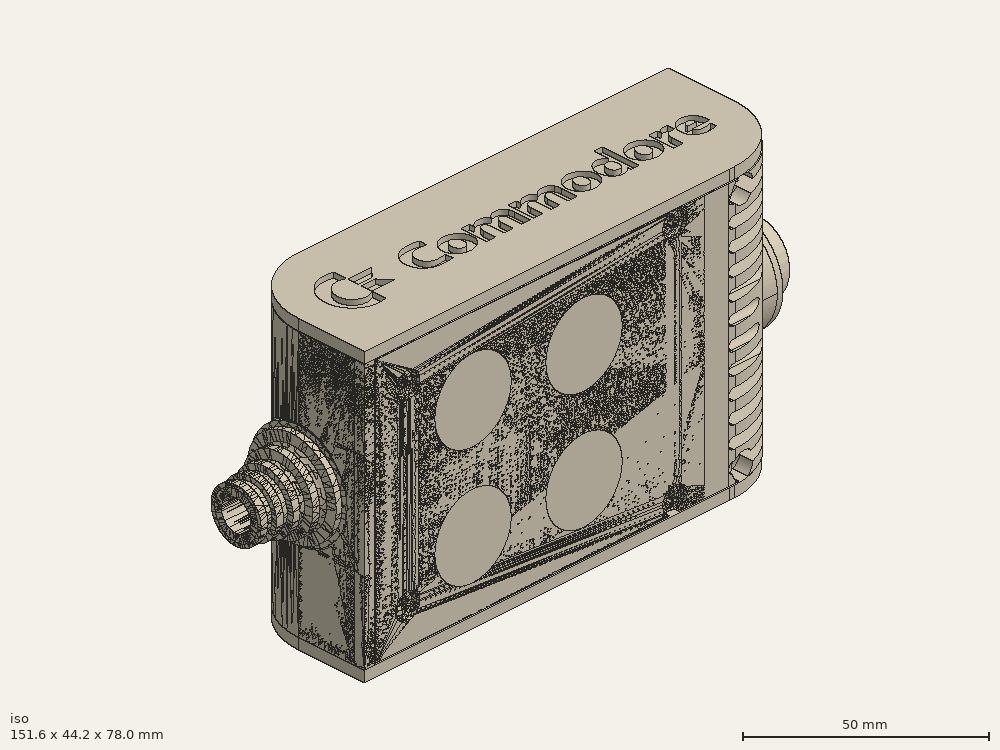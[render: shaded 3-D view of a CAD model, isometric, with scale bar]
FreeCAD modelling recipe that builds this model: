
FCSTD DOCUMENT  (FreeCAD 0.19R0.19.2)
Label: enclosure_215FCStd
License: All rights reserved
LicenseURL: http://en.wikipedia.org/wiki/All_rights_reserved
objects: Part::Revolution×152, Part::MultiFuse×146, Part::Feature×146, Sketcher::SketchObject×88, Part::Extrusion×73, Part::Cut×72, Part::Cylinder×70, Part::Fillet×58, Part::Box×36, App::MeasureDistance×4, Part::Chamfer×4, Part::FeaturePython×2, Image::ImagePlane×1, PartDesign::Body×1, Part::Mirroring×1
note: 849 computed .brp shape members not serialized (recipe doc carries the construction recipe); baked Part::Feature solids carry a one-line shape summary decoded from their .brp

FEATURE [Sketcher::SketchObject] Sketch  label="topSketch"
  FullyConstrained = true
  sketch-geometry (20):
    g0: LineSegment StartX=5.21097e-06 StartY=3 StartZ=0 EndX=5.21097e-06 EndY=19 EndZ=0
    g1: ArcOfCircle CenterX=19 CenterY=19 CenterZ=0 NormalX=0 NormalY=0 NormalZ=1 AngleXU=0 Radius=19 StartAngle=1.5708 EndAngle=3.14159
    g2: ArcOfCircle CenterX=19 CenterY=19 CenterZ=0 NormalX=0 NormalY=0 NormalZ=1 AngleXU=0 Radius=16 StartAngle=1.5708 EndAngle=3.14159
    g3: LineSegment StartX=114 StartY=35 StartZ=0 EndX=19 EndY=35 EndZ=0
    g4: LineSegment StartX=5.21097e-06 StartY=3 StartZ=0 EndX=5.21097e-06 EndY=0 EndZ=0
    g5: LineSegment StartX=3 StartY=0 StartZ=0 EndX=5.21097e-06 EndY=0 EndZ=0
    g6: LineSegment StartX=3 StartY=19 StartZ=0 EndX=3 EndY=0 EndZ=0
    g7: LineSegment StartX=19 StartY=38 StartZ=0 EndX=124 EndY=38 EndZ=0
    g8: Circle CenterX=119 CenterY=35 CenterZ=0 NormalX=0 NormalY=0 NormalZ=1 AngleXU=0 Radius=1
    g9: Circle CenterX=121 CenterY=35 CenterZ=0 NormalX=0 NormalY=0 NormalZ=1 AngleXU=0 Radius=1
    g10: Circle CenterX=121 CenterY=33 CenterZ=0 NormalX=0 NormalY=0 NormalZ=1 AngleXU=0 Radius=1
    g11: BSplineCurve PolesCount=3 KnotsCount=2 Degree=2 IsPeriodic=0
    g12: GeomPoint X=119 Y=35 Z=0
    g13: GeomPoint X=121 Y=33 Z=0
    g14: LineSegment StartX=119 StartY=35 StartZ=0 EndX=114 EndY=35 EndZ=0
    g15: ArcOfCircle CenterX=105 CenterY=19 CenterZ=0 NormalX=0 NormalY=0 NormalZ=1 AngleXU=0 Radius=19 StartAngle=5.7297 EndAngle=6.28319
    g16: ArcOfCircle CenterX=105 CenterY=19 CenterZ=0 NormalX=0 NormalY=0 NormalZ=1 AngleXU=0 Radius=16 StartAngle=5.60905 EndAngle=6.28319
    g17: LineSegment StartX=121 StartY=33 StartZ=0 EndX=121 EndY=19 EndZ=0
    g18: LineSegment StartX=124 StartY=38 StartZ=0 EndX=124 EndY=19 EndZ=0
    g19: LineSegment StartX=117.5 StartY=9.01251 StartZ=0 EndX=121.163 EndY=9.0125 EndZ=0
  constraints (46):
    c: Vertical(g0)
    c: Block(g0)
    c: Coincident(g1,g0)
    c: Block(g1)
    c: Coincident(g2,g1)
    c: Block(g2)
    c: Coincident(g3,g2)
    c: Horizontal(g3)
    c: Tangent(g3,g2)
    c: Coincident(g4,g0)
    c: Distance(g4) = 3
    c: Vertical(g4)
    c: Coincident(g5,g4)
    c: Horizontal(g5)
    c: Coincident(g6,g2)
    c: Coincident(g6,g5)
    c: Vertical(g6)
    c: Horizontal(g7)
    c: Distance(g7) = 105
    c: Coincident(g7,g1)
    c: Block(g3)
    c: Weight(g8) = 1
    c: Equal(g8,g9)
    c: Equal(g8,g10)
    c: InternalAlignment(g8,g11)
    c: InternalAlignment(g9,g11)
    c: InternalAlignment(g10,g11)
    c: InternalAlignment(g12,g11)
    c: InternalAlignment(g13,g11)
    c: Block(g11)
    c: Coincident(g14,g11)
    c: Coincident(g14,g3)
    c: Horizontal(g14)
    c: Block(g15)
    c: Coincident(g16,g15)
    c: Block(g16)
    c: Coincident(g17,g11)
    c: Coincident(g17,g16)
    c: Vertical(g17)
    c: Distance(g17) = 14
    c: Coincident(g18,g7)
    c: Coincident(g18,g15)
    c: Vertical(g18)
    c: Distance(g18) = 19
    c: Coincident(g19,g16)
    c: Coincident(g19,g15)
FEATURE [Sketcher::SketchObject] Sketch001  label="bottomSketch"
  FullyConstrained = true
  sketch-geometry (32):
    g0: LineSegment StartX=3.3 StartY=-6.03275e-07 StartZ=0 EndX=98 EndY=-6.03275e-07 EndZ=0
    g1: ArcOfCircle CenterX=98 CenterY=19 CenterZ=0 NormalX=0 NormalY=0 NormalZ=1 AngleXU=0 Radius=19 StartAngle=4.71239 EndAngle=5.71103
    g2: LineSegment StartX=6.3 StartY=8 StartZ=0 EndX=3.3 EndY=8 EndZ=0
    g3: LineSegment StartX=3.3 StartY=8 StartZ=0 EndX=3.3 EndY=-6.03275e-07 EndZ=0
    g4: ArcOfCircle CenterX=8.3 CenterY=5 CenterZ=0 NormalX=0 NormalY=0 NormalZ=1 AngleXU=0 Radius=2 StartAngle=3.14159 EndAngle=4.71239
    g5: LineSegment StartX=6.3 StartY=8 StartZ=0 EndX=6.3 EndY=5 EndZ=0
    g6: ArcOfCircle CenterX=98 CenterY=19 CenterZ=0 NormalX=0 NormalY=0 NormalZ=1 AngleXU=0 Radius=12.7 StartAngle=4.71239 EndAngle=6.28319
    g7: LineSegment StartX=94.7 StartY=3 StartZ=0 EndX=8.3 EndY=3 EndZ=0
    g8-g12: Circle x5 (B-spline internal-alignment scaffolding for g13; pole/knot coordinates omitted)
    g13: BSplineCurve PolesCount=5 KnotsCount=3 Degree=3 IsPeriodic=0
    g14: GeomPoint X=98 Y=6.3 Z=0
    g15: GeomPoint X=96.3938 Y=4.71946 Z=0
    g16: GeomPoint X=94.7 Y=3 Z=0
    g17-g23: Circle x7 (B-spline internal-alignment scaffolding for g24; pole/knot coordinates omitted)
    g24: BSplineCurve PolesCount=7 KnotsCount=5 Degree=3 IsPeriodic=0
    g25-g29: GeomPoint x5 (B-spline internal-alignment scaffolding for g24; pole/knot coordinates omitted)
    g30: ArcOfCircle CenterX=98 CenterY=19 CenterZ=0 NormalX=0 NormalY=0 NormalZ=1 AngleXU=0 Radius=15.7 StartAngle=5.81226 EndAngle=6.28319
    g31: LineSegment StartX=110.7 StartY=19 StartZ=0 EndX=113.7 EndY=19 EndZ=0
  constraints (41):
    c: Horizontal(g0)
    c: Coincident(g1,g0)
    c: Block(g1)
    c: Horizontal(g2)
    c: Distance(g2) = 3
    c: Coincident(g3,g2)
    c: Vertical(g3)
    c: Coincident(g3,g0)
    c: Block(g4)
    c: Block(g2)
    c: Coincident(g5,g2)
    c: Coincident(g5,g4)
    c: Vertical(g5)
    c: Coincident(g6,g1)
    c: Block(g6)
    c: Coincident(g7,g4)
    c: Horizontal(g7)
    c: Block(g0)
    c: Block(g7)
    c: Block(g3)
    c: Coincident(g13,g6)
    c: Weight(g8) = 1
    c: Equal(g8, g9-g12) x4
    c: Coincident(g13,g7)
    c: InternalAlignment(g8-g12 -> g13) x5
    c: InternalAlignment(g14,g13)
    c: InternalAlignment(g15,g13)
    c: InternalAlignment(g16,g13)
    c: Block(g13)
    c: Weight(g17) = 1
    c: Equal(g17, g18-g23) x6
    c: Coincident(g24,g1)
    c: InternalAlignment(g17-g23 -> g24) x7
    c: InternalAlignment(g25-g29 -> g24) x5
    c: Block(g24)
    c: Coincident(g30,g24)
    c: Coincident(g31,g6)
    c: Coincident(g31,g30)
    c: Horizontal(g31)
    c: Block(g31)
    c: Block(g30)
FEATURE [Part::Extrusion] Extrude  label="top"
  Base = -> Sketch
  Dir = (0,0,1)
  DirMode = 2
  FaceMakerClass = Part::FaceMakerBullseye
  LengthFwd = 72
  LengthRev = 0
  Solid = true
  Symmetric = false
FEATURE [Part::Extrusion] Extrude001  label="bottom"
  Base = -> Sketch001
  Dir = (0,0,1)
  DirMode = 2
  FaceMakerClass = Part::FaceMakerBullseye
  LengthFwd = 71.4
  LengthRev = 0
  Placement = pos=(0,0,0.3) rot=(0,0,1;0rad)
  Solid = true
  Symmetric = false
FEATURE [Sketcher::SketchObject] Sketch002  label="topSketch001"
  FullyConstrained = true
  sketch-geometry (8):
    g0: ArcOfCircle CenterX=19 CenterY=19.0975 CenterZ=0 NormalX=0 NormalY=0 NormalZ=1 AngleXU=0 Radius=18.9025 StartAngle=1.5708 EndAngle=3.14674
    g1: LineSegment StartX=0.0977805 StartY=19.0003 StartZ=0 EndX=0.0977805 EndY=0.000251602 EndZ=0
    g2: LineSegment StartX=19 StartY=38 StartZ=0 EndX=124 EndY=38 EndZ=0
    g3: LineSegment StartX=0.0977805 StartY=0.000251602 StartZ=0 EndX=105.098 EndY=0.000251602 EndZ=0
    g4: LineSegment StartX=124 StartY=38 StartZ=0 EndX=125.616 EndY=38 EndZ=0
    g5: LineSegment StartX=105.098 StartY=0.000251602 StartZ=0 EndX=106.713 EndY=0.000251602 EndZ=0
    g6: ArcOfCircle CenterX=106.616 CenterY=19 CenterZ=0 NormalX=0 NormalY=0 NormalZ=1 AngleXU=0 Radius=19 StartAngle=4.71754 EndAngle=6.28319
    g7: LineSegment StartX=125.616 StartY=38 StartZ=0 EndX=125.616 EndY=19 EndZ=0
  constraints (21):
    c: Block(g0)
    c: Coincident(g1,g0)
    c: Vertical(g1)
    c: Horizontal(g2)
    c: Distance(g2) = 105
    c: Coincident(g2,g0)
    c: Distance(g1) = 19
    c: Coincident(g3,g1)
    c: Horizontal(g3)
    c: Distance(g3) = 105
    c: Coincident(g4,g2)
    c: Horizontal(g4)
    c: Distance(g4) = 1.61553
    c: Horizontal(g5)
    c: Equal(g4,g5) = 1.61553
    c: Coincident(g5,g3)
    c: Block(g6)
    c: Coincident(g6,g5)
    c: Coincident(g7,g4)
    c: Coincident(g7,g6)
    c: Vertical(g7)
FEATURE [Part::Extrusion] Extrude002  label="sideA"
  Base = -> Sketch002
  Dir = (0,0,1)
  DirMode = 2
  FaceMakerClass = Part::FaceMakerBullseye
  LengthFwd = 3
  LengthRev = 0
  Placement = pos=(0,0,-3) rot=(0,0,1;0rad)
  Solid = true
  Symmetric = false
FEATURE [Sketcher::SketchObject] Sketch003  label="topSketch002"
  FullyConstrained = true
  sketch-geometry (6):
    g0: LineSegment StartX=19 StartY=38 StartZ=0 EndX=117 EndY=38 EndZ=0
    g1: ArcOfCircle CenterX=19 CenterY=19 CenterZ=0 NormalX=0 NormalY=0 NormalZ=1 AngleXU=0 Radius=19 StartAngle=1.5708 EndAngle=3.14159
    g2: LineSegment StartX=117 StartY=38 StartZ=0 EndX=117 EndY=19 EndZ=0
    g3: LineSegment StartX=98 StartY=1.0161e-12 StartZ=0 EndX=5.22862e-06 EndY=1.0161e-12 EndZ=0
    g4: LineSegment StartX=5.22862e-06 StartY=19 StartZ=0 EndX=5.22862e-06 EndY=1.0161e-12 EndZ=0
    g5: ArcOfCircle CenterX=98 CenterY=19 CenterZ=0 NormalX=0 NormalY=0 NormalZ=1 AngleXU=0 Radius=19 StartAngle=4.71239 EndAngle=6.28319
  constraints (16):
    c: Horizontal(g0)
    c: Distance(g0) = 98
    c: Coincident(g1,g0)
    c: Block(g1)
    c: Coincident(g2,g0)
    c: Vertical(g2)
    c: Distance(g2) = 19
    c: Horizontal(g3)
    c: Coincident(g4,g1)
    c: Vertical(g4)
    c: Coincident(g3,g4)
    c: Block(g3)
    c: Coincident(g5,g2)
    c: Coincident(g5,g3)
    c: Block(g0)
    c: Block(g5)
FEATURE [Sketcher::SketchObject] Sketch004
  FullyConstrained = true
  MapMode = 3
  Placement = pos=(0,0,0) rot=(1,0,0;1.5708rad)
  Support = -> [Extrude]
  sketch-geometry (8):
    g0: Circle CenterX=80.351 CenterY=-67.6202 CenterZ=0 NormalX=0 NormalY=0 NormalZ=1 AngleXU=0 Radius=2
    g1: Circle CenterX=80.351 CenterY=-67.6202 CenterZ=0 NormalX=0 NormalY=0 NormalZ=1 AngleXU=0 Radius=3
    g2: Circle CenterX=80.351 CenterY=-4.92017 CenterZ=0 NormalX=0 NormalY=0 NormalZ=1 AngleXU=0 Radius=2
    g3: Circle CenterX=80.351 CenterY=-4.92017 CenterZ=0 NormalX=0 NormalY=0 NormalZ=1 AngleXU=0 Radius=3
    g4: Circle CenterX=23.851 CenterY=-4.92017 CenterZ=0 NormalX=0 NormalY=0 NormalZ=1 AngleXU=0 Radius=2
    g5: Circle CenterX=23.851 CenterY=-4.92017 CenterZ=0 NormalX=0 NormalY=0 NormalZ=1 AngleXU=0 Radius=3
    g6: Circle CenterX=23.851 CenterY=-67.6202 CenterZ=0 NormalX=0 NormalY=0 NormalZ=1 AngleXU=0 Radius=2
    g7: Circle CenterX=23.851 CenterY=-67.6202 CenterZ=0 NormalX=0 NormalY=0 NormalZ=1 AngleXU=0 Radius=3
  constraints (8):
    c: Block(g3)
    c: Block(g2)
    c: Block(g1)
    c: Block(g0)
    c: Block(g6)
    c: Block(g7)
    c: Block(g4)
    c: Block(g5)
FEATURE [Part::Extrusion] Extrude004
  Base = -> Sketch004
  Dir = (0,-1,2e-16)
  DirMode = 2
  FaceMakerClass = Part::FaceMakerBullseye
  LengthFwd = 6
  LengthRev = 0
  Placement = pos=(0,9,0) rot=(0,0,1;0rad)
  Solid = true
  Symmetric = false
FEATURE [Sketcher::SketchObject] Sketch005
  FullyConstrained = true
  MapMode = 3
  Placement = pos=(0,0,0) rot=(1,0,0;1.5708rad)
  Support = -> [Extrude]
  sketch-geometry (8):
    g0: Circle CenterX=80.351 CenterY=-67.6202 CenterZ=0 NormalX=0 NormalY=0 NormalZ=1 AngleXU=0 Radius=3
    g1: Circle CenterX=80.351 CenterY=-4.92017 CenterZ=0 NormalX=0 NormalY=0 NormalZ=1 AngleXU=0 Radius=3
    g2: Circle CenterX=23.851 CenterY=-4.92017 CenterZ=0 NormalX=0 NormalY=0 NormalZ=1 AngleXU=0 Radius=3
    g3: Circle CenterX=23.851 CenterY=-67.6202 CenterZ=0 NormalX=0 NormalY=0 NormalZ=1 AngleXU=0 Radius=3
    g4: Circle CenterX=23.851 CenterY=-67.6202 CenterZ=0 NormalX=0 NormalY=0 NormalZ=1 AngleXU=0 Radius=5
    g5: Circle CenterX=80.351 CenterY=-67.6202 CenterZ=0 NormalX=0 NormalY=0 NormalZ=1 AngleXU=0 Radius=5
    g6: Circle CenterX=23.851 CenterY=-4.92017 CenterZ=0 NormalX=0 NormalY=0 NormalZ=1 AngleXU=0 Radius=5
    g7: Circle CenterX=80.351 CenterY=-4.92017 CenterZ=0 NormalX=0 NormalY=0 NormalZ=1 AngleXU=0 Radius=5
  constraints (8):
    c: Block(g1)
    c: Block(g0)
    c: Block(g3)
    c: Block(g2)
    c: Block(g5)
    c: Block(g4)
    c: Block(g6)
    c: Block(g7)
FEATURE [Part::Extrusion] Extrude005
  Base = -> Sketch005
  Dir = (0,-1,2e-16)
  DirMode = 2
  FaceMakerClass = Part::FaceMakerBullseye
  LengthFwd = 2
  LengthRev = 0
  Solid = true
  Symmetric = false
FEATURE [Sketcher::SketchObject] Sketch006
  FullyConstrained = true
  MapMode = 3
  Placement = pos=(0,0,0) rot=(1,0,0;1.5708rad)
  sketch-geometry (8):
    g0: Circle CenterX=80.351 CenterY=-67.6202 CenterZ=0 NormalX=0 NormalY=0 NormalZ=1 AngleXU=0 Radius=3
    g1: Circle CenterX=80.351 CenterY=-4.92017 CenterZ=0 NormalX=0 NormalY=0 NormalZ=1 AngleXU=0 Radius=3
    g2: Circle CenterX=23.851 CenterY=-4.92017 CenterZ=0 NormalX=0 NormalY=0 NormalZ=1 AngleXU=0 Radius=3
    g3: Circle CenterX=23.851 CenterY=-67.6202 CenterZ=0 NormalX=0 NormalY=0 NormalZ=1 AngleXU=0 Radius=3
    g4: Circle CenterX=23.851 CenterY=-67.6202 CenterZ=0 NormalX=0 NormalY=0 NormalZ=1 AngleXU=0 Radius=5
    g5: Circle CenterX=80.351 CenterY=-67.6202 CenterZ=0 NormalX=0 NormalY=0 NormalZ=1 AngleXU=0 Radius=5
    g6: Circle CenterX=23.851 CenterY=-4.92017 CenterZ=0 NormalX=0 NormalY=0 NormalZ=1 AngleXU=0 Radius=5
    g7: Circle CenterX=80.351 CenterY=-4.92017 CenterZ=0 NormalX=0 NormalY=0 NormalZ=1 AngleXU=0 Radius=5
  constraints (8):
    c: Block(g1)
    c: Block(g0)
    c: Block(g3)
    c: Block(g2)
    c: Block(g5)
    c: Block(g4)
    c: Block(g6)
    c: Block(g7)
FEATURE [Part::Extrusion] Extrude007
  Base = -> Sketch006
  Dir = (0,-1,2e-16)
  DirMode = 2
  FaceMakerClass = Part::FaceMakerBullseye
  LengthFwd = 2
  LengthRev = 0
  Solid = true
  Symmetric = false
FEATURE [Part::Fillet] Fillet
  Base = -> Extrude007
  Edges = 4 edges r=1.99: [Edge6,Edge12,Edge18,Edge24]
FEATURE [Part::Cut] Cut
  Base = -> Extrude005
  Placement = pos=(0,5,0) rot=(0,0,1;0rad)
  Tool = -> Fillet
FEATURE [Part::MultiFuse] Fusion  label="pCBScrews"
  Placement = pos=(-2.5,0,72.3) rot=(0,0,1;0rad)
  Shapes = -> [Extrude004,Cut]
FEATURE [App::MeasureDistance] Distance  label="Distance: 0.69 mm"
  Distance = 0.685967
  P1 = (24.0138,2.9647,0.3)
  P2 = (23.8901,3,-0.373787)
FEATURE [App::MeasureDistance] Distance001  label="Distance: 0.53 mm"
  Distance = 0.533607
  P1 = (80.2939,3,72.2334)
  P2 = (80.281,2.99661,71.7)
FEATURE [Part::Fillet] Fillet001
  Base = -> Extrude001
  Edges = 1 edges r=2.4: [Edge17]
FEATURE [Part::Fillet] Fillet002  label="bottom001"
  Base = -> Fillet001
  Edges = 1 edges r=2.4: [Edge36]
FEATURE [Part::Fillet] Fillet003  label="top001"
  Base = -> Extrude
  Edges = 1 edges r=2: [Edge1]
FEATURE [Sketcher::SketchObject] Sketch007
  FullyConstrained = true
  sketch-geometry (16):
    g0: LineSegment StartX=4 StartY=0 StartZ=0 EndX=4 EndY=2.4 EndZ=0
    g1: LineSegment StartX=4 StartY=2.4 StartZ=0 EndX=7 EndY=2.4 EndZ=0
    g2: LineSegment StartX=4 StartY=0 StartZ=0 EndX=5.7 EndY=0 EndZ=0
    g3: LineSegment StartX=5.7 StartY=0 StartZ=0 EndX=5.7 EndY=-5.6 EndZ=0
    g4-g8: Circle x5 (B-spline internal-alignment scaffolding for g9; pole/knot coordinates omitted)
    g9: BSplineCurve PolesCount=5 KnotsCount=3 Degree=3 IsPeriodic=0
    g10: GeomPoint X=7 Y=2.4 Z=0
    g11: GeomPoint X=10.4582 Y=-1.55472 Z=0
    g12: GeomPoint X=14 Y=-5.6 Z=0
    g13: LineSegment StartX=14 StartY=-5.6 StartZ=0 EndX=14 EndY=-14.1 EndZ=0
    g14: LineSegment StartX=14 StartY=-14.1 StartZ=0 EndX=6.5 EndY=-14.1 EndZ=0
    g15: LineSegment StartX=5.7 StartY=-5.6 StartZ=0 EndX=6.5 EndY=-14.1 EndZ=0
  constraints (28):
    c: Distance(g0) = 2.4
    c: Vertical(g0)
    c: Block(g0)
    c: Coincident(g1,g0)
    c: Horizontal(g1)
    c: Distance(g1) = 3
    c: Coincident(g2,g0)
    c: Horizontal(g2)
    c: Distance(g2) = 1.7
    c: Coincident(g3,g2)
    c: Vertical(g3)
    c: Distance(g3) = 5.6
    c: Coincident(g9,g1)
    c: Weight(g4) = 1
    c: Equal(g4, g5-g8) x4
    c: InternalAlignment(g4-g8 -> g9) x5
    c: InternalAlignment(g10,g9)
    c: InternalAlignment(g11,g9)
    c: InternalAlignment(g12,g9)
    c: Block(g9)
    c: Coincident(g13,g9)
    c: Vertical(g13)
    c: Distance(g13) = 8.5
    c: Coincident(g14,g13)
    c: Horizontal(g14)
    c: Distance(g14) = 7.5
    c: Coincident(g15,g3)
    c: Coincident(g15,g14)
FEATURE [Part::Feature] Face
  shape: bbox 10 x 16.5 x 2e-07 mm, 1 faces, 0 solids (baked)
FEATURE [Part::Revolution] Revolve  label="plugHousing"
  Angle = 360
  Axis = (0,1,0)
  Base = (0,0,0)
  FaceMakerClass = Part::FaceMakerBullseye
  Placement = pos=(0,0,36.15) rot=(0,0,1;0rad)
  Solid = false
  Source = -> Face
  Symmetric = false
FEATURE [Part::Feature] Face001
  shape: bbox 10 x 16.5 x 2e-07 mm, 1 faces, 0 solids (baked)
FEATURE [Part::Revolution] Revolve001  label="plugHousing001"
  Angle = 360
  Axis = (0,1,0)
  Base = (0,0,0)
  FaceMakerClass = Part::FaceMakerBullseye
  Placement = pos=(0,0,36.15) rot=(0,0,1;0rad)
  Solid = false
  Source = -> Face001
  Symmetric = false
FEATURE [Part::MultiFuse] Fusion001  label="plugHousing002"
  Placement = pos=(0,0,0) rot=(0,0,1;1.5708rad)
  Shapes = -> [Revolve001,Revolve]
FEATURE [Part::Feature] Face002
  shape: bbox 10 x 16.5 x 2e-07 mm, 1 faces, 0 solids (baked)
FEATURE [Part::Revolution] Revolve003  label="plugHousing005"
  Angle = 360
  Axis = (0,1,0)
  Base = (0,0,0)
  FaceMakerClass = Part::FaceMakerBullseye
  Placement = pos=(0,0,36.15) rot=(0,0,1;0rad)
  Solid = false
  Source = -> Face002
  Symmetric = false
FEATURE [Part::Feature] Face003
  shape: bbox 10 x 16.5 x 2e-07 mm, 1 faces, 0 solids (baked)
FEATURE [Part::Revolution] Revolve002  label="plugHousing003"
  Angle = 360
  Axis = (0,1,0)
  Base = (0,0,0)
  FaceMakerClass = Part::FaceMakerBullseye
  Placement = pos=(0,0,36.15) rot=(0,0,1;0rad)
  Solid = false
  Source = -> Face003
  Symmetric = false
FEATURE [Part::MultiFuse] Fusion002  label="plugHousing004"
  Placement = pos=(0,0,0) rot=(0,0,1;1.5708rad)
  Shapes = -> [Revolve002,Revolve003]
FEATURE [Part::MultiFuse] Fusion003  label="plugHousing006"
  Placement = pos=(0,19,0) rot=(0,0,1;3.14159rad)
  Shapes = -> [Fusion002,Fusion001]
FEATURE [Part::Feature] Face004
  shape: bbox 10 x 16.5 x 2e-07 mm, 1 faces, 0 solids (baked)
FEATURE [Part::Revolution] Revolve006  label="plugHousing010"
  Angle = 360
  Axis = (0,1,0)
  Base = (0,0,0)
  FaceMakerClass = Part::FaceMakerBullseye
  Placement = pos=(0,0,36.15) rot=(0,0,1;0rad)
  Solid = false
  Source = -> Face004
  Symmetric = false
FEATURE [Part::Feature] Face005
  shape: bbox 10 x 16.5 x 2e-07 mm, 1 faces, 0 solids (baked)
FEATURE [Part::Revolution] Revolve007  label="plugHousing011"
  Angle = 360
  Axis = (0,1,0)
  Base = (0,0,0)
  FaceMakerClass = Part::FaceMakerBullseye
  Placement = pos=(0,0,36.15) rot=(0,0,1;0rad)
  Solid = false
  Source = -> Face005
  Symmetric = false
FEATURE [Part::Feature] Face006
  shape: bbox 10 x 16.5 x 2e-07 mm, 1 faces, 0 solids (baked)
FEATURE [Part::Revolution] Revolve004  label="plugHousing007"
  Angle = 360
  Axis = (0,1,0)
  Base = (0,0,0)
  FaceMakerClass = Part::FaceMakerBullseye
  Placement = pos=(0,0,36.15) rot=(0,0,1;0rad)
  Solid = false
  Source = -> Face006
  Symmetric = false
FEATURE [Part::MultiFuse] Fusion004  label="plugHousing009"
  Placement = pos=(0,0,0) rot=(0,0,1;1.5708rad)
  Shapes = -> [Revolve004,Revolve007]
FEATURE [Part::Feature] Face007
  shape: bbox 10 x 16.5 x 2e-07 mm, 1 faces, 0 solids (baked)
FEATURE [Part::Revolution] Revolve005  label="plugHousing008"
  Angle = 360
  Axis = (0,1,0)
  Base = (0,0,0)
  FaceMakerClass = Part::FaceMakerBullseye
  Placement = pos=(0,0,36.15) rot=(0,0,1;0rad)
  Solid = false
  Source = -> Face007
  Symmetric = false
FEATURE [Part::MultiFuse] Fusion005  label="plugHousing012"
  Placement = pos=(0,0,0) rot=(0,0,1;1.5708rad)
  Shapes = -> [Revolve006,Revolve005]
FEATURE [Part::MultiFuse] Fusion006  label="plugHousing013"
  Placement = pos=(0,19,0) rot=(0,0,1;3.14159rad)
  Shapes = -> [Fusion005,Fusion004]
FEATURE [Part::MultiFuse] Fusion007  label="plugHousing014"
  Placement = pos=(122.621,0,-0.15) rot=(0,0,1;0rad)
  Shapes = -> [Fusion003,Fusion006]
FEATURE [Part::Cylinder] Cylinder002
  Angle = 360
  AttacherType = Attacher::AttachEngine3D
  Height = 20
  Placement = pos=(0,0,36.15) rot=(0,0,1;0rad)
  Radius = 4
FEATURE [Part::Cylinder] Cylinder003
  Angle = 360
  AttacherType = Attacher::AttachEngine3D
  Height = 10
  Placement = pos=(0,0,36.15) rot=(0,0,1;0rad)
  Radius = 4
FEATURE [Part::MultiFuse] Fusion009  label="removeToCreateHoleForPlugHousing"
  Placement = pos=(70,19,36.15) rot=(0,1,0;1.5708rad)
  Shapes = -> [Cylinder002,Cylinder003]
FEATURE [Part::Cylinder] Cylinder004
  Angle = 360
  AttacherType = Attacher::AttachEngine3D
  Height = 20
  Placement = pos=(0,0,36.15) rot=(0,0,1;0rad)
  Radius = 4
FEATURE [Part::Cylinder] Cylinder005
  Angle = 360
  AttacherType = Attacher::AttachEngine3D
  Height = 10
  Placement = pos=(0,0,36.15) rot=(0,0,1;0rad)
  Radius = 4
FEATURE [Part::MultiFuse] Fusion010  label="removeToCreateHoleForPlugHousing001"
  Placement = pos=(70,19,36.15) rot=(0,1,0;1.5708rad)
  Shapes = -> [Cylinder004,Cylinder005]
FEATURE [Part::Cut] Cut001
  Base = -> Fillet003
  Tool = -> Fusion010
FEATURE [Part::Cut] Cut002  label="Bottom"
  Base = -> Fillet002
  Tool = -> Fusion009
FEATURE [Part::Feature] Face008
  shape: bbox 10 x 16.5 x 2e-07 mm, 1 faces, 0 solids (baked)
FEATURE [Part::Revolution] Revolve011  label="plugHousing021"
  Angle = 360
  Axis = (0,1,0)
  Base = (0,0,0)
  FaceMakerClass = Part::FaceMakerBullseye
  Placement = pos=(0,0,36.15) rot=(0,0,1;0rad)
  Solid = false
  Source = -> Face008
  Symmetric = false
FEATURE [Part::Feature] Face009
  shape: bbox 10 x 16.5 x 2e-07 mm, 1 faces, 0 solids (baked)
FEATURE [Part::Revolution] Revolve012  label="plugHousing022"
  Angle = 360
  Axis = (0,1,0)
  Base = (0,0,0)
  FaceMakerClass = Part::FaceMakerBullseye
  Placement = pos=(0,0,36.15) rot=(0,0,1;0rad)
  Solid = false
  Source = -> Face009
  Symmetric = false
FEATURE [Part::Feature] Face010 .. Face013  x4 (patterned run collapsed; names and placements below)
  shape: bbox 10 x 16.5 x 2e-07 mm, 1 faces, 0 solids (baked)
FEATURE [Part::Revolution] Revolve015  label="plugHousing027"
  Angle = 360
  Axis = (0,1,0)
  Base = (0,0,0)
  FaceMakerClass = Part::FaceMakerBullseye
  Placement = pos=(0,0,36.15) rot=(0,0,1;0rad)
  Solid = false
  Source = -> Face013
  Symmetric = false
FEATURE [Part::Feature] Face014
  shape: bbox 10 x 16.5 x 2e-07 mm, 1 faces, 0 solids (baked)
FEATURE [Part::Feature] Face015
  shape: bbox 10 x 16.5 x 2e-07 mm, 1 faces, 0 solids (baked)
FEATURE [Part::Feature] Face016
  shape: bbox 10 x 16.5 x 2e-07 mm, 1 faces, 0 solids (baked)
FEATURE [Part::Revolution] Revolve019  label="plugHousing033"
  Angle = 360
  Axis = (0,1,0)
  Base = (0,0,0)
  FaceMakerClass = Part::FaceMakerBullseye
  Placement = pos=(0,0,36.15) rot=(0,0,1;0rad)
  Solid = false
  Source = -> Face016
  Symmetric = false
FEATURE [Part::Feature] Face017
  shape: bbox 10 x 16.5 x 2e-07 mm, 1 faces, 0 solids (baked)
FEATURE [Part::Revolution] Revolve020  label="plugHousing034"
  Angle = 360
  Axis = (0,1,0)
  Base = (0,0,0)
  FaceMakerClass = Part::FaceMakerBullseye
  Placement = pos=(0,0,36.15) rot=(0,0,1;0rad)
  Solid = false
  Source = -> Face017
  Symmetric = false
FEATURE [Part::Feature] Face018
  shape: bbox 10 x 16.5 x 2e-07 mm, 1 faces, 0 solids (baked)
FEATURE [Part::Revolution] Revolve016  label="plugHousing030"
  Angle = 360
  Axis = (0,1,0)
  Base = (0,0,0)
  FaceMakerClass = Part::FaceMakerBullseye
  Placement = pos=(0,0,36.15) rot=(0,0,1;0rad)
  Solid = false
  Source = -> Face018
  Symmetric = false
FEATURE [Part::MultiFuse] Fusion020  label="plugHousing038"
  Placement = pos=(0,0,0) rot=(0,0,1;1.5708rad)
  Shapes = -> [Revolve016,Revolve020]
FEATURE [Part::Feature] Face019
  shape: bbox 10 x 16.5 x 2e-07 mm, 1 faces, 0 solids (baked)
FEATURE [Part::Feature] Face020
  shape: bbox 10 x 16.5 x 2e-07 mm, 1 faces, 0 solids (baked)
FEATURE [Part::Revolution] Revolve017  label="plugHousing031"
  Angle = 360
  Axis = (0,1,0)
  Base = (0,0,0)
  FaceMakerClass = Part::FaceMakerBullseye
  Placement = pos=(0,0,36.15) rot=(0,0,1;0rad)
  Solid = false
  Source = -> Face020
  Symmetric = false
FEATURE [Part::MultiFuse] Fusion021  label="plugHousing039"
  Placement = pos=(0,0,0) rot=(0,0,1;1.5708rad)
  Shapes = -> [Revolve019,Revolve017]
FEATURE [Part::MultiFuse] Fusion023  label="plugHousing041"
  Placement = pos=(0,19,0) rot=(0,0,1;3.14159rad)
  Shapes = -> [Fusion021,Fusion020]
FEATURE [Part::Revolution] Revolve022  label="plugHousing043"
  Angle = 360
  Axis = (0,1,0)
  Base = (0,0,0)
  FaceMakerClass = Part::FaceMakerBullseye
  Placement = pos=(0,0,36.15) rot=(0,0,1;0rad)
  Solid = false
  Source = -> Face019
  Symmetric = false
FEATURE [Part::Feature] Face021
  shape: bbox 10 x 16.5 x 2e-07 mm, 1 faces, 0 solids (baked)
FEATURE [Part::Revolution] Revolve023  label="plugHousing044"
  Angle = 360
  Axis = (0,1,0)
  Base = (0,0,0)
  FaceMakerClass = Part::FaceMakerBullseye
  Placement = pos=(0,0,36.15) rot=(0,0,1;0rad)
  Solid = false
  Source = -> Face021
  Symmetric = false
FEATURE [Part::Feature] Face022
  shape: bbox 10 x 16.5 x 2e-07 mm, 1 faces, 0 solids (baked)
FEATURE [Part::Revolution] Revolve018  label="plugHousing032"
  Angle = 360
  Axis = (0,1,0)
  Base = (0,0,0)
  FaceMakerClass = Part::FaceMakerBullseye
  Placement = pos=(0,0,36.15) rot=(0,0,1;0rad)
  Solid = false
  Source = -> Face022
  Symmetric = false
FEATURE [Part::MultiFuse] Fusion022  label="plugHousing040"
  Placement = pos=(0,0,0) rot=(0,0,1;1.5708rad)
  Shapes = -> [Revolve018,Revolve023]
FEATURE [Part::Feature] Face023
  shape: bbox 10 x 16.5 x 2e-07 mm, 1 faces, 0 solids (baked)
FEATURE [Part::Revolution] Revolve021  label="plugHousing035"
  Angle = 360
  Axis = (0,1,0)
  Base = (0,0,0)
  FaceMakerClass = Part::FaceMakerBullseye
  Placement = pos=(0,0,36.15) rot=(0,0,1;0rad)
  Solid = false
  Source = -> Face023
  Symmetric = false
FEATURE [Part::MultiFuse] Fusion018  label="plugHousing036"
  Placement = pos=(0,0,0) rot=(0,0,1;1.5708rad)
  Shapes = -> [Revolve022,Revolve021]
FEATURE [Part::MultiFuse] Fusion019  label="plugHousing037"
  Placement = pos=(0,19,0) rot=(0,0,1;3.14159rad)
  Shapes = -> [Fusion018,Fusion022]
FEATURE [Part::MultiFuse] Fusion024  label="plugHousing042"
  Placement = pos=(122.621,0,-0.15) rot=(0,0,1;0rad)
  Shapes = -> [Fusion023,Fusion019]
FEATURE [Part::Cylinder] Cylinder006
  Angle = 360
  AttacherType = Attacher::AttachEngine3D
  Height = 20
  Placement = pos=(0,0,36.15) rot=(0,0,1;0rad)
  Radius = 14.3
FEATURE [Part::Cylinder] Cylinder007
  Angle = 360
  AttacherType = Attacher::AttachEngine3D
  Height = 10
  Placement = pos=(0,0,36.15) rot=(0,0,1;0rad)
  Radius = 4
FEATURE [Part::MultiFuse] Fusion026  label="removeToCreteHoleForPlugHousing"
  Placement = pos=(70,19,36) rot=(0,1,0;1.5708rad)
  Shapes = -> [Cylinder006,Cylinder007]
FEATURE [Part::Box] Box001  label="Cube001"
  AttacherType = Attacher::AttachEngine3D
  Height = 28
  Length = 3
  Placement = pos=(110.7,19,22) rot=(0,0,1;0rad)
  Width = 15.7
FEATURE [Part::Cut] Cut003  label="top002"
  Base = -> Cut001
  Tool = -> Fusion007
FEATURE [Part::Revolution] Revolve008  label="plugHousing015"
  Angle = 360
  Axis = (0,1,0)
  Base = (0,0,0)
  FaceMakerClass = Part::FaceMakerBullseye
  Placement = pos=(0,0,36.15) rot=(0,0,1;0rad)
  Solid = false
  Source = -> Face010
  Symmetric = false
FEATURE [Part::MultiFuse] Fusion013  label="plugHousing020"
  Placement = pos=(0,0,0) rot=(0,0,1;1.5708rad)
  Shapes = -> [Revolve008,Revolve012]
FEATURE [Part::Cut] Cut004  label="top003"
  Base = -> Cut003
  Placement = pos=(1,0,0) rot=(0,0,1;0rad)
  Tool = -> Fusion026
FEATURE [Part::Cylinder] Cylinder008
  Angle = 360
  AttacherType = Attacher::AttachEngine3D
  Height = 20
  Placement = pos=(0,0,36.15) rot=(0,0,1;0rad)
  Radius = 10.3
FEATURE [Part::Cylinder] Cylinder009
  Angle = 360
  AttacherType = Attacher::AttachEngine3D
  Height = 10
  Placement = pos=(0,0,36.15) rot=(0,0,1;0rad)
  Radius = 4
FEATURE [Part::MultiFuse] Fusion027  label="removeToCreteHoleForPlugHousing001"
  Placement = pos=(70,19,36) rot=(0,1,0;1.5708rad)
  Shapes = -> [Cylinder008,Cylinder009]
FEATURE [Part::Cut] Cut005  label="plugHousingTab"
  Base = -> Box001
  Tool = -> Fusion027
FEATURE [Part::MultiFuse] Fusion028  label="plugHousing045"
  Shapes = -> [Fusion024,Cut005]
FEATURE [Part::Box] Box002  label="Cube002"
  AttacherType = Attacher::AttachEngine3D
  Height = 28.8
  Length = 3
  Placement = pos=(107.3,28,21.6) rot=(0,0,1;0rad)
  Width = 7
FEATURE [Part::Box] Box003  label="Cube003"
  AttacherType = Attacher::AttachEngine3D
  Height = 3
  Length = 6.4
  Placement = pos=(107.3,28,18.6) rot=(0,0,1;0rad)
  Width = 7
FEATURE [Part::Box] Box004  label="Cube004"
  AttacherType = Attacher::AttachEngine3D
  Height = 3
  Length = 6.4
  Placement = pos=(107.3,28,50.4) rot=(0,0,1;0rad)
  Width = 7
FEATURE [Part::MultiFuse] Fusion029  label="plugHousingBracketHolder"
  Shapes = -> [Box004,Box002,Box003]
FEATURE [Part::Cylinder] Cylinder010
  Angle = 360
  AttacherType = Attacher::AttachEngine3D
  Height = 20
  Placement = pos=(0,0,36.15) rot=(0,0,1;0rad)
  Radius = 14.3
FEATURE [Part::Cylinder] Cylinder011
  Angle = 360
  AttacherType = Attacher::AttachEngine3D
  Height = 10
  Placement = pos=(0,0,36.15) rot=(0,0,1;0rad)
  Radius = 4
FEATURE [Part::MultiFuse] Fusion030  label="removeToCreteHoleForPlugHousing002"
  Placement = pos=(70,19,36) rot=(0,1,0;1.5708rad)
  Shapes = -> [Cylinder010,Cylinder011]
FEATURE [Part::Cut] Cut006  label="plugHousingBracketHolder001"
  Base = -> Fusion029
  Tool = -> Fusion030
FEATURE [Part::Cylinder] Cylinder012
  Angle = 360
  AttacherType = Attacher::AttachEngine3D
  Height = 20
  Placement = pos=(0,0,36.15) rot=(0,0,1;0rad)
  Radius = 7
FEATURE [Part::Cylinder] Cylinder013
  Angle = 360
  AttacherType = Attacher::AttachEngine3D
  Height = 10
  Placement = pos=(0,0,36.15) rot=(0,0,1;0rad)
  Radius = 4
FEATURE [Part::MultiFuse] Fusion032  label="removeToCreteHoleForPlugHousing003"
  Placement = pos=(70,19,36) rot=(0,1,0;1.5708rad)
  Shapes = -> [Cylinder012,Cylinder013]
FEATURE [Part::Cut] Cut007  label="bottom002"
  Base = -> Cut002
  Tool = -> Fusion032
FEATURE [Sketcher::SketchObject] Sketch008
  FullyConstrained = true
  sketch-geometry (54):
    g0: LineSegment StartX=-4.2 StartY=0 StartZ=0 EndX=-6.2 EndY=0 EndZ=0
    g1: LineSegment StartX=-14 StartY=-18 StartZ=0 EndX=-14 EndY=-26.5 EndZ=0
    g2: LineSegment StartX=-4.2 StartY=0 StartZ=0 EndX=-4.2 EndY=-13.4877 EndZ=0
    g3: Circle CenterX=-4.2 CenterY=-13.4877 CenterZ=0 NormalX=0 NormalY=0 NormalZ=1 AngleXU=0 Radius=1
    g4: Circle CenterX=-4.2 CenterY=-26.5 CenterZ=0 NormalX=0 NormalY=0 NormalZ=1 AngleXU=0 Radius=1
    g5: Circle CenterX=-8.2 CenterY=-26.5 CenterZ=0 NormalX=0 NormalY=0 NormalZ=1 AngleXU=0 Radius=1
    g6: BSplineCurve PolesCount=3 KnotsCount=2 Degree=2 IsPeriodic=0
    g7: GeomPoint X=-4.2 Y=-13.4877 Z=0
    g8: GeomPoint X=-8.2 Y=-26.5 Z=0
    g9: LineSegment StartX=-14 StartY=-26.5 StartZ=0 EndX=-8.2 EndY=-26.5 EndZ=0
    g10: LineSegment StartX=-10.15 StartY=-12 StartZ=0 EndX=-10.15 EndY=-14 EndZ=0
    g11: LineSegment StartX=-12.8401 StartY=-16 StartZ=0 EndX=-10.1571 EndY=-16 EndZ=0
    g12: LineSegment StartX=-10.15 StartY=-14 StartZ=0 EndX=-8.70761 EndY=-14 EndZ=0
    g13: LineSegment StartX=-12.8401 StartY=-16 StartZ=0 EndX=-12.8401 EndY=-17.6958 EndZ=0
    g14: LineSegment StartX=-10.15 StartY=-12 StartZ=0 EndX=-7.79258 EndY=-12 EndZ=0
    g15: Circle CenterX=-6.2215 CenterY=-2 CenterZ=0 NormalX=0 NormalY=0 NormalZ=1 AngleXU=0 Radius=1
    g16: Circle CenterX=-6.22762 CenterY=-2.58724 CenterZ=0 NormalX=0 NormalY=0 NormalZ=1 AngleXU=0 Radius=1
    g17: Circle CenterX=-6.32538 CenterY=-4 CenterZ=0 NormalX=0 NormalY=0 NormalZ=1 AngleXU=0 Radius=1
    g18: BSplineCurve PolesCount=3 KnotsCount=2 Degree=2 IsPeriodic=0
    g19: GeomPoint X=-6.2215 Y=-2 Z=0
    g20: GeomPoint X=-6.32538 Y=-4 Z=0
    g21: Circle CenterX=-6.48644 CenterY=-5.99526 CenterZ=0 NormalX=0 NormalY=0 NormalZ=1 AngleXU=0 Radius=1
    g22: Circle CenterX=-6.58486 CenterY=-6.99526 CenterZ=0 NormalX=0 NormalY=0 NormalZ=1 AngleXU=0 Radius=1
    g23: Circle CenterX=-6.77343 CenterY=-8 CenterZ=0 NormalX=0 NormalY=0 NormalZ=1 AngleXU=0 Radius=1
    g24: BSplineCurve PolesCount=3 KnotsCount=2 Degree=2 IsPeriodic=0
    g25: GeomPoint X=-6.48644 Y=-5.99526 Z=0
    g26: GeomPoint X=-6.77343 Y=-8 Z=0
    g27: Circle CenterX=-7.19003 CenterY=-10 CenterZ=0 NormalX=0 NormalY=0 NormalZ=1 AngleXU=0 Radius=1
    g28: Circle CenterX=-7.44407 CenterY=-11.0915 CenterZ=0 NormalX=0 NormalY=0 NormalZ=1 AngleXU=0 Radius=1
    g29: Circle CenterX=-7.79258 CenterY=-12 CenterZ=0 NormalX=0 NormalY=0 NormalZ=1 AngleXU=0 Radius=1
    g30: BSplineCurve PolesCount=3 KnotsCount=2 Degree=2 IsPeriodic=0
    g31: GeomPoint X=-7.19003 Y=-10 Z=0
    g32: GeomPoint X=-7.79258 Y=-12 Z=0
    g33: Circle CenterX=-8.70761 CenterY=-14 CenterZ=0 NormalX=0 NormalY=0 NormalZ=1 AngleXU=0 Radius=1
    g34: Circle CenterX=-9.33087 CenterY=-15.1837 CenterZ=0 NormalX=0 NormalY=0 NormalZ=1 AngleXU=0 Radius=1
    g35: Circle CenterX=-10.1571 CenterY=-16 CenterZ=0 NormalX=0 NormalY=0 NormalZ=1 AngleXU=0 Radius=1
    g36: BSplineCurve PolesCount=3 KnotsCount=2 Degree=2 IsPeriodic=0
    g37: GeomPoint X=-8.70761 Y=-14 Z=0
    g38: GeomPoint X=-10.1571 Y=-16 Z=0
    g39: Circle CenterX=-12.8401 CenterY=-17.6958 CenterZ=0 NormalX=0 NormalY=0 NormalZ=1 AngleXU=0 Radius=1
    g40: Circle CenterX=-13.3521 CenterY=-17.9027 CenterZ=0 NormalX=0 NormalY=0 NormalZ=1 AngleXU=0 Radius=1
    g41: Circle CenterX=-14 CenterY=-18 CenterZ=0 NormalX=0 NormalY=0 NormalZ=1 AngleXU=0 Radius=1
    g42: BSplineCurve PolesCount=3 KnotsCount=2 Degree=2 IsPeriodic=0
    g43: GeomPoint X=-12.8401 Y=-17.6958 Z=0
    g44: GeomPoint X=-14 Y=-18 Z=0
    g45: LineSegment StartX=-6.2 StartY=0 StartZ=0 EndX=-7.2 EndY=0 EndZ=0
    g46: LineSegment StartX=-7.2 StartY=0 StartZ=0 EndX=-7.2 EndY=-2 EndZ=0
    g47: LineSegment StartX=-7.2 StartY=-2 StartZ=0 EndX=-6.2215 EndY=-2 EndZ=0
    g48: LineSegment StartX=-6.32538 StartY=-4 StartZ=0 EndX=-7.65538 EndY=-4 EndZ=0
    g49: LineSegment StartX=-7.65538 StartY=-4 StartZ=0 EndX=-7.65538 EndY=-5.99526 EndZ=0
    g50: LineSegment StartX=-7.65538 StartY=-5.99526 StartZ=0 EndX=-6.48644 EndY=-5.99526 EndZ=0
    g51: LineSegment StartX=-6.77343 StartY=-8 StartZ=0 EndX=-8.43343 EndY=-8 EndZ=0
    g52: LineSegment StartX=-8.43343 StartY=-8 StartZ=0 EndX=-8.43343 EndY=-10 EndZ=0
    g53: LineSegment StartX=-8.43343 StartY=-10 StartZ=0 EndX=-7.19003 EndY=-10 EndZ=0
  constraints (112):
    c: Horizontal(g0)
    c: Distance(g0) = 2
    c: Block(g0)
    c: Vertical(g1)
    c: Coincident(g2,g0)
    c: Vertical(g2)
    c: Block(g2)
    c: Coincident(g6,g2)
    c: Weight(g3) = 1
    c: Equal(g3,g4)
    c: Equal(g3,g5)
    c: InternalAlignment(g3,g6)
    c: InternalAlignment(g4,g6)
    c: InternalAlignment(g5,g6)
    c: InternalAlignment(g7,g6)
    c: InternalAlignment(g8,g6)
    c: Block(g6)
    c: Coincident(g9,g1)
    c: Coincident(g9,g6)
    c: Horizontal(g9)
    c: Vertical(g10)
    c: Block(g10)
    c: Horizontal(g11)
    c: Block(g11)
    c: Coincident(g12,g10)
    c: Horizontal(g12)
    c: Block(g12)
    c: Coincident(g13,g11)
    c: Vertical(g13)
    c: Block(g13)
    c: Coincident(g14,g10)
    c: Horizontal(g14)
    c: Block(g14)
    c: Block(g9)
    c: Block(g1)
    c: Weight(g15) = 1
    c: Equal(g15,g16)
    c: Equal(g15,g17)
    c: InternalAlignment(g15,g18)
    c: InternalAlignment(g16,g18)
    c: InternalAlignment(g17,g18)
    c: InternalAlignment(g19,g18)
    c: InternalAlignment(g20,g18)
    c: Weight(g21) = 1
    c: Equal(g21,g22)
    c: Equal(g21,g23)
    c: InternalAlignment(g21,g24)
    c: InternalAlignment(g22,g24)
    c: InternalAlignment(g23,g24)
    c: InternalAlignment(g25,g24)
    c: InternalAlignment(g26,g24)
    c: Weight(g27) = 1
    c: Equal(g27,g28)
    c: Equal(g27,g29)
    c: Coincident(g30,g14)
    c: InternalAlignment(g27,g30)
    c: InternalAlignment(g28,g30)
    c: InternalAlignment(g29,g30)
    c: InternalAlignment(g31,g30)
    c: InternalAlignment(g32,g30)
    c: Coincident(g36,g12)
    c: Weight(g33) = 1
    c: Equal(g33,g34)
    c: Equal(g33,g35)
    c: Coincident(g36,g11)
    c: InternalAlignment(g33,g36)
    c: InternalAlignment(g34,g36)
    c: InternalAlignment(g35,g36)
    c: InternalAlignment(g37,g36)
    c: InternalAlignment(g38,g36)
    c: Coincident(g42,g13)
    c: Weight(g39) = 1
    c: Equal(g39,g40)
    c: Equal(g39,g41)
    c: Coincident(g42,g1)
    c: InternalAlignment(g39,g42)
    c: InternalAlignment(g40,g42)
    c: InternalAlignment(g41,g42)
    c: InternalAlignment(g43,g42)
    c: InternalAlignment(g44,g42)
    c: Block(g18)
    c: Block(g24)
    c: Block(g30)
    c: Block(g36)
    c: Block(g42)
    c: Horizontal(g45)
    c: Coincident(g45,g0)
    c: Vertical(g46)
    c: Coincident(g46,g45)
    c: Coincident(g47,g46)
    c: Coincident(g47,g18)
    c: Horizontal(g47)
    c: Block(g46)
    c: Coincident(g48,g18)
    c: Horizontal(g48)
    c: Distance(g48) = 1.33
    c: Vertical(g49)
    c: Coincident(g49,g48)
    c: Coincident(g50,g49)
    c: Coincident(g50,g24)
    c: Horizontal(g50)
    c: Tangent(g50,g22)
    c: Horizontal(g51)
    c: Coincident(g51,g24)
    c: Block(g51)
    c: Vertical(g52)
    c: Block(g52)
    c: Coincident(g52,g51)
    c: Coincident(g53,g52)
    c: Coincident(g53,g30)
    c: Horizontal(g53)
    c: Distance(g1) = 8.5
FEATURE [Part::Feature] Face024
  shape: bbox 9.8 x 26.5 x 2e-07 mm, 1 faces, 0 solids (baked)
FEATURE [Part::Revolution] Revolve024
  Angle = 360
  Axis = (0,1,0)
  Base = (0,0,0)
  FaceMakerClass = Part::FaceMakerBullseye
  Placement = pos=(0,0,0) rot=(0,0,1;1.5708rad)
  Solid = false
  Source = -> Face024
  Symmetric = false
FEATURE [Part::Feature] Face025
  shape: bbox 9.8 x 26.5 x 2e-07 mm, 1 faces, 0 solids (baked)
FEATURE [Part::Revolution] Revolve025
  Angle = 360
  Axis = (0,1,0)
  Base = (0,0,0)
  FaceMakerClass = Part::FaceMakerBullseye
  Placement = pos=(0,0,0) rot=(0,0,1;1.5708rad)
  Solid = false
  Source = -> Face025
  Symmetric = false
FEATURE [Part::MultiFuse] Fusion033
  Placement = pos=(-18,19,36) rot=(0,0,1;0rad)
  Shapes = -> [Revolve025,Revolve024]
FEATURE [Part::Cylinder] Cylinder014
  Angle = 360
  AttacherType = Attacher::AttachEngine3D
  Height = 20
  Placement = pos=(0,0,36.15) rot=(0,0,1;0rad)
  Radius = 14.3
FEATURE [Part::Cylinder] Cylinder015
  Angle = 360
  AttacherType = Attacher::AttachEngine3D
  Height = 10
  Placement = pos=(0,0,36.15) rot=(0,0,1;0rad)
  Radius = 4
FEATURE [Part::MultiFuse] Fusion034  label="removeToCreteHoleForPlugHousing004"
  Placement = pos=(-42,19,36) rot=(0,1,0;1.5708rad)
  Shapes = -> [Cylinder014,Cylinder015]
FEATURE [Part::Cut] Cut008  label="top004"
  Base = -> Cut004
  Placement = pos=(-1,0,0) rot=(0,0,1;0rad)
  Tool = -> Fusion034
FEATURE [Part::Box] Box005  label="Cube005"
  AttacherType = Attacher::AttachEngine3D
  Height = 28
  Length = 3
  Placement = pos=(110.7,19,22) rot=(0,0,1;0rad)
  Width = 15.7
FEATURE [Part::Cylinder] Cylinder016
  Angle = 360
  AttacherType = Attacher::AttachEngine3D
  Height = 10
  Placement = pos=(0,0,36.15) rot=(0,0,1;0rad)
  Radius = 4
FEATURE [Part::Cylinder] Cylinder017
  Angle = 360
  AttacherType = Attacher::AttachEngine3D
  Height = 20
  Placement = pos=(0,0,36.15) rot=(0,0,1;0rad)
  Radius = 10.3
FEATURE [Part::MultiFuse] Fusion035  label="removeToCreteHoleForPlugHousing005"
  Placement = pos=(70,19,36) rot=(0,1,0;1.5708rad)
  Shapes = -> [Cylinder017,Cylinder016]
FEATURE [Part::Cut] Cut009  label="plugHousingTab001"
  Base = -> Box005
  Placement = pos=(-107.4,-14,0) rot=(0,0,1;0rad)
  Tool = -> Fusion035
FEATURE [Part::Box] Box006  label="Cube006"
  AttacherType = Attacher::AttachEngine3D
  Height = 28
  Length = 3
  Placement = pos=(110.7,19,22) rot=(0,0,1;0rad)
  Width = 15.7
FEATURE [Part::Cylinder] Cylinder018
  Angle = 360
  AttacherType = Attacher::AttachEngine3D
  Height = 10
  Placement = pos=(0,0,36.15) rot=(0,0,1;0rad)
  Radius = 4
FEATURE [Part::Cylinder] Cylinder019
  Angle = 360
  AttacherType = Attacher::AttachEngine3D
  Height = 20
  Placement = pos=(0,0,36.15) rot=(0,0,1;0rad)
  Radius = 10.3
FEATURE [Part::MultiFuse] Fusion036  label="removeToCreteHoleForPlugHousing006"
  Placement = pos=(70,19,36) rot=(0,1,0;1.5708rad)
  Shapes = -> [Cylinder019,Cylinder018]
FEATURE [Part::Cut] Cut010  label="plugHousingTab002"
  Base = -> Box006
  Placement = pos=(-107.4,-14,0) rot=(0,0,1;0rad)
  Tool = -> Fusion036
FEATURE [Part::MultiFuse] Fusion037
  Placement = pos=(9.6,23,0) rot=(0,0,1;3.14159rad)
  Shapes = -> [Cut009,Cut010]
FEATURE [Part::Box] Box  label="Cube"
  AttacherType = Attacher::AttachEngine3D
  Height = 10
  Length = 3
  Placement = pos=(3.3,4,12) rot=(0,0,1;0rad)
  Width = 10
FEATURE [Part::Fillet] Fillet004
  Base = -> Fusion028
  Edges = 1 edges r=2: [Edge25]
FEATURE [Part::Fillet] Fillet005  label="plugHousing046"
  Base = -> Fillet004
  Edges = 1 edges r=2: [Edge8]
FEATURE [Part::Fillet] Fillet006
  Base = -> Box
  Edges = 1 edges r=2: [Edge11]
FEATURE [Part::Box] Box007  label="Cube007"
  AttacherType = Attacher::AttachEngine3D
  Height = 10
  Length = 3
  Placement = pos=(3.3,4,50) rot=(0,0,1;0rad)
  Width = 10
FEATURE [Part::Fillet] Fillet007
  Base = -> Box007
  Edges = 1 edges r=2: [Edge12]
FEATURE [Part::Box] Box008  label="Cube008"
  AttacherType = Attacher::AttachEngine3D
  Height = 28
  Length = 4
  Placement = pos=(5,0,22) rot=(0,0,1;0rad)
  Width = 10
FEATURE [Part::Fillet] Fillet008
  Base = -> Box008
  Edges = 1 edges r=1: [Edge7]
FEATURE [Part::Fillet] Fillet009
  Base = -> Fillet008
  Edges = 1 edges r=2: [Edge5]
FEATURE [Part::Fillet] Fillet010
  Base = -> Fillet009
  Edges = 1 edges r=2: [Edge2]
FEATURE [Sketcher::SketchObject] Sketch009  label="topSketch003"
  FullyConstrained = true
  sketch-geometry (4):
    g0: LineSegment StartX=16.8446 StartY=31.512 StartZ=0 EndX=16.3251 EndY=34.4666 EndZ=0
    g1: ArcOfCircle CenterX=19 CenterY=19.2524 CenterZ=0 NormalX=0 NormalY=0 NormalZ=1 AngleXU=0 Radius=15.4476 StartAngle=1.74483 EndAngle=2.72717
    g2: ArcOfCircle CenterX=19 CenterY=19.2524 CenterZ=0 NormalX=0 NormalY=0 NormalZ=1 AngleXU=0 Radius=12.4476 StartAngle=1.74483 EndAngle=2.73189
    g3: LineSegment StartX=4.86004 StartY=25.4725 StartZ=0 EndX=7.58253 EndY=24.2107 EndZ=0
  constraints (7):
    c: Block(g0)
    c: Coincident(g1,g0)
    c: Coincident(g2,g0)
    c: Coincident(g3,g1)
    c: Coincident(g3,g2)
    c: Block(g1)
    c: Block(g2)
FEATURE [Part::Extrusion] Extrude008
  Base = -> Sketch009
  Dir = (0,0,1)
  DirMode = 2
  FaceMakerClass = Part::FaceMakerBullseye
  LengthFwd = 10
  LengthRev = 0
  Placement = pos=(0,0,31) rot=(0,0,1;0rad)
  Solid = true
  Symmetric = false
FEATURE [Part::Cylinder] Cylinder020
  Angle = 360
  AttacherType = Attacher::AttachEngine3D
  Height = 20
  Placement = pos=(0,0,36.15) rot=(0,0,1;0rad)
  Radius = 8.2
FEATURE [Part::Cylinder] Cylinder021
  Angle = 360
  AttacherType = Attacher::AttachEngine3D
  Height = 10
  Placement = pos=(0,0,36.15) rot=(0,0,1;0rad)
  Radius = 4
FEATURE [Part::MultiFuse] Fusion038  label="removeToCreteHoleForPlugHousing007"
  Placement = pos=(-42,19,36) rot=(0,1,0;1.5708rad)
  Shapes = -> [Cylinder020,Cylinder021]
FEATURE [Part::Cut] Cut011
  Base = -> Extrude008
  Tool = -> Fusion038
FEATURE [Part::Fillet] Fillet011
  Base = -> Cut011
  Edges = 1 edges r=2: [Edge1]
FEATURE [Part::Fillet] Fillet012
  Base = -> Fillet011
  Edges = 1 edges r=2.5: [Edge1]
FEATURE [Part::Fillet] Fillet013
  Base = -> Fillet012
  Edges = 1 edges r=2.5: [Edge2]
FEATURE [Part::Box] Box010  label="Cube010"
  AttacherType = Attacher::AttachEngine3D
  Height = 16
  Length = 8
  Placement = pos=(12.7,31.52,28) rot=(0,0,1;0rad)
  Width = 4
FEATURE [Sketcher::SketchObject] Sketch010  label="topSketch004"
  FullyConstrained = true
  sketch-geometry (4):
    g0: LineSegment StartX=16.8446 StartY=31.512 StartZ=0 EndX=16.3251 EndY=34.4666 EndZ=0
    g1: ArcOfCircle CenterX=19 CenterY=19.2524 CenterZ=0 NormalX=0 NormalY=0 NormalZ=1 AngleXU=0 Radius=15.4476 StartAngle=1.74483 EndAngle=2.72717
    g2: ArcOfCircle CenterX=19 CenterY=19.2524 CenterZ=0 NormalX=0 NormalY=0 NormalZ=1 AngleXU=0 Radius=12.4476 StartAngle=1.74483 EndAngle=2.73189
    g3: LineSegment StartX=4.86004 StartY=25.4725 StartZ=0 EndX=7.58253 EndY=24.2107 EndZ=0
  constraints (7):
    c: Block(g0)
    c: Coincident(g1,g0)
    c: Coincident(g2,g0)
    c: Coincident(g3,g1)
    c: Coincident(g3,g2)
    c: Block(g1)
    c: Block(g2)
FEATURE [Part::Cylinder] Cylinder022
  Angle = 360
  AttacherType = Attacher::AttachEngine3D
  Height = 10
  Placement = pos=(0,0,36.15) rot=(0,0,1;0rad)
  Radius = 4
FEATURE [Sketcher::SketchObject] Sketch011  label="topSketch005"
  FullyConstrained = true
  sketch-geometry (4):
    g0: LineSegment StartX=16.8446 StartY=31.512 StartZ=0 EndX=16.3251 EndY=34.4666 EndZ=0
    g1: ArcOfCircle CenterX=19 CenterY=19.2524 CenterZ=0 NormalX=0 NormalY=0 NormalZ=1 AngleXU=0 Radius=15.4476 StartAngle=1.74483 EndAngle=2.72717
    g2: ArcOfCircle CenterX=19 CenterY=19.2524 CenterZ=0 NormalX=0 NormalY=0 NormalZ=1 AngleXU=0 Radius=12.4476 StartAngle=1.74483 EndAngle=2.73189
    g3: LineSegment StartX=4.86004 StartY=25.4725 StartZ=0 EndX=7.58253 EndY=24.2107 EndZ=0
  constraints (7):
    c: Block(g0)
    c: Coincident(g1,g0)
    c: Coincident(g2,g0)
    c: Coincident(g3,g1)
    c: Coincident(g3,g2)
    c: Block(g1)
    c: Block(g2)
FEATURE [Part::Extrusion] Extrude010
  Base = -> Sketch011
  Dir = (0,0,1)
  DirMode = 2
  FaceMakerClass = Part::FaceMakerBullseye
  LengthFwd = 10.6
  LengthRev = 0
  Placement = pos=(0,0,31) rot=(0,0,1;0rad)
  Solid = true
  Symmetric = false
FEATURE [Part::Cylinder] Cylinder023
  Angle = 360
  AttacherType = Attacher::AttachEngine3D
  Height = 20
  Placement = pos=(0,0,36.15) rot=(0,0,1;0rad)
  Radius = 8.2
FEATURE [Part::MultiFuse] Fusion039  label="removeToCreteHoleForPlugHousing008"
  Placement = pos=(-42,19,36) rot=(0,1,0;1.5708rad)
  Shapes = -> [Cylinder023,Cylinder022]
FEATURE [Part::Cut] Cut012
  Base = -> Extrude010
  Placement = pos=(0,0,-0.3) rot=(0,0,1;0rad)
  Tool = -> Fusion039
FEATURE [Part::Cut] Cut013
  Base = -> Box010
  Tool = -> Cut012
FEATURE [Part::Fillet] Fillet014
  Base = -> Cut013
  Edges = 1 edges r=0.7: [Edge13]
FEATURE [Part::Fillet] Fillet015
  Base = -> Fillet014
  Edges = 1 edges r=0.7: [Edge13]
FEATURE [Part::Fillet] Fillet016
  Base = -> Fillet015
  Edges = 1 edges r=0.7: [Edge16]
FEATURE [Part::Fillet] Fillet017
  Base = -> Fillet016
  Edges = 1 edges r=0.7: [Edge11]
FEATURE [Part::Fillet] Fillet018
  Base = -> Fillet017
  Edges = 1 edges r=0.7: [Edge10]
FEATURE [Part::Fillet] Fillet019
  Base = -> Fillet018
  Edges = 1 edges r=1.2: [Edge5]
FEATURE [Part::Fillet] Fillet020
  Base = -> Fillet019
  Edges = 1 edges r=1.2: [Edge12]
FEATURE [Part::Fillet] Fillet021
  Base = -> Fillet020
  Edges = 1 edges r=2: [Edge1]
  Placement = pos=(0.3,0,0) rot=(0,0,1;0rad)
FEATURE [Part::MultiFuse] Fusion040  label="top005"
  Shapes = -> [Cut008,Fillet021]
FEATURE [Part::MultiFuse] Fusion041  label="wireHolder"
  Shapes = -> [Fusion033,Fillet013]
FEATURE [Part::MultiFuse] Fusion042
  Shapes = -> [Fillet007,Fusion041]
FEATURE [Part::MultiFuse] Fusion043  label="wireHolder001"
  Shapes = -> [Fusion042,Fillet010]
FEATURE [Part::MultiFuse] Fusion044  label="wireHolder002"
  Shapes = -> [Fillet006,Fusion037,Fusion043]
FEATURE [Part::Feature] Face026
  shape: bbox 11 x 6 x 2e-07 mm, 1 faces, 0 solids (baked)
FEATURE [Part::Revolution] Revolve026
  Angle = 360
  Axis = (0,1,0)
  Base = (0,0,0)
  FaceMakerClass = Part::FaceMakerBullseye
  Placement = pos=(30.3,-1,19.7) rot=(0,0,1;0rad)
  Solid = false
  Source = -> Face026
  Symmetric = false
FEATURE [Sketcher::SketchObject] Sketch013  label="topSketch006"
  FullyConstrained = true
  sketch-geometry (13):
    g0: LineSegment StartX=117 StartY=19 StartZ=0 EndX=117 EndY=38 EndZ=0
    g1: ArcOfCircle CenterX=98 CenterY=19 CenterZ=0 NormalX=0 NormalY=0 NormalZ=1 AngleXU=0 Radius=19 StartAngle=5.7297 EndAngle=6.28319
    g2: LineSegment StartX=0 StartY=3 StartZ=0 EndX=0 EndY=19 EndZ=0
    g3: LineSegment StartX=19 StartY=38 StartZ=0 EndX=117 EndY=38 EndZ=0
    g4: ArcOfCircle CenterX=19 CenterY=19 CenterZ=0 NormalX=0 NormalY=0 NormalZ=1 AngleXU=0 Radius=19 StartAngle=1.5708 EndAngle=3.14159
    g5: ArcOfCircle CenterX=19 CenterY=19 CenterZ=0 NormalX=0 NormalY=0 NormalZ=1 AngleXU=0 Radius=16 StartAngle=1.5708 EndAngle=3.14159
    g6: ArcOfCircle CenterX=98 CenterY=19 CenterZ=0 NormalX=0 NormalY=0 NormalZ=1 AngleXU=0 Radius=16 StartAngle=5.60905 EndAngle=6.28319
    g7: LineSegment StartX=114 StartY=19 StartZ=0 EndX=114 EndY=35 EndZ=0
    g8: LineSegment StartX=110.5 StartY=9.01251 StartZ=0 EndX=114.163 EndY=9.01251 EndZ=0
    g9: LineSegment StartX=114 StartY=35 StartZ=0 EndX=19 EndY=35 EndZ=0
    g10: LineSegment StartX=0 StartY=3 StartZ=0 EndX=0 EndY=0 EndZ=0
    g11: LineSegment StartX=3 StartY=0 StartZ=0 EndX=0 EndY=0 EndZ=0
    g12: LineSegment StartX=3 StartY=19 StartZ=0 EndX=3 EndY=0 EndZ=0
  constraints (33):
    c: Vertical(g0)
    c: Distance(g0) = 19
    c: Block(g0)
    c: Coincident(g1,g0)
    c: Block(g1)
    c: Vertical(g2)
    c: Block(g2)
    c: Coincident(g3,g0)
    c: Horizontal(g3)
    c: Distance(g3) = 98
    c: Coincident(g4,g3)
    c: Coincident(g4,g2)
    c: Block(g4)
    c: Coincident(g5,g4)
    c: Coincident(g6,g1)
    c: Block(g6)
    c: Block(g5)
    c: Coincident(g7,g6)
    c: Vertical(g7)
    c: Coincident(g8,g6)
    c: Coincident(g8,g1)
    c: Coincident(g9,g7)
    c: Coincident(g9,g5)
    c: Horizontal(g9)
    c: Tangent(g9,g5)
    c: Coincident(g10,g2)
    c: Distance(g10) = 3
    c: Vertical(g10)
    c: Coincident(g11,g10)
    c: Horizontal(g11)
    c: Coincident(g12,g5)
    c: Coincident(g12,g11)
    c: Vertical(g12)
FEATURE [Part::Extrusion] Extrude011  label="top006"
  Base = -> Sketch013
  Dir = (0,0,1)
  DirMode = 2
  FaceMakerClass = Part::FaceMakerBullseye
  LengthFwd = 72
  LengthRev = 0
  Solid = true
  Symmetric = false
FEATURE [Sketcher::SketchObject] Sketch014
  FullyConstrained = true
  MapMode = 3
  Placement = pos=(0,0,0) rot=(1,0,0;1.5708rad)
  Support = -> [Extrude011]
  sketch-geometry (8):
    g0: Circle CenterX=80.351 CenterY=-67.6202 CenterZ=0 NormalX=0 NormalY=0 NormalZ=1 AngleXU=0 Radius=2
    g1: Circle CenterX=80.351 CenterY=-67.6202 CenterZ=0 NormalX=0 NormalY=0 NormalZ=1 AngleXU=0 Radius=3
    g2: Circle CenterX=80.351 CenterY=-4.92017 CenterZ=0 NormalX=0 NormalY=0 NormalZ=1 AngleXU=0 Radius=2
    g3: Circle CenterX=80.351 CenterY=-4.92017 CenterZ=0 NormalX=0 NormalY=0 NormalZ=1 AngleXU=0 Radius=3
    g4: Circle CenterX=23.851 CenterY=-4.92017 CenterZ=0 NormalX=0 NormalY=0 NormalZ=1 AngleXU=0 Radius=2
    g5: Circle CenterX=23.851 CenterY=-4.92017 CenterZ=0 NormalX=0 NormalY=0 NormalZ=1 AngleXU=0 Radius=3
    g6: Circle CenterX=23.851 CenterY=-67.6202 CenterZ=0 NormalX=0 NormalY=0 NormalZ=1 AngleXU=0 Radius=2
    g7: Circle CenterX=23.851 CenterY=-67.6202 CenterZ=0 NormalX=0 NormalY=0 NormalZ=1 AngleXU=0 Radius=3
  constraints (8):
    c: Block(g3)
    c: Block(g2)
    c: Block(g1)
    c: Block(g0)
    c: Block(g6)
    c: Block(g7)
    c: Block(g4)
    c: Block(g5)
FEATURE [Part::Feature] Face027
  shape: bbox 11 x 6 x 2e-07 mm, 1 faces, 0 solids (baked)
FEATURE [Part::Revolution] Revolve027
  Angle = 360
  Axis = (0,1,0)
  Base = (0,0,0)
  FaceMakerClass = Part::FaceMakerBullseye
  Placement = pos=(30.3,-1,51.7) rot=(0,0,1;0rad)
  Solid = false
  Source = -> Face027
  Symmetric = false
FEATURE [Part::Feature] Face028
  shape: bbox 11 x 6 x 2e-07 mm, 1 faces, 0 solids (baked)
FEATURE [Part::Revolution] Revolve028
  Angle = 360
  Axis = (0,1,0)
  Base = (0,0,0)
  FaceMakerClass = Part::FaceMakerBullseye
  Placement = pos=(62.3,-1,19.7) rot=(0,0,1;0rad)
  Solid = false
  Source = -> Face028
  Symmetric = false
FEATURE [Part::Feature] Face029
  shape: bbox 11 x 6 x 2e-07 mm, 1 faces, 0 solids (baked)
FEATURE [Part::Revolution] Revolve029
  Angle = 360
  Axis = (0,1,0)
  Base = (0,0,0)
  FaceMakerClass = Part::FaceMakerBullseye
  Placement = pos=(62.3,-1,51.7) rot=(0,0,1;0rad)
  Solid = false
  Source = -> Face029
  Symmetric = false
FEATURE [Part::Feature] Wire
  shape: bbox 11 x 5.2 x 2e-07 mm, 0 faces, 0 solids (baked)
FEATURE [Part::Revolution] Revolve030
  Angle = 360
  Axis = (0,1,0)
  Base = (0,0,0)
  FaceMakerClass = Part::FaceMakerBullseye
  Placement = pos=(30.3,38,19.7) rot=(0,0,1;0rad)
  Solid = true
  Source = -> Wire
  Symmetric = false
FEATURE [Part::Feature] Wire001
  shape: bbox 11 x 5.2 x 2e-07 mm, 0 faces, 0 solids (baked)
FEATURE [Part::Revolution] Revolve031
  Angle = 360
  Axis = (0,1,0)
  Base = (0,0,0)
  FaceMakerClass = Part::FaceMakerBullseye
  Placement = pos=(30.3,38,51.7) rot=(0,0,1;0rad)
  Solid = true
  Source = -> Wire001
  Symmetric = false
FEATURE [Part::Feature] Wire002
  shape: bbox 11 x 5.2 x 2e-07 mm, 0 faces, 0 solids (baked)
FEATURE [Part::Revolution] Revolve032
  Angle = 360
  Axis = (0,1,0)
  Base = (0,0,0)
  FaceMakerClass = Part::FaceMakerBullseye
  Placement = pos=(62.3,38,51.7) rot=(0,0,1;0rad)
  Solid = true
  Source = -> Wire002
  Symmetric = false
FEATURE [Part::Feature] Wire003
  shape: bbox 11 x 5.2 x 2e-07 mm, 0 faces, 0 solids (baked)
FEATURE [Part::Revolution] Revolve033
  Angle = 360
  Axis = (0,1,0)
  Base = (0,0,0)
  FaceMakerClass = Part::FaceMakerBullseye
  Placement = pos=(62.3,38,19.7) rot=(0,0,1;0rad)
  Solid = true
  Source = -> Wire003
  Symmetric = false
FEATURE [Part::MultiFuse] Fusion045  label="altRandScrewHousing"
  Shapes = -> [Revolve029,Revolve027,Revolve028,Revolve026]
FEATURE [Part::MultiFuse] Fusion046  label="fanScrewHousing"
  Shapes = -> [Revolve033,Revolve032,Revolve031,Revolve030]
FEATURE [Sketcher::SketchObject] Sketch015
  FullyConstrained = true
  sketch-geometry (17):
    g0: Circle CenterX=-3.5 CenterY=23.5 CenterZ=0 NormalX=0 NormalY=0 NormalZ=1 AngleXU=0 Radius=1
    g1: Circle CenterX=-1 CenterY=15.25 CenterZ=0 NormalX=0 NormalY=0 NormalZ=1 AngleXU=0 Radius=1
    g2: Circle CenterX=-3.5 CenterY=7 CenterZ=0 NormalX=0 NormalY=0 NormalZ=1 AngleXU=0 Radius=1
    g3: BSplineCurve PolesCount=3 KnotsCount=2 Degree=2 IsPeriodic=0
    g4: GeomPoint X=-3.5 Y=23.5 Z=0
    g5: GeomPoint X=-3.5 Y=7 Z=0
    g6: Circle CenterX=-4.8 CenterY=30.5 CenterZ=0 NormalX=0 NormalY=0 NormalZ=1 AngleXU=0 Radius=1
    g7: Circle CenterX=-3.5 CenterY=30.5 CenterZ=0 NormalX=0 NormalY=0 NormalZ=1 AngleXU=0 Radius=1
    g8: Circle CenterX=-3.5 CenterY=29.2 CenterZ=0 NormalX=0 NormalY=0 NormalZ=1 AngleXU=0 Radius=1
    g9: BSplineCurve PolesCount=3 KnotsCount=2 Degree=2 IsPeriodic=0
    g10: GeomPoint X=-4.8 Y=30.5 Z=0
    g11: GeomPoint X=-3.5 Y=29.2 Z=0
    g12: LineSegment StartX=-3.5 StartY=29.2 StartZ=0 EndX=-3.5 EndY=23.5 EndZ=0
    g13: LineSegment StartX=-4.8 StartY=30.5 StartZ=0 EndX=0 EndY=30.5 EndZ=0
    g14: LineSegment StartX=-3.5 StartY=0.3 StartZ=0 EndX=0 EndY=0.3 EndZ=0
    g15: LineSegment StartX=-3.5 StartY=0.3 StartZ=0 EndX=-3.5 EndY=7 EndZ=0
    g16: LineSegment StartX=0 StartY=0.3 StartZ=0 EndX=0 EndY=30.5 EndZ=0
  constraints (34):
    c: Weight(g0) = 1
    c: Equal(g0,g1)
    c: Equal(g0,g2)
    c: InternalAlignment(g0,g3)
    c: InternalAlignment(g1,g3)
    c: InternalAlignment(g2,g3)
    c: InternalAlignment(g4,g3)
    c: InternalAlignment(g5,g3)
    c: Block(g3)
    c: Weight(g6) = 1
    c: Equal(g6,g7)
    c: Equal(g6,g8)
    c: InternalAlignment(g6,g9)
    c: InternalAlignment(g7,g9)
    c: InternalAlignment(g8,g9)
    c: InternalAlignment(g10,g9)
    c: InternalAlignment(g11,g9)
    c: Block(g9)
    c: Coincident(g12,g9)
    c: Coincident(g12,g3)
    c: Vertical(g12)
    c: Coincident(g13,g9)
    c: Horizontal(g13)
    c: Distance(g13) = 4.8
    c: Horizontal(g14)
    c: Block(g14)
    c: Coincident(g15,g14)
    c: Coincident(g15,g3)
    c: Vertical(g15)
    c: Coincident(g16,g14)
    c: Coincident(g16,g13)
    c: Vertical(g16)
    c: Tangent(g16,g1)
    c: Distance(g14) = 3.5
FEATURE [Sketcher::SketchObject] Sketch016
  FullyConstrained = true
  sketch-geometry (16):
    g0: Circle CenterX=-3.5 CenterY=23.5 CenterZ=0 NormalX=0 NormalY=0 NormalZ=1 AngleXU=0 Radius=1
    g1: Circle CenterX=-1 CenterY=15.25 CenterZ=0 NormalX=0 NormalY=0 NormalZ=1 AngleXU=0 Radius=1
    g2: Circle CenterX=-3.5 CenterY=7 CenterZ=0 NormalX=0 NormalY=0 NormalZ=1 AngleXU=0 Radius=1
    g3: BSplineCurve PolesCount=3 KnotsCount=2 Degree=2 IsPeriodic=0
    g4: GeomPoint X=-3.5 Y=23.5 Z=0
    g5: GeomPoint X=-3.5 Y=7 Z=0
    g6: LineSegment StartX=-3.5 StartY=28.2 StartZ=0 EndX=-3.5 EndY=23.5 EndZ=0
    g7: LineSegment StartX=0 StartY=29.5 StartZ=0 EndX=0 EndY=30 EndZ=0
    g8: LineSegment StartX=-3.5 StartY=28.2 StartZ=0 EndX=-3.5 EndY=30 EndZ=0
    g9: LineSegment StartX=0 StartY=30 StartZ=0 EndX=0 EndY=30.5 EndZ=0
    g10: LineSegment StartX=0 StartY=30.5 StartZ=0 EndX=-3.5 EndY=30.5 EndZ=0
    g11: LineSegment StartX=-3.5 StartY=30.5 StartZ=0 EndX=-3.5 EndY=30 EndZ=0
    g12: LineSegment StartX=0 StartY=29.5 StartZ=0 EndX=0 EndY=5 EndZ=0
    g13: LineSegment StartX=-3.5 StartY=0.3 StartZ=0 EndX=-3.5 EndY=7 EndZ=0
    g14: LineSegment StartX=-3.5 StartY=0.3 StartZ=0 EndX=0 EndY=0.3 EndZ=0
    g15: LineSegment StartX=0 StartY=5 StartZ=0 EndX=0 EndY=0.3 EndZ=0
  constraints (39):
    c: Weight(g0) = 1
    c: Equal(g0,g1)
    c: Equal(g0,g2)
    c: InternalAlignment(g0,g3)
    c: InternalAlignment(g1,g3)
    c: InternalAlignment(g2,g3)
    c: InternalAlignment(g4,g3)
    c: InternalAlignment(g5,g3)
    c: Block(g3)
    c: Coincident(g6,g3)
    c: Vertical(g6)
    c: Vertical(g7)
    c: Distance(g7) = 0.5
    c: Coincident(g8,g6)
    c: Vertical(g8)
    c: Block(g6)
    c: Block(g7)
    c: Vertical(g9)
    c: Equal(g7,g9) = 0.5
    c: Block(g9)
    c: Coincident(g9,g7)
    c: Horizontal(g10)
    c: Coincident(g10,g9)
    c: Coincident(g11,g10)
    c: Coincident(g11,g8)
    c: Vertical(g11)
    c: Block(g11)
    c: Coincident(g12,g7)
    c: Vertical(g12)
    c: Coincident(g13,g3)
    c: Vertical(g13)
    c: Distance(g13) = 6.7
    c: Coincident(g14,g13)
    c: Horizontal(g14)
    c: Block(g14)
    c: Coincident(g15,g12)
    c: Coincident(g15,g14)
    c: Vertical(g15)
    c: Block(g15)
FEATURE [Sketcher::SketchObject] Sketch017
  FullyConstrained = true
  sketch-geometry (11):
    g0: LineSegment StartX=-3.5 StartY=1e-16 StartZ=0 EndX=-1.6 EndY=1e-16 EndZ=0
    g1: LineSegment StartX=-1.6 StartY=1e-16 StartZ=0 EndX=-1.6 EndY=1.5 EndZ=0
    g2: LineSegment StartX=-3.5 StartY=1.5 StartZ=0 EndX=-1.6 EndY=1.5 EndZ=0
    g3: LineSegment StartX=-3.5 StartY=1e-16 StartZ=0 EndX=-4.8 EndY=1e-16 EndZ=0
    g4: Circle CenterX=-3.5 CenterY=1.3 CenterZ=0 NormalX=0 NormalY=0 NormalZ=1 AngleXU=0 Radius=1
    g5: Circle CenterX=-3.5 CenterY=1e-16 CenterZ=0 NormalX=0 NormalY=0 NormalZ=1 AngleXU=0 Radius=1
    g6: Circle CenterX=-4.8 CenterY=1e-16 CenterZ=0 NormalX=0 NormalY=0 NormalZ=1 AngleXU=0 Radius=1
    g7: BSplineCurve PolesCount=3 KnotsCount=2 Degree=2 IsPeriodic=0
    g8: GeomPoint X=-3.5 Y=1.3 Z=0
    g9: GeomPoint X=-4.8 Y=1e-16 Z=0
    g10: LineSegment StartX=-3.5 StartY=1.3 StartZ=0 EndX=-3.5 EndY=1.5 EndZ=0
  constraints (24):
    c: Horizontal(g0)
    c: Distance(g0) = 1.9
    c: Block(g0)
    c: Coincident(g1,g0)
    c: Vertical(g1)
    c: Coincident(g2,g1)
    c: Horizontal(g2)
    c: Coincident(g3,g0)
    c: Horizontal(g3)
    c: Distance(g3) = 1.3
    c: Weight(g4) = 1
    c: Equal(g4,g5)
    c: Coincident(g5,g0)
    c: Equal(g4,g6)
    c: Coincident(g7,g3)
    c: InternalAlignment(g4,g7)
    c: InternalAlignment(g5,g7)
    c: InternalAlignment(g6,g7)
    c: InternalAlignment(g8,g7)
    c: InternalAlignment(g9,g7)
    c: Coincident(g10,g7)
    c: Coincident(g10,g2)
    c: Vertical(g10)
    c: Block(g10)
FEATURE [Part::Feature] Face035
  shape: bbox 3.2 x 1.5 x 2e-07 mm, 1 faces, 0 solids (baked)
FEATURE [Part::Revolution] Revolve039  label="backCaseScrewRetainer"
  Angle = 360
  Axis = (0,1,0)
  Base = (0,0,0)
  FaceMakerClass = Part::FaceMakerBullseye
  Placement = pos=(12.5,3,62) rot=(0,0,1;0rad)
  Solid = false
  Source = -> Face035
  Symmetric = false
FEATURE [Part::Feature] Face036
  shape: bbox 3.2 x 1.5 x 2e-07 mm, 1 faces, 0 solids (baked)
FEATURE [Part::Feature] Face039
  shape: bbox 4.8 x 30.2 x 2e-07 mm, 1 faces, 0 solids (baked)
FEATURE [Part::Revolution] Revolve043  label="frontCaseScrewPost002"
  Angle = 360
  Axis = (0,1,0)
  Base = (0,0,0)
  FaceMakerClass = Part::FaceMakerBullseye
  Placement = pos=(89.5,4.5,3.5) rot=(0,0,1;0rad)
  Solid = false
  Source = -> Face039
  Symmetric = false
FEATURE [Part::Feature] Face042
  shape: bbox 4.8 x 30.2 x 2e-07 mm, 1 faces, 0 solids (baked)
FEATURE [Part::Revolution] Revolve046  label="frontCaseScrewPost003"
  Angle = 360
  Axis = (0,1,0)
  Base = (0,0,0)
  FaceMakerClass = Part::FaceMakerBullseye
  Placement = pos=(89.5,4.5,68.5) rot=(0,0,1;0rad)
  Solid = false
  Source = -> Face042
  Symmetric = false
FEATURE [Part::Feature] Face043
  shape: bbox 3.2 x 1.5 x 2e-07 mm, 1 faces, 0 solids (baked)
FEATURE [Part::Revolution] Revolve047  label="frontCaseScrewRetainer002"
  Angle = 360
  Axis = (0,1,0)
  Base = (0,0,0)
  FaceMakerClass = Part::FaceMakerBullseye
  Placement = pos=(89.5,3,68.5) rot=(0,0,1;0rad)
  Solid = false
  Source = -> Face043
  Symmetric = false
FEATURE [Part::Feature] Face044
  shape: bbox 3.2 x 1.5 x 2e-07 mm, 1 faces, 0 solids (baked)
FEATURE [Part::Revolution] Revolve048  label="frontCaseScrewRetainer003"
  Angle = 360
  Axis = (0,1,0)
  Base = (0,0,0)
  FaceMakerClass = Part::FaceMakerBullseye
  Placement = pos=(89.5,3,3.5) rot=(0,0,1;0rad)
  Solid = false
  Source = -> Face044
  Symmetric = false
FEATURE [App::MeasureDistance] Distance002  label="Distance: 1.67 mm"
  Distance = 1.66921
  P1 = (99.2361,4.7524,71.7)
  P2 = (99.2347,6.42161,71.7)
FEATURE [Sketcher::SketchObject] Sketch018
  FullyConstrained = true
  sketch-geometry (7):
    g0: LineSegment StartX=0 StartY=0 StartZ=0 EndX=0 EndY=6 EndZ=0
    g1: Circle CenterX=0 CenterY=0 CenterZ=0 NormalX=0 NormalY=0 NormalZ=1 AngleXU=0 Radius=1
    g2: Circle CenterX=8 CenterY=6 CenterZ=0 NormalX=0 NormalY=0 NormalZ=1 AngleXU=0 Radius=1
    g3: BSplineCurve PolesCount=3 KnotsCount=2 Degree=2 IsPeriodic=0
    g4: GeomPoint X=0 Y=0 Z=0
    g5: GeomPoint X=8 Y=6 Z=0
    g6: LineSegment StartX=0 StartY=6 StartZ=0 EndX=8 EndY=6 EndZ=0
  constraints (14):
    c: Coincident(g0,g-1)
    c: Distance(g0) = 6
    c: Vertical(g0)
    c: Coincident(g3,g0)
    c: Weight(g1) = 1
    c: Equal(g1,g2)
    c: InternalAlignment(g1,g3)
    c: InternalAlignment(g2,g3)
    c: InternalAlignment(g4,g3)
    c: InternalAlignment(g5,g3)
    c: Block(g3)
    c: Coincident(g6,g0)
    c: Coincident(g6,g3)
    c: Horizontal(g6)
FEATURE [Part::Extrusion] Extrude012  label="caseScrewPillarBracket"
  Base = -> Sketch018
  Dir = (0,0,1)
  DirMode = 2
  FaceMakerClass = Part::FaceMakerBullseye
  LengthFwd = 2.4
  LengthRev = 0
  Placement = pos=(15.76,29,8.8) rot=(0,1,0;0rad)
  Solid = true
  Symmetric = false
FEATURE [Sketcher::SketchObject] Sketch019
  FullyConstrained = true
  sketch-geometry (7):
    g0: LineSegment StartX=0 StartY=0 StartZ=0 EndX=0 EndY=6 EndZ=0
    g1: Circle CenterX=0 CenterY=0 CenterZ=0 NormalX=0 NormalY=0 NormalZ=1 AngleXU=0 Radius=1
    g2: Circle CenterX=8 CenterY=6 CenterZ=0 NormalX=0 NormalY=0 NormalZ=1 AngleXU=0 Radius=1
    g3: BSplineCurve PolesCount=3 KnotsCount=2 Degree=2 IsPeriodic=0
    g4: GeomPoint X=0 Y=0 Z=0
    g5: GeomPoint X=8 Y=6 Z=0
    g6: LineSegment StartX=0 StartY=6 StartZ=0 EndX=8 EndY=6 EndZ=0
  constraints (14):
    c: Coincident(g0,g-1)
    c: Distance(g0) = 6
    c: Vertical(g0)
    c: Coincident(g3,g0)
    c: Weight(g1) = 1
    c: Equal(g1,g2)
    c: InternalAlignment(g1,g3)
    c: InternalAlignment(g2,g3)
    c: InternalAlignment(g4,g3)
    c: InternalAlignment(g5,g3)
    c: Block(g3)
    c: Coincident(g6,g0)
    c: Coincident(g6,g3)
    c: Horizontal(g6)
FEATURE [Part::Extrusion] Extrude013  label="caseScrewPillarBracket001"
  Base = -> Sketch019
  Dir = (0,0,1)
  DirMode = 2
  FaceMakerClass = Part::FaceMakerBullseye
  LengthFwd = 2.4
  LengthRev = 0
  Placement = pos=(15.76,29,60.8) rot=(0,0,1;0rad)
  Solid = true
  Symmetric = false
FEATURE [Sketcher::SketchObject] Sketch020
  FullyConstrained = true
  sketch-geometry (7):
    g0: LineSegment StartX=0 StartY=0 StartZ=0 EndX=0 EndY=6 EndZ=0
    g1: Circle CenterX=0 CenterY=0 CenterZ=0 NormalX=0 NormalY=0 NormalZ=1 AngleXU=0 Radius=1
    g2: Circle CenterX=8 CenterY=6 CenterZ=0 NormalX=0 NormalY=0 NormalZ=1 AngleXU=0 Radius=1
    g3: BSplineCurve PolesCount=3 KnotsCount=2 Degree=2 IsPeriodic=0
    g4: GeomPoint X=0 Y=0 Z=0
    g5: GeomPoint X=8 Y=6 Z=0
    g6: LineSegment StartX=0 StartY=6 StartZ=0 EndX=8 EndY=6 EndZ=0
  constraints (14):
    c: Coincident(g0,g-1)
    c: Distance(g0) = 6
    c: Vertical(g0)
    c: Coincident(g3,g0)
    c: Weight(g1) = 1
    c: Equal(g1,g2)
    c: InternalAlignment(g1,g3)
    c: InternalAlignment(g2,g3)
    c: InternalAlignment(g4,g3)
    c: InternalAlignment(g5,g3)
    c: Block(g3)
    c: Coincident(g6,g0)
    c: Coincident(g6,g3)
    c: Horizontal(g6)
FEATURE [Part::Extrusion] Extrude014  label="caseScrewPillarBracket002"
  Base = -> Sketch020
  Dir = (0,0,1)
  DirMode = 2
  FaceMakerClass = Part::FaceMakerBullseye
  LengthFwd = 2.4
  LengthRev = 0
  Placement = pos=(13.7,29,13.26) rot=(0,-1,0;1.5708rad)
  Solid = true
  Symmetric = false
FEATURE [Sketcher::SketchObject] Sketch021
  FullyConstrained = true
  sketch-geometry (7):
    g0: LineSegment StartX=0 StartY=0 StartZ=0 EndX=0 EndY=6 EndZ=0
    g1: Circle CenterX=0 CenterY=0 CenterZ=0 NormalX=0 NormalY=0 NormalZ=1 AngleXU=0 Radius=1
    g2: Circle CenterX=8 CenterY=6 CenterZ=0 NormalX=0 NormalY=0 NormalZ=1 AngleXU=0 Radius=1
    g3: BSplineCurve PolesCount=3 KnotsCount=2 Degree=2 IsPeriodic=0
    g4: GeomPoint X=0 Y=0 Z=0
    g5: GeomPoint X=8 Y=6 Z=0
    g6: LineSegment StartX=0 StartY=6 StartZ=0 EndX=8 EndY=6 EndZ=0
  constraints (14):
    c: Coincident(g0,g-1)
    c: Distance(g0) = 6
    c: Vertical(g0)
    c: Coincident(g3,g0)
    c: Weight(g1) = 1
    c: Equal(g1,g2)
    c: InternalAlignment(g1,g3)
    c: InternalAlignment(g2,g3)
    c: InternalAlignment(g4,g3)
    c: InternalAlignment(g5,g3)
    c: Block(g3)
    c: Coincident(g6,g0)
    c: Coincident(g6,g3)
    c: Horizontal(g6)
FEATURE [Part::Extrusion] Extrude015  label="caseScrewPillarBracket003"
  Base = -> Sketch021
  Dir = (0,0,1)
  DirMode = 2
  FaceMakerClass = Part::FaceMakerBullseye
  LengthFwd = 2.4
  LengthRev = 0
  Placement = pos=(11.3,29,58.74) rot=(0,1,0;1.5708rad)
  Solid = true
  Symmetric = false
FEATURE [Sketcher::SketchObject] Sketch022
  FullyConstrained = true
  sketch-geometry (7):
    g0: LineSegment StartX=0 StartY=0 StartZ=0 EndX=0 EndY=6 EndZ=0
    g1: Circle CenterX=0 CenterY=0 CenterZ=0 NormalX=0 NormalY=0 NormalZ=1 AngleXU=0 Radius=1
    g2: Circle CenterX=8 CenterY=6 CenterZ=0 NormalX=0 NormalY=0 NormalZ=1 AngleXU=0 Radius=1
    g3: BSplineCurve PolesCount=3 KnotsCount=2 Degree=2 IsPeriodic=0
    g4: GeomPoint X=0 Y=0 Z=0
    g5: GeomPoint X=8 Y=6 Z=0
    g6: LineSegment StartX=0 StartY=6 StartZ=0 EndX=8 EndY=6 EndZ=0
  constraints (14):
    c: Coincident(g0,g-1)
    c: Distance(g0) = 6
    c: Vertical(g0)
    c: Coincident(g3,g0)
    c: Weight(g1) = 1
    c: Equal(g1,g2)
    c: InternalAlignment(g1,g3)
    c: InternalAlignment(g2,g3)
    c: InternalAlignment(g4,g3)
    c: InternalAlignment(g5,g3)
    c: Block(g3)
    c: Coincident(g6,g0)
    c: Coincident(g6,g3)
    c: Horizontal(g6)
FEATURE [Part::Extrusion] Extrude016  label="caseScrewPillarBracket004"
  Base = -> Sketch022
  Dir = (0,0,1)
  DirMode = 2
  FaceMakerClass = Part::FaceMakerBullseye
  LengthFwd = 2.4
  LengthRev = 0
  Placement = pos=(88.3,29,65.23) rot=(0,1,0;1.5708rad)
  Solid = true
  Symmetric = false
FEATURE [Sketcher::SketchObject] Sketch023
  FullyConstrained = true
  sketch-geometry (7):
    g0: LineSegment StartX=0 StartY=0 StartZ=0 EndX=0 EndY=6 EndZ=0
    g1: Circle CenterX=0 CenterY=0 CenterZ=0 NormalX=0 NormalY=0 NormalZ=1 AngleXU=0 Radius=1
    g2: Circle CenterX=8 CenterY=6 CenterZ=0 NormalX=0 NormalY=0 NormalZ=1 AngleXU=0 Radius=1
    g3: BSplineCurve PolesCount=3 KnotsCount=2 Degree=2 IsPeriodic=0
    g4: GeomPoint X=0 Y=0 Z=0
    g5: GeomPoint X=8 Y=6 Z=0
    g6: LineSegment StartX=0 StartY=6 StartZ=0 EndX=8 EndY=6 EndZ=0
  constraints (14):
    c: Coincident(g0,g-1)
    c: Distance(g0) = 6
    c: Vertical(g0)
    c: Coincident(g3,g0)
    c: Weight(g1) = 1
    c: Equal(g1,g2)
    c: InternalAlignment(g1,g3)
    c: InternalAlignment(g2,g3)
    c: InternalAlignment(g4,g3)
    c: InternalAlignment(g5,g3)
    c: Block(g3)
    c: Coincident(g6,g0)
    c: Coincident(g6,g3)
    c: Horizontal(g6)
FEATURE [Part::Extrusion] Extrude017  label="caseScrewPillarBracket005"
  Base = -> Sketch023
  Dir = (0,0,1)
  DirMode = 2
  FaceMakerClass = Part::FaceMakerBullseye
  LengthFwd = 2.4
  LengthRev = 0
  Placement = pos=(90.7,29,6.77) rot=(0,-1,0;1.5708rad)
  Solid = true
  Symmetric = false
FEATURE [Sketcher::SketchObject] Sketch024
  FullyConstrained = true
  sketch-geometry (7):
    g0: LineSegment StartX=0 StartY=0 StartZ=0 EndX=0 EndY=6 EndZ=0
    g1: Circle CenterX=0 CenterY=0 CenterZ=0 NormalX=0 NormalY=0 NormalZ=1 AngleXU=0 Radius=1
    g2: Circle CenterX=8 CenterY=6 CenterZ=0 NormalX=0 NormalY=0 NormalZ=1 AngleXU=0 Radius=1
    g3: BSplineCurve PolesCount=3 KnotsCount=2 Degree=2 IsPeriodic=0
    g4: GeomPoint X=0 Y=0 Z=0
    g5: GeomPoint X=8 Y=6 Z=0
    g6: LineSegment StartX=0 StartY=6 StartZ=0 EndX=8 EndY=6 EndZ=0
  constraints (14):
    c: Coincident(g0,g-1)
    c: Distance(g0) = 6
    c: Vertical(g0)
    c: Coincident(g3,g0)
    c: Weight(g1) = 1
    c: Equal(g1,g2)
    c: InternalAlignment(g1,g3)
    c: InternalAlignment(g2,g3)
    c: InternalAlignment(g4,g3)
    c: InternalAlignment(g5,g3)
    c: Block(g3)
    c: Coincident(g6,g0)
    c: Coincident(g6,g3)
    c: Horizontal(g6)
FEATURE [Part::Extrusion] Extrude018  label="caseScrewPillarBracket006"
  Base = -> Sketch024
  Dir = (0,0,1)
  DirMode = 2
  FaceMakerClass = Part::FaceMakerBullseye
  LengthFwd = 2.4
  LengthRev = 0
  Placement = pos=(103.7,29,6.77) rot=(0,-1,0;1.5708rad)
  Solid = true
  Symmetric = false
FEATURE [Sketcher::SketchObject] Sketch025
  FullyConstrained = true
  sketch-geometry (7):
    g0: LineSegment StartX=0 StartY=0 StartZ=0 EndX=0 EndY=6 EndZ=0
    g1: Circle CenterX=0 CenterY=0 CenterZ=0 NormalX=0 NormalY=0 NormalZ=1 AngleXU=0 Radius=1
    g2: Circle CenterX=8 CenterY=6 CenterZ=0 NormalX=0 NormalY=0 NormalZ=1 AngleXU=0 Radius=1
    g3: BSplineCurve PolesCount=3 KnotsCount=2 Degree=2 IsPeriodic=0
    g4: GeomPoint X=0 Y=0 Z=0
    g5: GeomPoint X=8 Y=6 Z=0
    g6: LineSegment StartX=0 StartY=6 StartZ=0 EndX=8 EndY=6 EndZ=0
  constraints (14):
    c: Coincident(g0,g-1)
    c: Distance(g0) = 6
    c: Vertical(g0)
    c: Coincident(g3,g0)
    c: Weight(g1) = 1
    c: Equal(g1,g2)
    c: InternalAlignment(g1,g3)
    c: InternalAlignment(g2,g3)
    c: InternalAlignment(g4,g3)
    c: InternalAlignment(g5,g3)
    c: Block(g3)
    c: Coincident(g6,g0)
    c: Coincident(g6,g3)
    c: Horizontal(g6)
FEATURE [Part::Extrusion] Extrude019  label="caseScrewPillarBracket007"
  Base = -> Sketch025
  Dir = (0,0,1)
  DirMode = 2
  FaceMakerClass = Part::FaceMakerBullseye
  LengthFwd = 2.4
  LengthRev = 0
  Placement = pos=(101.3,29,65.23) rot=(0,1,0;1.5708rad)
  Solid = true
  Symmetric = false
FEATURE [Part::Box] Box011  label="frontCaseScrewPillarBracket"
  AttacherType = Attacher::AttachEngine3D
  Height = 2.4
  Length = 16
  Placement = pos=(87,28,2.3) rot=(0,0,1;0rad)
  Width = 7
FEATURE [Part::Box] Box012  label="frontCaseScrewPillarBracket001"
  AttacherType = Attacher::AttachEngine3D
  Height = 2.4
  Length = 16
  Placement = pos=(87,28,67.3) rot=(0,0,1;0rad)
  Width = 7
FEATURE [Sketcher::SketchObject] Sketch026
  FullyConstrained = true
  sketch-geometry (17):
    g0: Circle CenterX=-3.5 CenterY=23.5 CenterZ=0 NormalX=0 NormalY=0 NormalZ=1 AngleXU=0 Radius=1
    g1: Circle CenterX=-1 CenterY=15.25 CenterZ=0 NormalX=0 NormalY=0 NormalZ=1 AngleXU=0 Radius=1
    g2: Circle CenterX=-3.5 CenterY=7 CenterZ=0 NormalX=0 NormalY=0 NormalZ=1 AngleXU=0 Radius=1
    g3: BSplineCurve PolesCount=3 KnotsCount=2 Degree=2 IsPeriodic=0
    g4: GeomPoint X=-3.5 Y=23.5 Z=0
    g5: GeomPoint X=-3.5 Y=7 Z=0
    g6: Circle CenterX=-4.8 CenterY=30.5 CenterZ=0 NormalX=0 NormalY=0 NormalZ=1 AngleXU=0 Radius=1
    g7: Circle CenterX=-3.5 CenterY=30.5 CenterZ=0 NormalX=0 NormalY=0 NormalZ=1 AngleXU=0 Radius=1
    g8: Circle CenterX=-3.5 CenterY=29.2 CenterZ=0 NormalX=0 NormalY=0 NormalZ=1 AngleXU=0 Radius=1
    g9: BSplineCurve PolesCount=3 KnotsCount=2 Degree=2 IsPeriodic=0
    g10: GeomPoint X=-4.8 Y=30.5 Z=0
    g11: GeomPoint X=-3.5 Y=29.2 Z=0
    g12: LineSegment StartX=-3.5 StartY=29.2 StartZ=0 EndX=-3.5 EndY=23.5 EndZ=0
    g13: LineSegment StartX=-4.8 StartY=30.5 StartZ=0 EndX=0 EndY=30.5 EndZ=0
    g14: LineSegment StartX=-3.5 StartY=5 StartZ=0 EndX=-3.5 EndY=7 EndZ=0
    g15: LineSegment StartX=0 StartY=5 StartZ=0 EndX=0 EndY=30.5 EndZ=0
    g16: LineSegment StartX=-3.5 StartY=5 StartZ=0 EndX=0 EndY=5 EndZ=0
  constraints (33):
    c: Weight(g0) = 1
    c: Equal(g0,g1)
    c: Equal(g0,g2)
    c: InternalAlignment(g0,g3)
    c: InternalAlignment(g1,g3)
    c: InternalAlignment(g2,g3)
    c: InternalAlignment(g4,g3)
    c: InternalAlignment(g5,g3)
    c: Block(g3)
    c: Weight(g6) = 1
    c: Equal(g6,g7)
    c: Equal(g6,g8)
    c: InternalAlignment(g6,g9)
    c: InternalAlignment(g7,g9)
    c: InternalAlignment(g8,g9)
    c: InternalAlignment(g10,g9)
    c: InternalAlignment(g11,g9)
    c: Block(g9)
    c: Coincident(g12,g9)
    c: Coincident(g12,g3)
    c: Vertical(g12)
    c: Coincident(g13,g9)
    c: Horizontal(g13)
    c: Distance(g13) = 4.8
    c: Coincident(g14,g3)
    c: Vertical(g14)
    c: Coincident(g15,g13)
    c: Vertical(g15)
    c: Tangent(g15,g1)
    c: Distance(g14) = 2
    c: Coincident(g16,g14)
    c: Horizontal(g16)
    c: Coincident(g15,g16)
FEATURE [Part::Feature] Face050
  shape: bbox 4.8 x 25.5 x 2e-07 mm, 1 faces, 0 solids (baked)
FEATURE [Part::Revolution] Revolve054  label="moreFrontCaseScrewPost001"
  Angle = 360
  Axis = (0,1,0)
  Base = (0,0,0)
  FaceMakerClass = Part::FaceMakerBullseye
  Placement = pos=(102.5,4.5,3.5) rot=(0,0,1;0rad)
  Solid = false
  Source = -> Face050
  Symmetric = false
FEATURE [Part::Feature] Face051
  shape: bbox 4.8 x 25.5 x 2e-07 mm, 1 faces, 0 solids (baked)
FEATURE [Part::Revolution] Revolve055  label="moreFrontCaseScrewPost002"
  Angle = 360
  Axis = (0,1,0)
  Base = (0,0,0)
  FaceMakerClass = Part::FaceMakerBullseye
  Placement = pos=(102.5,4.5,68.5) rot=(0,0,1;0rad)
  Solid = false
  Source = -> Face051
  Symmetric = false
FEATURE [Sketcher::SketchObject] Sketch027
  FullyConstrained = true
  sketch-geometry (10):
    g0: LineSegment StartX=-1.6 StartY=4.7 StartZ=0 EndX=-1.6 EndY=1.7 EndZ=0
    g1: LineSegment StartX=-3.5 StartY=4.7 StartZ=0 EndX=-1.6 EndY=4.7 EndZ=0
    g2: LineSegment StartX=-1.6 StartY=1.7 StartZ=0 EndX=-1.6 EndY=1.5 EndZ=0
    g3: LineSegment StartX=-1.6 StartY=1.5 StartZ=0 EndX=-5.2 EndY=1.5 EndZ=0
    g4: Circle CenterX=-3.5 CenterY=4.7 CenterZ=0 NormalX=0 NormalY=0 NormalZ=1 AngleXU=0 Radius=1
    g5: Circle CenterX=-3.59627 CenterY=2.99743 CenterZ=0 NormalX=0 NormalY=0 NormalZ=1 AngleXU=0 Radius=1
    g6: Circle CenterX=-5.2 CenterY=1.5 CenterZ=0 NormalX=0 NormalY=0 NormalZ=1 AngleXU=0 Radius=1
    g7: BSplineCurve PolesCount=3 KnotsCount=2 Degree=2 IsPeriodic=0
    g8: GeomPoint X=-3.5 Y=4.7 Z=0
    g9: GeomPoint X=-5.2 Y=1.5 Z=0
  constraints (23):
    c: Vertical(g0)
    c: Distance(g0) = 3
    c: Coincident(g1,g0)
    c: Horizontal(g1)
    c: Block(g0)
    c: Block(g1)
    c: Coincident(g2,g0)
    c: Vertical(g2)
    c: Distance(g2) = 0.2
    c: Coincident(g3,g2)
    c: Horizontal(g3)
    c: Block(g3)
    c: Coincident(g7,g1)
    c: Weight(g4) = 1
    c: Equal(g4,g5)
    c: Equal(g4,g6)
    c: Coincident(g7,g3)
    c: InternalAlignment(g4,g7)
    c: InternalAlignment(g5,g7)
    c: InternalAlignment(g6,g7)
    c: InternalAlignment(g8,g7)
    c: InternalAlignment(g9,g7)
    c: Block(g7)
FEATURE [Sketcher::SketchObject] Sketch028
  FullyConstrained = true
  sketch-geometry (18):
    g0: LineSegment StartX=0 StartY=3e-16 StartZ=0 EndX=0 EndY=1.7 EndZ=0
    g1: LineSegment StartX=-3.5 StartY=0 StartZ=0 EndX=-3.5 EndY=0.9 EndZ=0
    g2: Circle CenterX=-2.7 CenterY=1.7 CenterZ=0 NormalX=0 NormalY=0 NormalZ=1 AngleXU=0 Radius=1
    g3: Circle CenterX=-3.5 CenterY=1.7 CenterZ=0 NormalX=0 NormalY=0 NormalZ=1 AngleXU=0 Radius=1
    g4: Circle CenterX=-3.5 CenterY=0.9 CenterZ=0 NormalX=0 NormalY=0 NormalZ=1 AngleXU=0 Radius=1
    g5: BSplineCurve PolesCount=3 KnotsCount=2 Degree=2 IsPeriodic=0
    g6: GeomPoint X=-2.7 Y=1.7 Z=0
    g7: GeomPoint X=-3.5 Y=0.9 Z=0
    g8: LineSegment StartX=-3.5 StartY=0 StartZ=0 EndX=-3.5 EndY=-7 EndZ=0
    g9: LineSegment StartX=0 StartY=3e-16 StartZ=0 EndX=0 EndY=-7 EndZ=0
    g10: LineSegment StartX=-3.5 StartY=-7 StartZ=0 EndX=0 EndY=-7 EndZ=0
    g11: LineSegment StartX=-2.7 StartY=1.7 StartZ=0 EndX=-1.6 EndY=1.7 EndZ=0
    g12: LineSegment StartX=0 StartY=1.7 StartZ=0 EndX=0 EndY=4.5 EndZ=0
    g13: LineSegment StartX=0 StartY=4.5 StartZ=0 EndX=0 EndY=10.8 EndZ=0
    g14: LineSegment StartX=0 StartY=10.8 StartZ=0 EndX=-2 EndY=10.8 EndZ=0
    g15: LineSegment StartX=-1.6 StartY=4.7 StartZ=0 EndX=-1.6 EndY=1.7 EndZ=0
    g16: LineSegment StartX=-1.6 StartY=4.7 StartZ=0 EndX=-2 EndY=4.7 EndZ=0
    g17: LineSegment StartX=-2 StartY=4.7 StartZ=0 EndX=-2 EndY=10.8 EndZ=0
  constraints (44):
    c: Vertical(g0)
    c: Vertical(g1)
    c: Distance(g1) = 0.9
    c: Block(g0)
    c: Distance(g0) = 1.7
    c: Weight(g2) = 1
    c: Equal(g2,g3)
    c: Equal(g2,g4)
    c: Coincident(g5,g1)
    c: InternalAlignment(g2,g5)
    c: InternalAlignment(g3,g5)
    c: InternalAlignment(g4,g5)
    c: InternalAlignment(g6,g5)
    c: InternalAlignment(g7,g5)
    c: Block(g5)
    c: Coincident(g8,g1)
    c: Vertical(g8)
    c: Distance(g8) = 7
    c: Vertical(g9)
    c: Equal(g8,g9) = 7
    c: Coincident(g9,g0)
    c: Coincident(g10,g8)
    c: Coincident(g10,g9)
    c: Horizontal(g10)
    c: Coincident(g11,g5)
    c: Horizontal(g11)
    c: Coincident(g12,g0)
    c: Vertical(g12)
    c: Distance(g12) = 2.8
    c: Coincident(g13,g12)
    c: Vertical(g13)
    c: Distance(g13) = 6.3
    c: Coincident(g14,g13)
    c: Horizontal(g14)
    c: Distance(g14) = 2
    c: Vertical(g15)
    c: Distance(g15) = 3
    c: Block(g11)
    c: Coincident(g15,g11)
    c: Coincident(g16,g15)
    c: Horizontal(g16)
    c: Coincident(g17,g16)
    c: Coincident(g17,g14)
    c: Vertical(g17)
FEATURE [Part::Revolution] Revolve040  label="backCaseScrewRetainer001"
  Angle = 360
  Axis = (0,1,0)
  Base = (0,0,0)
  FaceMakerClass = Part::FaceMakerBullseye
  Placement = pos=(12.5,3,10) rot=(0,0,1;0rad)
  Solid = false
  Source = -> Face036
  Symmetric = false
FEATURE [Part::Feature] Face055
  shape: bbox 3.5 x 30.2 x 2e-07 mm, 1 faces, 0 solids (baked)
FEATURE [Part::Revolution] Revolve059  label="backCaseScrewPost"
  Angle = 360
  Axis = (0,1,0)
  Base = (0,0,0)
  FaceMakerClass = Part::FaceMakerBullseye
  Placement = pos=(12.5,4.5,10) rot=(0,0,1;0rad)
  Solid = false
  Source = -> Face055
  Symmetric = false
FEATURE [Part::Feature] Face056
  shape: bbox 3.5 x 30.2 x 2e-07 mm, 1 faces, 0 solids (baked)
FEATURE [Part::Revolution] Revolve060  label="backCaseScrewPost001"
  Angle = 360
  Axis = (0,1,0)
  Base = (0,0,0)
  FaceMakerClass = Part::FaceMakerBullseye
  Placement = pos=(12.5,4.5,62) rot=(0,0,1;0rad)
  Solid = false
  Source = -> Face056
  Symmetric = false
FEATURE [Part::Feature] Face057
  shape: bbox 3.5 x 17.8 x 2e-07 mm, 1 faces, 0 solids (baked)
FEATURE [Part::Revolution] Revolve061  label="removeToCreateScrewAndThreadedInsertHole"
  Angle = 360
  Axis = (0,1,0)
  Base = (0,0,0)
  FaceMakerClass = Part::FaceMakerBullseye
  Placement = pos=(12.5,0,10) rot=(0,0,1;0rad)
  Solid = false
  Source = -> Face057
  Symmetric = false
FEATURE [Part::Feature] Face058
  shape: bbox 3.5 x 17.8 x 2e-07 mm, 1 faces, 0 solids (baked)
FEATURE [Part::Revolution] Revolve062  label="removeToCreateScrewAndThreadedInsertHole001"
  Angle = 360
  Axis = (0,1,0)
  Base = (0,0,0)
  FaceMakerClass = Part::FaceMakerBullseye
  Placement = pos=(12.5,0,62) rot=(0,0,1;0rad)
  Solid = false
  Source = -> Face058
  Symmetric = false
FEATURE [Part::Feature] Face059
  shape: bbox 3.5 x 17.8 x 2e-07 mm, 1 faces, 0 solids (baked)
FEATURE [Part::Revolution] Revolve063  label="removeToCreateScrewAndThreadedInsertHole002"
  Angle = 360
  Axis = (0,1,0)
  Base = (0,0,0)
  FaceMakerClass = Part::FaceMakerBullseye
  Placement = pos=(89.5,0,68.5) rot=(0,0,1;0rad)
  Solid = false
  Source = -> Face059
  Symmetric = false
FEATURE [Part::Feature] Face060
  shape: bbox 3.5 x 17.8 x 2e-07 mm, 1 faces, 0 solids (baked)
FEATURE [Part::Revolution] Revolve064  label="removeToCreateScrewAndThreadedInsertHole003"
  Angle = 360
  Axis = (0,1,0)
  Base = (0,0,0)
  FaceMakerClass = Part::FaceMakerBullseye
  Placement = pos=(89.5,0,3.5) rot=(0,0,1;0rad)
  Solid = false
  Source = -> Face060
  Symmetric = false
FEATURE [Part::Feature] Face061
  shape: bbox 3.5 x 17.8 x 2e-07 mm, 1 faces, 0 solids (baked)
FEATURE [Part::Revolution] Revolve065  label="removeToCreateScrewAndThreadedInsertHole004"
  Angle = 360
  Axis = (0,1,0)
  Base = (0,0,0)
  FaceMakerClass = Part::FaceMakerBullseye
  Placement = pos=(102.5,4.7,3.5) rot=(0,0,1;0rad)
  Solid = false
  Source = -> Face061
  Symmetric = false
FEATURE [Part::Feature] Face062
  shape: bbox 3.5 x 17.8 x 2e-07 mm, 1 faces, 0 solids (baked)
FEATURE [Part::Revolution] Revolve066  label="removeToCreateScrewAndThreadedInsertHole005"
  Angle = 360
  Axis = (0,1,0)
  Base = (0,0,0)
  FaceMakerClass = Part::FaceMakerBullseye
  Placement = pos=(102.5,4.7,68.5) rot=(0,0,1;0rad)
  Solid = false
  Source = -> Face062
  Symmetric = false
FEATURE [Part::MultiFuse] Fusion047  label="makeHoles"
  Shapes = -> [Revolve066,Revolve065,Revolve064,Revolve063,Revolve062,Revolve061]
FEATURE [Part::Feature] Face063
  shape: bbox 3.6 x 3.2 x 2e-07 mm, 1 faces, 0 solids (baked)
FEATURE [Part::Revolution] Revolve067  label="moreFrontCaseScrewRetainer002"
  Angle = 360
  Axis = (0,1,0)
  Base = (0,0,0)
  FaceMakerClass = Part::FaceMakerBullseye
  Placement = pos=(102.5,4.5,68.5) rot=(0,0,1;0rad)
  Solid = false
  Source = -> Face063
  Symmetric = false
FEATURE [Part::Feature] Face064
  shape: bbox 3.6 x 3.2 x 2e-07 mm, 1 faces, 0 solids (baked)
FEATURE [Part::Revolution] Revolve068  label="moreFrontCaseScrewRetainer003"
  Angle = 360
  Axis = (0,1,0)
  Base = (0,0,0)
  FaceMakerClass = Part::FaceMakerBullseye
  Placement = pos=(102.5,4.5,3.5) rot=(0,0,1;0rad)
  Solid = false
  Source = -> Face064
  Symmetric = false
FEATURE [Part::Feature] Face065
  shape: bbox 3.5 x 17.8 x 2e-07 mm, 1 faces, 0 solids (baked)
FEATURE [Part::Revolution] Revolve069  label="removeToCreateScrewAndThreadedInsertHole006"
  Angle = 360
  Axis = (0,1,0)
  Base = (0,0,0)
  FaceMakerClass = Part::FaceMakerBullseye
  Placement = pos=(12.5,0,10) rot=(0,0,1;0rad)
  Solid = false
  Source = -> Face065
  Symmetric = false
FEATURE [Part::Feature] Face066
  shape: bbox 3.5 x 17.8 x 2e-07 mm, 1 faces, 0 solids (baked)
FEATURE [Part::Revolution] Revolve070  label="removeToCreateScrewAndThreadedInsertHole007"
  Angle = 360
  Axis = (0,1,0)
  Base = (0,0,0)
  FaceMakerClass = Part::FaceMakerBullseye
  Placement = pos=(12.5,0,62) rot=(0,0,1;0rad)
  Solid = false
  Source = -> Face066
  Symmetric = false
FEATURE [Part::Feature] Face067
  shape: bbox 3.5 x 17.8 x 2e-07 mm, 1 faces, 0 solids (baked)
FEATURE [Part::Revolution] Revolve071  label="removeToCreateScrewAndThreadedInsertHole008"
  Angle = 360
  Axis = (0,1,0)
  Base = (0,0,0)
  FaceMakerClass = Part::FaceMakerBullseye
  Placement = pos=(89.5,0,68.5) rot=(0,0,1;0rad)
  Solid = false
  Source = -> Face067
  Symmetric = false
FEATURE [Part::Feature] Face068
  shape: bbox 3.5 x 17.8 x 2e-07 mm, 1 faces, 0 solids (baked)
FEATURE [Part::Revolution] Revolve072  label="removeToCreateScrewAndThreadedInsertHole009"
  Angle = 360
  Axis = (0,1,0)
  Base = (0,0,0)
  FaceMakerClass = Part::FaceMakerBullseye
  Placement = pos=(89.5,0,3.5) rot=(0,0,1;0rad)
  Solid = false
  Source = -> Face068
  Symmetric = false
FEATURE [Part::Feature] Face069
  shape: bbox 3.5 x 17.8 x 2e-07 mm, 1 faces, 0 solids (baked)
FEATURE [Part::Feature] Face070
  shape: bbox 3.5 x 17.8 x 2e-07 mm, 1 faces, 0 solids (baked)
FEATURE [Part::Revolution] Revolve073  label="removeToCreateScrewAndThreadedInsertHole010"
  Angle = 360
  Axis = (0,1,0)
  Base = (0,0,0)
  FaceMakerClass = Part::FaceMakerBullseye
  Placement = pos=(102.5,4.7,3.5) rot=(0,0,1;0rad)
  Solid = false
  Source = -> Face069
  Symmetric = false
FEATURE [Part::Revolution] Revolve074  label="removeToCreateScrewAndThreadedInsertHole011"
  Angle = 360
  Axis = (0,1,0)
  Base = (0,0,0)
  FaceMakerClass = Part::FaceMakerBullseye
  Placement = pos=(102.5,4.7,68.5) rot=(0,0,1;0rad)
  Solid = false
  Source = -> Face070
  Symmetric = false
FEATURE [Part::MultiFuse] Fusion048  label="makeHoles001"
  Shapes = -> [Revolve074,Revolve073,Revolve072,Revolve071,Revolve070,Revolve069]
FEATURE [Part::MultiFuse] Fusion049  label="caseScrewRetainers"
  Shapes = -> [Revolve067,Revolve068,Revolve048,Revolve047,Revolve039,Revolve040]
FEATURE [Part::Cut] Cut015  label="caseScrewRetainers001"
  Base = -> Fusion049
  Tool = -> Fusion048
FEATURE [Part::MultiFuse] Fusion050  label="casePillars"
  Shapes = -> [Revolve055,Revolve054,Revolve043,Revolve046,Revolve059,Revolve060]
FEATURE [Part::Feature] Face071 .. Face076  x6 (patterned run collapsed; names and placements below)
  shape: bbox 3.5 x 17.8 x 2e-07 mm, 1 faces, 0 solids (baked)
FEATURE [Part::Revolution] Revolve075  label="removeToCreateScrewAndThreadedInsertHole012"
  Angle = 360
  Axis = (0,1,0)
  Base = (0,0,0)
  FaceMakerClass = Part::FaceMakerBullseye
  Placement = pos=(12.5,0,10) rot=(0,0,1;0rad)
  Solid = false
  Source = -> Face071
  Symmetric = false
FEATURE [Part::Revolution] Revolve076  label="removeToCreateScrewAndThreadedInsertHole013"
  Angle = 360
  Axis = (0,1,0)
  Base = (0,0,0)
  FaceMakerClass = Part::FaceMakerBullseye
  Placement = pos=(12.5,0,62) rot=(0,0,1;0rad)
  Solid = false
  Source = -> Face072
  Symmetric = false
FEATURE [Part::Revolution] Revolve077  label="removeToCreateScrewAndThreadedInsertHole014"
  Angle = 360
  Axis = (0,1,0)
  Base = (0,0,0)
  FaceMakerClass = Part::FaceMakerBullseye
  Placement = pos=(89.5,0,68.5) rot=(0,0,1;0rad)
  Solid = false
  Source = -> Face073
  Symmetric = false
FEATURE [Part::Revolution] Revolve078  label="removeToCreateScrewAndThreadedInsertHole015"
  Angle = 360
  Axis = (0,1,0)
  Base = (0,0,0)
  FaceMakerClass = Part::FaceMakerBullseye
  Placement = pos=(89.5,0,3.5) rot=(0,0,1;0rad)
  Solid = false
  Source = -> Face074
  Symmetric = false
FEATURE [Part::Revolution] Revolve079  label="removeToCreateScrewAndThreadedInsertHole016"
  Angle = 360
  Axis = (0,1,0)
  Base = (0,0,0)
  FaceMakerClass = Part::FaceMakerBullseye
  Placement = pos=(102.5,4.7,3.5) rot=(0,0,1;0rad)
  Solid = false
  Source = -> Face075
  Symmetric = false
FEATURE [Part::Revolution] Revolve080  label="removeToCreateScrewAndThreadedInsertHole017"
  Angle = 360
  Axis = (0,1,0)
  Base = (0,0,0)
  FaceMakerClass = Part::FaceMakerBullseye
  Placement = pos=(102.5,4.7,68.5) rot=(0,0,1;0rad)
  Solid = false
  Source = -> Face076
  Symmetric = false
FEATURE [Part::MultiFuse] Fusion051  label="makeHoles002"
  Shapes = -> [Revolve080,Revolve079,Revolve078,Revolve077,Revolve076,Revolve075]
FEATURE [Part::Cut] Cut016  label="caesPillars"
  Base = -> Fusion050
  Tool = -> Fusion051
FEATURE [Part::Revolution] Revolve009  label="plugHousing016"
  Angle = 360
  Axis = (0,1,0)
  Base = (0,0,0)
  FaceMakerClass = Part::FaceMakerBullseye
  Placement = pos=(0,0,36.15) rot=(0,0,1;0rad)
  Solid = false
  Source = -> Face012
  Symmetric = false
FEATURE [Part::MultiFuse] Fusion014  label="plugHousing023"
  Placement = pos=(0,0,0) rot=(0,0,1;1.5708rad)
  Shapes = -> [Revolve011,Revolve009]
FEATURE [Part::Revolution] Revolve010  label="plugHousing017"
  Angle = 360
  Axis = (0,1,0)
  Base = (0,0,0)
  FaceMakerClass = Part::FaceMakerBullseye
  Placement = pos=(0,0,36.15) rot=(0,0,1;0rad)
  Solid = false
  Source = -> Face014
  Symmetric = false
FEATURE [Part::MultiFuse] Fusion015  label="plugHousing024"
  Placement = pos=(0,0,0) rot=(0,0,1;1.5708rad)
  Shapes = -> [Revolve010,Revolve015]
FEATURE [Part::Revolution] Revolve014  label="plugHousing026"
  Angle = 360
  Axis = (0,1,0)
  Base = (0,0,0)
  FaceMakerClass = Part::FaceMakerBullseye
  Placement = pos=(0,0,36.15) rot=(0,0,1;0rad)
  Solid = false
  Source = -> Face011
  Symmetric = false
FEATURE [Part::Revolution] Revolve013  label="plugHousing025"
  Angle = 360
  Axis = (0,1,0)
  Base = (0,0,0)
  FaceMakerClass = Part::FaceMakerBullseye
  Placement = pos=(0,0,36.15) rot=(0,0,1;0rad)
  Solid = false
  Source = -> Face015
  Symmetric = false
FEATURE [Part::MultiFuse] Fusion016  label="plugHousing028"
  Placement = pos=(0,19,0) rot=(0,0,1;3.14159rad)
  Shapes = -> [Fusion014,Fusion013]
FEATURE [Part::MultiFuse] Fusion011  label="plugHousing018"
  Placement = pos=(0,0,0) rot=(0,0,1;1.5708rad)
  Shapes = -> [Revolve014,Revolve013]
FEATURE [Part::MultiFuse] Fusion012  label="plugHousing019"
  Placement = pos=(0,19,0) rot=(0,0,1;3.14159rad)
  Shapes = -> [Fusion011,Fusion015]
FEATURE [Part::MultiFuse] Fusion017  label="plugHousing029"
  Placement = pos=(122.621,0,-0.15) rot=(0,0,1;0rad)
  Shapes = -> [Fusion016,Fusion012]
FEATURE [Part::MultiFuse] Fusion052  label="casePillarRetainers"
  Shapes = -> [Extrude012,Extrude013,Extrude014,Extrude015,Extrude016,Extrude017,Extrude018,Extrude019,Box011,Box012]
FEATURE [Part::Feature] Face077
  shape: bbox 3.5 x 17.8 x 2e-07 mm, 1 faces, 0 solids (baked)
FEATURE [Part::Revolution] Revolve081  label="removeToCreateScrewAndThreadedInsertHole018"
  Angle = 360
  Axis = (0,1,0)
  Base = (0,0,0)
  FaceMakerClass = Part::FaceMakerBullseye
  Placement = pos=(62.3,30.3,19.7) rot=(0,0,1;0rad)
  Solid = false
  Source = -> Face077
  Symmetric = false
FEATURE [Part::Feature] Face078
  shape: bbox 3.5 x 17.8 x 2e-07 mm, 1 faces, 0 solids (baked)
FEATURE [Part::Revolution] Revolve082  label="removeToCreateScrewAndThreadedInsertHole019"
  Angle = 360
  Axis = (0,1,0)
  Base = (0,0,0)
  FaceMakerClass = Part::FaceMakerBullseye
  Placement = pos=(62.3,30.3,51.7) rot=(0,0,1;0rad)
  Solid = false
  Source = -> Face078
  Symmetric = false
FEATURE [Part::Feature] Face079
  shape: bbox 3.5 x 17.8 x 2e-07 mm, 1 faces, 0 solids (baked)
FEATURE [Part::Revolution] Revolve083  label="removeToCreateScrewAndThreadedInsertHole020"
  Angle = 360
  Axis = (0,1,0)
  Base = (0,0,0)
  FaceMakerClass = Part::FaceMakerBullseye
  Placement = pos=(30.3,30.3,19.7) rot=(0,0,1;0rad)
  Solid = false
  Source = -> Face079
  Symmetric = false
FEATURE [Part::Feature] Face080
  shape: bbox 3.5 x 17.8 x 2e-07 mm, 1 faces, 0 solids (baked)
FEATURE [Part::Revolution] Revolve084  label="removeToCreateScrewAndThreadedInsertHole021"
  Angle = 360
  Axis = (0,1,0)
  Base = (0,0,0)
  FaceMakerClass = Part::FaceMakerBullseye
  Placement = pos=(30.3,30.3,51.7) rot=(0,0,1;0rad)
  Solid = false
  Source = -> Face080
  Symmetric = false
FEATURE [Part::MultiFuse] Fusion053  label="createThreadedInsertHolesForFan"
  Shapes = -> [Revolve081,Revolve082,Revolve083,Revolve084]
FEATURE [Part::Cut] Cut017  label="fanScrewHousing001"
  Base = -> Fusion046
  Tool = -> Fusion053
FEATURE [Part::Feature] Face081
  shape: bbox 3.5 x 17.8 x 2e-07 mm, 1 faces, 0 solids (baked)
FEATURE [Part::Revolution] Revolve085  label="removeToCreateScrewAndThreadedInsertHole022"
  Angle = 360
  Axis = (0,1,0)
  Base = (0,0,0)
  FaceMakerClass = Part::FaceMakerBullseye
  Placement = pos=(62.3,30.3,19.7) rot=(0,0,1;0rad)
  Solid = false
  Source = -> Face081
  Symmetric = false
FEATURE [Part::Feature] Face082
  shape: bbox 3.5 x 17.8 x 2e-07 mm, 1 faces, 0 solids (baked)
FEATURE [Part::Revolution] Revolve086  label="removeToCreateScrewAndThreadedInsertHole023"
  Angle = 360
  Axis = (0,1,0)
  Base = (0,0,0)
  FaceMakerClass = Part::FaceMakerBullseye
  Placement = pos=(62.3,30.3,51.7) rot=(0,0,1;0rad)
  Solid = false
  Source = -> Face082
  Symmetric = false
FEATURE [Part::Feature] Face083
  shape: bbox 3.5 x 17.8 x 2e-07 mm, 1 faces, 0 solids (baked)
FEATURE [Part::Revolution] Revolve087  label="removeToCreateScrewAndThreadedInsertHole024"
  Angle = 360
  Axis = (0,1,0)
  Base = (0,0,0)
  FaceMakerClass = Part::FaceMakerBullseye
  Placement = pos=(30.3,30.3,19.7) rot=(0,0,1;0rad)
  Solid = false
  Source = -> Face083
  Symmetric = false
FEATURE [Part::Feature] Face084
  shape: bbox 3.5 x 17.8 x 2e-07 mm, 1 faces, 0 solids (baked)
FEATURE [Part::Revolution] Revolve088  label="removeToCreateScrewAndThreadedInsertHole025"
  Angle = 360
  Axis = (0,1,0)
  Base = (0,0,0)
  FaceMakerClass = Part::FaceMakerBullseye
  Placement = pos=(30.3,30.3,51.7) rot=(0,0,1;0rad)
  Solid = false
  Source = -> Face084
  Symmetric = false
FEATURE [Part::MultiFuse] Fusion054  label="createThreadedInsertHolesForFan001"
  Shapes = -> [Revolve085,Revolve086,Revolve087,Revolve088]
FEATURE [Part::Cut] Cut018  label="top007"
  Base = -> Fusion040
  Tool = -> Fusion054
FEATURE [Sketcher::SketchObject] Sketch029
  FullyConstrained = false
  Placement = pos=(0,0,0) rot=(1,0,0;1.5708rad)
  sketch-geometry (24):
    g0: ArcOfCircle CenterX=-4 CenterY=-10.5 CenterZ=0 NormalX=0 NormalY=0 NormalZ=1 AngleXU=0 Radius=1.5 StartAngle=6e-16 EndAngle=3.14159
    g1: ArcOfCircle CenterX=-34.2 CenterY=-10.5 CenterZ=0 NormalX=0 NormalY=0 NormalZ=1 AngleXU=0 Radius=1.5 StartAngle=0 EndAngle=3.14159
    g2: ArcOfCircle CenterX=-34.2 CenterY=-27.7 CenterZ=0 NormalX=0 NormalY=0 NormalZ=1 AngleXU=0 Radius=1.5 StartAngle=3.14159 EndAngle=6.28319
    g3: ArcOfCircle CenterX=-4 CenterY=-27.7 CenterZ=0 NormalX=0 NormalY=0 NormalZ=1 AngleXU=0 Radius=1.5 StartAngle=3.1416 EndAngle=6.28319
    g4: ArcOfCircle CenterX=-10 CenterY=-4.3 CenterZ=0 NormalX=0 NormalY=0 NormalZ=1 AngleXU=0 Radius=1.5 StartAngle=2e-16 EndAngle=3.14159
    g5: ArcOfCircle CenterX=-16.1 CenterY=-1.8 CenterZ=0 NormalX=0 NormalY=0 NormalZ=1 AngleXU=0 Radius=1.5 StartAngle=5e-16 EndAngle=3.14159
    g6: ArcOfCircle CenterX=-22.1 CenterY=-1.8 CenterZ=0 NormalX=0 NormalY=0 NormalZ=1 AngleXU=0 Radius=1.5 StartAngle=5e-16 EndAngle=3.14159
    g7: ArcOfCircle CenterX=-28.2 CenterY=-4.3 CenterZ=0 NormalX=0 NormalY=0 NormalZ=1 AngleXU=0 Radius=1.5 StartAngle=2e-16 EndAngle=3.14159
    g8: ArcOfCircle CenterX=-10 CenterY=-33.9 CenterZ=0 NormalX=0 NormalY=0 NormalZ=1 AngleXU=0 Radius=1.5 StartAngle=3.14159 EndAngle=6.28319
    g9: ArcOfCircle CenterX=-16.1 CenterY=-36.4 CenterZ=0 NormalX=0 NormalY=0 NormalZ=1 AngleXU=0 Radius=1.5 StartAngle=3.14159 EndAngle=6.28319
    g10: ArcOfCircle CenterX=-22.1 CenterY=-36.4 CenterZ=0 NormalX=0 NormalY=0 NormalZ=1 AngleXU=0 Radius=1.5 StartAngle=3.14159 EndAngle=6.28319
    g11: ArcOfCircle CenterX=-28.2 CenterY=-33.9 CenterZ=0 NormalX=0 NormalY=0 NormalZ=1 AngleXU=0 Radius=1.5 StartAngle=3.14159 EndAngle=6.28319
    g12: LineSegment StartX=-35.7 StartY=-10.5 StartZ=0 EndX=-35.7 EndY=-27.7 EndZ=0
    g13: LineSegment StartX=-32.7 StartY=-10.5 StartZ=0 EndX=-32.7 EndY=-27.7 EndZ=0
    g14: LineSegment StartX=-29.7 StartY=-33.9 StartZ=0 EndX=-29.7 EndY=-4.3 EndZ=0
    g15: LineSegment StartX=-26.7 StartY=-33.9 StartZ=0 EndX=-26.7 EndY=-4.3 EndZ=0
    g16: LineSegment StartX=-2.5 StartY=-10.5 StartZ=0 EndX=-2.5 EndY=-27.7 EndZ=0
    g17: LineSegment StartX=-8.5 StartY=-4.3 StartZ=0 EndX=-8.5 EndY=-33.9 EndZ=0
    g18: LineSegment StartX=-5.5 StartY=-10.5 StartZ=0 EndX=-5.5 EndY=-27.7 EndZ=0
    g19: LineSegment StartX=-11.5 StartY=-4.3 StartZ=0 EndX=-11.5 EndY=-33.9 EndZ=0
    g20: LineSegment StartX=-14.6 StartY=-1.8 StartZ=0 EndX=-14.6 EndY=-36.4 EndZ=0
    g21: LineSegment StartX=-17.6 StartY=-1.8 StartZ=0 EndX=-17.6 EndY=-36.4 EndZ=0
    g22: LineSegment StartX=-20.6 StartY=-36.4 StartZ=0 EndX=-20.6 EndY=-1.8 EndZ=0
    g23: LineSegment StartX=-23.6 StartY=-1.8 StartZ=0 EndX=-23.6 EndY=-36.4 EndZ=0
  constraints (48):
    c: Block(g0)
    c: Block(g1)
    c: Block(g2)
    c: Block(g3)
    c: Block(g4)
    c: Block(g5)
    c: Block(g6)
    c: Block(g7)
    c: Block(g8)
    c: Block(g9)
    c: Block(g10)
    c: Block(g11)
    c: Coincident(g12,g1)
    c: Coincident(g12,g2)
    c: Vertical(g12)
    c: Coincident(g13,g1)
    c: Coincident(g13,g2)
    c: Vertical(g13)
    c: Coincident(g14,g11)
    c: Coincident(g14,g7)
    c: Vertical(g14)
    c: Coincident(g15,g11)
    c: Coincident(g15,g7)
    c: Vertical(g15)
    c: Coincident(g16,g0)
    c: Coincident(g16,g3)
    c: Vertical(g16)
    c: Coincident(g17,g4)
    c: Coincident(g17,g8)
    c: Vertical(g17)
    c: Coincident(g18,g0)
    c: Coincident(g18,g3)
    c: Vertical(g18)
    c: Coincident(g19,g4)
    c: Coincident(g19,g8)
    c: Vertical(g19)
    c: Coincident(g20,g5)
    c: Coincident(g20,g9)
    c: Vertical(g20)
    c: Coincident(g21,g5)
    c: Coincident(g21,g9)
    c: Vertical(g21)
    c: Coincident(g22,g10)
    c: Coincident(g22,g6)
    c: Vertical(g22)
    c: Coincident(g23,g6)
    c: Coincident(g23,g10)
    c: Vertical(g23)
FEATURE [Part::Extrusion] Extrude020  label="removeToCreateFanGrillHoles"
  Base = -> Sketch029
  Dir = (0,-1,6e-16)
  DirMode = 2
  FaceMakerClass = Part::FaceMakerBullseye
  LengthFwd = 10
  LengthRev = 0
  Placement = pos=(65.4,44,54.82) rot=(0,0,1;0rad)
  Solid = true
  Symmetric = false
FEATURE [Part::MultiFuse] Fusion055  label="top008"
  Shapes = -> [Cut017,Cut018]
FEATURE [Part::Cut] Cut019  label="top009"
  Base = -> Fusion055
  Tool = -> Extrude020
FEATURE [App::MeasureDistance] Distance003  label="Distance: 71.95 mm"
  Distance = 71.9513
  P1 = (117,38,72)
  P2 = (117,38,0.0487319)
FEATURE [Sketcher::SketchObject] Sketch030
  FullyConstrained = true
  Placement = pos=(117,19,0) rot=(0.57735,0.57735,0.57735;2.0944rad)
  sketch-geometry (48):
    g0: LineSegment StartX=-49.19 StartY=69.25 StartZ=0 EndX=-49.19 EndY=66.25 EndZ=0
    g1: LineSegment StartX=-49.19 StartY=63.5 StartZ=0 EndX=-49.19 EndY=60.5 EndZ=0
    g2: LineSegment StartX=-49.19 StartY=57.75 StartZ=0 EndX=-49.19 EndY=54.75 EndZ=0
    g3: LineSegment StartX=-49.19 StartY=52 StartZ=0 EndX=-49.19 EndY=49 EndZ=0
    g4: LineSegment StartX=-49.19 StartY=46.25 StartZ=0 EndX=-49.19 EndY=43.25 EndZ=0
    g5: LineSegment StartX=-49.19 StartY=40.5 StartZ=0 EndX=-49.19 EndY=37.5 EndZ=0
    g6: LineSegment StartX=-49.19 StartY=34.5 StartZ=0 EndX=-49.19 EndY=31.5 EndZ=0
    g7: LineSegment StartX=-49.19 StartY=28.75 StartZ=0 EndX=-49.19 EndY=25.75 EndZ=0
    g8: LineSegment StartX=-49.19 StartY=23 StartZ=0 EndX=-49.19 EndY=20 EndZ=0
    g9: LineSegment StartX=-49.19 StartY=17.25 StartZ=0 EndX=-49.19 EndY=14.25 EndZ=0
    g10: LineSegment StartX=-49.19 StartY=11.5 StartZ=0 EndX=-49.19 EndY=8.5 EndZ=0
    g11: LineSegment StartX=-49.19 StartY=5.75 StartZ=0 EndX=-49.19 EndY=2.75 EndZ=0
    g12: ArcOfCircle CenterX=-1.5 CenterY=67.75 CenterZ=0 NormalX=0 NormalY=0 NormalZ=1 AngleXU=0 Radius=1.5 StartAngle=4.71239 EndAngle=7.85398
    g13: ArcOfCircle CenterX=-1.5 CenterY=62 CenterZ=0 NormalX=0 NormalY=0 NormalZ=1 AngleXU=0 Radius=1.5 StartAngle=4.71239 EndAngle=7.85398
    g14: ArcOfCircle CenterX=-1.5 CenterY=56.25 CenterZ=0 NormalX=0 NormalY=0 NormalZ=1 AngleXU=0 Radius=1.5 StartAngle=4.71239 EndAngle=7.85398
    g15: ArcOfCircle CenterX=-11.49 CenterY=50.5 CenterZ=0 NormalX=0 NormalY=0 NormalZ=1 AngleXU=0 Radius=1.5 StartAngle=4.71239 EndAngle=7.85398
    g16: ArcOfCircle CenterX=-16.28 CenterY=44.75 CenterZ=0 NormalX=0 NormalY=0 NormalZ=1 AngleXU=0 Radius=1.5 StartAngle=4.71239 EndAngle=7.85398
    g17: ArcOfCircle CenterX=-18.2337 CenterY=39 CenterZ=0 NormalX=0 NormalY=0 NormalZ=1 AngleXU=0 Radius=1.5 StartAngle=4.71485 EndAngle=7.85398
    g18: ArcOfCircle CenterX=-16.2837 CenterY=27.25 CenterZ=0 NormalX=0 NormalY=0 NormalZ=1 AngleXU=0 Radius=1.5 StartAngle=4.71485 EndAngle=7.85398
    g19: ArcOfCircle CenterX=-18.2337 CenterY=33 CenterZ=0 NormalX=0 NormalY=0 NormalZ=1 AngleXU=0 Radius=1.5 StartAngle=4.71485 EndAngle=7.85398
    g20: ArcOfCircle CenterX=-11.49 CenterY=21.5 CenterZ=0 NormalX=0 NormalY=0 NormalZ=1 AngleXU=0 Radius=1.5 StartAngle=4.71239 EndAngle=7.85398
    g21: ArcOfCircle CenterX=-1.5 CenterY=4.25 CenterZ=0 NormalX=0 NormalY=0 NormalZ=1 AngleXU=0 Radius=1.5 StartAngle=4.71239 EndAngle=7.85398
    g22: ArcOfCircle CenterX=-1.5 CenterY=10 CenterZ=0 NormalX=0 NormalY=0 NormalZ=1 AngleXU=0 Radius=1.5 StartAngle=4.71239 EndAngle=7.85398
    g23: ArcOfCircle CenterX=-1.5 CenterY=15.75 CenterZ=0 NormalX=0 NormalY=0 NormalZ=1 AngleXU=0 Radius=1.5 StartAngle=4.71239 EndAngle=7.85398
    g24: LineSegment StartX=-49.19 StartY=69.25 StartZ=0 EndX=-1.5 EndY=69.25 EndZ=0
    g25: LineSegment StartX=-49.19 StartY=66.25 StartZ=0 EndX=-1.5 EndY=66.25 EndZ=0
    g26: LineSegment StartX=-49.19 StartY=63.5 StartZ=0 EndX=-1.5 EndY=63.5 EndZ=0
    g27: LineSegment StartX=-49.19 StartY=60.5 StartZ=0 EndX=-1.5 EndY=60.5 EndZ=0
    g28: LineSegment StartX=-49.19 StartY=57.75 StartZ=0 EndX=-1.5 EndY=57.75 EndZ=0
    g29: LineSegment StartX=-49.19 StartY=54.75 StartZ=0 EndX=-1.5 EndY=54.75 EndZ=0
    g30: LineSegment StartX=-49.19 StartY=52 StartZ=0 EndX=-11.49 EndY=52 EndZ=0
    g31: LineSegment StartX=-49.19 StartY=49 StartZ=0 EndX=-11.49 EndY=49 EndZ=0
    g32: LineSegment StartX=-49.19 StartY=46.25 StartZ=0 EndX=-16.28 EndY=46.25 EndZ=0
    g33: LineSegment StartX=-49.19 StartY=43.25 StartZ=0 EndX=-16.28 EndY=43.25 EndZ=0
    g34: LineSegment StartX=-49.19 StartY=40.5 StartZ=0 EndX=-18.2337 EndY=40.5 EndZ=0
    g35: LineSegment StartX=-49.19 StartY=37.5 StartZ=0 EndX=-18.23 EndY=37.5 EndZ=0
    g36: LineSegment StartX=-49.19 StartY=34.5 StartZ=0 EndX=-18.2337 EndY=34.5 EndZ=0
    g37: LineSegment StartX=-49.19 StartY=31.5 StartZ=0 EndX=-18.23 EndY=31.5 EndZ=0
    g38: LineSegment StartX=-49.19 StartY=28.75 StartZ=0 EndX=-16.2837 EndY=28.75 EndZ=0
    g39: LineSegment StartX=-49.19 StartY=25.75 StartZ=0 EndX=-16.28 EndY=25.75 EndZ=0
    g40: LineSegment StartX=-49.19 StartY=23 StartZ=0 EndX=-11.49 EndY=23 EndZ=0
    g41: LineSegment StartX=-49.19 StartY=20 StartZ=0 EndX=-11.49 EndY=20 EndZ=0
    g42: LineSegment StartX=-49.19 StartY=17.25 StartZ=0 EndX=-1.5 EndY=17.25 EndZ=0
    g43: LineSegment StartX=-49.19 StartY=14.25 StartZ=0 EndX=-1.5 EndY=14.25 EndZ=0
    g44: LineSegment StartX=-49.19 StartY=11.5 StartZ=0 EndX=-1.5 EndY=11.5 EndZ=0
    g45: LineSegment StartX=-49.19 StartY=8.5 StartZ=0 EndX=-1.5 EndY=8.5 EndZ=0
    g46: LineSegment StartX=-49.19 StartY=5.75 StartZ=0 EndX=-1.5 EndY=5.75 EndZ=0
    g47: LineSegment StartX=-49.19 StartY=2.75 StartZ=0 EndX=-1.5 EndY=2.75 EndZ=0
  constraints (120):
    c: Vertical(g0)
    c: Distance(g0) = 3
    c: Block(g0)
    c: Vertical(g1)
    c: Distance(g1) = 3
    c: Vertical(g2)
    c: Equal(g0,g2) = 3
    c: Block(g2)
    c: Vertical(g3)
    c: Equal(g1,g3) = 3
    c: Vertical(g4)
    c: Equal(g0,g4) = 3
    c: Block(g4)
    c: Vertical(g5)
    c: Equal(g1,g5) = 3
    c: Vertical(g6)
    c: Equal(g0,g6) = 3
    c: Block(g6)
    c: Vertical(g7)
    c: Equal(g1,g7) = 3
    c: Vertical(g8)
    c: Equal(g0,g8) = 3
    c: Block(g8)
    c: Vertical(g9)
    c: Equal(g1,g9) = 3
    c: Vertical(g10)
    c: Equal(g0,g10) = 3
    c: Block(g10)
    c: Vertical(g11)
    c: Equal(g1,g11) = 3
    c: Block(g12)
    c: Block(g13)
    c: Block(g14)
    c: Block(g15)
    c: Block(g16)
    c: Block(g17)
    c: Block(g18)
    c: Block(g19)
    c: Block(g20)
    c: Block(g21)
    c: Block(g22)
    c: Block(g23)
    c: Block(g11)
    c: Block(g9)
    c: Block(g7)
    c: Block(g5)
    c: Block(g3)
    c: Block(g1)
    c: Coincident(g24,g0)
    c: Coincident(g24,g12)
    c: Horizontal(g24)
    c: Coincident(g25,g0)
    c: Coincident(g25,g12)
    c: Horizontal(g25)
    c: Coincident(g26,g1)
    c: Coincident(g26,g13)
    c: Horizontal(g26)
    c: Coincident(g27,g1)
    c: Coincident(g27,g13)
    c: Horizontal(g27)
    c: Coincident(g28,g2)
    c: Coincident(g28,g14)
    c: Horizontal(g28)
    c: Coincident(g29,g2)
    c: Coincident(g29,g14)
    c: Horizontal(g29)
    c: Coincident(g30,g3)
    c: Coincident(g30,g15)
    c: Horizontal(g30)
    c: Coincident(g31,g3)
    c: Coincident(g31,g15)
    c: Horizontal(g31)
    c: Coincident(g32,g4)
    c: Coincident(g32,g16)
    c: Horizontal(g32)
    c: Coincident(g33,g4)
    c: Coincident(g33,g16)
    c: Horizontal(g33)
    c: Coincident(g34,g5)
    c: Coincident(g34,g17)
    c: Horizontal(g34)
    c: Coincident(g35,g5)
    c: Coincident(g35,g17)
    c: Horizontal(g35)
    c: Coincident(g36,g6)
    c: Coincident(g36,g19)
    c: Horizontal(g36)
    c: Coincident(g37,g6)
    c: Coincident(g37,g19)
    c: Horizontal(g37)
    c: Coincident(g38,g7)
    c: Coincident(g38,g18)
    c: Horizontal(g38)
    c: Coincident(g39,g7)
    c: Coincident(g39,g18)
    c: Horizontal(g39)
    c: Coincident(g40,g8)
    c: Coincident(g40,g20)
    c: Horizontal(g40)
    c: Coincident(g41,g8)
    c: Coincident(g41,g20)
    c: Horizontal(g41)
    c: Coincident(g42,g9)
    c: Coincident(g42,g23)
    c: Horizontal(g42)
    c: Coincident(g43,g9)
    c: Coincident(g43,g23)
    c: Horizontal(g43)
    c: Coincident(g44,g10)
    c: Coincident(g44,g22)
    c: Horizontal(g44)
    c: Coincident(g45,g10)
    c: Coincident(g45,g22)
    c: Horizontal(g45)
    c: Coincident(g46,g11)
    c: Coincident(g46,g21)
    c: Horizontal(g46)
    c: Coincident(g47,g11)
    c: Coincident(g47,g21)
    c: Horizontal(g47)
FEATURE [Sketcher::SketchObject] Sketch031
  FullyConstrained = true
  Placement = pos=(117,19,0) rot=(0.57735,0.57735,0.57735;2.0944rad)
  sketch-geometry (24):
    g0: ArcOfCircle CenterX=-49.19 CenterY=67.75 CenterZ=0 NormalX=0 NormalY=0 NormalZ=1 AngleXU=0 Radius=1.5 StartAngle=1.5708 EndAngle=4.71239
    g1: ArcOfCircle CenterX=-49.19 CenterY=62 CenterZ=0 NormalX=0 NormalY=0 NormalZ=1 AngleXU=0 Radius=1.5 StartAngle=1.5708 EndAngle=4.71239
    g2: ArcOfCircle CenterX=-49.19 CenterY=56.25 CenterZ=0 NormalX=0 NormalY=0 NormalZ=1 AngleXU=0 Radius=1.5 StartAngle=1.5708 EndAngle=4.71239
    g3: ArcOfCircle CenterX=-49.19 CenterY=50.5 CenterZ=0 NormalX=0 NormalY=0 NormalZ=1 AngleXU=0 Radius=1.5 StartAngle=1.5708 EndAngle=4.71239
    g4: ArcOfCircle CenterX=-49.19 CenterY=44.75 CenterZ=0 NormalX=0 NormalY=0 NormalZ=1 AngleXU=0 Radius=1.5 StartAngle=1.5708 EndAngle=4.71239
    g5: ArcOfCircle CenterX=-49.19 CenterY=39 CenterZ=0 NormalX=0 NormalY=0 NormalZ=1 AngleXU=0 Radius=1.5 StartAngle=1.5708 EndAngle=4.71239
    g6: ArcOfCircle CenterX=-49.19 CenterY=33 CenterZ=0 NormalX=0 NormalY=0 NormalZ=1 AngleXU=0 Radius=1.5 StartAngle=1.5708 EndAngle=4.71239
    g7: ArcOfCircle CenterX=-49.19 CenterY=27.25 CenterZ=0 NormalX=0 NormalY=0 NormalZ=1 AngleXU=0 Radius=1.5 StartAngle=1.5708 EndAngle=4.71239
    g8: ArcOfCircle CenterX=-49.19 CenterY=21.5 CenterZ=0 NormalX=0 NormalY=0 NormalZ=1 AngleXU=0 Radius=1.5 StartAngle=1.5708 EndAngle=4.71239
    g9: ArcOfCircle CenterX=-49.19 CenterY=15.75 CenterZ=0 NormalX=0 NormalY=0 NormalZ=1 AngleXU=0 Radius=1.5 StartAngle=1.5708 EndAngle=4.71239
    g10: ArcOfCircle CenterX=-49.19 CenterY=10 CenterZ=0 NormalX=0 NormalY=0 NormalZ=1 AngleXU=0 Radius=1.5 StartAngle=1.5708 EndAngle=4.71239
    g11: ArcOfCircle CenterX=-49.19 CenterY=4.25 CenterZ=0 NormalX=0 NormalY=0 NormalZ=1 AngleXU=0 Radius=1.5 StartAngle=1.5708 EndAngle=4.71239
    g12: LineSegment StartX=-49.19 StartY=69.25 StartZ=0 EndX=-49.19 EndY=66.25 EndZ=0
    g13: LineSegment StartX=-49.19 StartY=63.5 StartZ=0 EndX=-49.19 EndY=60.5 EndZ=0
    g14: LineSegment StartX=-49.19 StartY=57.75 StartZ=0 EndX=-49.19 EndY=54.75 EndZ=0
    g15: LineSegment StartX=-49.19 StartY=52 StartZ=0 EndX=-49.19 EndY=49 EndZ=0
    g16: LineSegment StartX=-49.19 StartY=46.25 StartZ=0 EndX=-49.19 EndY=43.25 EndZ=0
    g17: LineSegment StartX=-49.19 StartY=40.5 StartZ=0 EndX=-49.19 EndY=37.5 EndZ=0
    g18: LineSegment StartX=-49.19 StartY=34.5 StartZ=0 EndX=-49.19 EndY=31.5 EndZ=0
    g19: LineSegment StartX=-49.19 StartY=28.75 StartZ=0 EndX=-49.19 EndY=25.75 EndZ=0
    g20: LineSegment StartX=-49.19 StartY=23 StartZ=0 EndX=-49.19 EndY=20 EndZ=0
    g21: LineSegment StartX=-49.19 StartY=17.25 StartZ=0 EndX=-49.19 EndY=14.25 EndZ=0
    g22: LineSegment StartX=-49.19 StartY=11.5 StartZ=0 EndX=-49.19 EndY=8.5 EndZ=0
    g23: LineSegment StartX=-49.19 StartY=5.75 StartZ=0 EndX=-49.19 EndY=2.75 EndZ=0
  constraints (48):
    c: Block(g0)
    c: Block(g1)
    c: Block(g2)
    c: Block(g3)
    c: Block(g4)
    c: Block(g5)
    c: Block(g6)
    c: Block(g7)
    c: Block(g8)
    c: Block(g9)
    c: Block(g10)
    c: Block(g11)
    c: Coincident(g12,g0)
    c: Coincident(g12,g0)
    c: Vertical(g12)
    c: Vertical(g13)
    c: Coincident(g13,g1)
    c: Vertical(g14)
    c: Coincident(g14,g2)
    c: Vertical(g15)
    c: Coincident(g15,g3)
    c: Vertical(g16)
    c: Coincident(g16,g4)
    c: Vertical(g17)
    c: Coincident(g17,g5)
    c: Vertical(g18)
    c: Coincident(g18,g6)
    c: Vertical(g19)
    c: Coincident(g19,g7)
    c: Vertical(g20)
    c: Coincident(g20,g8)
    c: Vertical(g21)
    c: Coincident(g21,g9)
    c: Vertical(g22)
    c: Coincident(g22,g10)
    c: Vertical(g23)
    c: Coincident(g23,g11)
    c: Block(g23)
    c: Block(g22)
    c: Block(g21)
    c: Block(g20)
    c: Block(g13)
    c: Block(g14)
    c: Block(g15)
    c: Block(g16)
    c: Block(g17)
    c: Block(g18)
    c: Block(g19)
FEATURE [Part::Extrusion] Extrude022
  Base = -> Sketch030
  Dir = (1,-2e-16,2e-16)
  DirMode = 2
  FaceMakerClass = Part::FaceMakerBullseye
  LengthFwd = 19
  LengthRev = 0
  Placement = pos=(-19,0,0) rot=(0,0,1;0rad)
  Solid = true
  Symmetric = false
FEATURE [Part::Fillet] Fillet022
  Base = -> Extrude022
  Edges = 24 edges r=1.49: [Edge6,Edge11,Edge18,Edge23,Edge30,Edge35,Edge42,Edge47,Edge54,Edge59,Edge66,Edge71,Edge78,Edge83,Edge90,Edge95,Edge102,Edge107,Edge114,Edge119,Edge126,Edge131,Edge138,Edge143]
FEATURE [Part::Cut] Cut020  label="top010"
  Base = -> Cut019
  Tool = -> Fillet022
FEATURE [Sketcher::SketchObject] Sketch032
  FullyConstrained = true
  Placement = pos=(117,19,0) rot=(0.57735,0.57735,0.57735;2.0944rad)
  sketch-geometry (48):
    g0: LineSegment StartX=-49.19 StartY=69.25 StartZ=0 EndX=-49.19 EndY=66.25 EndZ=0
    g1: LineSegment StartX=-49.19 StartY=63.5 StartZ=0 EndX=-49.19 EndY=60.5 EndZ=0
    g2: LineSegment StartX=-49.19 StartY=57.75 StartZ=0 EndX=-49.19 EndY=54.75 EndZ=0
    g3: LineSegment StartX=-49.19 StartY=52 StartZ=0 EndX=-49.19 EndY=49 EndZ=0
    g4: LineSegment StartX=-49.19 StartY=46.25 StartZ=0 EndX=-49.19 EndY=43.25 EndZ=0
    g5: LineSegment StartX=-49.19 StartY=40.5 StartZ=0 EndX=-49.19 EndY=37.5 EndZ=0
    g6: LineSegment StartX=-49.19 StartY=34.5 StartZ=0 EndX=-49.19 EndY=31.5 EndZ=0
    g7: LineSegment StartX=-49.19 StartY=28.75 StartZ=0 EndX=-49.19 EndY=25.75 EndZ=0
    g8: LineSegment StartX=-49.19 StartY=23 StartZ=0 EndX=-49.19 EndY=20 EndZ=0
    g9: LineSegment StartX=-49.19 StartY=17.25 StartZ=0 EndX=-49.19 EndY=14.25 EndZ=0
    g10: LineSegment StartX=-49.19 StartY=11.5 StartZ=0 EndX=-49.19 EndY=8.5 EndZ=0
    g11: LineSegment StartX=-49.19 StartY=5.75 StartZ=0 EndX=-49.19 EndY=2.75 EndZ=0
    g12: ArcOfCircle CenterX=-1.5 CenterY=67.75 CenterZ=0 NormalX=0 NormalY=0 NormalZ=1 AngleXU=0 Radius=1.5 StartAngle=4.71239 EndAngle=7.85398
    g13: ArcOfCircle CenterX=-1.5 CenterY=62 CenterZ=0 NormalX=0 NormalY=0 NormalZ=1 AngleXU=0 Radius=1.5 StartAngle=4.71239 EndAngle=7.85398
    g14: ArcOfCircle CenterX=-1.5 CenterY=56.25 CenterZ=0 NormalX=0 NormalY=0 NormalZ=1 AngleXU=0 Radius=1.5 StartAngle=4.71239 EndAngle=7.85398
    g15: ArcOfCircle CenterX=-11.49 CenterY=50.5 CenterZ=0 NormalX=0 NormalY=0 NormalZ=1 AngleXU=0 Radius=1.5 StartAngle=4.71239 EndAngle=7.85398
    g16: ArcOfCircle CenterX=-16.28 CenterY=44.75 CenterZ=0 NormalX=0 NormalY=0 NormalZ=1 AngleXU=0 Radius=1.5 StartAngle=4.71239 EndAngle=7.85398
    g17: ArcOfCircle CenterX=-18.2337 CenterY=39 CenterZ=0 NormalX=0 NormalY=0 NormalZ=1 AngleXU=0 Radius=1.5 StartAngle=4.71485 EndAngle=7.85398
    g18: ArcOfCircle CenterX=-16.2837 CenterY=27.25 CenterZ=0 NormalX=0 NormalY=0 NormalZ=1 AngleXU=0 Radius=1.5 StartAngle=4.71485 EndAngle=7.85398
    g19: ArcOfCircle CenterX=-18.2337 CenterY=33 CenterZ=0 NormalX=0 NormalY=0 NormalZ=1 AngleXU=0 Radius=1.5 StartAngle=4.71485 EndAngle=7.85398
    g20: ArcOfCircle CenterX=-11.49 CenterY=21.5 CenterZ=0 NormalX=0 NormalY=0 NormalZ=1 AngleXU=0 Radius=1.5 StartAngle=4.71239 EndAngle=7.85398
    g21: ArcOfCircle CenterX=-1.5 CenterY=4.25 CenterZ=0 NormalX=0 NormalY=0 NormalZ=1 AngleXU=0 Radius=1.5 StartAngle=4.71239 EndAngle=7.85398
    g22: ArcOfCircle CenterX=-1.5 CenterY=10 CenterZ=0 NormalX=0 NormalY=0 NormalZ=1 AngleXU=0 Radius=1.5 StartAngle=4.71239 EndAngle=7.85398
    g23: ArcOfCircle CenterX=-1.5 CenterY=15.75 CenterZ=0 NormalX=0 NormalY=0 NormalZ=1 AngleXU=0 Radius=1.5 StartAngle=4.71239 EndAngle=7.85398
    g24: LineSegment StartX=-49.19 StartY=69.25 StartZ=0 EndX=-1.5 EndY=69.25 EndZ=0
    g25: LineSegment StartX=-49.19 StartY=66.25 StartZ=0 EndX=-1.5 EndY=66.25 EndZ=0
    g26: LineSegment StartX=-49.19 StartY=63.5 StartZ=0 EndX=-1.5 EndY=63.5 EndZ=0
    g27: LineSegment StartX=-49.19 StartY=60.5 StartZ=0 EndX=-1.5 EndY=60.5 EndZ=0
    g28: LineSegment StartX=-49.19 StartY=57.75 StartZ=0 EndX=-1.5 EndY=57.75 EndZ=0
    g29: LineSegment StartX=-49.19 StartY=54.75 StartZ=0 EndX=-1.5 EndY=54.75 EndZ=0
    g30: LineSegment StartX=-49.19 StartY=52 StartZ=0 EndX=-11.49 EndY=52 EndZ=0
    g31: LineSegment StartX=-49.19 StartY=49 StartZ=0 EndX=-11.49 EndY=49 EndZ=0
    g32: LineSegment StartX=-49.19 StartY=46.25 StartZ=0 EndX=-16.28 EndY=46.25 EndZ=0
    g33: LineSegment StartX=-49.19 StartY=43.25 StartZ=0 EndX=-16.28 EndY=43.25 EndZ=0
    g34: LineSegment StartX=-49.19 StartY=40.5 StartZ=0 EndX=-18.2337 EndY=40.5 EndZ=0
    g35: LineSegment StartX=-49.19 StartY=37.5 StartZ=0 EndX=-18.23 EndY=37.5 EndZ=0
    g36: LineSegment StartX=-49.19 StartY=34.5 StartZ=0 EndX=-18.2337 EndY=34.5 EndZ=0
    g37: LineSegment StartX=-49.19 StartY=31.5 StartZ=0 EndX=-18.23 EndY=31.5 EndZ=0
    g38: LineSegment StartX=-49.19 StartY=28.75 StartZ=0 EndX=-16.2837 EndY=28.75 EndZ=0
    g39: LineSegment StartX=-49.19 StartY=25.75 StartZ=0 EndX=-16.28 EndY=25.75 EndZ=0
    g40: LineSegment StartX=-49.19 StartY=23 StartZ=0 EndX=-11.49 EndY=23 EndZ=0
    g41: LineSegment StartX=-49.19 StartY=20 StartZ=0 EndX=-11.49 EndY=20 EndZ=0
    g42: LineSegment StartX=-49.19 StartY=17.25 StartZ=0 EndX=-1.5 EndY=17.25 EndZ=0
    g43: LineSegment StartX=-49.19 StartY=14.25 StartZ=0 EndX=-1.5 EndY=14.25 EndZ=0
    g44: LineSegment StartX=-49.19 StartY=11.5 StartZ=0 EndX=-1.5 EndY=11.5 EndZ=0
    g45: LineSegment StartX=-49.19 StartY=8.5 StartZ=0 EndX=-1.5 EndY=8.5 EndZ=0
    g46: LineSegment StartX=-49.19 StartY=5.75 StartZ=0 EndX=-1.5 EndY=5.75 EndZ=0
    g47: LineSegment StartX=-49.19 StartY=2.75 StartZ=0 EndX=-1.5 EndY=2.75 EndZ=0
  constraints (120):
    c: Vertical(g0)
    c: Distance(g0) = 3
    c: Block(g0)
    c: Vertical(g1)
    c: Distance(g1) = 3
    c: Vertical(g2)
    c: Equal(g0,g2) = 3
    c: Block(g2)
    c: Vertical(g3)
    c: Equal(g1,g3) = 3
    c: Vertical(g4)
    c: Equal(g0,g4) = 3
    c: Block(g4)
    c: Vertical(g5)
    c: Equal(g1,g5) = 3
    c: Vertical(g6)
    c: Equal(g0,g6) = 3
    c: Block(g6)
    c: Vertical(g7)
    c: Equal(g1,g7) = 3
    c: Vertical(g8)
    c: Equal(g0,g8) = 3
    c: Block(g8)
    c: Vertical(g9)
    c: Equal(g1,g9) = 3
    c: Vertical(g10)
    c: Equal(g0,g10) = 3
    c: Block(g10)
    c: Vertical(g11)
    c: Equal(g1,g11) = 3
    c: Block(g12)
    c: Block(g13)
    c: Block(g14)
    c: Block(g15)
    c: Block(g16)
    c: Block(g17)
    c: Block(g18)
    c: Block(g19)
    c: Block(g20)
    c: Block(g21)
    c: Block(g22)
    c: Block(g23)
    c: Block(g11)
    c: Block(g9)
    c: Block(g7)
    c: Block(g5)
    c: Block(g3)
    c: Block(g1)
    c: Coincident(g24,g0)
    c: Coincident(g24,g12)
    c: Horizontal(g24)
    c: Coincident(g25,g0)
    c: Coincident(g25,g12)
    c: Horizontal(g25)
    c: Coincident(g26,g1)
    c: Coincident(g26,g13)
    c: Horizontal(g26)
    c: Coincident(g27,g1)
    c: Coincident(g27,g13)
    c: Horizontal(g27)
    c: Coincident(g28,g2)
    c: Coincident(g28,g14)
    c: Horizontal(g28)
    c: Coincident(g29,g2)
    c: Coincident(g29,g14)
    c: Horizontal(g29)
    c: Coincident(g30,g3)
    c: Coincident(g30,g15)
    c: Horizontal(g30)
    c: Coincident(g31,g3)
    c: Coincident(g31,g15)
    c: Horizontal(g31)
    c: Coincident(g32,g4)
    c: Coincident(g32,g16)
    c: Horizontal(g32)
    c: Coincident(g33,g4)
    c: Coincident(g33,g16)
    c: Horizontal(g33)
    c: Coincident(g34,g5)
    c: Coincident(g34,g17)
    c: Horizontal(g34)
    c: Coincident(g35,g5)
    c: Coincident(g35,g17)
    c: Horizontal(g35)
    c: Coincident(g36,g6)
    c: Coincident(g36,g19)
    c: Horizontal(g36)
    c: Coincident(g37,g6)
    c: Coincident(g37,g19)
    c: Horizontal(g37)
    c: Coincident(g38,g7)
    c: Coincident(g38,g18)
    c: Horizontal(g38)
    c: Coincident(g39,g7)
    c: Coincident(g39,g18)
    c: Horizontal(g39)
    c: Coincident(g40,g8)
    c: Coincident(g40,g20)
    c: Horizontal(g40)
    c: Coincident(g41,g8)
    c: Coincident(g41,g20)
    c: Horizontal(g41)
    c: Coincident(g42,g9)
    c: Coincident(g42,g23)
    c: Horizontal(g42)
    c: Coincident(g43,g9)
    c: Coincident(g43,g23)
    c: Horizontal(g43)
    c: Coincident(g44,g10)
    c: Coincident(g44,g22)
    c: Horizontal(g44)
    c: Coincident(g45,g10)
    c: Coincident(g45,g22)
    c: Horizontal(g45)
    c: Coincident(g46,g11)
    c: Coincident(g46,g21)
    c: Horizontal(g46)
    c: Coincident(g47,g11)
    c: Coincident(g47,g21)
    c: Horizontal(g47)
FEATURE [Part::Extrusion] Extrude023
  Base = -> Sketch032
  Dir = (1,-2e-16,2e-16)
  DirMode = 2
  FaceMakerClass = Part::FaceMakerBullseye
  LengthFwd = 19
  LengthRev = 0
  Placement = pos=(-19,0,0) rot=(0,0,1;0rad)
  Solid = true
  Symmetric = false
FEATURE [Part::Fillet] Fillet023
  Base = -> Extrude023
  Edges = <same value as first occurrence — deduplicated (x6 in doc)>
  Placement = pos=(0,0.05,0) rot=(0,0,1;0rad)
FEATURE [Part::Cut] Cut014  label="bottom003"
  Base = -> Cut007
  Tool = -> Fusion047
FEATURE [Part::Cut] Cut021  label="bottom004"
  Base = -> Cut014
  Tool = -> Fillet023
FEATURE [Sketcher::SketchObject] Sketch033
  FullyConstrained = true
  Placement = pos=(117,19,0) rot=(0.57735,0.57735,0.57735;2.0944rad)
  sketch-geometry (8):
    g0: LineSegment StartX=-49.19 StartY=69.25 StartZ=0 EndX=-49.19 EndY=66.25 EndZ=0
    g1: LineSegment StartX=-49.19 StartY=5.75 StartZ=0 EndX=-49.19 EndY=2.75 EndZ=0
    g2: ArcOfCircle CenterX=-1.5 CenterY=67.75 CenterZ=0 NormalX=0 NormalY=0 NormalZ=1 AngleXU=0 Radius=1.5 StartAngle=4.71239 EndAngle=7.85398
    g3: ArcOfCircle CenterX=-1.5 CenterY=4.25 CenterZ=0 NormalX=0 NormalY=0 NormalZ=1 AngleXU=0 Radius=1.5 StartAngle=4.71239 EndAngle=7.85398
    g4: LineSegment StartX=-49.19 StartY=69.25 StartZ=0 EndX=-1.5 EndY=69.25 EndZ=0
    g5: LineSegment StartX=-49.19 StartY=66.25 StartZ=0 EndX=-1.5 EndY=66.25 EndZ=0
    g6: LineSegment StartX=-49.19 StartY=5.75 StartZ=0 EndX=-1.5 EndY=5.75 EndZ=0
    g7: LineSegment StartX=-49.19 StartY=2.75 StartZ=0 EndX=-1.5 EndY=2.75 EndZ=0
  constraints (19):
    c: Vertical(g0)
    c: Distance(g0) = 3
    c: Block(g0)
    c: Vertical(g1)
    c: Block(g2)
    c: Block(g3)
    c: Block(g1)
    c: Coincident(g4,g0)
    c: Coincident(g4,g2)
    c: Horizontal(g4)
    c: Coincident(g5,g0)
    c: Coincident(g5,g2)
    c: Horizontal(g5)
    c: Coincident(g6,g1)
    c: Coincident(g6,g3)
    c: Horizontal(g6)
    c: Coincident(g7,g1)
    c: Coincident(g7,g3)
    c: Horizontal(g7)
FEATURE [Sketcher::SketchObject] Sketch034
  FullyConstrained = true
  Placement = pos=(117,19,0) rot=(0.57735,0.57735,0.57735;2.0944rad)
  sketch-geometry (8):
    g0: LineSegment StartX=-49.19 StartY=63.5 StartZ=0 EndX=-49.19 EndY=60.5 EndZ=0
    g1: LineSegment StartX=-49.19 StartY=11.5 StartZ=0 EndX=-49.19 EndY=8.5 EndZ=0
    g2: ArcOfCircle CenterX=-1.5 CenterY=62 CenterZ=0 NormalX=0 NormalY=0 NormalZ=1 AngleXU=0 Radius=1.5 StartAngle=4.71239 EndAngle=7.85398
    g3: ArcOfCircle CenterX=-1.5 CenterY=10 CenterZ=0 NormalX=0 NormalY=0 NormalZ=1 AngleXU=0 Radius=1.5 StartAngle=4.71239 EndAngle=7.85398
    g4: LineSegment StartX=-49.19 StartY=63.5 StartZ=0 EndX=-1.5 EndY=63.5 EndZ=0
    g5: LineSegment StartX=-49.19 StartY=60.5 StartZ=0 EndX=-1.5 EndY=60.5 EndZ=0
    g6: LineSegment StartX=-49.19 StartY=11.5 StartZ=0 EndX=-1.5 EndY=11.5 EndZ=0
    g7: LineSegment StartX=-49.19 StartY=8.5 StartZ=0 EndX=-1.5 EndY=8.5 EndZ=0
  constraints (19):
    c: Vertical(g0)
    c: Distance(g0) = 3
    c: Vertical(g1)
    c: Block(g1)
    c: Block(g2)
    c: Block(g3)
    c: Block(g0)
    c: Coincident(g4,g0)
    c: Coincident(g4,g2)
    c: Horizontal(g4)
    c: Coincident(g5,g0)
    c: Coincident(g5,g2)
    c: Horizontal(g5)
    c: Coincident(g6,g1)
    c: Coincident(g6,g3)
    c: Horizontal(g6)
    c: Coincident(g7,g1)
    c: Coincident(g7,g3)
    c: Horizontal(g7)
FEATURE [Part::Extrusion] Extrude024
  Base = -> Sketch033
  Dir = (1,0,0)
  DirMode = 2
  FaceMakerClass = Part::FaceMakerBullseye
  LengthFwd = 10
  LengthRev = 0
  Solid = true
  Symmetric = false
FEATURE [Part::Extrusion] Extrude025
  Base = -> Sketch034
  Dir = (1,0,0)
  DirMode = 2
  FaceMakerClass = Part::FaceMakerBullseye
  LengthFwd = 10
  LengthRev = 0
  Solid = true
  Symmetric = false
FEATURE [Part::Fillet] Fillet024  label="removeFromtMoreFrontCaseScrewRetainers"
  Base = -> Extrude024
  Edges = 4 edges r=1.49: [Edge6,Edge11,Edge18,Edge23]
  Placement = pos=(-11,0,0) rot=(0,0,1;0rad)
FEATURE [Part::Fillet] Fillet025  label="removeFromtMoreFrontCaseScrewRetainers001"
  Base = -> Extrude025
  Edges = 4 edges r=1.49: [Edge6,Edge11,Edge18,Edge23]
  Placement = pos=(-19,0,0) rot=(0,0,1;0rad)
FEATURE [Part::Cut] Cut022
  Base = -> Cut015
  Tool = -> Fillet025
FEATURE [Part::Cut] Cut023  label="screwRetainers"
  Base = -> Cut022
  Tool = -> Fillet024
FEATURE [Part::MultiFuse] Fusion056  label="bottom005"
  Shapes = -> [Fusion044,Cut021]
FEATURE [Part::MultiFuse] Fusion057  label="casePillars001"
  Shapes = -> [Cut016,Fusion052]
FEATURE [Part::MultiFuse] Fusion058  label="bottom006"
  Shapes = -> [Fusion056,Cut023]
FEATURE [Part::MultiFuse] Fusion059  label="bottom007"
  Shapes = -> [Fusion058,Fillet005]
FEATURE [Part::MultiFuse] Fusion060  label="bottom008"
  Shapes = -> [Fusion059,Fusion]
FEATURE [Part::MultiFuse] Fusion061  label="top011"
  Shapes = -> [Cut006,Cut020]
FEATURE [Part::MultiFuse] Fusion062  label="top012"
  Shapes = -> [Fusion057,Fusion061]
FEATURE [Sketcher::SketchObject] Sketch035  label="topSketch007"
  FullyConstrained = true
  sketch-geometry (6):
    g0: LineSegment StartX=19 StartY=38 StartZ=0 EndX=117 EndY=38 EndZ=0
    g1: ArcOfCircle CenterX=19 CenterY=19 CenterZ=0 NormalX=0 NormalY=0 NormalZ=1 AngleXU=0 Radius=19 StartAngle=1.5708 EndAngle=3.14159
    g2: LineSegment StartX=117 StartY=38 StartZ=0 EndX=117 EndY=19 EndZ=0
    g3: LineSegment StartX=98 StartY=1.0161e-12 StartZ=0 EndX=5.22862e-06 EndY=1.0161e-12 EndZ=0
    g4: LineSegment StartX=5.22862e-06 StartY=19 StartZ=0 EndX=5.22862e-06 EndY=1.0161e-12 EndZ=0
    g5: ArcOfCircle CenterX=98 CenterY=19 CenterZ=0 NormalX=0 NormalY=0 NormalZ=1 AngleXU=0 Radius=19 StartAngle=4.71239 EndAngle=6.28319
  constraints (16):
    c: Horizontal(g0)
    c: Distance(g0) = 98
    c: Coincident(g1,g0)
    c: Block(g1)
    c: Coincident(g2,g0)
    c: Vertical(g2)
    c: Distance(g2) = 19
    c: Horizontal(g3)
    c: Coincident(g4,g1)
    c: Vertical(g4)
    c: Coincident(g3,g4)
    c: Block(g3)
    c: Coincident(g5,g2)
    c: Coincident(g5,g3)
    c: Block(g0)
    c: Block(g5)
FEATURE [Part::Extrusion] Extrude026  label="sideA001"
  Base = -> Sketch035
  Dir = (0,0,1)
  DirMode = 2
  FaceMakerClass = Part::FaceMakerBullseye
  LengthFwd = 3
  LengthRev = 0
  Placement = pos=(0,0,-2.7) rot=(0,0,1;0rad)
  Solid = true
  Symmetric = false
FEATURE [Sketcher::SketchObject] Sketch036  label="topSketch008"
  FullyConstrained = true
  sketch-geometry (6):
    g0: LineSegment StartX=19 StartY=38 StartZ=0 EndX=117 EndY=38 EndZ=0
    g1: ArcOfCircle CenterX=19 CenterY=19 CenterZ=0 NormalX=0 NormalY=0 NormalZ=1 AngleXU=0 Radius=19 StartAngle=1.5708 EndAngle=3.14159
    g2: LineSegment StartX=117 StartY=38 StartZ=0 EndX=117 EndY=19 EndZ=0
    g3: LineSegment StartX=98 StartY=1.0161e-12 StartZ=0 EndX=5.22862e-06 EndY=1.0161e-12 EndZ=0
    g4: LineSegment StartX=5.22862e-06 StartY=19 StartZ=0 EndX=5.22862e-06 EndY=1.0161e-12 EndZ=0
    g5: ArcOfCircle CenterX=98 CenterY=19 CenterZ=0 NormalX=0 NormalY=0 NormalZ=1 AngleXU=0 Radius=19 StartAngle=4.71239 EndAngle=6.28319
  constraints (16):
    c: Horizontal(g0)
    c: Distance(g0) = 98
    c: Coincident(g1,g0)
    c: Block(g1)
    c: Coincident(g2,g0)
    c: Vertical(g2)
    c: Distance(g2) = 19
    c: Horizontal(g3)
    c: Coincident(g4,g1)
    c: Vertical(g4)
    c: Coincident(g3,g4)
    c: Block(g3)
    c: Coincident(g5,g2)
    c: Coincident(g5,g3)
    c: Block(g0)
    c: Block(g5)
FEATURE [Part::Extrusion] Extrude027  label="sideB001"
  Base = -> Sketch036
  Dir = (0,0,1)
  DirMode = 2
  FaceMakerClass = Part::FaceMakerBullseye
  LengthFwd = 3
  LengthRev = 0
  Placement = pos=(0,0,71.7) rot=(0,0,1;0rad)
  Solid = true
  Symmetric = false
FEATURE [Part::MultiFuse] Fusion064  label="removeFromBottom"
  Shapes = -> [Extrude026,Extrude027]
FEATURE [Part::Cut] Cut024  label="bottom009"
  Base = -> Fusion060
  Tool = -> Fusion064
FEATURE [Sketcher::SketchObject] Sketch037  label="topSketch009"
  FullyConstrained = true
  sketch-geometry (8):
    g0: ArcOfCircle CenterX=19 CenterY=19.1201 CenterZ=0 NormalX=0 NormalY=0 NormalZ=1 AngleXU=0 Radius=18.8799 StartAngle=1.5708 EndAngle=3.14793
    g1: LineSegment StartX=0.120501 StartY=19.0004 StartZ=0 EndX=0.120501 EndY=0.000382114 EndZ=0
    g2: LineSegment StartX=19 StartY=38 StartZ=0 EndX=124 EndY=38 EndZ=0
    g3: LineSegment StartX=0.120501 StartY=0.000382114 StartZ=0 EndX=105.121 EndY=0.000382114 EndZ=0
    g4: LineSegment StartX=124 StartY=38 StartZ=0 EndX=125.616 EndY=38 EndZ=0
    g5: LineSegment StartX=105.121 StartY=0.000382114 StartZ=0 EndX=106.736 EndY=0.000382114 EndZ=0
    g6: ArcOfCircle CenterX=106.616 CenterY=19 CenterZ=0 NormalX=0 NormalY=0 NormalZ=1 AngleXU=0 Radius=19 StartAngle=4.71873 EndAngle=6.28319
    g7: LineSegment StartX=125.616 StartY=38 StartZ=0 EndX=125.616 EndY=19 EndZ=0
  constraints (21):
    c: Block(g0)
    c: Coincident(g1,g0)
    c: Vertical(g1)
    c: Horizontal(g2)
    c: Distance(g2) = 105
    c: Coincident(g2,g0)
    c: Distance(g1) = 19
    c: Coincident(g3,g1)
    c: Horizontal(g3)
    c: Distance(g3) = 105
    c: Coincident(g4,g2)
    c: Horizontal(g4)
    c: Distance(g4) = 1.61553
    c: Horizontal(g5)
    c: Equal(g4,g5) = 1.61553
    c: Coincident(g5,g3)
    c: Block(g6)
    c: Coincident(g6,g5)
    c: Coincident(g7,g4)
    c: Coincident(g7,g6)
    c: Vertical(g7)
FEATURE [Part::Extrusion] Extrude028  label="sideB"
  Base = -> Sketch037
  Dir = (0,0,1)
  DirMode = 2
  FaceMakerClass = Part::FaceMakerBullseye
  LengthFwd = 3
  LengthRev = 0
  Placement = pos=(0,0,72) rot=(0,0,1;0rad)
  Solid = true
  Symmetric = false
FEATURE [Sketcher::SketchObject] Sketch038  label="topSketch010"
  FullyConstrained = true
  sketch-geometry (22):
    g0: LineSegment StartX=5.21097e-06 StartY=3 StartZ=0 EndX=5.21097e-06 EndY=19 EndZ=0
    g1: ArcOfCircle CenterX=19 CenterY=19 CenterZ=0 NormalX=0 NormalY=0 NormalZ=1 AngleXU=0 Radius=19 StartAngle=1.5708 EndAngle=3.14159
    g2: ArcOfCircle CenterX=19 CenterY=19 CenterZ=0 NormalX=0 NormalY=0 NormalZ=1 AngleXU=0 Radius=16 StartAngle=1.5708 EndAngle=3.14159
    g3: LineSegment StartX=114 StartY=35 StartZ=0 EndX=19 EndY=35 EndZ=0
    g4: LineSegment StartX=5.21097e-06 StartY=3 StartZ=0 EndX=5.21097e-06 EndY=0 EndZ=0
    g5: LineSegment StartX=3 StartY=0 StartZ=0 EndX=5.21097e-06 EndY=0 EndZ=0
    g6: LineSegment StartX=3 StartY=19 StartZ=0 EndX=3 EndY=0 EndZ=0
    g7: LineSegment StartX=19 StartY=38 StartZ=0 EndX=124 EndY=38 EndZ=0
    g8: Circle CenterX=119 CenterY=35 CenterZ=0 NormalX=0 NormalY=0 NormalZ=1 AngleXU=0 Radius=1
    g9: Circle CenterX=121 CenterY=35 CenterZ=0 NormalX=0 NormalY=0 NormalZ=1 AngleXU=0 Radius=1
    g10: Circle CenterX=121 CenterY=33 CenterZ=0 NormalX=0 NormalY=0 NormalZ=1 AngleXU=0 Radius=1
    g11: BSplineCurve PolesCount=3 KnotsCount=2 Degree=2 IsPeriodic=0
    g12: GeomPoint X=119 Y=35 Z=0
    g13: GeomPoint X=121 Y=33 Z=0
    g14: LineSegment StartX=119 StartY=35 StartZ=0 EndX=114 EndY=35 EndZ=0
    g15: ArcOfCircle CenterX=105 CenterY=19 CenterZ=0 NormalX=0 NormalY=0 NormalZ=1 AngleXU=0 Radius=16 StartAngle=5.60905 EndAngle=6.28319
    g16: LineSegment StartX=121 StartY=33 StartZ=0 EndX=121 EndY=19 EndZ=0
    g17: LineSegment StartX=117.5 StartY=9.01251 StartZ=0 EndX=121.163 EndY=9.0125 EndZ=0
    g18: ArcOfCircle CenterX=105 CenterY=19 CenterZ=0 NormalX=0 NormalY=0 NormalZ=1 AngleXU=0 Radius=20.6155 StartAngle=5.7297 EndAngle=6.28319
    g19: LineSegment StartX=121.163 StartY=9.0125 StartZ=0 EndX=122.538 EndY=8.16329 EndZ=0
    g20: LineSegment StartX=124 StartY=38 StartZ=0 EndX=125.616 EndY=38 EndZ=0
    g21: LineSegment StartX=125.616 StartY=19 StartZ=0 EndX=125.616 EndY=38 EndZ=0
  constraints (49):
    c: Vertical(g0)
    c: Block(g0)
    c: Coincident(g1,g0)
    c: Block(g1)
    c: Coincident(g2,g1)
    c: Block(g2)
    c: Coincident(g3,g2)
    c: Horizontal(g3)
    c: Tangent(g3,g2)
    c: Coincident(g4,g0)
    c: Distance(g4) = 3
    c: Vertical(g4)
    c: Coincident(g5,g4)
    c: Horizontal(g5)
    c: Coincident(g6,g2)
    c: Coincident(g6,g5)
    c: Vertical(g6)
    c: Horizontal(g7)
    c: Distance(g7) = 105
    c: Coincident(g7,g1)
    c: Block(g3)
    c: Weight(g8) = 1
    c: Equal(g8,g9)
    c: Equal(g8,g10)
    c: InternalAlignment(g8,g11)
    c: InternalAlignment(g9,g11)
    c: InternalAlignment(g10,g11)
    c: InternalAlignment(g12,g11)
    c: InternalAlignment(g13,g11)
    c: Block(g11)
    c: Coincident(g14,g11)
    c: Coincident(g14,g3)
    c: Horizontal(g14)
    c: Block(g15)
    c: Coincident(g16,g11)
    c: Coincident(g16,g15)
    c: Vertical(g16)
    c: Distance(g16) = 14
    c: Coincident(g17,g15)
    c: Block(g18)
    c: Coincident(g19,g18)
    c: Coincident(g20,g7)
    c: Horizontal(g20)
    c: Vertical(g21)
    c: Coincident(g20,g21)
    c: Block(g20)
    c: Block(g21)
    c: Block(g19)
    c: Block(g17)
FEATURE [Part::Extrusion] Extrude029
  Base = -> Sketch038
  Dir = (0,0,1)
  DirMode = 2
  FaceMakerClass = Part::FaceMakerBullseye
  LengthFwd = 72
  LengthRev = 0
  Solid = true
  Symmetric = false
FEATURE [Part::Feature] Face085
  shape: bbox 4.8 x 25.5 x 2e-07 mm, 1 faces, 0 solids (baked)
FEATURE [Part::Revolution] Revolve089  label="moreFrontCaseScrewPost003"
  Angle = 360
  Axis = (0,1,0)
  Base = (0,0,0)
  FaceMakerClass = Part::FaceMakerBullseye
  Placement = pos=(109.5,4.5,3.5) rot=(0,0,1;0rad)
  Solid = false
  Source = -> Face085
  Symmetric = false
FEATURE [Part::Feature] Face086
  shape: bbox 4.8 x 25.5 x 2e-07 mm, 1 faces, 0 solids (baked)
FEATURE [Part::Revolution] Revolve090  label="moreFrontCaseScrewPost004"
  Angle = 360
  Axis = (0,1,0)
  Base = (0,0,0)
  FaceMakerClass = Part::FaceMakerBullseye
  Placement = pos=(109.5,4.5,68.5) rot=(0,0,1;0rad)
  Solid = false
  Source = -> Face086
  Symmetric = false
FEATURE [Part::Fillet] Fillet026  label="top013"
  Base = -> Extrude029
  Edges = 1 edges r=2: [Edge35]
FEATURE [Sketcher::SketchObject] Sketch039
  FullyConstrained = true
  sketch-geometry (7):
    g0: LineSegment StartX=0 StartY=0 StartZ=0 EndX=0 EndY=6 EndZ=0
    g1: Circle CenterX=0 CenterY=0 CenterZ=0 NormalX=0 NormalY=0 NormalZ=1 AngleXU=0 Radius=1
    g2: Circle CenterX=8 CenterY=6 CenterZ=0 NormalX=0 NormalY=0 NormalZ=1 AngleXU=0 Radius=1
    g3: BSplineCurve PolesCount=3 KnotsCount=2 Degree=2 IsPeriodic=0
    g4: GeomPoint X=0 Y=0 Z=0
    g5: GeomPoint X=8 Y=6 Z=0
    g6: LineSegment StartX=0 StartY=6 StartZ=0 EndX=8 EndY=6 EndZ=0
  constraints (14):
    c: Coincident(g0,g-1)
    c: Distance(g0) = 6
    c: Vertical(g0)
    c: Coincident(g3,g0)
    c: Weight(g1) = 1
    c: Equal(g1,g2)
    c: InternalAlignment(g1,g3)
    c: InternalAlignment(g2,g3)
    c: InternalAlignment(g4,g3)
    c: InternalAlignment(g5,g3)
    c: Block(g3)
    c: Coincident(g6,g0)
    c: Coincident(g6,g3)
    c: Horizontal(g6)
FEATURE [Sketcher::SketchObject] Sketch040
  FullyConstrained = true
  sketch-geometry (7):
    g0: LineSegment StartX=0 StartY=0 StartZ=0 EndX=0 EndY=6 EndZ=0
    g1: Circle CenterX=0 CenterY=0 CenterZ=0 NormalX=0 NormalY=0 NormalZ=1 AngleXU=0 Radius=1
    g2: Circle CenterX=8 CenterY=6 CenterZ=0 NormalX=0 NormalY=0 NormalZ=1 AngleXU=0 Radius=1
    g3: BSplineCurve PolesCount=3 KnotsCount=2 Degree=2 IsPeriodic=0
    g4: GeomPoint X=0 Y=0 Z=0
    g5: GeomPoint X=8 Y=6 Z=0
    g6: LineSegment StartX=0 StartY=6 StartZ=0 EndX=8 EndY=6 EndZ=0
  constraints (14):
    c: Coincident(g0,g-1)
    c: Distance(g0) = 6
    c: Vertical(g0)
    c: Coincident(g3,g0)
    c: Weight(g1) = 1
    c: Equal(g1,g2)
    c: InternalAlignment(g1,g3)
    c: InternalAlignment(g2,g3)
    c: InternalAlignment(g4,g3)
    c: InternalAlignment(g5,g3)
    c: Block(g3)
    c: Coincident(g6,g0)
    c: Coincident(g6,g3)
    c: Horizontal(g6)
FEATURE [Sketcher::SketchObject] Sketch041
  FullyConstrained = true
  sketch-geometry (7):
    g0: LineSegment StartX=0 StartY=0 StartZ=0 EndX=0 EndY=6 EndZ=0
    g1: Circle CenterX=0 CenterY=0 CenterZ=0 NormalX=0 NormalY=0 NormalZ=1 AngleXU=0 Radius=1
    g2: Circle CenterX=8 CenterY=6 CenterZ=0 NormalX=0 NormalY=0 NormalZ=1 AngleXU=0 Radius=1
    g3: BSplineCurve PolesCount=3 KnotsCount=2 Degree=2 IsPeriodic=0
    g4: GeomPoint X=0 Y=0 Z=0
    g5: GeomPoint X=8 Y=6 Z=0
    g6: LineSegment StartX=0 StartY=6 StartZ=0 EndX=8 EndY=6 EndZ=0
  constraints (14):
    c: Coincident(g0,g-1)
    c: Distance(g0) = 6
    c: Vertical(g0)
    c: Coincident(g3,g0)
    c: Weight(g1) = 1
    c: Equal(g1,g2)
    c: InternalAlignment(g1,g3)
    c: InternalAlignment(g2,g3)
    c: InternalAlignment(g4,g3)
    c: InternalAlignment(g5,g3)
    c: Block(g3)
    c: Coincident(g6,g0)
    c: Coincident(g6,g3)
    c: Horizontal(g6)
FEATURE [Sketcher::SketchObject] Sketch042
  FullyConstrained = true
  sketch-geometry (7):
    g0: LineSegment StartX=0 StartY=0 StartZ=0 EndX=0 EndY=6 EndZ=0
    g1: Circle CenterX=0 CenterY=0 CenterZ=0 NormalX=0 NormalY=0 NormalZ=1 AngleXU=0 Radius=1
    g2: Circle CenterX=8 CenterY=6 CenterZ=0 NormalX=0 NormalY=0 NormalZ=1 AngleXU=0 Radius=1
    g3: BSplineCurve PolesCount=3 KnotsCount=2 Degree=2 IsPeriodic=0
    g4: GeomPoint X=0 Y=0 Z=0
    g5: GeomPoint X=8 Y=6 Z=0
    g6: LineSegment StartX=0 StartY=6 StartZ=0 EndX=8 EndY=6 EndZ=0
  constraints (14):
    c: Coincident(g0,g-1)
    c: Distance(g0) = 6
    c: Vertical(g0)
    c: Coincident(g3,g0)
    c: Weight(g1) = 1
    c: Equal(g1,g2)
    c: InternalAlignment(g1,g3)
    c: InternalAlignment(g2,g3)
    c: InternalAlignment(g4,g3)
    c: InternalAlignment(g5,g3)
    c: Block(g3)
    c: Coincident(g6,g0)
    c: Coincident(g6,g3)
    c: Horizontal(g6)
FEATURE [Part::Extrusion] Extrude030  label="caseScrewPillarBracket008"
  Base = -> Sketch039
  Dir = (0,0,1)
  DirMode = 2
  FaceMakerClass = Part::FaceMakerBullseye
  LengthFwd = 2.4
  LengthRev = 0
  Placement = pos=(15.76,29,8.8) rot=(0,1,0;0rad)
  Solid = true
  Symmetric = false
FEATURE [Part::Extrusion] Extrude031  label="caseScrewPillarBracket009"
  Base = -> Sketch040
  Dir = (0,0,1)
  DirMode = 2
  FaceMakerClass = Part::FaceMakerBullseye
  LengthFwd = 2.4
  LengthRev = 0
  Placement = pos=(15.76,29,60.8) rot=(0,0,1;0rad)
  Solid = true
  Symmetric = false
FEATURE [Part::Extrusion] Extrude032  label="caseScrewPillarBracket010"
  Base = -> Sketch041
  Dir = (0,0,1)
  DirMode = 2
  FaceMakerClass = Part::FaceMakerBullseye
  LengthFwd = 2.4
  LengthRev = 0
  Placement = pos=(13.7,29,13.26) rot=(0,-1,0;1.5708rad)
  Solid = true
  Symmetric = false
FEATURE [Part::Extrusion] Extrude033  label="caseScrewPillarBracket011"
  Base = -> Sketch042
  Dir = (0,0,1)
  DirMode = 2
  FaceMakerClass = Part::FaceMakerBullseye
  LengthFwd = 2.4
  LengthRev = 0
  Placement = pos=(11.3,29,58.74) rot=(0,1,0;1.5708rad)
  Solid = true
  Symmetric = false
FEATURE [Sketcher::SketchObject] Sketch043
  FullyConstrained = true
  sketch-geometry (7):
    g0: LineSegment StartX=0 StartY=0 StartZ=0 EndX=0 EndY=6 EndZ=0
    g1: Circle CenterX=0 CenterY=0 CenterZ=0 NormalX=0 NormalY=0 NormalZ=1 AngleXU=0 Radius=1
    g2: Circle CenterX=8 CenterY=6 CenterZ=0 NormalX=0 NormalY=0 NormalZ=1 AngleXU=0 Radius=1
    g3: BSplineCurve PolesCount=3 KnotsCount=2 Degree=2 IsPeriodic=0
    g4: GeomPoint X=0 Y=0 Z=0
    g5: GeomPoint X=8 Y=6 Z=0
    g6: LineSegment StartX=0 StartY=6 StartZ=0 EndX=8 EndY=6 EndZ=0
  constraints (14):
    c: Coincident(g0,g-1)
    c: Distance(g0) = 6
    c: Vertical(g0)
    c: Coincident(g3,g0)
    c: Weight(g1) = 1
    c: Equal(g1,g2)
    c: InternalAlignment(g1,g3)
    c: InternalAlignment(g2,g3)
    c: InternalAlignment(g4,g3)
    c: InternalAlignment(g5,g3)
    c: Block(g3)
    c: Coincident(g6,g0)
    c: Coincident(g6,g3)
    c: Horizontal(g6)
FEATURE [Part::Extrusion] Extrude034  label="caseScrewPillarBracket012"
  Base = -> Sketch043
  Dir = (0,0,1)
  DirMode = 2
  FaceMakerClass = Part::FaceMakerBullseye
  LengthFwd = 2.4
  LengthRev = 0
  Placement = pos=(88.3,29,65.23) rot=(0,1,0;1.5708rad)
  Solid = true
  Symmetric = false
FEATURE [Sketcher::SketchObject] Sketch044
  FullyConstrained = true
  sketch-geometry (7):
    g0: LineSegment StartX=0 StartY=0 StartZ=0 EndX=0 EndY=6 EndZ=0
    g1: Circle CenterX=0 CenterY=0 CenterZ=0 NormalX=0 NormalY=0 NormalZ=1 AngleXU=0 Radius=1
    g2: Circle CenterX=8 CenterY=6 CenterZ=0 NormalX=0 NormalY=0 NormalZ=1 AngleXU=0 Radius=1
    g3: BSplineCurve PolesCount=3 KnotsCount=2 Degree=2 IsPeriodic=0
    g4: GeomPoint X=0 Y=0 Z=0
    g5: GeomPoint X=8 Y=6 Z=0
    g6: LineSegment StartX=0 StartY=6 StartZ=0 EndX=8 EndY=6 EndZ=0
  constraints (14):
    c: Coincident(g0,g-1)
    c: Distance(g0) = 6
    c: Vertical(g0)
    c: Coincident(g3,g0)
    c: Weight(g1) = 1
    c: Equal(g1,g2)
    c: InternalAlignment(g1,g3)
    c: InternalAlignment(g2,g3)
    c: InternalAlignment(g4,g3)
    c: InternalAlignment(g5,g3)
    c: Block(g3)
    c: Coincident(g6,g0)
    c: Coincident(g6,g3)
    c: Horizontal(g6)
FEATURE [Part::Extrusion] Extrude035  label="caseScrewPillarBracket013"
  Base = -> Sketch044
  Dir = (0,0,1)
  DirMode = 2
  FaceMakerClass = Part::FaceMakerBullseye
  LengthFwd = 2.4
  LengthRev = 0
  Placement = pos=(90.7,29,6.77) rot=(0,-1,0;1.5708rad)
  Solid = true
  Symmetric = false
FEATURE [Sketcher::SketchObject] Sketch045
  FullyConstrained = true
  sketch-geometry (7):
    g0: LineSegment StartX=0 StartY=0 StartZ=0 EndX=0 EndY=6 EndZ=0
    g1: Circle CenterX=0 CenterY=0 CenterZ=0 NormalX=0 NormalY=0 NormalZ=1 AngleXU=0 Radius=1
    g2: Circle CenterX=8 CenterY=6 CenterZ=0 NormalX=0 NormalY=0 NormalZ=1 AngleXU=0 Radius=1
    g3: BSplineCurve PolesCount=3 KnotsCount=2 Degree=2 IsPeriodic=0
    g4: GeomPoint X=0 Y=0 Z=0
    g5: GeomPoint X=8 Y=6 Z=0
    g6: LineSegment StartX=0 StartY=6 StartZ=0 EndX=8 EndY=6 EndZ=0
  constraints (14):
    c: Coincident(g0,g-1)
    c: Distance(g0) = 6
    c: Vertical(g0)
    c: Coincident(g3,g0)
    c: Weight(g1) = 1
    c: Equal(g1,g2)
    c: InternalAlignment(g1,g3)
    c: InternalAlignment(g2,g3)
    c: InternalAlignment(g4,g3)
    c: InternalAlignment(g5,g3)
    c: Block(g3)
    c: Coincident(g6,g0)
    c: Coincident(g6,g3)
    c: Horizontal(g6)
FEATURE [Sketcher::SketchObject] Sketch046
  FullyConstrained = true
  sketch-geometry (7):
    g0: LineSegment StartX=0 StartY=0 StartZ=0 EndX=0 EndY=6 EndZ=0
    g1: Circle CenterX=0 CenterY=0 CenterZ=0 NormalX=0 NormalY=0 NormalZ=1 AngleXU=0 Radius=1
    g2: Circle CenterX=8 CenterY=6 CenterZ=0 NormalX=0 NormalY=0 NormalZ=1 AngleXU=0 Radius=1
    g3: BSplineCurve PolesCount=3 KnotsCount=2 Degree=2 IsPeriodic=0
    g4: GeomPoint X=0 Y=0 Z=0
    g5: GeomPoint X=8 Y=6 Z=0
    g6: LineSegment StartX=0 StartY=6 StartZ=0 EndX=8 EndY=6 EndZ=0
  constraints (14):
    c: Coincident(g0,g-1)
    c: Distance(g0) = 6
    c: Vertical(g0)
    c: Coincident(g3,g0)
    c: Weight(g1) = 1
    c: Equal(g1,g2)
    c: InternalAlignment(g1,g3)
    c: InternalAlignment(g2,g3)
    c: InternalAlignment(g4,g3)
    c: InternalAlignment(g5,g3)
    c: Block(g3)
    c: Coincident(g6,g0)
    c: Coincident(g6,g3)
    c: Horizontal(g6)
FEATURE [Part::Extrusion] Extrude036  label="caseScrewPillarBracket014"
  Base = -> Sketch045
  Dir = (0,0,1)
  DirMode = 2
  FaceMakerClass = Part::FaceMakerBullseye
  LengthFwd = 2.4
  LengthRev = 0
  Placement = pos=(110.7,29,6.77) rot=(0,-1,0;1.5708rad)
  Solid = true
  Symmetric = false
FEATURE [Part::Extrusion] Extrude037  label="caseScrewPillarBracket015"
  Base = -> Sketch046
  Dir = (0,0,1)
  DirMode = 2
  FaceMakerClass = Part::FaceMakerBullseye
  LengthFwd = 2.4
  LengthRev = 0
  Placement = pos=(108.3,29,65.23) rot=(0,1,0;1.5708rad)
  Solid = true
  Symmetric = false
FEATURE [Part::Box] Box013  label="frontCaseScrewPillarBracket002"
  AttacherType = Attacher::AttachEngine3D
  Height = 2.4
  Length = 22
  Placement = pos=(87,28,2.3) rot=(0,0,1;0rad)
  Width = 7
FEATURE [Part::Box] Box014  label="frontCaseScrewPillarBracket003"
  AttacherType = Attacher::AttachEngine3D
  Height = 2.4
  Length = 22
  Placement = pos=(87,28,67.3) rot=(0,0,1;0rad)
  Width = 7
FEATURE [Part::Feature] Face087
  shape: bbox 4.8 x 30.2 x 2e-07 mm, 1 faces, 0 solids (baked)
FEATURE [Part::Revolution] Revolve091  label="frontCaseScrewPost004"
  Angle = 360
  Axis = (0,1,0)
  Base = (0,0,0)
  FaceMakerClass = Part::FaceMakerBullseye
  Placement = pos=(89.5,4.5,3.5) rot=(0,0,1;0rad)
  Solid = false
  Source = -> Face087
  Symmetric = false
FEATURE [Part::Feature] Face088
  shape: bbox 4.8 x 30.2 x 2e-07 mm, 1 faces, 0 solids (baked)
FEATURE [Part::Revolution] Revolve092  label="frontCaseScrewPost005"
  Angle = 360
  Axis = (0,1,0)
  Base = (0,0,0)
  FaceMakerClass = Part::FaceMakerBullseye
  Placement = pos=(89.5,4.5,68.5) rot=(0,0,1;0rad)
  Solid = false
  Source = -> Face088
  Symmetric = false
FEATURE [Part::Feature] Face089
  shape: bbox 3.5 x 30.2 x 2e-07 mm, 1 faces, 0 solids (baked)
FEATURE [Part::Revolution] Revolve093  label="backCaseScrewPost002"
  Angle = 360
  Axis = (0,1,0)
  Base = (0,0,0)
  FaceMakerClass = Part::FaceMakerBullseye
  Placement = pos=(12.5,4.5,10) rot=(0,0,1;0rad)
  Solid = false
  Source = -> Face089
  Symmetric = false
FEATURE [Part::Feature] Face090
  shape: bbox 3.5 x 30.2 x 2e-07 mm, 1 faces, 0 solids (baked)
FEATURE [Part::Revolution] Revolve094  label="backCaseScrewPost003"
  Angle = 360
  Axis = (0,1,0)
  Base = (0,0,0)
  FaceMakerClass = Part::FaceMakerBullseye
  Placement = pos=(12.5,4.5,62) rot=(0,0,1;0rad)
  Solid = false
  Source = -> Face090
  Symmetric = false
FEATURE [Part::Box] Box015  label="Cube011"
  AttacherType = Attacher::AttachEngine3D
  Height = 28.8
  Length = 3
  Placement = pos=(107.3,28,21.6) rot=(0,0,1;0rad)
  Width = 7
FEATURE [Part::Box] Box016  label="Cube012"
  AttacherType = Attacher::AttachEngine3D
  Height = 3
  Length = 7.4
  Placement = pos=(107.3,28,18.6) rot=(0,0,1;0rad)
  Width = 7
FEATURE [Part::Box] Box017  label="Cube013"
  AttacherType = Attacher::AttachEngine3D
  Height = 3
  Length = 7.4
  Placement = pos=(107.3,28,50.4) rot=(0,0,1;0rad)
  Width = 7
FEATURE [Part::Cylinder] Cylinder024
  Angle = 360
  AttacherType = Attacher::AttachEngine3D
  Height = 20
  Placement = pos=(0,0,36.15) rot=(0,0,1;0rad)
  Radius = 14.3
FEATURE [Part::Cylinder] Cylinder025
  Angle = 360
  AttacherType = Attacher::AttachEngine3D
  Height = 10
  Placement = pos=(0,0,36.15) rot=(0,0,1;0rad)
  Radius = 4
FEATURE [Part::MultiFuse] Fusion066  label="removeToCreteHoleForPlugHousing009"
  Placement = pos=(70,19,36) rot=(0,1,0;1.5708rad)
  Shapes = -> [Cylinder024,Cylinder025]
FEATURE [Part::MultiFuse] Fusion065  label="plugHousingBracketHolder002"
  Shapes = -> [Box017,Box015,Box016]
FEATURE [Part::Cut] Cut025  label="plugHousingBracketHolder003"
  Base = -> Fusion065
  Placement = pos=(7,0,0) rot=(0,0,1;0rad)
  Tool = -> Fusion066
FEATURE [Sketcher::SketchObject] Sketch047
  FullyConstrained = false
  Placement = pos=(0,0,0) rot=(1,0,0;1.5708rad)
  sketch-geometry (24):
    g0: ArcOfCircle CenterX=-4 CenterY=-10.5 CenterZ=0 NormalX=0 NormalY=0 NormalZ=1 AngleXU=0 Radius=1.5 StartAngle=6e-16 EndAngle=3.14159
    g1: ArcOfCircle CenterX=-34.2 CenterY=-10.5 CenterZ=0 NormalX=0 NormalY=0 NormalZ=1 AngleXU=0 Radius=1.5 StartAngle=0 EndAngle=3.14159
    g2: ArcOfCircle CenterX=-34.2 CenterY=-27.7 CenterZ=0 NormalX=0 NormalY=0 NormalZ=1 AngleXU=0 Radius=1.5 StartAngle=3.14159 EndAngle=6.28319
    g3: ArcOfCircle CenterX=-4 CenterY=-27.7 CenterZ=0 NormalX=0 NormalY=0 NormalZ=1 AngleXU=0 Radius=1.5 StartAngle=3.1416 EndAngle=6.28319
    g4: ArcOfCircle CenterX=-10 CenterY=-4.3 CenterZ=0 NormalX=0 NormalY=0 NormalZ=1 AngleXU=0 Radius=1.5 StartAngle=2e-16 EndAngle=3.14159
    g5: ArcOfCircle CenterX=-16.1 CenterY=-1.8 CenterZ=0 NormalX=0 NormalY=0 NormalZ=1 AngleXU=0 Radius=1.5 StartAngle=5e-16 EndAngle=3.14159
    g6: ArcOfCircle CenterX=-22.1 CenterY=-1.8 CenterZ=0 NormalX=0 NormalY=0 NormalZ=1 AngleXU=0 Radius=1.5 StartAngle=5e-16 EndAngle=3.14159
    g7: ArcOfCircle CenterX=-28.2 CenterY=-4.3 CenterZ=0 NormalX=0 NormalY=0 NormalZ=1 AngleXU=0 Radius=1.5 StartAngle=2e-16 EndAngle=3.14159
    g8: ArcOfCircle CenterX=-10 CenterY=-33.9 CenterZ=0 NormalX=0 NormalY=0 NormalZ=1 AngleXU=0 Radius=1.5 StartAngle=3.14159 EndAngle=6.28319
    g9: ArcOfCircle CenterX=-16.1 CenterY=-36.4 CenterZ=0 NormalX=0 NormalY=0 NormalZ=1 AngleXU=0 Radius=1.5 StartAngle=3.14159 EndAngle=6.28319
    g10: ArcOfCircle CenterX=-22.1 CenterY=-36.4 CenterZ=0 NormalX=0 NormalY=0 NormalZ=1 AngleXU=0 Radius=1.5 StartAngle=3.14159 EndAngle=6.28319
    g11: ArcOfCircle CenterX=-28.2 CenterY=-33.9 CenterZ=0 NormalX=0 NormalY=0 NormalZ=1 AngleXU=0 Radius=1.5 StartAngle=3.14159 EndAngle=6.28319
    g12: LineSegment StartX=-35.7 StartY=-10.5 StartZ=0 EndX=-35.7 EndY=-27.7 EndZ=0
    g13: LineSegment StartX=-32.7 StartY=-10.5 StartZ=0 EndX=-32.7 EndY=-27.7 EndZ=0
    g14: LineSegment StartX=-29.7 StartY=-33.9 StartZ=0 EndX=-29.7 EndY=-4.3 EndZ=0
    g15: LineSegment StartX=-26.7 StartY=-33.9 StartZ=0 EndX=-26.7 EndY=-4.3 EndZ=0
    g16: LineSegment StartX=-2.5 StartY=-10.5 StartZ=0 EndX=-2.5 EndY=-27.7 EndZ=0
    g17: LineSegment StartX=-8.5 StartY=-4.3 StartZ=0 EndX=-8.5 EndY=-33.9 EndZ=0
    g18: LineSegment StartX=-5.5 StartY=-10.5 StartZ=0 EndX=-5.5 EndY=-27.7 EndZ=0
    g19: LineSegment StartX=-11.5 StartY=-4.3 StartZ=0 EndX=-11.5 EndY=-33.9 EndZ=0
    g20: LineSegment StartX=-14.6 StartY=-1.8 StartZ=0 EndX=-14.6 EndY=-36.4 EndZ=0
    g21: LineSegment StartX=-17.6 StartY=-1.8 StartZ=0 EndX=-17.6 EndY=-36.4 EndZ=0
    g22: LineSegment StartX=-20.6 StartY=-36.4 StartZ=0 EndX=-20.6 EndY=-1.8 EndZ=0
    g23: LineSegment StartX=-23.6 StartY=-1.8 StartZ=0 EndX=-23.6 EndY=-36.4 EndZ=0
  constraints (48):
    c: Block(g0)
    c: Block(g1)
    c: Block(g2)
    c: Block(g3)
    c: Block(g4)
    c: Block(g5)
    c: Block(g6)
    c: Block(g7)
    c: Block(g8)
    c: Block(g9)
    c: Block(g10)
    c: Block(g11)
    c: Coincident(g12,g1)
    c: Coincident(g12,g2)
    c: Vertical(g12)
    c: Coincident(g13,g1)
    c: Coincident(g13,g2)
    c: Vertical(g13)
    c: Coincident(g14,g11)
    c: Coincident(g14,g7)
    c: Vertical(g14)
    c: Coincident(g15,g11)
    c: Coincident(g15,g7)
    c: Vertical(g15)
    c: Coincident(g16,g0)
    c: Coincident(g16,g3)
    c: Vertical(g16)
    c: Coincident(g17,g4)
    c: Coincident(g17,g8)
    c: Vertical(g17)
    c: Coincident(g18,g0)
    c: Coincident(g18,g3)
    c: Vertical(g18)
    c: Coincident(g19,g4)
    c: Coincident(g19,g8)
    c: Vertical(g19)
    c: Coincident(g20,g5)
    c: Coincident(g20,g9)
    c: Vertical(g20)
    c: Coincident(g21,g5)
    c: Coincident(g21,g9)
    c: Vertical(g21)
    c: Coincident(g22,g10)
    c: Coincident(g22,g6)
    c: Vertical(g22)
    c: Coincident(g23,g6)
    c: Coincident(g23,g10)
    c: Vertical(g23)
FEATURE [Part::Extrusion] Extrude038  label="removeToCreateFanGrillHoles001"
  Base = -> Sketch047
  Dir = (0,-1,6e-16)
  DirMode = 2
  FaceMakerClass = Part::FaceMakerBullseye
  LengthFwd = 10
  LengthRev = 0
  Placement = pos=(65.4,44,54.82) rot=(0,0,1;0rad)
  Solid = true
  Symmetric = false
FEATURE [Part::Feature] Wire004
  shape: bbox 11 x 5.2 x 2e-07 mm, 0 faces, 0 solids (baked)
FEATURE [Part::Revolution] Revolve095
  Angle = 360
  Axis = (0,1,0)
  Base = (0,0,0)
  FaceMakerClass = Part::FaceMakerBullseye
  Placement = pos=(30.3,38,19.7) rot=(0,0,1;0rad)
  Solid = true
  Source = -> Wire004
  Symmetric = false
FEATURE [Part::Feature] Wire005
  shape: bbox 11 x 5.2 x 2e-07 mm, 0 faces, 0 solids (baked)
FEATURE [Part::Revolution] Revolve096
  Angle = 360
  Axis = (0,1,0)
  Base = (0,0,0)
  FaceMakerClass = Part::FaceMakerBullseye
  Placement = pos=(30.3,38,51.7) rot=(0,0,1;0rad)
  Solid = true
  Source = -> Wire005
  Symmetric = false
FEATURE [Part::Feature] Wire006
  shape: bbox 11 x 5.2 x 2e-07 mm, 0 faces, 0 solids (baked)
FEATURE [Part::Revolution] Revolve097
  Angle = 360
  Axis = (0,1,0)
  Base = (0,0,0)
  FaceMakerClass = Part::FaceMakerBullseye
  Placement = pos=(62.3,38,51.7) rot=(0,0,1;0rad)
  Solid = true
  Source = -> Wire006
  Symmetric = false
FEATURE [Part::Feature] Wire007
  shape: bbox 11 x 5.2 x 2e-07 mm, 0 faces, 0 solids (baked)
FEATURE [Part::Revolution] Revolve098
  Angle = 360
  Axis = (0,1,0)
  Base = (0,0,0)
  FaceMakerClass = Part::FaceMakerBullseye
  Placement = pos=(62.3,38,19.7) rot=(0,0,1;0rad)
  Solid = true
  Source = -> Wire007
  Symmetric = false
FEATURE [Part::MultiFuse] Fusion067  label="fanScrewHousing002"
  Shapes = -> [Revolve098,Revolve097,Revolve096,Revolve095]
FEATURE [Part::Feature] Face091 .. Face094  x4 (patterned run collapsed; names and placements below)
  shape: bbox 3.5 x 17.8 x 2e-07 mm, 1 faces, 0 solids (baked)
FEATURE [Part::Revolution] Revolve099  label="removeToCreateScrewAndThreadedInsertHole026"
  Angle = 360
  Axis = (0,1,0)
  Base = (0,0,0)
  FaceMakerClass = Part::FaceMakerBullseye
  Placement = pos=(62.3,30.3,19.7) rot=(0,0,1;0rad)
  Solid = false
  Source = -> Face091
  Symmetric = false
FEATURE [Part::Revolution] Revolve100  label="removeToCreateScrewAndThreadedInsertHole027"
  Angle = 360
  Axis = (0,1,0)
  Base = (0,0,0)
  FaceMakerClass = Part::FaceMakerBullseye
  Placement = pos=(62.3,30.3,51.7) rot=(0,0,1;0rad)
  Solid = false
  Source = -> Face092
  Symmetric = false
FEATURE [Part::Revolution] Revolve101  label="removeToCreateScrewAndThreadedInsertHole028"
  Angle = 360
  Axis = (0,1,0)
  Base = (0,0,0)
  FaceMakerClass = Part::FaceMakerBullseye
  Placement = pos=(30.3,30.3,19.7) rot=(0,0,1;0rad)
  Solid = false
  Source = -> Face093
  Symmetric = false
FEATURE [Part::Revolution] Revolve102  label="removeToCreateScrewAndThreadedInsertHole029"
  Angle = 360
  Axis = (0,1,0)
  Base = (0,0,0)
  FaceMakerClass = Part::FaceMakerBullseye
  Placement = pos=(30.3,30.3,51.7) rot=(0,0,1;0rad)
  Solid = false
  Source = -> Face094
  Symmetric = false
FEATURE [Part::MultiFuse] Fusion068  label="createThreadedInsertHolesForFan002"
  Shapes = -> [Revolve099,Revolve100,Revolve101,Revolve102]
FEATURE [Part::Cut] Cut026  label="fanScrewHousing003"
  Base = -> Fusion067
  Tool = -> Fusion068
FEATURE [Sketcher::SketchObject] Sketch048
  FullyConstrained = false
  Placement = pos=(0,0,0) rot=(1,0,0;1.5708rad)
  sketch-geometry (24):
    g0: ArcOfCircle CenterX=-4 CenterY=-10.5 CenterZ=0 NormalX=0 NormalY=0 NormalZ=1 AngleXU=0 Radius=1.5 StartAngle=6e-16 EndAngle=3.14159
    g1: ArcOfCircle CenterX=-34.2 CenterY=-10.5 CenterZ=0 NormalX=0 NormalY=0 NormalZ=1 AngleXU=0 Radius=1.5 StartAngle=0 EndAngle=3.14159
    g2: ArcOfCircle CenterX=-34.2 CenterY=-27.7 CenterZ=0 NormalX=0 NormalY=0 NormalZ=1 AngleXU=0 Radius=1.5 StartAngle=3.14159 EndAngle=6.28319
    g3: ArcOfCircle CenterX=-4 CenterY=-27.7 CenterZ=0 NormalX=0 NormalY=0 NormalZ=1 AngleXU=0 Radius=1.5 StartAngle=3.1416 EndAngle=6.28319
    g4: ArcOfCircle CenterX=-10 CenterY=-4.3 CenterZ=0 NormalX=0 NormalY=0 NormalZ=1 AngleXU=0 Radius=1.5 StartAngle=2e-16 EndAngle=3.14159
    g5: ArcOfCircle CenterX=-16.1 CenterY=-1.8 CenterZ=0 NormalX=0 NormalY=0 NormalZ=1 AngleXU=0 Radius=1.5 StartAngle=5e-16 EndAngle=3.14159
    g6: ArcOfCircle CenterX=-22.1 CenterY=-1.8 CenterZ=0 NormalX=0 NormalY=0 NormalZ=1 AngleXU=0 Radius=1.5 StartAngle=5e-16 EndAngle=3.14159
    g7: ArcOfCircle CenterX=-28.2 CenterY=-4.3 CenterZ=0 NormalX=0 NormalY=0 NormalZ=1 AngleXU=0 Radius=1.5 StartAngle=2e-16 EndAngle=3.14159
    g8: ArcOfCircle CenterX=-10 CenterY=-33.9 CenterZ=0 NormalX=0 NormalY=0 NormalZ=1 AngleXU=0 Radius=1.5 StartAngle=3.14159 EndAngle=6.28319
    g9: ArcOfCircle CenterX=-16.1 CenterY=-36.4 CenterZ=0 NormalX=0 NormalY=0 NormalZ=1 AngleXU=0 Radius=1.5 StartAngle=3.14159 EndAngle=6.28319
    g10: ArcOfCircle CenterX=-22.1 CenterY=-36.4 CenterZ=0 NormalX=0 NormalY=0 NormalZ=1 AngleXU=0 Radius=1.5 StartAngle=3.14159 EndAngle=6.28319
    g11: ArcOfCircle CenterX=-28.2 CenterY=-33.9 CenterZ=0 NormalX=0 NormalY=0 NormalZ=1 AngleXU=0 Radius=1.5 StartAngle=3.14159 EndAngle=6.28319
    g12: LineSegment StartX=-35.7 StartY=-10.5 StartZ=0 EndX=-35.7 EndY=-27.7 EndZ=0
    g13: LineSegment StartX=-32.7 StartY=-10.5 StartZ=0 EndX=-32.7 EndY=-27.7 EndZ=0
    g14: LineSegment StartX=-29.7 StartY=-33.9 StartZ=0 EndX=-29.7 EndY=-4.3 EndZ=0
    g15: LineSegment StartX=-26.7 StartY=-33.9 StartZ=0 EndX=-26.7 EndY=-4.3 EndZ=0
    g16: LineSegment StartX=-2.5 StartY=-10.5 StartZ=0 EndX=-2.5 EndY=-27.7 EndZ=0
    g17: LineSegment StartX=-8.5 StartY=-4.3 StartZ=0 EndX=-8.5 EndY=-33.9 EndZ=0
    g18: LineSegment StartX=-5.5 StartY=-10.5 StartZ=0 EndX=-5.5 EndY=-27.7 EndZ=0
    g19: LineSegment StartX=-11.5 StartY=-4.3 StartZ=0 EndX=-11.5 EndY=-33.9 EndZ=0
    g20: LineSegment StartX=-14.6 StartY=-1.8 StartZ=0 EndX=-14.6 EndY=-36.4 EndZ=0
    g21: LineSegment StartX=-17.6 StartY=-1.8 StartZ=0 EndX=-17.6 EndY=-36.4 EndZ=0
    g22: LineSegment StartX=-20.6 StartY=-36.4 StartZ=0 EndX=-20.6 EndY=-1.8 EndZ=0
    g23: LineSegment StartX=-23.6 StartY=-1.8 StartZ=0 EndX=-23.6 EndY=-36.4 EndZ=0
  constraints (48):
    c: Block(g0)
    c: Block(g1)
    c: Block(g2)
    c: Block(g3)
    c: Block(g4)
    c: Block(g5)
    c: Block(g6)
    c: Block(g7)
    c: Block(g8)
    c: Block(g9)
    c: Block(g10)
    c: Block(g11)
    c: Coincident(g12,g1)
    c: Coincident(g12,g2)
    c: Vertical(g12)
    c: Coincident(g13,g1)
    c: Coincident(g13,g2)
    c: Vertical(g13)
    c: Coincident(g14,g11)
    c: Coincident(g14,g7)
    c: Vertical(g14)
    c: Coincident(g15,g11)
    c: Coincident(g15,g7)
    c: Vertical(g15)
    c: Coincident(g16,g0)
    c: Coincident(g16,g3)
    c: Vertical(g16)
    c: Coincident(g17,g4)
    c: Coincident(g17,g8)
    c: Vertical(g17)
    c: Coincident(g18,g0)
    c: Coincident(g18,g3)
    c: Vertical(g18)
    c: Coincident(g19,g4)
    c: Coincident(g19,g8)
    c: Vertical(g19)
    c: Coincident(g20,g5)
    c: Coincident(g20,g9)
    c: Vertical(g20)
    c: Coincident(g21,g5)
    c: Coincident(g21,g9)
    c: Vertical(g21)
    c: Coincident(g22,g10)
    c: Coincident(g22,g6)
    c: Vertical(g22)
    c: Coincident(g23,g6)
    c: Coincident(g23,g10)
    c: Vertical(g23)
FEATURE [Part::Extrusion] Extrude039  label="removeToCreateFanGrillHoles002"
  Base = -> Sketch048
  Dir = (0,-1,6e-16)
  DirMode = 2
  FaceMakerClass = Part::FaceMakerBullseye
  LengthFwd = 10
  LengthRev = 0
  Placement = pos=(65.4,44,54.82) rot=(0,0,1;0rad)
  Solid = true
  Symmetric = false
FEATURE [Part::Cut] Cut027  label="fanScrewHousing004"
  Base = -> Cut026
  Tool = -> Extrude038
FEATURE [Part::Cut] Cut028  label="top014"
  Base = -> Fillet026
  Tool = -> Extrude039
FEATURE [Part::Feature] Face095 .. Face098  x4 (patterned run collapsed; names and placements below)
  shape: bbox 3.5 x 17.8 x 2e-07 mm, 1 faces, 0 solids (baked)
FEATURE [Part::Revolution] Revolve103  label="removeToCreateScrewAndThreadedInsertHole030"
  Angle = 360
  Axis = (0,1,0)
  Base = (0,0,0)
  FaceMakerClass = Part::FaceMakerBullseye
  Placement = pos=(62.3,30.3,19.7) rot=(0,0,1;0rad)
  Solid = false
  Source = -> Face095
  Symmetric = false
FEATURE [Part::Revolution] Revolve104  label="removeToCreateScrewAndThreadedInsertHole031"
  Angle = 360
  Axis = (0,1,0)
  Base = (0,0,0)
  FaceMakerClass = Part::FaceMakerBullseye
  Placement = pos=(62.3,30.3,51.7) rot=(0,0,1;0rad)
  Solid = false
  Source = -> Face096
  Symmetric = false
FEATURE [Part::Revolution] Revolve105  label="removeToCreateScrewAndThreadedInsertHole032"
  Angle = 360
  Axis = (0,1,0)
  Base = (0,0,0)
  FaceMakerClass = Part::FaceMakerBullseye
  Placement = pos=(30.3,30.3,19.7) rot=(0,0,1;0rad)
  Solid = false
  Source = -> Face097
  Symmetric = false
FEATURE [Part::Revolution] Revolve106  label="removeToCreateScrewAndThreadedInsertHole033"
  Angle = 360
  Axis = (0,1,0)
  Base = (0,0,0)
  FaceMakerClass = Part::FaceMakerBullseye
  Placement = pos=(30.3,30.3,51.7) rot=(0,0,1;0rad)
  Solid = false
  Source = -> Face098
  Symmetric = false
FEATURE [Part::MultiFuse] Fusion069  label="createThreadedInsertHolesForFan003"
  Shapes = -> [Revolve103,Revolve104,Revolve105,Revolve106]
FEATURE [Part::Cut] Cut029  label="top015"
  Base = -> Cut028
  Tool = -> Fusion054
FEATURE [Part::Cut] Cut030  label="fanScrewHousing005"
  Base = -> Cut027
  Tool = -> Fusion069
FEATURE [Part::Cylinder] Cylinder026  label="removeToCreteHoleForPlugHousing010"
  Angle = 360
  AttacherType = Attacher::AttachEngine3D
  Height = 20
  Placement = pos=(-2,19,36) rot=(0,1,0;1.5708rad)
  Radius = 14.3
FEATURE [Part::Box] Box018  label="removeToCreteHoleForPlugHousing011"
  AttacherType = Attacher::AttachEngine3D
  Height = 28.6
  Length = 10
  Placement = pos=(-2,0,21.7) rot=(0,0,1;0rad)
  Width = 19
FEATURE [Part::Box] Box019  label="wireHolderBottomCaseBit"
  AttacherType = Attacher::AttachEngine3D
  Height = 28
  Length = 3
  Placement = pos=(0,0,22) rot=(0,0,1;0rad)
  Width = 21
FEATURE [Part::Cylinder] Cylinder027  label="removeToCreteHoleForPlugHousing012"
  Angle = 360
  AttacherType = Attacher::AttachEngine3D
  Height = 20
  Placement = pos=(-2,19,36) rot=(0,1,0;1.5708rad)
  Radius = 14.3
FEATURE [Part::Cut] Cut031  label="wireHolderBottomCaseBit001"
  Base = -> Box019
  Tool = -> Cylinder027
FEATURE [Part::MultiFuse] Fusion070  label="removeToCreteHoleForPlugHousing013"
  Shapes = -> [Box018,Cylinder026]
FEATURE [Part::Cut] Cut032  label="top016"
  Base = -> Cut029
  Tool = -> Fusion070
FEATURE [Part::Cylinder] Cylinder028
  Angle = 360
  AttacherType = Attacher::AttachEngine3D
  Height = 20
  Placement = pos=(0,0,36.15) rot=(0,0,1;0rad)
  Radius = 14.3
FEATURE [Part::Cylinder] Cylinder029
  Angle = 360
  AttacherType = Attacher::AttachEngine3D
  Height = 10
  Placement = pos=(0,0,36.15) rot=(0,0,1;0rad)
  Radius = 4
FEATURE [Part::MultiFuse] Fusion071  label="removeToCreteHoleForPlugHousing014"
  Placement = pos=(70,19,36) rot=(0,1,0;1.5708rad)
  Shapes = -> [Cylinder028,Cylinder029]
FEATURE [Sketcher::SketchObject] Sketch049  label="topSketch011"
  FullyConstrained = true
  sketch-geometry (4):
    g0: ArcOfCircle CenterX=105 CenterY=19 CenterZ=0 NormalX=0 NormalY=0 NormalZ=1 AngleXU=0 Radius=20.6155 StartAngle=5.54125 EndAngle=6.28319
    g1: ArcOfCircle CenterX=105 CenterY=19 CenterZ=0 NormalX=0 NormalY=0 NormalZ=1 AngleXU=0 Radius=13 StartAngle=5.54125 EndAngle=6.28319
    g2: LineSegment StartX=118 StartY=19 StartZ=0 EndX=125.616 EndY=19 EndZ=0
    g3: LineSegment StartX=114.583 StartY=10.2157 StartZ=0 EndX=120.197 EndY=5.06982 EndZ=0
  constraints (7):
    c: Block(g0)
    c: Block(g1)
    c: Coincident(g2,g1)
    c: Coincident(g2,g0)
    c: Horizontal(g2)
    c: Coincident(g3,g1)
    c: Coincident(g3,g0)
FEATURE [Part::Box] Box020  label="removeToCreteHoleForPlugHousing015"
  AttacherType = Attacher::AttachEngine3D
  Height = 28.6
  Length = 20
  Placement = pos=(106.15,0,21.7) rot=(0,0,1;0rad)
  Width = 19
FEATURE [Part::MultiFuse] Fusion072  label="removeToCreteHoleForPlugHousing016"
  Shapes = -> [Box020,Fusion071]
FEATURE [Part::Cut] Cut033  label="removeToCreteHoleForPlugHousing017"
  Base = -> Cut032
  Tool = -> Fusion072
FEATURE [Part::Cylinder] Cylinder030
  Angle = 360
  AttacherType = Attacher::AttachEngine3D
  Height = 20
  Placement = pos=(0,0,36.15) rot=(0,0,1;0rad)
  Radius = 14.3
FEATURE [Part::Cylinder] Cylinder031
  Angle = 360
  AttacherType = Attacher::AttachEngine3D
  Height = 10
  Placement = pos=(0,0,36.15) rot=(0,0,1;0rad)
  Radius = 4
FEATURE [Part::Box] Box021  label="removeToCreteHoleForPlugHousing019"
  AttacherType = Attacher::AttachEngine3D
  Height = 28.6
  Length = 20
  Placement = pos=(106.15,0,21.7) rot=(0,0,1;0rad)
  Width = 19
FEATURE [Part::MultiFuse] Fusion074  label="removeToCreteHoleForPlugHousing020"
  Placement = pos=(70,19,36) rot=(0,1,0;1.5708rad)
  Shapes = -> [Cylinder030,Cylinder031]
FEATURE [Part::MultiFuse] Fusion073  label="removeToCreteHoleForPlugHousing018"
  Placement = pos=(0,0,28.3) rot=(0,0,1;0rad)
  Shapes = -> [Box021,Fusion074]
FEATURE [Part::Cylinder] Cylinder032
  Angle = 360
  AttacherType = Attacher::AttachEngine3D
  Height = 20
  Placement = pos=(0,0,36.15) rot=(0,0,1;0rad)
  Radius = 14.3
FEATURE [Part::Cylinder] Cylinder033
  Angle = 360
  AttacherType = Attacher::AttachEngine3D
  Height = 10
  Placement = pos=(0,0,36.15) rot=(0,0,1;0rad)
  Radius = 4
FEATURE [Part::Box] Box022  label="removeToCreteHoleForPlugHousing021"
  AttacherType = Attacher::AttachEngine3D
  Height = 28.6
  Length = 20
  Placement = pos=(106.15,0,21.7) rot=(0,0,1;0rad)
  Width = 19
FEATURE [Part::MultiFuse] Fusion076  label="removeToCreteHoleForPlugHousing023"
  Placement = pos=(70,19,36) rot=(0,1,0;1.5708rad)
  Shapes = -> [Cylinder032,Cylinder033]
FEATURE [Part::MultiFuse] Fusion075  label="removeToCreteHoleForPlugHousing022"
  Placement = pos=(0,0,-28.3) rot=(0,0,1;0rad)
  Shapes = -> [Box022,Fusion076]
FEATURE [Part::MultiFuse] Fusion077  label="removeToCreatePlugHousingBottomBit"
  Shapes = -> [Fusion075,Fusion073]
FEATURE [Part::Cylinder] Cylinder034
  Angle = 360
  AttacherType = Attacher::AttachEngine3D
  Height = 20
  Placement = pos=(0,0,36.15) rot=(0,0,1;0rad)
  Radius = 14
FEATURE [Part::Cylinder] Cylinder035
  Angle = 360
  AttacherType = Attacher::AttachEngine3D
  Height = 10
  Placement = pos=(0,0,36.15) rot=(0,0,1;0rad)
  Radius = 4
FEATURE [Part::MultiFuse] Fusion078  label="removeToCreteHoleForPlugHousing024"
  Placement = pos=(70,19,36) rot=(0,1,0;1.5708rad)
  Shapes = -> [Cylinder034,Cylinder035]
FEATURE [Part::MultiFuse] Fusion079  label="removeToCreatePlugHousingBottomBit001"
  Shapes = -> [Fusion078,Fusion077]
FEATURE [Part::Extrusion] Extrude040  label="bottomPlugHousingBit"
  Base = -> Sketch049
  Dir = (0,0,1)
  DirMode = 2
  FaceMakerClass = Part::FaceMakerBullseye
  LengthFwd = 72
  LengthRev = 0
  Solid = true
  Symmetric = false
FEATURE [Part::Cut] Cut034  label="bottomPlugHousingBit001"
  Base = -> Extrude040
  Placement = pos=(-0.09,0,0) rot=(0,0,1;0rad)
  Tool = -> Fusion079
FEATURE [Part::Box] Box023  label="Cube014"
  AttacherType = Attacher::AttachEngine3D
  Height = 16
  Length = 8
  Placement = pos=(12.7,31.52,28) rot=(0,0,1;0rad)
  Width = 4
FEATURE [Part::Cylinder] Cylinder036
  Angle = 360
  AttacherType = Attacher::AttachEngine3D
  Height = 10
  Placement = pos=(0,0,36.15) rot=(0,0,1;0rad)
  Radius = 4
FEATURE [Part::Cylinder] Cylinder037
  Angle = 360
  AttacherType = Attacher::AttachEngine3D
  Height = 20
  Placement = pos=(0,0,36.15) rot=(0,0,1;0rad)
  Radius = 8.2
FEATURE [Part::MultiFuse] Fusion080  label="removeToCreteHoleForPlugHousing025"
  Placement = pos=(-42,19,36) rot=(0,1,0;1.5708rad)
  Shapes = -> [Cylinder037,Cylinder036]
FEATURE [Sketcher::SketchObject] Sketch050  label="topSketch012"
  FullyConstrained = true
  sketch-geometry (4):
    g0: LineSegment StartX=16.8446 StartY=31.512 StartZ=0 EndX=16.3251 EndY=34.4666 EndZ=0
    g1: ArcOfCircle CenterX=19 CenterY=19.2524 CenterZ=0 NormalX=0 NormalY=0 NormalZ=1 AngleXU=0 Radius=15.4476 StartAngle=1.74483 EndAngle=2.72717
    g2: ArcOfCircle CenterX=19 CenterY=19.2524 CenterZ=0 NormalX=0 NormalY=0 NormalZ=1 AngleXU=0 Radius=12.4476 StartAngle=1.74483 EndAngle=2.73189
    g3: LineSegment StartX=4.86004 StartY=25.4725 StartZ=0 EndX=7.58253 EndY=24.2107 EndZ=0
  constraints (7):
    c: Block(g0)
    c: Coincident(g1,g0)
    c: Coincident(g2,g0)
    c: Coincident(g3,g1)
    c: Coincident(g3,g2)
    c: Block(g1)
    c: Block(g2)
FEATURE [Part::Extrusion] Extrude041
  Base = -> Sketch050
  Dir = (0,0,1)
  DirMode = 2
  FaceMakerClass = Part::FaceMakerBullseye
  LengthFwd = 10.6
  LengthRev = 0
  Placement = pos=(0,0,31) rot=(0,0,1;0rad)
  Solid = true
  Symmetric = false
FEATURE [Part::Cut] Cut035
  Base = -> Extrude041
  Placement = pos=(0,0,-0.3) rot=(0,0,1;0rad)
  Tool = -> Fusion080
FEATURE [Part::Cut] Cut036
  Base = -> Box023
  Tool = -> Cut035
FEATURE [Part::Fillet] Fillet027
  Base = -> Cut036
  Edges = 1 edges r=0.7: [Edge13]
FEATURE [Part::Fillet] Fillet028
  Base = -> Fillet027
  Edges = 1 edges r=0.7: [Edge13]
FEATURE [Part::Fillet] Fillet029
  Base = -> Fillet028
  Edges = 1 edges r=0.7: [Edge16]
FEATURE [Part::Fillet] Fillet030
  Base = -> Fillet029
  Edges = 1 edges r=0.7: [Edge11]
FEATURE [Part::Fillet] Fillet031
  Base = -> Fillet030
  Edges = 1 edges r=0.7: [Edge10]
FEATURE [Part::Fillet] Fillet032
  Base = -> Fillet031
  Edges = 1 edges r=1.2: [Edge5]
FEATURE [Part::Fillet] Fillet033
  Base = -> Fillet032
  Edges = 1 edges r=1.2: [Edge12]
FEATURE [Part::Fillet] Fillet034  label="wireHousingRetainer"
  Base = -> Fillet033
  Edges = 1 edges r=2: [Edge1]
  Placement = pos=(0.3,0,0) rot=(0,0,1;0rad)
FEATURE [Part::Feature] Face099
  shape: bbox 3.5 x 17.8 x 2e-07 mm, 1 faces, 0 solids (baked)
FEATURE [Part::Revolution] Revolve107  label="removeToCreateScrewAndThreadedInsertHole034"
  Angle = 360
  Axis = (0,1,0)
  Base = (0,0,0)
  FaceMakerClass = Part::FaceMakerBullseye
  Placement = pos=(12.5,0,10) rot=(0,0,1;0rad)
  Solid = false
  Source = -> Face099
  Symmetric = false
FEATURE [Part::Feature] Face100
  shape: bbox 3.5 x 17.8 x 2e-07 mm, 1 faces, 0 solids (baked)
FEATURE [Part::Revolution] Revolve108  label="removeToCreateScrewAndThreadedInsertHole035"
  Angle = 360
  Axis = (0,1,0)
  Base = (0,0,0)
  FaceMakerClass = Part::FaceMakerBullseye
  Placement = pos=(12.5,0,62) rot=(0,0,1;0rad)
  Solid = false
  Source = -> Face100
  Symmetric = false
FEATURE [Part::Feature] Face101
  shape: bbox 3.5 x 17.8 x 2e-07 mm, 1 faces, 0 solids (baked)
FEATURE [Part::Revolution] Revolve109  label="removeToCreateScrewAndThreadedInsertHole036"
  Angle = 360
  Axis = (0,1,0)
  Base = (0,0,0)
  FaceMakerClass = Part::FaceMakerBullseye
  Placement = pos=(89.5,0,68.5) rot=(0,0,1;0rad)
  Solid = false
  Source = -> Face101
  Symmetric = false
FEATURE [Part::Feature] Face102
  shape: bbox 3.5 x 17.8 x 2e-07 mm, 1 faces, 0 solids (baked)
FEATURE [Part::Revolution] Revolve110  label="removeToCreateScrewAndThreadedInsertHole037"
  Angle = 360
  Axis = (0,1,0)
  Base = (0,0,0)
  FaceMakerClass = Part::FaceMakerBullseye
  Placement = pos=(89.5,0,3.5) rot=(0,0,1;0rad)
  Solid = false
  Source = -> Face102
  Symmetric = false
FEATURE [Part::Feature] Face103
  shape: bbox 3.5 x 17.8 x 2e-07 mm, 1 faces, 0 solids (baked)
FEATURE [Part::Revolution] Revolve111  label="removeToCreateScrewAndThreadedInsertHole038"
  Angle = 360
  Axis = (0,1,0)
  Base = (0,0,0)
  FaceMakerClass = Part::FaceMakerBullseye
  Placement = pos=(109.5,4.7,3.5) rot=(0,0,1;0rad)
  Solid = false
  Source = -> Face103
  Symmetric = false
FEATURE [Part::Feature] Face104
  shape: bbox 3.5 x 17.8 x 2e-07 mm, 1 faces, 0 solids (baked)
FEATURE [Part::Revolution] Revolve112  label="removeToCreateScrewAndThreadedInsertHole039"
  Angle = 360
  Axis = (0,1,0)
  Base = (0,0,0)
  FaceMakerClass = Part::FaceMakerBullseye
  Placement = pos=(109.5,4.7,68.5) rot=(0,0,1;0rad)
  Solid = false
  Source = -> Face104
  Symmetric = false
FEATURE [Part::MultiFuse] Fusion081  label="removeToCreateScrewAndThreadedInsertHole040"
  Shapes = -> [Revolve107,Revolve108,Revolve109,Revolve110,Revolve111,Revolve112]
FEATURE [Part::MultiFuse] Fusion082  label="casePillars002"
  Shapes = -> [Revolve094,Revolve092,Revolve090,Revolve089,Revolve091,Revolve093]
FEATURE [Part::Cut] Cut037  label="casePillars003"
  Base = -> Fusion082
  Tool = -> Fusion081
FEATURE [Sketcher::SketchObject] Sketch051
  FullyConstrained = true
  Placement = pos=(117,19,0) rot=(0.57735,0.57735,0.57735;2.0944rad)
  sketch-geometry (48):
    g0: LineSegment StartX=-49.19 StartY=69.25 StartZ=0 EndX=-49.19 EndY=66.25 EndZ=0
    g1: LineSegment StartX=-49.19 StartY=63.5 StartZ=0 EndX=-49.19 EndY=60.5 EndZ=0
    g2: LineSegment StartX=-49.19 StartY=57.75 StartZ=0 EndX=-49.19 EndY=54.75 EndZ=0
    g3: LineSegment StartX=-49.19 StartY=52 StartZ=0 EndX=-49.19 EndY=49 EndZ=0
    g4: LineSegment StartX=-49.19 StartY=46.25 StartZ=0 EndX=-49.19 EndY=43.25 EndZ=0
    g5: LineSegment StartX=-49.19 StartY=40.5 StartZ=0 EndX=-49.19 EndY=37.5 EndZ=0
    g6: LineSegment StartX=-49.19 StartY=34.5 StartZ=0 EndX=-49.19 EndY=31.5 EndZ=0
    g7: LineSegment StartX=-49.19 StartY=28.75 StartZ=0 EndX=-49.19 EndY=25.75 EndZ=0
    g8: LineSegment StartX=-49.19 StartY=23 StartZ=0 EndX=-49.19 EndY=20 EndZ=0
    g9: LineSegment StartX=-49.19 StartY=17.25 StartZ=0 EndX=-49.19 EndY=14.25 EndZ=0
    g10: LineSegment StartX=-49.19 StartY=11.5 StartZ=0 EndX=-49.19 EndY=8.5 EndZ=0
    g11: LineSegment StartX=-49.19 StartY=5.75 StartZ=0 EndX=-49.19 EndY=2.75 EndZ=0
    g12: ArcOfCircle CenterX=-1.5 CenterY=67.75 CenterZ=0 NormalX=0 NormalY=0 NormalZ=1 AngleXU=0 Radius=1.5 StartAngle=4.71239 EndAngle=7.85398
    g13: ArcOfCircle CenterX=-1.5 CenterY=62 CenterZ=0 NormalX=0 NormalY=0 NormalZ=1 AngleXU=0 Radius=1.5 StartAngle=4.71239 EndAngle=7.85398
    g14: ArcOfCircle CenterX=-1.5 CenterY=56.25 CenterZ=0 NormalX=0 NormalY=0 NormalZ=1 AngleXU=0 Radius=1.5 StartAngle=4.71239 EndAngle=7.85398
    g15: ArcOfCircle CenterX=-11.49 CenterY=50.5 CenterZ=0 NormalX=0 NormalY=0 NormalZ=1 AngleXU=0 Radius=1.5 StartAngle=4.71239 EndAngle=7.85398
    g16: ArcOfCircle CenterX=-16.28 CenterY=44.75 CenterZ=0 NormalX=0 NormalY=0 NormalZ=1 AngleXU=0 Radius=1.5 StartAngle=4.71239 EndAngle=7.85398
    g17: ArcOfCircle CenterX=-18.2337 CenterY=39 CenterZ=0 NormalX=0 NormalY=0 NormalZ=1 AngleXU=0 Radius=1.5 StartAngle=4.71485 EndAngle=7.85398
    g18: ArcOfCircle CenterX=-16.2837 CenterY=27.25 CenterZ=0 NormalX=0 NormalY=0 NormalZ=1 AngleXU=0 Radius=1.5 StartAngle=4.71485 EndAngle=7.85398
    g19: ArcOfCircle CenterX=-18.2337 CenterY=33 CenterZ=0 NormalX=0 NormalY=0 NormalZ=1 AngleXU=0 Radius=1.5 StartAngle=4.71485 EndAngle=7.85398
    g20: ArcOfCircle CenterX=-11.49 CenterY=21.5 CenterZ=0 NormalX=0 NormalY=0 NormalZ=1 AngleXU=0 Radius=1.5 StartAngle=4.71239 EndAngle=7.85398
    g21: ArcOfCircle CenterX=-1.5 CenterY=4.25 CenterZ=0 NormalX=0 NormalY=0 NormalZ=1 AngleXU=0 Radius=1.5 StartAngle=4.71239 EndAngle=7.85398
    g22: ArcOfCircle CenterX=-1.5 CenterY=10 CenterZ=0 NormalX=0 NormalY=0 NormalZ=1 AngleXU=0 Radius=1.5 StartAngle=4.71239 EndAngle=7.85398
    g23: ArcOfCircle CenterX=-1.5 CenterY=15.75 CenterZ=0 NormalX=0 NormalY=0 NormalZ=1 AngleXU=0 Radius=1.5 StartAngle=4.71239 EndAngle=7.85398
    g24: LineSegment StartX=-49.19 StartY=69.25 StartZ=0 EndX=-1.5 EndY=69.25 EndZ=0
    g25: LineSegment StartX=-49.19 StartY=66.25 StartZ=0 EndX=-1.5 EndY=66.25 EndZ=0
    g26: LineSegment StartX=-49.19 StartY=63.5 StartZ=0 EndX=-1.5 EndY=63.5 EndZ=0
    g27: LineSegment StartX=-49.19 StartY=60.5 StartZ=0 EndX=-1.5 EndY=60.5 EndZ=0
    g28: LineSegment StartX=-49.19 StartY=57.75 StartZ=0 EndX=-1.5 EndY=57.75 EndZ=0
    g29: LineSegment StartX=-49.19 StartY=54.75 StartZ=0 EndX=-1.5 EndY=54.75 EndZ=0
    g30: LineSegment StartX=-49.19 StartY=52 StartZ=0 EndX=-11.49 EndY=52 EndZ=0
    g31: LineSegment StartX=-49.19 StartY=49 StartZ=0 EndX=-11.49 EndY=49 EndZ=0
    g32: LineSegment StartX=-49.19 StartY=46.25 StartZ=0 EndX=-16.28 EndY=46.25 EndZ=0
    g33: LineSegment StartX=-49.19 StartY=43.25 StartZ=0 EndX=-16.28 EndY=43.25 EndZ=0
    g34: LineSegment StartX=-49.19 StartY=40.5 StartZ=0 EndX=-18.2337 EndY=40.5 EndZ=0
    g35: LineSegment StartX=-49.19 StartY=37.5 StartZ=0 EndX=-18.23 EndY=37.5 EndZ=0
    g36: LineSegment StartX=-49.19 StartY=34.5 StartZ=0 EndX=-18.2337 EndY=34.5 EndZ=0
    g37: LineSegment StartX=-49.19 StartY=31.5 StartZ=0 EndX=-18.23 EndY=31.5 EndZ=0
    g38: LineSegment StartX=-49.19 StartY=28.75 StartZ=0 EndX=-16.2837 EndY=28.75 EndZ=0
    g39: LineSegment StartX=-49.19 StartY=25.75 StartZ=0 EndX=-16.28 EndY=25.75 EndZ=0
    g40: LineSegment StartX=-49.19 StartY=23 StartZ=0 EndX=-11.49 EndY=23 EndZ=0
    g41: LineSegment StartX=-49.19 StartY=20 StartZ=0 EndX=-11.49 EndY=20 EndZ=0
    g42: LineSegment StartX=-49.19 StartY=17.25 StartZ=0 EndX=-1.5 EndY=17.25 EndZ=0
    g43: LineSegment StartX=-49.19 StartY=14.25 StartZ=0 EndX=-1.5 EndY=14.25 EndZ=0
    g44: LineSegment StartX=-49.19 StartY=11.5 StartZ=0 EndX=-1.5 EndY=11.5 EndZ=0
    g45: LineSegment StartX=-49.19 StartY=8.5 StartZ=0 EndX=-1.5 EndY=8.5 EndZ=0
    g46: LineSegment StartX=-49.19 StartY=5.75 StartZ=0 EndX=-1.5 EndY=5.75 EndZ=0
    g47: LineSegment StartX=-49.19 StartY=2.75 StartZ=0 EndX=-1.5 EndY=2.75 EndZ=0
  constraints (120):
    c: Vertical(g0)
    c: Distance(g0) = 3
    c: Block(g0)
    c: Vertical(g1)
    c: Distance(g1) = 3
    c: Vertical(g2)
    c: Equal(g0,g2) = 3
    c: Block(g2)
    c: Vertical(g3)
    c: Equal(g1,g3) = 3
    c: Vertical(g4)
    c: Equal(g0,g4) = 3
    c: Block(g4)
    c: Vertical(g5)
    c: Equal(g1,g5) = 3
    c: Vertical(g6)
    c: Equal(g0,g6) = 3
    c: Block(g6)
    c: Vertical(g7)
    c: Equal(g1,g7) = 3
    c: Vertical(g8)
    c: Equal(g0,g8) = 3
    c: Block(g8)
    c: Vertical(g9)
    c: Equal(g1,g9) = 3
    c: Vertical(g10)
    c: Equal(g0,g10) = 3
    c: Block(g10)
    c: Vertical(g11)
    c: Equal(g1,g11) = 3
    c: Block(g12)
    c: Block(g13)
    c: Block(g14)
    c: Block(g15)
    c: Block(g16)
    c: Block(g17)
    c: Block(g18)
    c: Block(g19)
    c: Block(g20)
    c: Block(g21)
    c: Block(g22)
    c: Block(g23)
    c: Block(g11)
    c: Block(g9)
    c: Block(g7)
    c: Block(g5)
    c: Block(g3)
    c: Block(g1)
    c: Coincident(g24,g0)
    c: Coincident(g24,g12)
    c: Horizontal(g24)
    c: Coincident(g25,g0)
    c: Coincident(g25,g12)
    c: Horizontal(g25)
    c: Coincident(g26,g1)
    c: Coincident(g26,g13)
    c: Horizontal(g26)
    c: Coincident(g27,g1)
    c: Coincident(g27,g13)
    c: Horizontal(g27)
    c: Coincident(g28,g2)
    c: Coincident(g28,g14)
    c: Horizontal(g28)
    c: Coincident(g29,g2)
    c: Coincident(g29,g14)
    c: Horizontal(g29)
    c: Coincident(g30,g3)
    c: Coincident(g30,g15)
    c: Horizontal(g30)
    c: Coincident(g31,g3)
    c: Coincident(g31,g15)
    c: Horizontal(g31)
    c: Coincident(g32,g4)
    c: Coincident(g32,g16)
    c: Horizontal(g32)
    c: Coincident(g33,g4)
    c: Coincident(g33,g16)
    c: Horizontal(g33)
    c: Coincident(g34,g5)
    c: Coincident(g34,g17)
    c: Horizontal(g34)
    c: Coincident(g35,g5)
    c: Coincident(g35,g17)
    c: Horizontal(g35)
    c: Coincident(g36,g6)
    c: Coincident(g36,g19)
    c: Horizontal(g36)
    c: Coincident(g37,g6)
    c: Coincident(g37,g19)
    c: Horizontal(g37)
    c: Coincident(g38,g7)
    c: Coincident(g38,g18)
    c: Horizontal(g38)
    c: Coincident(g39,g7)
    c: Coincident(g39,g18)
    c: Horizontal(g39)
    c: Coincident(g40,g8)
    c: Coincident(g40,g20)
    c: Horizontal(g40)
    c: Coincident(g41,g8)
    c: Coincident(g41,g20)
    c: Horizontal(g41)
    c: Coincident(g42,g9)
    c: Coincident(g42,g23)
    c: Horizontal(g42)
    c: Coincident(g43,g9)
    c: Coincident(g43,g23)
    c: Horizontal(g43)
    c: Coincident(g44,g10)
    c: Coincident(g44,g22)
    c: Horizontal(g44)
    c: Coincident(g45,g10)
    c: Coincident(g45,g22)
    c: Horizontal(g45)
    c: Coincident(g46,g11)
    c: Coincident(g46,g21)
    c: Horizontal(g46)
    c: Coincident(g47,g11)
    c: Coincident(g47,g21)
    c: Horizontal(g47)
FEATURE [Part::Extrusion] Extrude042
  Base = -> Sketch051
  Dir = (1,-2e-16,2e-16)
  DirMode = 2
  FaceMakerClass = Part::FaceMakerBullseye
  LengthFwd = 19
  LengthRev = 0
  Placement = pos=(-19,0,0) rot=(0,0,1;0rad)
  Solid = true
  Symmetric = false
FEATURE [Part::Fillet] Fillet035  label="removeToCreateVentalationHoles"
  Base = -> Extrude042
  Edges = <same value as first occurrence — deduplicated (x6 in doc)>
  Placement = pos=(7,0,0) rot=(0,0,1;0rad)
FEATURE [Part::Cut] Cut038  label="top017"
  Base = -> Cut033
  Tool = -> Fillet035
FEATURE [Sketcher::SketchObject] Sketch052  label="bottomSketch001"
  FullyConstrained = true
  sketch-geometry (45):
    g0: LineSegment StartX=6.29999 StartY=8 StartZ=0 EndX=3.29999 EndY=8 EndZ=0
    g1: LineSegment StartX=3.29999 StartY=8 StartZ=0 EndX=3.29999 EndY=-6.03275e-07 EndZ=0
    g2: ArcOfCircle CenterX=8.29999 CenterY=5 CenterZ=0 NormalX=0 NormalY=0 NormalZ=1 AngleXU=0 Radius=2 StartAngle=3.14159 EndAngle=4.71239
    g3: LineSegment StartX=6.29999 StartY=8 StartZ=0 EndX=6.29999 EndY=5 EndZ=0
    g4: ArcOfCircle CenterX=105 CenterY=19 CenterZ=0 NormalX=0 NormalY=0 NormalZ=1 AngleXU=0 Radius=12.7 StartAngle=4.71239 EndAngle=5.94289
    g5-g11: Circle x7 (B-spline internal-alignment scaffolding for g12; pole/knot coordinates omitted)
    g12: BSplineCurve PolesCount=7 KnotsCount=5 Degree=3 IsPeriodic=0
    g13-g17: GeomPoint x5 (B-spline internal-alignment scaffolding for g12; pole/knot coordinates omitted)
    g18: ArcOfCircle CenterX=105 CenterY=19 CenterZ=0 NormalX=0 NormalY=0 NormalZ=1 AngleXU=0 Radius=15.7 StartAngle=5.81226 EndAngle=6.28319
    g19: BSplineCurve PolesCount=5 KnotsCount=3 Degree=3 IsPeriodic=0
    g20: LineSegment StartX=8.29999 StartY=3 StartZ=0 EndX=101.7 EndY=3 EndZ=0
    g21: LineSegment StartX=3.29999 StartY=-6.03275e-07 StartZ=0 EndX=105 EndY=-6.03275e-07 EndZ=0
    g22: LineSegment StartX=120.974 StartY=8.71251 StartZ=0 EndX=122.332 EndY=7.83778 EndZ=0
    g23: LineSegment StartX=105 StartY=-6.03274e-07 StartZ=0 EndX=113 EndY=-6.03274e-07 EndZ=0
    g24: ArcOfCircle CenterX=105 CenterY=19 CenterZ=0 NormalX=0 NormalY=0 NormalZ=1 AngleXU=0 Radius=20.6155 StartAngle=5.11091 EndAngle=5.71103
    g25: ArcOfCircle CenterX=117.7 CenterY=19 CenterZ=0 NormalX=0 NormalY=0 NormalZ=1 AngleXU=0 Radius=3 StartAngle=1.2e-15 EndAngle=2.10468
    g26: Circle CenterX=116.345 CenterY=16.3232 CenterZ=0 NormalX=0 NormalY=0 NormalZ=1 AngleXU=0 Radius=1
    g27: Circle CenterX=117.24 CenterY=15.7584 CenterZ=0 NormalX=0 NormalY=0 NormalZ=1 AngleXU=0 Radius=1
    g28: Circle CenterX=116.972 CenterY=14.7612 CenterZ=0 NormalX=0 NormalY=0 NormalZ=1 AngleXU=0 Radius=1
    g29: BSplineCurve PolesCount=3 KnotsCount=2 Degree=2 IsPeriodic=0
    g30: GeomPoint X=116.345 Y=16.3232 Z=0
    g31: GeomPoint X=116.972 Y=14.7612 Z=0
    g32: Circle CenterX=115.828 CenterY=17.157 CenterZ=0 NormalX=0 NormalY=0 NormalZ=1 AngleXU=0 Radius=1
    g33: Circle CenterX=115.841 CenterY=16.639 CenterZ=0 NormalX=0 NormalY=0 NormalZ=1 AngleXU=0 Radius=1
    g34: Circle CenterX=116.345 CenterY=16.3232 CenterZ=0 NormalX=0 NormalY=0 NormalZ=1 AngleXU=0 Radius=1
    g35: BSplineCurve PolesCount=3 KnotsCount=2 Degree=2 IsPeriodic=0
    g36: GeomPoint X=115.828 Y=17.157 Z=0
    g37: GeomPoint X=116.345 Y=16.3232 Z=0
    g38: LineSegment StartX=115.828 StartY=17.157 StartZ=0 EndX=115.828 EndY=20.8307 EndZ=0
    g39: Circle CenterX=115.828 CenterY=20.8307 CenterZ=0 NormalX=0 NormalY=0 NormalZ=1 AngleXU=0 Radius=1
    g40: Circle CenterX=115.831 CenterY=21.3396 CenterZ=0 NormalX=0 NormalY=0 NormalZ=1 AngleXU=0 Radius=1
    g41: Circle CenterX=116.173 CenterY=21.5825 CenterZ=0 NormalX=0 NormalY=0 NormalZ=1 AngleXU=0 Radius=1
    g42: BSplineCurve PolesCount=3 KnotsCount=2 Degree=2 IsPeriodic=0
    g43: GeomPoint X=115.828 Y=20.8307 Z=0
    g44: GeomPoint X=116.173 Y=21.5825 Z=0
  constraints (70):
    c: Horizontal(g0)
    c: Distance(g0) = 3
    c: Coincident(g1,g0)
    c: Vertical(g1)
    c: Block(g2)
    c: Block(g0)
    c: Coincident(g3,g0)
    c: Coincident(g3,g2)
    c: Vertical(g3)
    c: Block(g1)
    c: Block(g4)
    c: Coincident(g19,g4)
    c: Block(g19)
    c: Equal(g5, g6-g11) x6
    c: InternalAlignment(g5-g11 -> g12) x7
    c: InternalAlignment(g13-g17 -> g12) x5
    c: Block(g12)
    c: Coincident(g18,g12)
    c: Block(g18)
    c: Coincident(g20,g2)
    c: Coincident(g20,g19)
    c: Horizontal(g20)
    c: Distance(g20) = 93.4
    c: Coincident(g21,g1)
    c: Horizontal(g21)
    c: Distance(g21) = 101.7
    c: Horizontal(g23)
    c: Distance(g23) = 8
    c: Coincident(g24,g23)
    c: Block(g23)
    c: Coincident(g22,g24)
    c: Block(g24)
    c: Block(g22)
    c: Distance(g22) = 1.61553
    c: Coincident(g25,g18)
    c: Block(g25)
    c: Weight(g26) = 1
    c: Equal(g26,g27)
    c: Equal(g26,g28)
    c: Coincident(g29,g4)
    c: InternalAlignment(g26,g29)
    c: InternalAlignment(g27,g29)
    c: InternalAlignment(g28,g29)
    c: InternalAlignment(g30,g29)
    c: InternalAlignment(g31,g29)
    c: Block(g29)
    c: Weight(g32) = 1
    c: Equal(g32,g33)
    c: Equal(g32,g34)
    c: Coincident(g35,g29)
    c: InternalAlignment(g32,g35)
    c: InternalAlignment(g33,g35)
    c: InternalAlignment(g34,g35)
    c: InternalAlignment(g36,g35)
    c: InternalAlignment(g37,g35)
    c: Block(g35)
    c: Coincident(g38,g35)
    c: Vertical(g38)
    c: Block(g38)
    c: Coincident(g42,g38)
    c: Weight(g39) = 1
    c: Equal(g39,g40)
    c: Equal(g39,g41)
    c: Coincident(g42,g25)
    c: InternalAlignment(g39,g42)
    c: InternalAlignment(g40,g42)
    c: InternalAlignment(g41,g42)
    c: InternalAlignment(g43,g42)
    c: InternalAlignment(g44,g42)
    c: Block(g42)
FEATURE [Part::Extrusion] Extrude043  label="bottom010"
  Base = -> Sketch052
  Dir = (0,0,1)
  DirMode = 2
  FaceMakerClass = Part::FaceMakerBullseye
  LengthFwd = 71.4
  LengthRev = 0
  Placement = pos=(0,0,0.3) rot=(0,0,1;0rad)
  Solid = true
  Symmetric = false
FEATURE [Sketcher::SketchObject] Sketch053  label="topSketch013"
  FullyConstrained = true
  sketch-geometry (22):
    g0: LineSegment StartX=5.21097e-06 StartY=3 StartZ=0 EndX=5.21097e-06 EndY=19 EndZ=0
    g1: ArcOfCircle CenterX=19 CenterY=19 CenterZ=0 NormalX=0 NormalY=0 NormalZ=1 AngleXU=0 Radius=19 StartAngle=1.5708 EndAngle=3.14159
    g2: ArcOfCircle CenterX=19 CenterY=19 CenterZ=0 NormalX=0 NormalY=0 NormalZ=1 AngleXU=0 Radius=16 StartAngle=1.5708 EndAngle=3.14159
    g3: LineSegment StartX=114 StartY=35 StartZ=0 EndX=19 EndY=35 EndZ=0
    g4: LineSegment StartX=5.21097e-06 StartY=3 StartZ=0 EndX=5.21097e-06 EndY=0 EndZ=0
    g5: LineSegment StartX=3 StartY=0 StartZ=0 EndX=5.21097e-06 EndY=0 EndZ=0
    g6: LineSegment StartX=3 StartY=19 StartZ=0 EndX=3 EndY=0 EndZ=0
    g7: LineSegment StartX=19 StartY=38 StartZ=0 EndX=124 EndY=38 EndZ=0
    g8: Circle CenterX=119 CenterY=35 CenterZ=0 NormalX=0 NormalY=0 NormalZ=1 AngleXU=0 Radius=1
    g9: Circle CenterX=121 CenterY=35 CenterZ=0 NormalX=0 NormalY=0 NormalZ=1 AngleXU=0 Radius=1
    g10: Circle CenterX=121 CenterY=33 CenterZ=0 NormalX=0 NormalY=0 NormalZ=1 AngleXU=0 Radius=1
    g11: BSplineCurve PolesCount=3 KnotsCount=2 Degree=2 IsPeriodic=0
    g12: GeomPoint X=119 Y=35 Z=0
    g13: GeomPoint X=121 Y=33 Z=0
    g14: LineSegment StartX=119 StartY=35 StartZ=0 EndX=114 EndY=35 EndZ=0
    g15: ArcOfCircle CenterX=105 CenterY=19 CenterZ=0 NormalX=0 NormalY=0 NormalZ=1 AngleXU=0 Radius=16 StartAngle=5.60905 EndAngle=6.28319
    g16: LineSegment StartX=121 StartY=33 StartZ=0 EndX=121 EndY=19 EndZ=0
    g17: LineSegment StartX=117.5 StartY=9.01251 StartZ=0 EndX=121.163 EndY=9.0125 EndZ=0
    g18: ArcOfCircle CenterX=105 CenterY=19 CenterZ=0 NormalX=0 NormalY=0 NormalZ=1 AngleXU=0 Radius=20.6155 StartAngle=5.7297 EndAngle=6.28319
    g19: LineSegment StartX=121.163 StartY=9.0125 StartZ=0 EndX=122.538 EndY=8.16329 EndZ=0
    g20: LineSegment StartX=124 StartY=38 StartZ=0 EndX=125.616 EndY=38 EndZ=0
    g21: LineSegment StartX=125.616 StartY=19 StartZ=0 EndX=125.616 EndY=38 EndZ=0
  constraints (50):
    c: Vertical(g0)
    c: Block(g0)
    c: Coincident(g1,g0)
    c: Block(g1)
    c: Coincident(g2,g1)
    c: Block(g2)
    c: Coincident(g3,g2)
    c: Horizontal(g3)
    c: Tangent(g3,g2)
    c: Coincident(g4,g0)
    c: Distance(g4) = 3
    c: Vertical(g4)
    c: Coincident(g5,g4)
    c: Horizontal(g5)
    c: Coincident(g6,g2)
    c: Coincident(g6,g5)
    c: Vertical(g6)
    c: Horizontal(g7)
    c: Distance(g7) = 105
    c: Coincident(g7,g1)
    c: Block(g3)
    c: Weight(g8) = 1
    c: Equal(g8,g9)
    c: Equal(g8,g10)
    c: InternalAlignment(g8,g11)
    c: InternalAlignment(g9,g11)
    c: InternalAlignment(g10,g11)
    c: InternalAlignment(g12,g11)
    c: InternalAlignment(g13,g11)
    c: Block(g11)
    c: Coincident(g14,g11)
    c: Coincident(g14,g3)
    c: Horizontal(g14)
    c: Block(g15)
    c: Coincident(g16,g11)
    c: Coincident(g16,g15)
    c: Vertical(g16)
    c: Distance(g16) = 14
    c: Coincident(g17,g15)
    c: Block(g18)
    c: Coincident(g19,g18)
    c: Coincident(g20,g7)
    c: Horizontal(g20)
    c: Vertical(g21)
    c: Coincident(g20,g21)
    c: Block(g20)
    c: Block(g21)
    c: Block(g19)
    c: Block(g17)
    c: Distance(g20) = 1.61553
FEATURE [Part::Extrusion] Extrude044
  Base = -> Sketch053
  Dir = (0,0,1)
  DirMode = 2
  FaceMakerClass = Part::FaceMakerBullseye
  LengthFwd = 72
  LengthRev = 0
  Solid = true
  Symmetric = false
FEATURE [Part::Fillet] Fillet036  label="top018"
  Base = -> Extrude044
  Edges = 1 edges r=2: [Edge41]
FEATURE [Sketcher::SketchObject] Sketch054
  FullyConstrained = false
  Placement = pos=(0,0,0) rot=(1,0,0;1.5708rad)
  sketch-geometry (24):
    g0: ArcOfCircle CenterX=-4 CenterY=-10.5 CenterZ=0 NormalX=0 NormalY=0 NormalZ=1 AngleXU=0 Radius=1.5 StartAngle=6e-16 EndAngle=3.14159
    g1: ArcOfCircle CenterX=-34.2 CenterY=-10.5 CenterZ=0 NormalX=0 NormalY=0 NormalZ=1 AngleXU=0 Radius=1.5 StartAngle=0 EndAngle=3.14159
    g2: ArcOfCircle CenterX=-34.2 CenterY=-27.7 CenterZ=0 NormalX=0 NormalY=0 NormalZ=1 AngleXU=0 Radius=1.5 StartAngle=3.14159 EndAngle=6.28319
    g3: ArcOfCircle CenterX=-4 CenterY=-27.7 CenterZ=0 NormalX=0 NormalY=0 NormalZ=1 AngleXU=0 Radius=1.5 StartAngle=3.1416 EndAngle=6.28319
    g4: ArcOfCircle CenterX=-10 CenterY=-4.3 CenterZ=0 NormalX=0 NormalY=0 NormalZ=1 AngleXU=0 Radius=1.5 StartAngle=2e-16 EndAngle=3.14159
    g5: ArcOfCircle CenterX=-16.1 CenterY=-1.8 CenterZ=0 NormalX=0 NormalY=0 NormalZ=1 AngleXU=0 Radius=1.5 StartAngle=5e-16 EndAngle=3.14159
    g6: ArcOfCircle CenterX=-22.1 CenterY=-1.8 CenterZ=0 NormalX=0 NormalY=0 NormalZ=1 AngleXU=0 Radius=1.5 StartAngle=5e-16 EndAngle=3.14159
    g7: ArcOfCircle CenterX=-28.2 CenterY=-4.3 CenterZ=0 NormalX=0 NormalY=0 NormalZ=1 AngleXU=0 Radius=1.5 StartAngle=2e-16 EndAngle=3.14159
    g8: ArcOfCircle CenterX=-10 CenterY=-33.9 CenterZ=0 NormalX=0 NormalY=0 NormalZ=1 AngleXU=0 Radius=1.5 StartAngle=3.14159 EndAngle=6.28319
    g9: ArcOfCircle CenterX=-16.1 CenterY=-36.4 CenterZ=0 NormalX=0 NormalY=0 NormalZ=1 AngleXU=0 Radius=1.5 StartAngle=3.14159 EndAngle=6.28319
    g10: ArcOfCircle CenterX=-22.1 CenterY=-36.4 CenterZ=0 NormalX=0 NormalY=0 NormalZ=1 AngleXU=0 Radius=1.5 StartAngle=3.14159 EndAngle=6.28319
    g11: ArcOfCircle CenterX=-28.2 CenterY=-33.9 CenterZ=0 NormalX=0 NormalY=0 NormalZ=1 AngleXU=0 Radius=1.5 StartAngle=3.14159 EndAngle=6.28319
    g12: LineSegment StartX=-35.7 StartY=-10.5 StartZ=0 EndX=-35.7 EndY=-27.7 EndZ=0
    g13: LineSegment StartX=-32.7 StartY=-10.5 StartZ=0 EndX=-32.7 EndY=-27.7 EndZ=0
    g14: LineSegment StartX=-29.7 StartY=-33.9 StartZ=0 EndX=-29.7 EndY=-4.3 EndZ=0
    g15: LineSegment StartX=-26.7 StartY=-33.9 StartZ=0 EndX=-26.7 EndY=-4.3 EndZ=0
    g16: LineSegment StartX=-2.5 StartY=-10.5 StartZ=0 EndX=-2.5 EndY=-27.7 EndZ=0
    g17: LineSegment StartX=-8.5 StartY=-4.3 StartZ=0 EndX=-8.5 EndY=-33.9 EndZ=0
    g18: LineSegment StartX=-5.5 StartY=-10.5 StartZ=0 EndX=-5.5 EndY=-27.7 EndZ=0
    g19: LineSegment StartX=-11.5 StartY=-4.3 StartZ=0 EndX=-11.5 EndY=-33.9 EndZ=0
    g20: LineSegment StartX=-14.6 StartY=-1.8 StartZ=0 EndX=-14.6 EndY=-36.4 EndZ=0
    g21: LineSegment StartX=-17.6 StartY=-1.8 StartZ=0 EndX=-17.6 EndY=-36.4 EndZ=0
    g22: LineSegment StartX=-20.6 StartY=-36.4 StartZ=0 EndX=-20.6 EndY=-1.8 EndZ=0
    g23: LineSegment StartX=-23.6 StartY=-1.8 StartZ=0 EndX=-23.6 EndY=-36.4 EndZ=0
  constraints (48):
    c: Block(g0)
    c: Block(g1)
    c: Block(g2)
    c: Block(g3)
    c: Block(g4)
    c: Block(g5)
    c: Block(g6)
    c: Block(g7)
    c: Block(g8)
    c: Block(g9)
    c: Block(g10)
    c: Block(g11)
    c: Coincident(g12,g1)
    c: Coincident(g12,g2)
    c: Vertical(g12)
    c: Coincident(g13,g1)
    c: Coincident(g13,g2)
    c: Vertical(g13)
    c: Coincident(g14,g11)
    c: Coincident(g14,g7)
    c: Vertical(g14)
    c: Coincident(g15,g11)
    c: Coincident(g15,g7)
    c: Vertical(g15)
    c: Coincident(g16,g0)
    c: Coincident(g16,g3)
    c: Vertical(g16)
    c: Coincident(g17,g4)
    c: Coincident(g17,g8)
    c: Vertical(g17)
    c: Coincident(g18,g0)
    c: Coincident(g18,g3)
    c: Vertical(g18)
    c: Coincident(g19,g4)
    c: Coincident(g19,g8)
    c: Vertical(g19)
    c: Coincident(g20,g5)
    c: Coincident(g20,g9)
    c: Vertical(g20)
    c: Coincident(g21,g5)
    c: Coincident(g21,g9)
    c: Vertical(g21)
    c: Coincident(g22,g10)
    c: Coincident(g22,g6)
    c: Vertical(g22)
    c: Coincident(g23,g6)
    c: Coincident(g23,g10)
    c: Vertical(g23)
FEATURE [Part::Extrusion] Extrude045  label="removeToCreateFanGrillHoles003"
  Base = -> Sketch054
  Dir = (0,-1,6e-16)
  DirMode = 2
  FaceMakerClass = Part::FaceMakerBullseye
  LengthFwd = 10
  LengthRev = 0
  Placement = pos=(65.4,44,54.82) rot=(0,0,1;0rad)
  Solid = true
  Symmetric = false
FEATURE [Part::Feature] Face105 .. Face108  x4 (patterned run collapsed; names and placements below)
  shape: bbox 3.5 x 17.8 x 2e-07 mm, 1 faces, 0 solids (baked)
FEATURE [Part::Revolution] Revolve113  label="removeToCreateScrewAndThreadedInsertHole041"
  Angle = 360
  Axis = (0,1,0)
  Base = (0,0,0)
  FaceMakerClass = Part::FaceMakerBullseye
  Placement = pos=(62.3,30.3,19.7) rot=(0,0,1;0rad)
  Solid = false
  Source = -> Face105
  Symmetric = false
FEATURE [Part::Revolution] Revolve114  label="removeToCreateScrewAndThreadedInsertHole042"
  Angle = 360
  Axis = (0,1,0)
  Base = (0,0,0)
  FaceMakerClass = Part::FaceMakerBullseye
  Placement = pos=(62.3,30.3,51.7) rot=(0,0,1;0rad)
  Solid = false
  Source = -> Face106
  Symmetric = false
FEATURE [Part::Revolution] Revolve115  label="removeToCreateScrewAndThreadedInsertHole043"
  Angle = 360
  Axis = (0,1,0)
  Base = (0,0,0)
  FaceMakerClass = Part::FaceMakerBullseye
  Placement = pos=(30.3,30.3,19.7) rot=(0,0,1;0rad)
  Solid = false
  Source = -> Face107
  Symmetric = false
FEATURE [Part::Revolution] Revolve116  label="removeToCreateScrewAndThreadedInsertHole044"
  Angle = 360
  Axis = (0,1,0)
  Base = (0,0,0)
  FaceMakerClass = Part::FaceMakerBullseye
  Placement = pos=(30.3,30.3,51.7) rot=(0,0,1;0rad)
  Solid = false
  Source = -> Face108
  Symmetric = false
FEATURE [Part::MultiFuse] Fusion083  label="createThreadedInsertHolesForFan004"
  Shapes = -> [Revolve113,Revolve114,Revolve115,Revolve116]
FEATURE [Part::Box] Box024  label="removeToCreteHoleForPlugHousing026"
  AttacherType = Attacher::AttachEngine3D
  Height = 28.6
  Length = 10
  Placement = pos=(-2,0,21.7) rot=(0,0,1;0rad)
  Width = 19
FEATURE [Part::Cylinder] Cylinder038  label="removeToCreteHoleForPlugHousing027"
  Angle = 360
  AttacherType = Attacher::AttachEngine3D
  Height = 20
  Placement = pos=(-2,19,36) rot=(0,1,0;1.5708rad)
  Radius = 14.3
FEATURE [Part::MultiFuse] Fusion084  label="removeToCreteHoleForPlugHousing028"
  Shapes = -> [Box024,Cylinder038]
FEATURE [Part::Cylinder] Cylinder039
  Angle = 360
  AttacherType = Attacher::AttachEngine3D
  Height = 20
  Placement = pos=(0,0,36.15) rot=(0,0,1;0rad)
  Radius = 14.3
FEATURE [Part::Cylinder] Cylinder040
  Angle = 360
  AttacherType = Attacher::AttachEngine3D
  Height = 10
  Placement = pos=(0,0,36.15) rot=(0,0,1;0rad)
  Radius = 4
FEATURE [Part::Box] Box025  label="removeToCreteHoleForPlugHousing030"
  AttacherType = Attacher::AttachEngine3D
  Height = 28.6
  Length = 20
  Placement = pos=(106.15,0,21.7) rot=(0,0,1;0rad)
  Width = 19
FEATURE [Part::MultiFuse] Fusion086  label="removeToCreteHoleForPlugHousing031"
  Placement = pos=(70,19,36) rot=(0,1,0;1.5708rad)
  Shapes = -> [Cylinder039,Cylinder040]
FEATURE [Part::MultiFuse] Fusion085  label="removeToCreteHoleForPlugHousing029"
  Shapes = -> [Box025,Fusion086]
FEATURE [Sketcher::SketchObject] Sketch055
  FullyConstrained = true
  Placement = pos=(117,19,0) rot=(0.57735,0.57735,0.57735;2.0944rad)
  sketch-geometry (48):
    g0: LineSegment StartX=-49.19 StartY=69.25 StartZ=0 EndX=-49.19 EndY=66.25 EndZ=0
    g1: LineSegment StartX=-49.19 StartY=63.5 StartZ=0 EndX=-49.19 EndY=60.5 EndZ=0
    g2: LineSegment StartX=-49.19 StartY=57.75 StartZ=0 EndX=-49.19 EndY=54.75 EndZ=0
    g3: LineSegment StartX=-49.19 StartY=52 StartZ=0 EndX=-49.19 EndY=49 EndZ=0
    g4: LineSegment StartX=-49.19 StartY=46.25 StartZ=0 EndX=-49.19 EndY=43.25 EndZ=0
    g5: LineSegment StartX=-49.19 StartY=40.5 StartZ=0 EndX=-49.19 EndY=37.5 EndZ=0
    g6: LineSegment StartX=-49.19 StartY=34.5 StartZ=0 EndX=-49.19 EndY=31.5 EndZ=0
    g7: LineSegment StartX=-49.19 StartY=28.75 StartZ=0 EndX=-49.19 EndY=25.75 EndZ=0
    g8: LineSegment StartX=-49.19 StartY=23 StartZ=0 EndX=-49.19 EndY=20 EndZ=0
    g9: LineSegment StartX=-49.19 StartY=17.25 StartZ=0 EndX=-49.19 EndY=14.25 EndZ=0
    g10: LineSegment StartX=-49.19 StartY=11.5 StartZ=0 EndX=-49.19 EndY=8.5 EndZ=0
    g11: LineSegment StartX=-49.19 StartY=5.75 StartZ=0 EndX=-49.19 EndY=2.75 EndZ=0
    g12: ArcOfCircle CenterX=-1.5 CenterY=67.75 CenterZ=0 NormalX=0 NormalY=0 NormalZ=1 AngleXU=0 Radius=1.5 StartAngle=4.71239 EndAngle=7.85398
    g13: ArcOfCircle CenterX=-1.5 CenterY=62 CenterZ=0 NormalX=0 NormalY=0 NormalZ=1 AngleXU=0 Radius=1.5 StartAngle=4.71239 EndAngle=7.85398
    g14: ArcOfCircle CenterX=-1.5 CenterY=56.25 CenterZ=0 NormalX=0 NormalY=0 NormalZ=1 AngleXU=0 Radius=1.5 StartAngle=4.71239 EndAngle=7.85398
    g15: ArcOfCircle CenterX=-11.49 CenterY=50.5 CenterZ=0 NormalX=0 NormalY=0 NormalZ=1 AngleXU=0 Radius=1.5 StartAngle=4.71239 EndAngle=7.85398
    g16: ArcOfCircle CenterX=-16.28 CenterY=44.75 CenterZ=0 NormalX=0 NormalY=0 NormalZ=1 AngleXU=0 Radius=1.5 StartAngle=4.71239 EndAngle=7.85398
    g17: ArcOfCircle CenterX=-18.2337 CenterY=39 CenterZ=0 NormalX=0 NormalY=0 NormalZ=1 AngleXU=0 Radius=1.5 StartAngle=4.71485 EndAngle=7.85398
    g18: ArcOfCircle CenterX=-16.2837 CenterY=27.25 CenterZ=0 NormalX=0 NormalY=0 NormalZ=1 AngleXU=0 Radius=1.5 StartAngle=4.71485 EndAngle=7.85398
    g19: ArcOfCircle CenterX=-18.2337 CenterY=33 CenterZ=0 NormalX=0 NormalY=0 NormalZ=1 AngleXU=0 Radius=1.5 StartAngle=4.71485 EndAngle=7.85398
    g20: ArcOfCircle CenterX=-11.49 CenterY=21.5 CenterZ=0 NormalX=0 NormalY=0 NormalZ=1 AngleXU=0 Radius=1.5 StartAngle=4.71239 EndAngle=7.85398
    g21: ArcOfCircle CenterX=-1.5 CenterY=4.25 CenterZ=0 NormalX=0 NormalY=0 NormalZ=1 AngleXU=0 Radius=1.5 StartAngle=4.71239 EndAngle=7.85398
    g22: ArcOfCircle CenterX=-1.5 CenterY=10 CenterZ=0 NormalX=0 NormalY=0 NormalZ=1 AngleXU=0 Radius=1.5 StartAngle=4.71239 EndAngle=7.85398
    g23: ArcOfCircle CenterX=-1.5 CenterY=15.75 CenterZ=0 NormalX=0 NormalY=0 NormalZ=1 AngleXU=0 Radius=1.5 StartAngle=4.71239 EndAngle=7.85398
    g24: LineSegment StartX=-49.19 StartY=69.25 StartZ=0 EndX=-1.5 EndY=69.25 EndZ=0
    g25: LineSegment StartX=-49.19 StartY=66.25 StartZ=0 EndX=-1.5 EndY=66.25 EndZ=0
    g26: LineSegment StartX=-49.19 StartY=63.5 StartZ=0 EndX=-1.5 EndY=63.5 EndZ=0
    g27: LineSegment StartX=-49.19 StartY=60.5 StartZ=0 EndX=-1.5 EndY=60.5 EndZ=0
    g28: LineSegment StartX=-49.19 StartY=57.75 StartZ=0 EndX=-1.5 EndY=57.75 EndZ=0
    g29: LineSegment StartX=-49.19 StartY=54.75 StartZ=0 EndX=-1.5 EndY=54.75 EndZ=0
    g30: LineSegment StartX=-49.19 StartY=52 StartZ=0 EndX=-11.49 EndY=52 EndZ=0
    g31: LineSegment StartX=-49.19 StartY=49 StartZ=0 EndX=-11.49 EndY=49 EndZ=0
    g32: LineSegment StartX=-49.19 StartY=46.25 StartZ=0 EndX=-16.28 EndY=46.25 EndZ=0
    g33: LineSegment StartX=-49.19 StartY=43.25 StartZ=0 EndX=-16.28 EndY=43.25 EndZ=0
    g34: LineSegment StartX=-49.19 StartY=40.5 StartZ=0 EndX=-18.2337 EndY=40.5 EndZ=0
    g35: LineSegment StartX=-49.19 StartY=37.5 StartZ=0 EndX=-18.23 EndY=37.5 EndZ=0
    g36: LineSegment StartX=-49.19 StartY=34.5 StartZ=0 EndX=-18.2337 EndY=34.5 EndZ=0
    g37: LineSegment StartX=-49.19 StartY=31.5 StartZ=0 EndX=-18.23 EndY=31.5 EndZ=0
    g38: LineSegment StartX=-49.19 StartY=28.75 StartZ=0 EndX=-16.2837 EndY=28.75 EndZ=0
    g39: LineSegment StartX=-49.19 StartY=25.75 StartZ=0 EndX=-16.28 EndY=25.75 EndZ=0
    g40: LineSegment StartX=-49.19 StartY=23 StartZ=0 EndX=-11.49 EndY=23 EndZ=0
    g41: LineSegment StartX=-49.19 StartY=20 StartZ=0 EndX=-11.49 EndY=20 EndZ=0
    g42: LineSegment StartX=-49.19 StartY=17.25 StartZ=0 EndX=-1.5 EndY=17.25 EndZ=0
    g43: LineSegment StartX=-49.19 StartY=14.25 StartZ=0 EndX=-1.5 EndY=14.25 EndZ=0
    g44: LineSegment StartX=-49.19 StartY=11.5 StartZ=0 EndX=-1.5 EndY=11.5 EndZ=0
    g45: LineSegment StartX=-49.19 StartY=8.5 StartZ=0 EndX=-1.5 EndY=8.5 EndZ=0
    g46: LineSegment StartX=-49.19 StartY=5.75 StartZ=0 EndX=-1.5 EndY=5.75 EndZ=0
    g47: LineSegment StartX=-49.19 StartY=2.75 StartZ=0 EndX=-1.5 EndY=2.75 EndZ=0
  constraints (120):
    c: Vertical(g0)
    c: Distance(g0) = 3
    c: Block(g0)
    c: Vertical(g1)
    c: Distance(g1) = 3
    c: Vertical(g2)
    c: Equal(g0,g2) = 3
    c: Block(g2)
    c: Vertical(g3)
    c: Equal(g1,g3) = 3
    c: Vertical(g4)
    c: Equal(g0,g4) = 3
    c: Block(g4)
    c: Vertical(g5)
    c: Equal(g1,g5) = 3
    c: Vertical(g6)
    c: Equal(g0,g6) = 3
    c: Block(g6)
    c: Vertical(g7)
    c: Equal(g1,g7) = 3
    c: Vertical(g8)
    c: Equal(g0,g8) = 3
    c: Block(g8)
    c: Vertical(g9)
    c: Equal(g1,g9) = 3
    c: Vertical(g10)
    c: Equal(g0,g10) = 3
    c: Block(g10)
    c: Vertical(g11)
    c: Equal(g1,g11) = 3
    c: Block(g12)
    c: Block(g13)
    c: Block(g14)
    c: Block(g15)
    c: Block(g16)
    c: Block(g17)
    c: Block(g18)
    c: Block(g19)
    c: Block(g20)
    c: Block(g21)
    c: Block(g22)
    c: Block(g23)
    c: Block(g11)
    c: Block(g9)
    c: Block(g7)
    c: Block(g5)
    c: Block(g3)
    c: Block(g1)
    c: Coincident(g24,g0)
    c: Coincident(g24,g12)
    c: Horizontal(g24)
    c: Coincident(g25,g0)
    c: Coincident(g25,g12)
    c: Horizontal(g25)
    c: Coincident(g26,g1)
    c: Coincident(g26,g13)
    c: Horizontal(g26)
    c: Coincident(g27,g1)
    c: Coincident(g27,g13)
    c: Horizontal(g27)
    c: Coincident(g28,g2)
    c: Coincident(g28,g14)
    c: Horizontal(g28)
    c: Coincident(g29,g2)
    c: Coincident(g29,g14)
    c: Horizontal(g29)
    c: Coincident(g30,g3)
    c: Coincident(g30,g15)
    c: Horizontal(g30)
    c: Coincident(g31,g3)
    c: Coincident(g31,g15)
    c: Horizontal(g31)
    c: Coincident(g32,g4)
    c: Coincident(g32,g16)
    c: Horizontal(g32)
    c: Coincident(g33,g4)
    c: Coincident(g33,g16)
    c: Horizontal(g33)
    c: Coincident(g34,g5)
    c: Coincident(g34,g17)
    c: Horizontal(g34)
    c: Coincident(g35,g5)
    c: Coincident(g35,g17)
    c: Horizontal(g35)
    c: Coincident(g36,g6)
    c: Coincident(g36,g19)
    c: Horizontal(g36)
    c: Coincident(g37,g6)
    c: Coincident(g37,g19)
    c: Horizontal(g37)
    c: Coincident(g38,g7)
    c: Coincident(g38,g18)
    c: Horizontal(g38)
    c: Coincident(g39,g7)
    c: Coincident(g39,g18)
    c: Horizontal(g39)
    c: Coincident(g40,g8)
    c: Coincident(g40,g20)
    c: Horizontal(g40)
    c: Coincident(g41,g8)
    c: Coincident(g41,g20)
    c: Horizontal(g41)
    c: Coincident(g42,g9)
    c: Coincident(g42,g23)
    c: Horizontal(g42)
    c: Coincident(g43,g9)
    c: Coincident(g43,g23)
    c: Horizontal(g43)
    c: Coincident(g44,g10)
    c: Coincident(g44,g22)
    c: Horizontal(g44)
    c: Coincident(g45,g10)
    c: Coincident(g45,g22)
    c: Horizontal(g45)
    c: Coincident(g46,g11)
    c: Coincident(g46,g21)
    c: Horizontal(g46)
    c: Coincident(g47,g11)
    c: Coincident(g47,g21)
    c: Horizontal(g47)
FEATURE [Part::Extrusion] Extrude046
  Base = -> Sketch055
  Dir = (1,0,0)
  DirMode = 2
  FaceMakerClass = Part::FaceMakerBullseye
  LengthFwd = 23
  LengthRev = 0
  Placement = pos=(-19,0,0) rot=(0,0,1;0rad)
  Solid = true
  Symmetric = false
FEATURE [Part::Fillet] Fillet038  label="removeToCreateVentalationHoles001"
  Base = -> Extrude046
  Edges = <same value as first occurrence — deduplicated (x6 in doc)>
  Placement = pos=(7,0,0) rot=(0,0,1;0rad)
FEATURE [Sketcher::SketchObject] Sketch056  label="topSketch014"
  FullyConstrained = true
  sketch-geometry (22):
    g0: LineSegment StartX=5.21097e-06 StartY=3 StartZ=0 EndX=5.21097e-06 EndY=19 EndZ=0
    g1: ArcOfCircle CenterX=19 CenterY=19 CenterZ=0 NormalX=0 NormalY=0 NormalZ=1 AngleXU=0 Radius=19 StartAngle=1.5708 EndAngle=3.14159
    g2: ArcOfCircle CenterX=19 CenterY=19 CenterZ=0 NormalX=0 NormalY=0 NormalZ=1 AngleXU=0 Radius=16 StartAngle=1.5708 EndAngle=3.14159
    g3: LineSegment StartX=114 StartY=35 StartZ=0 EndX=19 EndY=35 EndZ=0
    g4: LineSegment StartX=5.21097e-06 StartY=3 StartZ=0 EndX=5.21097e-06 EndY=0 EndZ=0
    g5: LineSegment StartX=3 StartY=0 StartZ=0 EndX=5.21097e-06 EndY=0 EndZ=0
    g6: LineSegment StartX=3 StartY=19 StartZ=0 EndX=3 EndY=0 EndZ=0
    g7: LineSegment StartX=19 StartY=38 StartZ=0 EndX=124 EndY=38 EndZ=0
    g8: Circle CenterX=119 CenterY=35 CenterZ=0 NormalX=0 NormalY=0 NormalZ=1 AngleXU=0 Radius=1
    g9: Circle CenterX=121 CenterY=35 CenterZ=0 NormalX=0 NormalY=0 NormalZ=1 AngleXU=0 Radius=1
    g10: Circle CenterX=121 CenterY=33 CenterZ=0 NormalX=0 NormalY=0 NormalZ=1 AngleXU=0 Radius=1
    g11: BSplineCurve PolesCount=3 KnotsCount=2 Degree=2 IsPeriodic=0
    g12: GeomPoint X=119 Y=35 Z=0
    g13: GeomPoint X=121 Y=33 Z=0
    g14: LineSegment StartX=119 StartY=35 StartZ=0 EndX=114 EndY=35 EndZ=0
    g15: ArcOfCircle CenterX=105 CenterY=19 CenterZ=0 NormalX=0 NormalY=0 NormalZ=1 AngleXU=0 Radius=16 StartAngle=5.60905 EndAngle=6.28319
    g16: LineSegment StartX=121 StartY=33 StartZ=0 EndX=121 EndY=19 EndZ=0
    g17: LineSegment StartX=117.5 StartY=9.01251 StartZ=0 EndX=121.163 EndY=9.0125 EndZ=0
    g18: ArcOfCircle CenterX=105 CenterY=19 CenterZ=0 NormalX=0 NormalY=0 NormalZ=1 AngleXU=0 Radius=20.6155 StartAngle=5.7297 EndAngle=6.28319
    g19: LineSegment StartX=121.163 StartY=9.0125 StartZ=0 EndX=122.538 EndY=8.16329 EndZ=0
    g20: LineSegment StartX=124 StartY=38 StartZ=0 EndX=125.616 EndY=38 EndZ=0
    g21: LineSegment StartX=125.616 StartY=19 StartZ=0 EndX=125.616 EndY=38 EndZ=0
  constraints (49):
    c: Vertical(g0)
    c: Block(g0)
    c: Coincident(g1,g0)
    c: Block(g1)
    c: Coincident(g2,g1)
    c: Block(g2)
    c: Coincident(g3,g2)
    c: Horizontal(g3)
    c: Tangent(g3,g2)
    c: Coincident(g4,g0)
    c: Distance(g4) = 3
    c: Vertical(g4)
    c: Coincident(g5,g4)
    c: Horizontal(g5)
    c: Coincident(g6,g2)
    c: Coincident(g6,g5)
    c: Vertical(g6)
    c: Horizontal(g7)
    c: Distance(g7) = 105
    c: Coincident(g7,g1)
    c: Block(g3)
    c: Weight(g8) = 1
    c: Equal(g8,g9)
    c: Equal(g8,g10)
    c: InternalAlignment(g8,g11)
    c: InternalAlignment(g9,g11)
    c: InternalAlignment(g10,g11)
    c: InternalAlignment(g12,g11)
    c: InternalAlignment(g13,g11)
    c: Block(g11)
    c: Coincident(g14,g11)
    c: Coincident(g14,g3)
    c: Horizontal(g14)
    c: Block(g15)
    c: Coincident(g16,g11)
    c: Coincident(g16,g15)
    c: Vertical(g16)
    c: Distance(g16) = 14
    c: Coincident(g17,g15)
    c: Block(g18)
    c: Coincident(g19,g18)
    c: Coincident(g20,g7)
    c: Horizontal(g20)
    c: Vertical(g21)
    c: Coincident(g20,g21)
    c: Block(g20)
    c: Block(g21)
    c: Block(g19)
    c: Block(g17)
FEATURE [Part::Box] Box026  label="removeToCreteHoleForPlugHousing032"
  AttacherType = Attacher::AttachEngine3D
  Height = 28.6
  Length = 10
  Placement = pos=(-2,0,21.7) rot=(0,0,1;0rad)
  Width = 19
FEATURE [Part::Feature] Face109 .. Face112  x4 (patterned run collapsed; names and placements below)
  shape: bbox 3.5 x 17.8 x 2e-07 mm, 1 faces, 0 solids (baked)
FEATURE [Part::Revolution] Revolve117  label="removeToCreateScrewAndThreadedInsertHole045"
  Angle = 360
  Axis = (0,1,0)
  Base = (0,0,0)
  FaceMakerClass = Part::FaceMakerBullseye
  Placement = pos=(62.3,30.3,19.7) rot=(0,0,1;0rad)
  Solid = false
  Source = -> Face109
  Symmetric = false
FEATURE [Part::Revolution] Revolve118  label="removeToCreateScrewAndThreadedInsertHole046"
  Angle = 360
  Axis = (0,1,0)
  Base = (0,0,0)
  FaceMakerClass = Part::FaceMakerBullseye
  Placement = pos=(62.3,30.3,51.7) rot=(0,0,1;0rad)
  Solid = false
  Source = -> Face110
  Symmetric = false
FEATURE [Part::Revolution] Revolve119  label="removeToCreateScrewAndThreadedInsertHole047"
  Angle = 360
  Axis = (0,1,0)
  Base = (0,0,0)
  FaceMakerClass = Part::FaceMakerBullseye
  Placement = pos=(30.3,30.3,19.7) rot=(0,0,1;0rad)
  Solid = false
  Source = -> Face111
  Symmetric = false
FEATURE [Part::Revolution] Revolve120  label="removeToCreateScrewAndThreadedInsertHole048"
  Angle = 360
  Axis = (0,1,0)
  Base = (0,0,0)
  FaceMakerClass = Part::FaceMakerBullseye
  Placement = pos=(30.3,30.3,51.7) rot=(0,0,1;0rad)
  Solid = false
  Source = -> Face112
  Symmetric = false
FEATURE [Part::MultiFuse] Fusion087  label="createThreadedInsertHolesForFan005"
  Shapes = -> [Revolve117,Revolve118,Revolve119,Revolve120]
FEATURE [Part::Extrusion] Extrude047
  Base = -> Sketch056
  Dir = (0,0,1)
  DirMode = 2
  FaceMakerClass = Part::FaceMakerBullseye
  LengthFwd = 72
  LengthRev = 0
  Solid = true
  Symmetric = false
FEATURE [Part::Fillet] Fillet039  label="top019"
  Base = -> Extrude047
  Edges = 1 edges r=2: [Edge35]
FEATURE [Sketcher::SketchObject] Sketch057
  FullyConstrained = false
  Placement = pos=(0,0,0) rot=(1,0,0;1.5708rad)
  sketch-geometry (24):
    g0: ArcOfCircle CenterX=-4 CenterY=-10.5 CenterZ=0 NormalX=0 NormalY=0 NormalZ=1 AngleXU=0 Radius=1.5 StartAngle=6e-16 EndAngle=3.14159
    g1: ArcOfCircle CenterX=-34.2 CenterY=-10.5 CenterZ=0 NormalX=0 NormalY=0 NormalZ=1 AngleXU=0 Radius=1.5 StartAngle=0 EndAngle=3.14159
    g2: ArcOfCircle CenterX=-34.2 CenterY=-27.7 CenterZ=0 NormalX=0 NormalY=0 NormalZ=1 AngleXU=0 Radius=1.5 StartAngle=3.14159 EndAngle=6.28319
    g3: ArcOfCircle CenterX=-4 CenterY=-27.7 CenterZ=0 NormalX=0 NormalY=0 NormalZ=1 AngleXU=0 Radius=1.5 StartAngle=3.1416 EndAngle=6.28319
    g4: ArcOfCircle CenterX=-10 CenterY=-4.3 CenterZ=0 NormalX=0 NormalY=0 NormalZ=1 AngleXU=0 Radius=1.5 StartAngle=2e-16 EndAngle=3.14159
    g5: ArcOfCircle CenterX=-16.1 CenterY=-1.8 CenterZ=0 NormalX=0 NormalY=0 NormalZ=1 AngleXU=0 Radius=1.5 StartAngle=5e-16 EndAngle=3.14159
    g6: ArcOfCircle CenterX=-22.1 CenterY=-1.8 CenterZ=0 NormalX=0 NormalY=0 NormalZ=1 AngleXU=0 Radius=1.5 StartAngle=5e-16 EndAngle=3.14159
    g7: ArcOfCircle CenterX=-28.2 CenterY=-4.3 CenterZ=0 NormalX=0 NormalY=0 NormalZ=1 AngleXU=0 Radius=1.5 StartAngle=2e-16 EndAngle=3.14159
    g8: ArcOfCircle CenterX=-10 CenterY=-33.9 CenterZ=0 NormalX=0 NormalY=0 NormalZ=1 AngleXU=0 Radius=1.5 StartAngle=3.14159 EndAngle=6.28319
    g9: ArcOfCircle CenterX=-16.1 CenterY=-36.4 CenterZ=0 NormalX=0 NormalY=0 NormalZ=1 AngleXU=0 Radius=1.5 StartAngle=3.14159 EndAngle=6.28319
    g10: ArcOfCircle CenterX=-22.1 CenterY=-36.4 CenterZ=0 NormalX=0 NormalY=0 NormalZ=1 AngleXU=0 Radius=1.5 StartAngle=3.14159 EndAngle=6.28319
    g11: ArcOfCircle CenterX=-28.2 CenterY=-33.9 CenterZ=0 NormalX=0 NormalY=0 NormalZ=1 AngleXU=0 Radius=1.5 StartAngle=3.14159 EndAngle=6.28319
    g12: LineSegment StartX=-35.7 StartY=-10.5 StartZ=0 EndX=-35.7 EndY=-27.7 EndZ=0
    g13: LineSegment StartX=-32.7 StartY=-10.5 StartZ=0 EndX=-32.7 EndY=-27.7 EndZ=0
    g14: LineSegment StartX=-29.7 StartY=-33.9 StartZ=0 EndX=-29.7 EndY=-4.3 EndZ=0
    g15: LineSegment StartX=-26.7 StartY=-33.9 StartZ=0 EndX=-26.7 EndY=-4.3 EndZ=0
    g16: LineSegment StartX=-2.5 StartY=-10.5 StartZ=0 EndX=-2.5 EndY=-27.7 EndZ=0
    g17: LineSegment StartX=-8.5 StartY=-4.3 StartZ=0 EndX=-8.5 EndY=-33.9 EndZ=0
    g18: LineSegment StartX=-5.5 StartY=-10.5 StartZ=0 EndX=-5.5 EndY=-27.7 EndZ=0
    g19: LineSegment StartX=-11.5 StartY=-4.3 StartZ=0 EndX=-11.5 EndY=-33.9 EndZ=0
    g20: LineSegment StartX=-14.6 StartY=-1.8 StartZ=0 EndX=-14.6 EndY=-36.4 EndZ=0
    g21: LineSegment StartX=-17.6 StartY=-1.8 StartZ=0 EndX=-17.6 EndY=-36.4 EndZ=0
    g22: LineSegment StartX=-20.6 StartY=-36.4 StartZ=0 EndX=-20.6 EndY=-1.8 EndZ=0
    g23: LineSegment StartX=-23.6 StartY=-1.8 StartZ=0 EndX=-23.6 EndY=-36.4 EndZ=0
  constraints (48):
    c: Block(g0)
    c: Block(g1)
    c: Block(g2)
    c: Block(g3)
    c: Block(g4)
    c: Block(g5)
    c: Block(g6)
    c: Block(g7)
    c: Block(g8)
    c: Block(g9)
    c: Block(g10)
    c: Block(g11)
    c: Coincident(g12,g1)
    c: Coincident(g12,g2)
    c: Vertical(g12)
    c: Coincident(g13,g1)
    c: Coincident(g13,g2)
    c: Vertical(g13)
    c: Coincident(g14,g11)
    c: Coincident(g14,g7)
    c: Vertical(g14)
    c: Coincident(g15,g11)
    c: Coincident(g15,g7)
    c: Vertical(g15)
    c: Coincident(g16,g0)
    c: Coincident(g16,g3)
    c: Vertical(g16)
    c: Coincident(g17,g4)
    c: Coincident(g17,g8)
    c: Vertical(g17)
    c: Coincident(g18,g0)
    c: Coincident(g18,g3)
    c: Vertical(g18)
    c: Coincident(g19,g4)
    c: Coincident(g19,g8)
    c: Vertical(g19)
    c: Coincident(g20,g5)
    c: Coincident(g20,g9)
    c: Vertical(g20)
    c: Coincident(g21,g5)
    c: Coincident(g21,g9)
    c: Vertical(g21)
    c: Coincident(g22,g10)
    c: Coincident(g22,g6)
    c: Vertical(g22)
    c: Coincident(g23,g6)
    c: Coincident(g23,g10)
    c: Vertical(g23)
FEATURE [Part::Extrusion] Extrude048  label="removeToCreateFanGrillHoles004"
  Base = -> Sketch057
  Dir = (0,-1,6e-16)
  DirMode = 2
  FaceMakerClass = Part::FaceMakerBullseye
  LengthFwd = 10
  LengthRev = 0
  Placement = pos=(65.4,44,54.82) rot=(0,0,1;0rad)
  Solid = true
  Symmetric = false
FEATURE [Part::Cut] Cut040  label="top021"
  Base = -> Fillet039
  Tool = -> Extrude048
FEATURE [Part::Cylinder] Cylinder041  label="removeToCreteHoleForPlugHousing034"
  Angle = 360
  AttacherType = Attacher::AttachEngine3D
  Height = 20
  Placement = pos=(-2,19,36) rot=(0,1,0;1.5708rad)
  Radius = 14.3
FEATURE [Part::MultiFuse] Fusion089  label="removeToCreteHoleForPlugHousing035"
  Shapes = -> [Box026,Cylinder041]
FEATURE [Part::Cylinder] Cylinder042
  Angle = 360
  AttacherType = Attacher::AttachEngine3D
  Height = 20
  Placement = pos=(0,0,36.15) rot=(0,0,1;0rad)
  Radius = 14.3
FEATURE [Part::Cylinder] Cylinder043
  Angle = 360
  AttacherType = Attacher::AttachEngine3D
  Height = 10
  Placement = pos=(0,0,36.15) rot=(0,0,1;0rad)
  Radius = 4
FEATURE [Part::Box] Box027  label="removeToCreteHoleForPlugHousing036"
  AttacherType = Attacher::AttachEngine3D
  Height = 28.6
  Length = 20
  Placement = pos=(106.15,0,21.7) rot=(0,0,1;0rad)
  Width = 19
FEATURE [Part::Cut] Cut041  label="top022"
  Base = -> Cut040
  Tool = -> Fusion087
FEATURE [Part::Cut] Cut039  label="top020"
  Base = -> Cut041
  Tool = -> Fusion089
FEATURE [Part::MultiFuse] Fusion090  label="removeToCreteHoleForPlugHousing037"
  Placement = pos=(70,19,36) rot=(0,1,0;1.5708rad)
  Shapes = -> [Cylinder042,Cylinder043]
FEATURE [Part::MultiFuse] Fusion088  label="removeToCreteHoleForPlugHousing033"
  Shapes = -> [Box027,Fusion090]
FEATURE [Part::Cut] Cut042  label="removeToCreteHoleForPlugHousing038"
  Base = -> Cut039
  Tool = -> Fusion088
FEATURE [Part::MultiFuse] Fusion091  label="removeFromTop"
  Shapes = -> [Fillet038,Fusion085,Fusion084,Fusion083,Extrude045]
FEATURE [Part::Cut] Cut043  label="REAL TOP ====="
  Base = -> Fillet036
  Tool = -> Fusion091
FEATURE [Part::MultiFuse] Fusion092  label="caseScrewPillarBracket016"
  Shapes = -> [Extrude030,Extrude031,Extrude032,Extrude033,Extrude034,Extrude035,Extrude036,Extrude037,Box013,Box014]
FEATURE [Sketcher::SketchObject] Sketch058  label="topSketch015"
  FullyConstrained = true
  sketch-geometry (20):
    g0: LineSegment StartX=5.21097e-06 StartY=3 StartZ=0 EndX=5.21097e-06 EndY=19 EndZ=0
    g1: ArcOfCircle CenterX=19 CenterY=19 CenterZ=0 NormalX=0 NormalY=0 NormalZ=1 AngleXU=0 Radius=19 StartAngle=1.5708 EndAngle=3.14159
    g2: ArcOfCircle CenterX=19 CenterY=19 CenterZ=0 NormalX=0 NormalY=0 NormalZ=1 AngleXU=0 Radius=16 StartAngle=1.5708 EndAngle=3.14159
    g3: LineSegment StartX=114 StartY=35 StartZ=0 EndX=19 EndY=35 EndZ=0
    g4: LineSegment StartX=5.21097e-06 StartY=3 StartZ=0 EndX=5.21097e-06 EndY=0 EndZ=0
    g5: LineSegment StartX=3 StartY=0 StartZ=0 EndX=5.21097e-06 EndY=0 EndZ=0
    g6: LineSegment StartX=3 StartY=19 StartZ=0 EndX=3 EndY=0 EndZ=0
    g7: LineSegment StartX=19 StartY=38 StartZ=0 EndX=124 EndY=38 EndZ=0
    g8: Circle CenterX=119 CenterY=35 CenterZ=0 NormalX=0 NormalY=0 NormalZ=1 AngleXU=0 Radius=1
    g9: Circle CenterX=121 CenterY=35 CenterZ=0 NormalX=0 NormalY=0 NormalZ=1 AngleXU=0 Radius=1
    g10: Circle CenterX=121 CenterY=33 CenterZ=0 NormalX=0 NormalY=0 NormalZ=1 AngleXU=0 Radius=1
    g11: BSplineCurve PolesCount=3 KnotsCount=2 Degree=2 IsPeriodic=0
    g12: GeomPoint X=119 Y=35 Z=0
    g13: GeomPoint X=121 Y=33 Z=0
    g14: LineSegment StartX=119 StartY=35 StartZ=0 EndX=114 EndY=35 EndZ=0
    g15: ArcOfCircle CenterX=105 CenterY=19 CenterZ=0 NormalX=0 NormalY=0 NormalZ=1 AngleXU=0 Radius=19 StartAngle=5.7297 EndAngle=6.28319
    g16: ArcOfCircle CenterX=105 CenterY=19 CenterZ=0 NormalX=0 NormalY=0 NormalZ=1 AngleXU=0 Radius=16 StartAngle=5.60905 EndAngle=6.28319
    g17: LineSegment StartX=121 StartY=33 StartZ=0 EndX=121 EndY=19 EndZ=0
    g18: LineSegment StartX=124 StartY=38 StartZ=0 EndX=124 EndY=19 EndZ=0
    g19: LineSegment StartX=117.5 StartY=9.01251 StartZ=0 EndX=121.163 EndY=9.0125 EndZ=0
  constraints (46):
    c: Vertical(g0)
    c: Block(g0)
    c: Coincident(g1,g0)
    c: Block(g1)
    c: Coincident(g2,g1)
    c: Block(g2)
    c: Coincident(g3,g2)
    c: Horizontal(g3)
    c: Tangent(g3,g2)
    c: Coincident(g4,g0)
    c: Distance(g4) = 3
    c: Vertical(g4)
    c: Coincident(g5,g4)
    c: Horizontal(g5)
    c: Coincident(g6,g2)
    c: Coincident(g6,g5)
    c: Vertical(g6)
    c: Horizontal(g7)
    c: Distance(g7) = 105
    c: Coincident(g7,g1)
    c: Block(g3)
    c: Weight(g8) = 1
    c: Equal(g8,g9)
    c: Equal(g8,g10)
    c: InternalAlignment(g8,g11)
    c: InternalAlignment(g9,g11)
    c: InternalAlignment(g10,g11)
    c: InternalAlignment(g12,g11)
    c: InternalAlignment(g13,g11)
    c: Block(g11)
    c: Coincident(g14,g11)
    c: Coincident(g14,g3)
    c: Horizontal(g14)
    c: Block(g15)
    c: Coincident(g16,g15)
    c: Block(g16)
    c: Coincident(g17,g11)
    c: Coincident(g17,g16)
    c: Vertical(g17)
    c: Distance(g17) = 14
    c: Coincident(g18,g7)
    c: Coincident(g18,g15)
    c: Vertical(g18)
    c: Distance(g18) = 19
    c: Coincident(g19,g16)
    c: Coincident(g19,g15)
FEATURE [Part::Extrusion] Extrude049  label="top023"
  Base = -> Sketch058
  Dir = (0,0,1)
  DirMode = 2
  FaceMakerClass = Part::FaceMakerBullseye
  LengthFwd = 72
  LengthRev = 0
  Solid = true
  Symmetric = false
FEATURE [Sketcher::SketchObject] Sketch059
  FullyConstrained = true
  MapMode = 3
  Placement = pos=(0,0,0) rot=(1,0,0;1.5708rad)
  Support = -> [Extrude049]
  sketch-geometry (8):
    g0: Circle CenterX=80.351 CenterY=-67.6202 CenterZ=0 NormalX=0 NormalY=0 NormalZ=1 AngleXU=0 Radius=2
    g1: Circle CenterX=80.351 CenterY=-67.6202 CenterZ=0 NormalX=0 NormalY=0 NormalZ=1 AngleXU=0 Radius=3
    g2: Circle CenterX=80.351 CenterY=-4.92017 CenterZ=0 NormalX=0 NormalY=0 NormalZ=1 AngleXU=0 Radius=2
    g3: Circle CenterX=80.351 CenterY=-4.92017 CenterZ=0 NormalX=0 NormalY=0 NormalZ=1 AngleXU=0 Radius=3
    g4: Circle CenterX=23.851 CenterY=-4.92017 CenterZ=0 NormalX=0 NormalY=0 NormalZ=1 AngleXU=0 Radius=2
    g5: Circle CenterX=23.851 CenterY=-4.92017 CenterZ=0 NormalX=0 NormalY=0 NormalZ=1 AngleXU=0 Radius=3
    g6: Circle CenterX=23.851 CenterY=-67.6202 CenterZ=0 NormalX=0 NormalY=0 NormalZ=1 AngleXU=0 Radius=2
    g7: Circle CenterX=23.851 CenterY=-67.6202 CenterZ=0 NormalX=0 NormalY=0 NormalZ=1 AngleXU=0 Radius=3
  constraints (8):
    c: Block(g3)
    c: Block(g2)
    c: Block(g1)
    c: Block(g0)
    c: Block(g6)
    c: Block(g7)
    c: Block(g4)
    c: Block(g5)
FEATURE [Sketcher::SketchObject] Sketch060
  FullyConstrained = true
  MapMode = 3
  Placement = pos=(0,0,0) rot=(1,0,0;1.5708rad)
  Support = -> [Extrude049]
  sketch-geometry (8):
    g0: Circle CenterX=80.351 CenterY=-67.6202 CenterZ=0 NormalX=0 NormalY=0 NormalZ=1 AngleXU=0 Radius=3
    g1: Circle CenterX=80.351 CenterY=-4.92017 CenterZ=0 NormalX=0 NormalY=0 NormalZ=1 AngleXU=0 Radius=3
    g2: Circle CenterX=23.851 CenterY=-4.92017 CenterZ=0 NormalX=0 NormalY=0 NormalZ=1 AngleXU=0 Radius=3
    g3: Circle CenterX=23.851 CenterY=-67.6202 CenterZ=0 NormalX=0 NormalY=0 NormalZ=1 AngleXU=0 Radius=3
    g4: Circle CenterX=23.851 CenterY=-67.6202 CenterZ=0 NormalX=0 NormalY=0 NormalZ=1 AngleXU=0 Radius=5
    g5: Circle CenterX=80.351 CenterY=-67.6202 CenterZ=0 NormalX=0 NormalY=0 NormalZ=1 AngleXU=0 Radius=5
    g6: Circle CenterX=23.851 CenterY=-4.92017 CenterZ=0 NormalX=0 NormalY=0 NormalZ=1 AngleXU=0 Radius=5
    g7: Circle CenterX=80.351 CenterY=-4.92017 CenterZ=0 NormalX=0 NormalY=0 NormalZ=1 AngleXU=0 Radius=5
  constraints (8):
    c: Block(g1)
    c: Block(g0)
    c: Block(g3)
    c: Block(g2)
    c: Block(g5)
    c: Block(g4)
    c: Block(g6)
    c: Block(g7)
FEATURE [Sketcher::SketchObject] Sketch061
  FullyConstrained = true
  MapMode = 3
  Placement = pos=(0,0,0) rot=(1,0,0;1.5708rad)
  sketch-geometry (8):
    g0: Circle CenterX=80.351 CenterY=-67.6202 CenterZ=0 NormalX=0 NormalY=0 NormalZ=1 AngleXU=0 Radius=3
    g1: Circle CenterX=80.351 CenterY=-4.92017 CenterZ=0 NormalX=0 NormalY=0 NormalZ=1 AngleXU=0 Radius=3
    g2: Circle CenterX=23.851 CenterY=-4.92017 CenterZ=0 NormalX=0 NormalY=0 NormalZ=1 AngleXU=0 Radius=3
    g3: Circle CenterX=23.851 CenterY=-67.6202 CenterZ=0 NormalX=0 NormalY=0 NormalZ=1 AngleXU=0 Radius=3
    g4: Circle CenterX=23.851 CenterY=-67.6202 CenterZ=0 NormalX=0 NormalY=0 NormalZ=1 AngleXU=0 Radius=5
    g5: Circle CenterX=80.351 CenterY=-67.6202 CenterZ=0 NormalX=0 NormalY=0 NormalZ=1 AngleXU=0 Radius=5
    g6: Circle CenterX=23.851 CenterY=-4.92017 CenterZ=0 NormalX=0 NormalY=0 NormalZ=1 AngleXU=0 Radius=5
    g7: Circle CenterX=80.351 CenterY=-4.92017 CenterZ=0 NormalX=0 NormalY=0 NormalZ=1 AngleXU=0 Radius=5
  constraints (8):
    c: Block(g1)
    c: Block(g0)
    c: Block(g3)
    c: Block(g2)
    c: Block(g5)
    c: Block(g4)
    c: Block(g6)
    c: Block(g7)
FEATURE [Sketcher::SketchObject] Sketch062  label="topSketch016"
  FullyConstrained = true
  sketch-geometry (20):
    g0: LineSegment StartX=5.21097e-06 StartY=3 StartZ=0 EndX=5.21097e-06 EndY=19 EndZ=0
    g1: ArcOfCircle CenterX=19 CenterY=19 CenterZ=0 NormalX=0 NormalY=0 NormalZ=1 AngleXU=0 Radius=19 StartAngle=1.5708 EndAngle=3.14159
    g2: ArcOfCircle CenterX=19 CenterY=19 CenterZ=0 NormalX=0 NormalY=0 NormalZ=1 AngleXU=0 Radius=16 StartAngle=1.5708 EndAngle=3.14159
    g3: LineSegment StartX=114 StartY=35 StartZ=0 EndX=19 EndY=35 EndZ=0
    g4: LineSegment StartX=5.21097e-06 StartY=3 StartZ=0 EndX=5.21097e-06 EndY=0 EndZ=0
    g5: LineSegment StartX=3 StartY=0 StartZ=0 EndX=5.21097e-06 EndY=0 EndZ=0
    g6: LineSegment StartX=3 StartY=19 StartZ=0 EndX=3 EndY=0 EndZ=0
    g7: LineSegment StartX=19 StartY=38 StartZ=0 EndX=124 EndY=38 EndZ=0
    g8: Circle CenterX=119 CenterY=35 CenterZ=0 NormalX=0 NormalY=0 NormalZ=1 AngleXU=0 Radius=1
    g9: Circle CenterX=121 CenterY=35 CenterZ=0 NormalX=0 NormalY=0 NormalZ=1 AngleXU=0 Radius=1
    g10: Circle CenterX=121 CenterY=33 CenterZ=0 NormalX=0 NormalY=0 NormalZ=1 AngleXU=0 Radius=1
    g11: BSplineCurve PolesCount=3 KnotsCount=2 Degree=2 IsPeriodic=0
    g12: GeomPoint X=119 Y=35 Z=0
    g13: GeomPoint X=121 Y=33 Z=0
    g14: LineSegment StartX=119 StartY=35 StartZ=0 EndX=114 EndY=35 EndZ=0
    g15: ArcOfCircle CenterX=105 CenterY=19 CenterZ=0 NormalX=0 NormalY=0 NormalZ=1 AngleXU=0 Radius=19 StartAngle=5.7297 EndAngle=6.28319
    g16: ArcOfCircle CenterX=105 CenterY=19 CenterZ=0 NormalX=0 NormalY=0 NormalZ=1 AngleXU=0 Radius=16 StartAngle=5.60905 EndAngle=6.28319
    g17: LineSegment StartX=121 StartY=33 StartZ=0 EndX=121 EndY=19 EndZ=0
    g18: LineSegment StartX=124 StartY=38 StartZ=0 EndX=124 EndY=19 EndZ=0
    g19: LineSegment StartX=117.5 StartY=9.01251 StartZ=0 EndX=121.163 EndY=9.0125 EndZ=0
  constraints (46):
    c: Vertical(g0)
    c: Block(g0)
    c: Coincident(g1,g0)
    c: Block(g1)
    c: Coincident(g2,g1)
    c: Block(g2)
    c: Coincident(g3,g2)
    c: Horizontal(g3)
    c: Tangent(g3,g2)
    c: Coincident(g4,g0)
    c: Distance(g4) = 3
    c: Vertical(g4)
    c: Coincident(g5,g4)
    c: Horizontal(g5)
    c: Coincident(g6,g2)
    c: Coincident(g6,g5)
    c: Vertical(g6)
    c: Horizontal(g7)
    c: Distance(g7) = 105
    c: Coincident(g7,g1)
    c: Block(g3)
    c: Weight(g8) = 1
    c: Equal(g8,g9)
    c: Equal(g8,g10)
    c: InternalAlignment(g8,g11)
    c: InternalAlignment(g9,g11)
    c: InternalAlignment(g10,g11)
    c: InternalAlignment(g12,g11)
    c: InternalAlignment(g13,g11)
    c: Block(g11)
    c: Coincident(g14,g11)
    c: Coincident(g14,g3)
    c: Horizontal(g14)
    c: Block(g15)
    c: Coincident(g16,g15)
    c: Block(g16)
    c: Coincident(g17,g11)
    c: Coincident(g17,g16)
    c: Vertical(g17)
    c: Distance(g17) = 14
    c: Coincident(g18,g7)
    c: Coincident(g18,g15)
    c: Vertical(g18)
    c: Distance(g18) = 19
    c: Coincident(g19,g16)
    c: Coincident(g19,g15)
FEATURE [Part::Extrusion] Extrude053  label="top024"
  Base = -> Sketch062
  Dir = (0,0,1)
  DirMode = 2
  FaceMakerClass = Part::FaceMakerBullseye
  LengthFwd = 72
  LengthRev = 0
  Solid = true
  Symmetric = false
FEATURE [Sketcher::SketchObject] Sketch063
  FullyConstrained = true
  MapMode = 3
  Placement = pos=(0,0,0) rot=(1,0,0;1.5708rad)
  Support = -> [Extrude053]
  sketch-geometry (8):
    g0: Circle CenterX=80.351 CenterY=-67.6202 CenterZ=0 NormalX=0 NormalY=0 NormalZ=1 AngleXU=0 Radius=2
    g1: Circle CenterX=80.351 CenterY=-67.6202 CenterZ=0 NormalX=0 NormalY=0 NormalZ=1 AngleXU=0 Radius=3
    g2: Circle CenterX=80.351 CenterY=-4.92017 CenterZ=0 NormalX=0 NormalY=0 NormalZ=1 AngleXU=0 Radius=2
    g3: Circle CenterX=80.351 CenterY=-4.92017 CenterZ=0 NormalX=0 NormalY=0 NormalZ=1 AngleXU=0 Radius=3
    g4: Circle CenterX=23.851 CenterY=-4.92017 CenterZ=0 NormalX=0 NormalY=0 NormalZ=1 AngleXU=0 Radius=2
    g5: Circle CenterX=23.851 CenterY=-4.92017 CenterZ=0 NormalX=0 NormalY=0 NormalZ=1 AngleXU=0 Radius=3
    g6: Circle CenterX=23.851 CenterY=-67.6202 CenterZ=0 NormalX=0 NormalY=0 NormalZ=1 AngleXU=0 Radius=2
    g7: Circle CenterX=23.851 CenterY=-67.6202 CenterZ=0 NormalX=0 NormalY=0 NormalZ=1 AngleXU=0 Radius=3
  constraints (8):
    c: Block(g3)
    c: Block(g2)
    c: Block(g1)
    c: Block(g0)
    c: Block(g6)
    c: Block(g7)
    c: Block(g4)
    c: Block(g5)
FEATURE [Part::Extrusion] Extrude054
  Base = -> Sketch063
  Dir = (0,-1,2e-16)
  DirMode = 2
  FaceMakerClass = Part::FaceMakerBullseye
  LengthFwd = 6
  LengthRev = 0
  Placement = pos=(0,9,0) rot=(0,0,1;0rad)
  Solid = true
  Symmetric = false
FEATURE [Sketcher::SketchObject] Sketch064  label="topSketch017"
  FullyConstrained = true
  sketch-geometry (20):
    g0: LineSegment StartX=5.21097e-06 StartY=3 StartZ=0 EndX=5.21097e-06 EndY=19 EndZ=0
    g1: ArcOfCircle CenterX=19 CenterY=19 CenterZ=0 NormalX=0 NormalY=0 NormalZ=1 AngleXU=0 Radius=19 StartAngle=1.5708 EndAngle=3.14159
    g2: ArcOfCircle CenterX=19 CenterY=19 CenterZ=0 NormalX=0 NormalY=0 NormalZ=1 AngleXU=0 Radius=16 StartAngle=1.5708 EndAngle=3.14159
    g3: LineSegment StartX=114 StartY=35 StartZ=0 EndX=19 EndY=35 EndZ=0
    g4: LineSegment StartX=5.21097e-06 StartY=3 StartZ=0 EndX=5.21097e-06 EndY=0 EndZ=0
    g5: LineSegment StartX=3 StartY=0 StartZ=0 EndX=5.21097e-06 EndY=0 EndZ=0
    g6: LineSegment StartX=3 StartY=19 StartZ=0 EndX=3 EndY=0 EndZ=0
    g7: LineSegment StartX=19 StartY=38 StartZ=0 EndX=124 EndY=38 EndZ=0
    g8: Circle CenterX=119 CenterY=35 CenterZ=0 NormalX=0 NormalY=0 NormalZ=1 AngleXU=0 Radius=1
    g9: Circle CenterX=121 CenterY=35 CenterZ=0 NormalX=0 NormalY=0 NormalZ=1 AngleXU=0 Radius=1
    g10: Circle CenterX=121 CenterY=33 CenterZ=0 NormalX=0 NormalY=0 NormalZ=1 AngleXU=0 Radius=1
    g11: BSplineCurve PolesCount=3 KnotsCount=2 Degree=2 IsPeriodic=0
    g12: GeomPoint X=119 Y=35 Z=0
    g13: GeomPoint X=121 Y=33 Z=0
    g14: LineSegment StartX=119 StartY=35 StartZ=0 EndX=114 EndY=35 EndZ=0
    g15: ArcOfCircle CenterX=105 CenterY=19 CenterZ=0 NormalX=0 NormalY=0 NormalZ=1 AngleXU=0 Radius=19 StartAngle=5.7297 EndAngle=6.28319
    g16: ArcOfCircle CenterX=105 CenterY=19 CenterZ=0 NormalX=0 NormalY=0 NormalZ=1 AngleXU=0 Radius=16 StartAngle=5.60905 EndAngle=6.28319
    g17: LineSegment StartX=121 StartY=33 StartZ=0 EndX=121 EndY=19 EndZ=0
    g18: LineSegment StartX=124 StartY=38 StartZ=0 EndX=124 EndY=19 EndZ=0
    g19: LineSegment StartX=117.5 StartY=9.01251 StartZ=0 EndX=121.163 EndY=9.0125 EndZ=0
  constraints (46):
    c: Vertical(g0)
    c: Block(g0)
    c: Coincident(g1,g0)
    c: Block(g1)
    c: Coincident(g2,g1)
    c: Block(g2)
    c: Coincident(g3,g2)
    c: Horizontal(g3)
    c: Tangent(g3,g2)
    c: Coincident(g4,g0)
    c: Distance(g4) = 3
    c: Vertical(g4)
    c: Coincident(g5,g4)
    c: Horizontal(g5)
    c: Coincident(g6,g2)
    c: Coincident(g6,g5)
    c: Vertical(g6)
    c: Horizontal(g7)
    c: Distance(g7) = 105
    c: Coincident(g7,g1)
    c: Block(g3)
    c: Weight(g8) = 1
    c: Equal(g8,g9)
    c: Equal(g8,g10)
    c: InternalAlignment(g8,g11)
    c: InternalAlignment(g9,g11)
    c: InternalAlignment(g10,g11)
    c: InternalAlignment(g12,g11)
    c: InternalAlignment(g13,g11)
    c: Block(g11)
    c: Coincident(g14,g11)
    c: Coincident(g14,g3)
    c: Horizontal(g14)
    c: Block(g15)
    c: Coincident(g16,g15)
    c: Block(g16)
    c: Coincident(g17,g11)
    c: Coincident(g17,g16)
    c: Vertical(g17)
    c: Distance(g17) = 14
    c: Coincident(g18,g7)
    c: Coincident(g18,g15)
    c: Vertical(g18)
    c: Distance(g18) = 19
    c: Coincident(g19,g16)
    c: Coincident(g19,g15)
FEATURE [Sketcher::SketchObject] Sketch065
  FullyConstrained = true
  MapMode = 3
  Placement = pos=(0,0,0) rot=(1,0,0;1.5708rad)
  sketch-geometry (8):
    g0: Circle CenterX=80.351 CenterY=-67.6202 CenterZ=0 NormalX=0 NormalY=0 NormalZ=1 AngleXU=0 Radius=3
    g1: Circle CenterX=80.351 CenterY=-4.92017 CenterZ=0 NormalX=0 NormalY=0 NormalZ=1 AngleXU=0 Radius=3
    g2: Circle CenterX=23.851 CenterY=-4.92017 CenterZ=0 NormalX=0 NormalY=0 NormalZ=1 AngleXU=0 Radius=3
    g3: Circle CenterX=23.851 CenterY=-67.6202 CenterZ=0 NormalX=0 NormalY=0 NormalZ=1 AngleXU=0 Radius=3
    g4: Circle CenterX=23.851 CenterY=-67.6202 CenterZ=0 NormalX=0 NormalY=0 NormalZ=1 AngleXU=0 Radius=5
    g5: Circle CenterX=80.351 CenterY=-67.6202 CenterZ=0 NormalX=0 NormalY=0 NormalZ=1 AngleXU=0 Radius=5
    g6: Circle CenterX=23.851 CenterY=-4.92017 CenterZ=0 NormalX=0 NormalY=0 NormalZ=1 AngleXU=0 Radius=5
    g7: Circle CenterX=80.351 CenterY=-4.92017 CenterZ=0 NormalX=0 NormalY=0 NormalZ=1 AngleXU=0 Radius=5
  constraints (8):
    c: Block(g1)
    c: Block(g0)
    c: Block(g3)
    c: Block(g2)
    c: Block(g5)
    c: Block(g4)
    c: Block(g6)
    c: Block(g7)
FEATURE [Part::Extrusion] Extrude056
  Base = -> Sketch065
  Dir = (0,-1,2e-16)
  DirMode = 2
  FaceMakerClass = Part::FaceMakerBullseye
  LengthFwd = 2
  LengthRev = 0
  Solid = true
  Symmetric = false
FEATURE [Part::Extrusion] Extrude057  label="top025"
  Base = -> Sketch064
  Dir = (0,0,1)
  DirMode = 2
  FaceMakerClass = Part::FaceMakerBullseye
  LengthFwd = 72
  LengthRev = 0
  Solid = true
  Symmetric = false
FEATURE [Sketcher::SketchObject] Sketch066
  FullyConstrained = true
  MapMode = 3
  Placement = pos=(0,0,0) rot=(1,0,0;1.5708rad)
  Support = -> [Extrude057]
  sketch-geometry (8):
    g0: Circle CenterX=80.351 CenterY=-67.6202 CenterZ=0 NormalX=0 NormalY=0 NormalZ=1 AngleXU=0 Radius=3
    g1: Circle CenterX=80.351 CenterY=-4.92017 CenterZ=0 NormalX=0 NormalY=0 NormalZ=1 AngleXU=0 Radius=3
    g2: Circle CenterX=23.851 CenterY=-4.92017 CenterZ=0 NormalX=0 NormalY=0 NormalZ=1 AngleXU=0 Radius=3
    g3: Circle CenterX=23.851 CenterY=-67.6202 CenterZ=0 NormalX=0 NormalY=0 NormalZ=1 AngleXU=0 Radius=3
    g4: Circle CenterX=23.851 CenterY=-67.6202 CenterZ=0 NormalX=0 NormalY=0 NormalZ=1 AngleXU=0 Radius=5
    g5: Circle CenterX=80.351 CenterY=-67.6202 CenterZ=0 NormalX=0 NormalY=0 NormalZ=1 AngleXU=0 Radius=5
    g6: Circle CenterX=23.851 CenterY=-4.92017 CenterZ=0 NormalX=0 NormalY=0 NormalZ=1 AngleXU=0 Radius=5
    g7: Circle CenterX=80.351 CenterY=-4.92017 CenterZ=0 NormalX=0 NormalY=0 NormalZ=1 AngleXU=0 Radius=5
  constraints (8):
    c: Block(g1)
    c: Block(g0)
    c: Block(g3)
    c: Block(g2)
    c: Block(g5)
    c: Block(g4)
    c: Block(g6)
    c: Block(g7)
FEATURE [Part::Extrusion] Extrude055
  Base = -> Sketch066
  Dir = (0,-1,2e-16)
  DirMode = 2
  FaceMakerClass = Part::FaceMakerBullseye
  LengthFwd = 2
  LengthRev = 0
  Solid = true
  Symmetric = false
FEATURE [Part::Fillet] Fillet041
  Base = -> Extrude056
  Edges = 4 edges r=1.99: [Edge6,Edge12,Edge18,Edge24]
FEATURE [Part::Cut] Cut045
  Base = -> Extrude055
  Placement = pos=(0,6,0) rot=(0,0,1;0rad)
  Tool = -> Fillet041
FEATURE [Part::MultiFuse] Fusion095  label="pcbScrewPillars"
  Placement = pos=(-3.2,-1,72.3) rot=(0,0,1;0rad)
  Shapes = -> [Cut045,Extrude054]
FEATURE [Part::Feature] Face113
  shape: bbox 3.2 x 1.5 x 2e-07 mm, 1 faces, 0 solids (baked)
FEATURE [Part::Revolution] Revolve121  label="backCaseScrewRetainer002"
  Angle = 360
  Axis = (0,1,0)
  Base = (0,0,0)
  FaceMakerClass = Part::FaceMakerBullseye
  Placement = pos=(12.5,3,62) rot=(0,0,1;0rad)
  Solid = false
  Source = -> Face113
  Symmetric = false
FEATURE [Part::Feature] Face114
  shape: bbox 3.2 x 1.5 x 2e-07 mm, 1 faces, 0 solids (baked)
FEATURE [Part::Feature] Face115
  shape: bbox 3.2 x 1.5 x 2e-07 mm, 1 faces, 0 solids (baked)
FEATURE [Part::Feature] Face116
  shape: bbox 3.2 x 1.5 x 2e-07 mm, 1 faces, 0 solids (baked)
FEATURE [Part::Revolution] Revolve122  label="frontCaseScrewRetainer004"
  Angle = 360
  Axis = (0,1,0)
  Base = (0,0,0)
  FaceMakerClass = Part::FaceMakerBullseye
  Placement = pos=(89.5,3,68.5) rot=(0,0,1;0rad)
  Solid = false
  Source = -> Face115
  Symmetric = false
FEATURE [Part::Revolution] Revolve123  label="frontCaseScrewRetainer005"
  Angle = 360
  Axis = (0,1,0)
  Base = (0,0,0)
  FaceMakerClass = Part::FaceMakerBullseye
  Placement = pos=(89.5,3,3.5) rot=(0,0,1;0rad)
  Solid = false
  Source = -> Face116
  Symmetric = false
FEATURE [Part::Revolution] Revolve124  label="backCaseScrewRetainer003"
  Angle = 360
  Axis = (0,1,0)
  Base = (0,0,0)
  FaceMakerClass = Part::FaceMakerBullseye
  Placement = pos=(12.5,3,10) rot=(0,0,1;0rad)
  Solid = false
  Source = -> Face114
  Symmetric = false
FEATURE [Part::Feature] Face117
  shape: bbox 3.6 x 3.2 x 2e-07 mm, 1 faces, 0 solids (baked)
FEATURE [Part::Revolution] Revolve125  label="moreFrontCaseScrewRetainer004"
  Angle = 360
  Axis = (0,1,0)
  Base = (0,0,0)
  FaceMakerClass = Part::FaceMakerBullseye
  Placement = pos=(109.5,4.5,68.5) rot=(0,0,1;0rad)
  Solid = false
  Source = -> Face117
  Symmetric = false
FEATURE [Part::Feature] Face118
  shape: bbox 3.6 x 3.2 x 2e-07 mm, 1 faces, 0 solids (baked)
FEATURE [Part::Revolution] Revolve126  label="moreFrontCaseScrewRetainer005"
  Angle = 360
  Axis = (0,1,0)
  Base = (0,0,0)
  FaceMakerClass = Part::FaceMakerBullseye
  Placement = pos=(109.5,4.5,3.5) rot=(0,0,1;0rad)
  Solid = false
  Source = -> Face118
  Symmetric = false
FEATURE [Part::MultiFuse] Fusion096  label="screwRetainers001"
  Shapes = -> [Revolve126,Revolve125,Revolve124,Revolve123,Revolve122,Revolve121]
FEATURE [Part::Feature] Face119
  shape: bbox 10 x 16.5 x 2e-07 mm, 1 faces, 0 solids (baked)
FEATURE [Part::Revolution] Revolve130  label="plugHousing050"
  Angle = 360
  Axis = (0,1,0)
  Base = (0,0,0)
  FaceMakerClass = Part::FaceMakerBullseye
  Placement = pos=(0,0,36.15) rot=(0,0,1;0rad)
  Solid = false
  Source = -> Face119
  Symmetric = false
FEATURE [Part::Feature] Face120
  shape: bbox 10 x 16.5 x 2e-07 mm, 1 faces, 0 solids (baked)
FEATURE [Part::Feature] Face121
  shape: bbox 10 x 16.5 x 2e-07 mm, 1 faces, 0 solids (baked)
FEATURE [Part::Revolution] Revolve127  label="plugHousing047"
  Angle = 360
  Axis = (0,1,0)
  Base = (0,0,0)
  FaceMakerClass = Part::FaceMakerBullseye
  Placement = pos=(0,0,36.15) rot=(0,0,1;0rad)
  Solid = false
  Source = -> Face121
  Symmetric = false
FEATURE [Part::Feature] Face122
  shape: bbox 10 x 16.5 x 2e-07 mm, 1 faces, 0 solids (baked)
FEATURE [Part::Feature] Face123
  shape: bbox 10 x 16.5 x 2e-07 mm, 1 faces, 0 solids (baked)
FEATURE [Part::Revolution] Revolve128  label="plugHousing048"
  Angle = 360
  Axis = (0,1,0)
  Base = (0,0,0)
  FaceMakerClass = Part::FaceMakerBullseye
  Placement = pos=(0,0,36.15) rot=(0,0,1;0rad)
  Solid = false
  Source = -> Face123
  Symmetric = false
FEATURE [Part::MultiFuse] Fusion100  label="plugHousing054"
  Placement = pos=(0,0,0) rot=(0,0,1;1.5708rad)
  Shapes = -> [Revolve130,Revolve128]
FEATURE [Part::Feature] Face124
  shape: bbox 10 x 16.5 x 2e-07 mm, 1 faces, 0 solids (baked)
FEATURE [Part::Feature] Face125
  shape: bbox 10 x 16.5 x 2e-07 mm, 1 faces, 0 solids (baked)
FEATURE [Part::Revolution] Revolve129  label="plugHousing049"
  Angle = 360
  Axis = (0,1,0)
  Base = (0,0,0)
  FaceMakerClass = Part::FaceMakerBullseye
  Placement = pos=(0,0,36.15) rot=(0,0,1;0rad)
  Solid = false
  Source = -> Face125
  Symmetric = false
FEATURE [Part::Feature] Face126
  shape: bbox 10 x 16.5 x 2e-07 mm, 1 faces, 0 solids (baked)
FEATURE [Part::Revolution] Revolve131  label="plugHousing058"
  Angle = 360
  Axis = (0,1,0)
  Base = (0,0,0)
  FaceMakerClass = Part::FaceMakerBullseye
  Placement = pos=(0,0,36.15) rot=(0,0,1;0rad)
  Solid = false
  Source = -> Face120
  Symmetric = false
FEATURE [Part::MultiFuse] Fusion099  label="plugHousing053"
  Placement = pos=(0,0,0) rot=(0,0,1;1.5708rad)
  Shapes = -> [Revolve127,Revolve131]
FEATURE [Part::MultiFuse] Fusion102  label="plugHousing056"
  Placement = pos=(0,19,0) rot=(0,0,1;3.14159rad)
  Shapes = -> [Fusion100,Fusion099]
FEATURE [Part::Revolution] Revolve132  label="plugHousing059"
  Angle = 360
  Axis = (0,1,0)
  Base = (0,0,0)
  FaceMakerClass = Part::FaceMakerBullseye
  Placement = pos=(0,0,36.15) rot=(0,0,1;0rad)
  Solid = false
  Source = -> Face126
  Symmetric = false
FEATURE [Part::Revolution] Revolve133  label="plugHousing060"
  Angle = 360
  Axis = (0,1,0)
  Base = (0,0,0)
  FaceMakerClass = Part::FaceMakerBullseye
  Placement = pos=(0,0,36.15) rot=(0,0,1;0rad)
  Solid = false
  Source = -> Face122
  Symmetric = false
FEATURE [Part::MultiFuse] Fusion097  label="plugHousing051"
  Placement = pos=(0,0,0) rot=(0,0,1;1.5708rad)
  Shapes = -> [Revolve133,Revolve132]
FEATURE [Part::Revolution] Revolve134  label="plugHousing061"
  Angle = 360
  Axis = (0,1,0)
  Base = (0,0,0)
  FaceMakerClass = Part::FaceMakerBullseye
  Placement = pos=(0,0,36.15) rot=(0,0,1;0rad)
  Solid = false
  Source = -> Face124
  Symmetric = false
FEATURE [Part::MultiFuse] Fusion101  label="plugHousing055"
  Placement = pos=(0,0,0) rot=(0,0,1;1.5708rad)
  Shapes = -> [Revolve129,Revolve134]
FEATURE [Part::MultiFuse] Fusion098  label="plugHousing052"
  Placement = pos=(0,19,0) rot=(0,0,1;3.14159rad)
  Shapes = -> [Fusion097,Fusion101]
FEATURE [Part::MultiFuse] Fusion103  label="plugHousing057"
  Placement = pos=(122.621,0,-0.15) rot=(0,0,1;0rad)
  Shapes = -> [Fusion102,Fusion098]
FEATURE [Part::Box] Box028  label="Cube015"
  AttacherType = Attacher::AttachEngine3D
  Height = 28
  Length = 3
  Placement = pos=(110.7,19,22) rot=(0,0,1;0rad)
  Width = 15.7
FEATURE [Part::Cylinder] Cylinder044
  Angle = 360
  AttacherType = Attacher::AttachEngine3D
  Height = 20
  Placement = pos=(0,0,36.15) rot=(0,0,1;0rad)
  Radius = 10.3
FEATURE [Part::Cylinder] Cylinder045
  Angle = 360
  AttacherType = Attacher::AttachEngine3D
  Height = 10
  Placement = pos=(0,0,36.15) rot=(0,0,1;0rad)
  Radius = 4
FEATURE [Part::MultiFuse] Fusion104  label="removeToCreteHoleForPlugHousing040"
  Placement = pos=(70,19,36) rot=(0,1,0;1.5708rad)
  Shapes = -> [Cylinder044,Cylinder045]
FEATURE [Part::Cut] Cut046  label="plugHousingTab003"
  Base = -> Box028
  Tool = -> Fusion104
FEATURE [Part::MultiFuse] Fusion105  label="plugHousing062"
  Shapes = -> [Fusion103,Cut046]
FEATURE [Part::Fillet] Fillet042
  Base = -> Fusion105
  Edges = 1 edges r=2: [Edge25]
FEATURE [Part::Fillet] Fillet043  label="plugHousing063"
  Base = -> Fillet042
  Edges = 1 edges r=2: [Edge8]
  Placement = pos=(7,0,0) rot=(0,0,1;0rad)
FEATURE [Part::Feature] Face127
  shape: bbox 10 x 16.5 x 2e-07 mm, 1 faces, 0 solids (baked)
FEATURE [Part::Feature] Face128
  shape: bbox 10 x 16.5 x 2e-07 mm, 1 faces, 0 solids (baked)
FEATURE [Part::Revolution] Revolve137  label="plugHousing070"
  Angle = 360
  Axis = (0,1,0)
  Base = (0,0,0)
  FaceMakerClass = Part::FaceMakerBullseye
  Placement = pos=(0,0,36.15) rot=(0,0,1;0rad)
  Solid = false
  Source = -> Face127
  Symmetric = false
FEATURE [Part::Revolution] Revolve140  label="plugHousing073"
  Angle = 360
  Axis = (0,1,0)
  Base = (0,0,0)
  FaceMakerClass = Part::FaceMakerBullseye
  Placement = pos=(0,0,36.15) rot=(0,0,1;0rad)
  Solid = false
  Source = -> Face128
  Symmetric = false
FEATURE [Part::Feature] Face129
  shape: bbox 10 x 16.5 x 2e-07 mm, 1 faces, 0 solids (baked)
FEATURE [Part::Revolution] Revolve138  label="plugHousing071"
  Angle = 360
  Axis = (0,1,0)
  Base = (0,0,0)
  FaceMakerClass = Part::FaceMakerBullseye
  Placement = pos=(0,0,36.15) rot=(0,0,1;0rad)
  Solid = false
  Source = -> Face129
  Symmetric = false
FEATURE [Part::Feature] Face130
  shape: bbox 10 x 16.5 x 2e-07 mm, 1 faces, 0 solids (baked)
FEATURE [Part::Revolution] Revolve139  label="plugHousing072"
  Angle = 360
  Axis = (0,1,0)
  Base = (0,0,0)
  FaceMakerClass = Part::FaceMakerBullseye
  Placement = pos=(0,0,36.15) rot=(0,0,1;0rad)
  Solid = false
  Source = -> Face130
  Symmetric = false
FEATURE [Part::Feature] Face131
  shape: bbox 10 x 16.5 x 2e-07 mm, 1 faces, 0 solids (baked)
FEATURE [Part::Revolution] Revolve135  label="plugHousing068"
  Angle = 360
  Axis = (0,1,0)
  Base = (0,0,0)
  FaceMakerClass = Part::FaceMakerBullseye
  Placement = pos=(0,0,36.15) rot=(0,0,1;0rad)
  Solid = false
  Source = -> Face131
  Symmetric = false
FEATURE [Part::MultiFuse] Fusion112  label="plugHousing078"
  Placement = pos=(0,0,0) rot=(0,0,1;1.5708rad)
  Shapes = -> [Revolve135,Revolve139]
FEATURE [Part::Feature] Face132
  shape: bbox 10 x 16.5 x 2e-07 mm, 1 faces, 0 solids (baked)
FEATURE [Part::Revolution] Revolve141  label="plugHousing074"
  Angle = 360
  Axis = (0,1,0)
  Base = (0,0,0)
  FaceMakerClass = Part::FaceMakerBullseye
  Placement = pos=(0,0,36.15) rot=(0,0,1;0rad)
  Solid = false
  Source = -> Face132
  Symmetric = false
FEATURE [Part::MultiFuse] Fusion110  label="plugHousing076"
  Placement = pos=(0,0,0) rot=(0,0,1;1.5708rad)
  Shapes = -> [Revolve141,Revolve140]
FEATURE [Part::Feature] Face133
  shape: bbox 10 x 16.5 x 2e-07 mm, 1 faces, 0 solids (baked)
FEATURE [Part::Revolution] Revolve136  label="plugHousing069"
  Angle = 360
  Axis = (0,1,0)
  Base = (0,0,0)
  FaceMakerClass = Part::FaceMakerBullseye
  Placement = pos=(0,0,36.15) rot=(0,0,1;0rad)
  Solid = false
  Source = -> Face133
  Symmetric = false
FEATURE [Part::MultiFuse] Fusion106  label="plugHousing064"
  Placement = pos=(0,0,0) rot=(0,0,1;1.5708rad)
  Shapes = -> [Revolve138,Revolve136]
FEATURE [Part::MultiFuse] Fusion108  label="plugHousing066"
  Placement = pos=(0,19,0) rot=(0,0,1;3.14159rad)
  Shapes = -> [Fusion106,Fusion112]
FEATURE [Part::Feature] Face134
  shape: bbox 10 x 16.5 x 2e-07 mm, 1 faces, 0 solids (baked)
FEATURE [Part::Revolution] Revolve142  label="plugHousing075"
  Angle = 360
  Axis = (0,1,0)
  Base = (0,0,0)
  FaceMakerClass = Part::FaceMakerBullseye
  Placement = pos=(0,0,36.15) rot=(0,0,1;0rad)
  Solid = false
  Source = -> Face134
  Symmetric = false
FEATURE [Part::MultiFuse] Fusion107  label="plugHousing065"
  Placement = pos=(0,0,0) rot=(0,0,1;1.5708rad)
  Shapes = -> [Revolve137,Revolve142]
FEATURE [Part::MultiFuse] Fusion111  label="plugHousing077"
  Placement = pos=(0,19,0) rot=(0,0,1;3.14159rad)
  Shapes = -> [Fusion110,Fusion107]
FEATURE [Part::MultiFuse] Fusion109  label="plugHousing067"
  Placement = pos=(131.236,0,-0.15) rot=(0,0,1;0rad)
  Shapes = -> [Fusion108,Fusion111]
FEATURE [Part::MultiFuse] Fusion113  label="plugHousing079"
  Shapes = -> [Fillet043,Fusion109]
FEATURE [Part::Feature] Face135
  shape: bbox 3.5 x 17.8 x 2e-07 mm, 1 faces, 0 solids (baked)
FEATURE [Part::Revolution] Revolve143  label="removeToCreateScrewAndThreadedInsertHole049"
  Angle = 360
  Axis = (0,1,0)
  Base = (0,0,0)
  FaceMakerClass = Part::FaceMakerBullseye
  Placement = pos=(12.5,0,10) rot=(0,0,1;0rad)
  Solid = false
  Source = -> Face135
  Symmetric = false
FEATURE [Part::Feature] Face136
  shape: bbox 3.5 x 17.8 x 2e-07 mm, 1 faces, 0 solids (baked)
FEATURE [Part::Revolution] Revolve144  label="removeToCreateScrewAndThreadedInsertHole050"
  Angle = 360
  Axis = (0,1,0)
  Base = (0,0,0)
  FaceMakerClass = Part::FaceMakerBullseye
  Placement = pos=(12.5,0,62) rot=(0,0,1;0rad)
  Solid = false
  Source = -> Face136
  Symmetric = false
FEATURE [Part::Feature] Face137
  shape: bbox 3.5 x 17.8 x 2e-07 mm, 1 faces, 0 solids (baked)
FEATURE [Part::Revolution] Revolve145  label="removeToCreateScrewAndThreadedInsertHole051"
  Angle = 360
  Axis = (0,1,0)
  Base = (0,0,0)
  FaceMakerClass = Part::FaceMakerBullseye
  Placement = pos=(89.5,0,68.5) rot=(0,0,1;0rad)
  Solid = false
  Source = -> Face137
  Symmetric = false
FEATURE [Part::Feature] Face138
  shape: bbox 3.5 x 17.8 x 2e-07 mm, 1 faces, 0 solids (baked)
FEATURE [Part::Revolution] Revolve146  label="removeToCreateScrewAndThreadedInsertHole052"
  Angle = 360
  Axis = (0,1,0)
  Base = (0,0,0)
  FaceMakerClass = Part::FaceMakerBullseye
  Placement = pos=(89.5,0,3.5) rot=(0,0,1;0rad)
  Solid = false
  Source = -> Face138
  Symmetric = false
FEATURE [Part::Feature] Face139
  shape: bbox 3.5 x 17.8 x 2e-07 mm, 1 faces, 0 solids (baked)
FEATURE [Part::Revolution] Revolve147  label="removeToCreateScrewAndThreadedInsertHole053"
  Angle = 360
  Axis = (0,1,0)
  Base = (0,0,0)
  FaceMakerClass = Part::FaceMakerBullseye
  Placement = pos=(109.5,4.7,3.5) rot=(0,0,1;0rad)
  Solid = false
  Source = -> Face139
  Symmetric = false
FEATURE [Part::Feature] Face140
  shape: bbox 3.5 x 17.8 x 2e-07 mm, 1 faces, 0 solids (baked)
FEATURE [Part::Revolution] Revolve148  label="removeToCreateScrewAndThreadedInsertHole054"
  Angle = 360
  Axis = (0,1,0)
  Base = (0,0,0)
  FaceMakerClass = Part::FaceMakerBullseye
  Placement = pos=(109.5,4.7,68.5) rot=(0,0,1;0rad)
  Solid = false
  Source = -> Face140
  Symmetric = false
FEATURE [Part::MultiFuse] Fusion114  label="removeToCreateScrewAndThreadedInsertHole055"
  Shapes = -> [Revolve148,Revolve147,Revolve146,Revolve145,Revolve144,Revolve143]
FEATURE [Part::Cut] Cut047  label="casePillars004"
  Base = -> Cut037
  Tool = -> Fusion114
FEATURE [Part::Feature] Face141
  shape: bbox 3.5 x 17.8 x 2e-07 mm, 1 faces, 0 solids (baked)
FEATURE [Part::Feature] Face142
  shape: bbox 3.5 x 17.8 x 2e-07 mm, 1 faces, 0 solids (baked)
FEATURE [Part::Feature] Face143
  shape: bbox 3.5 x 17.8 x 2e-07 mm, 1 faces, 0 solids (baked)
FEATURE [Part::Revolution] Revolve149  label="removeToCreateScrewAndThreadedInsertHole057"
  Angle = 360
  Axis = (0,1,0)
  Base = (0,0,0)
  FaceMakerClass = Part::FaceMakerBullseye
  Placement = pos=(12.5,0,10) rot=(0,0,1;0rad)
  Solid = false
  Source = -> Face141
  Symmetric = false
FEATURE [Part::Feature] Face144
  shape: bbox 3.5 x 17.8 x 2e-07 mm, 1 faces, 0 solids (baked)
FEATURE [Part::Feature] Face145
  shape: bbox 3.5 x 17.8 x 2e-07 mm, 1 faces, 0 solids (baked)
FEATURE [Part::Feature] Face146
  shape: bbox 3.5 x 17.8 x 2e-07 mm, 1 faces, 0 solids (baked)
FEATURE [Part::Revolution] Revolve150  label="removeToCreateScrewAndThreadedInsertHole058"
  Angle = 360
  Axis = (0,1,0)
  Base = (0,0,0)
  FaceMakerClass = Part::FaceMakerBullseye
  Placement = pos=(12.5,0,62) rot=(0,0,1;0rad)
  Solid = false
  Source = -> Face146
  Symmetric = false
FEATURE [Part::Revolution] Revolve151  label="removeToCreateScrewAndThreadedInsertHole059"
  Angle = 360
  Axis = (0,1,0)
  Base = (0,0,0)
  FaceMakerClass = Part::FaceMakerBullseye
  Placement = pos=(89.5,0,68.5) rot=(0,0,1;0rad)
  Solid = false
  Source = -> Face143
  Symmetric = false
FEATURE [Part::Revolution] Revolve152  label="removeToCreateScrewAndThreadedInsertHole060"
  Angle = 360
  Axis = (0,1,0)
  Base = (0,0,0)
  FaceMakerClass = Part::FaceMakerBullseye
  Placement = pos=(89.5,0,3.5) rot=(0,0,1;0rad)
  Solid = false
  Source = -> Face142
  Symmetric = false
FEATURE [Part::Revolution] Revolve153  label="removeToCreateScrewAndThreadedInsertHole061"
  Angle = 360
  Axis = (0,1,0)
  Base = (0,0,0)
  FaceMakerClass = Part::FaceMakerBullseye
  Placement = pos=(109.5,4.7,3.5) rot=(0,0,1;0rad)
  Solid = false
  Source = -> Face145
  Symmetric = false
FEATURE [Part::Revolution] Revolve154  label="removeToCreateScrewAndThreadedInsertHole062"
  Angle = 360
  Axis = (0,1,0)
  Base = (0,0,0)
  FaceMakerClass = Part::FaceMakerBullseye
  Placement = pos=(109.5,4.7,68.5) rot=(0,0,1;0rad)
  Solid = false
  Source = -> Face144
  Symmetric = false
FEATURE [Part::MultiFuse] Fusion115  label="removeToCreateScrewAndThreadedInsertHole056"
  Shapes = -> [Revolve154,Revolve153,Revolve152,Revolve151,Revolve150,Revolve149]
FEATURE [Part::Feature] Face147
  shape: bbox 9.8 x 26.5 x 2e-07 mm, 1 faces, 0 solids (baked)
FEATURE [Part::Revolution] Revolve155
  Angle = 360
  Axis = (0,1,0)
  Base = (0,0,0)
  FaceMakerClass = Part::FaceMakerBullseye
  Placement = pos=(0,0,0) rot=(0,0,1;1.5708rad)
  Solid = false
  Source = -> Face147
  Symmetric = false
FEATURE [Part::Feature] Face148
  shape: bbox 9.8 x 26.5 x 2e-07 mm, 1 faces, 0 solids (baked)
FEATURE [Part::Revolution] Revolve156
  Angle = 360
  Axis = (0,1,0)
  Base = (0,0,0)
  FaceMakerClass = Part::FaceMakerBullseye
  Placement = pos=(0,0,0) rot=(0,0,1;1.5708rad)
  Solid = false
  Source = -> Face148
  Symmetric = false
FEATURE [Part::MultiFuse] Fusion116
  Placement = pos=(-18,19,36) rot=(0,0,1;0rad)
  Shapes = -> [Revolve156,Revolve155]
FEATURE [Part::Box] Box029  label="Cube016"
  AttacherType = Attacher::AttachEngine3D
  Height = 28
  Length = 3
  Placement = pos=(110.7,19,22) rot=(0,0,1;0rad)
  Width = 15.7
FEATURE [Part::Cylinder] Cylinder046
  Angle = 360
  AttacherType = Attacher::AttachEngine3D
  Height = 10
  Placement = pos=(0,0,36.15) rot=(0,0,1;0rad)
  Radius = 4
FEATURE [Part::Cylinder] Cylinder047
  Angle = 360
  AttacherType = Attacher::AttachEngine3D
  Height = 20
  Placement = pos=(0,0,36.15) rot=(0,0,1;0rad)
  Radius = 10.3
FEATURE [Part::MultiFuse] Fusion117  label="removeToCreteHoleForPlugHousing041"
  Placement = pos=(70,19,36) rot=(0,1,0;1.5708rad)
  Shapes = -> [Cylinder047,Cylinder046]
FEATURE [Part::Cut] Cut049  label="plugHousingTab004"
  Base = -> Box029
  Placement = pos=(-107.4,-14,0) rot=(0,0,1;0rad)
  Tool = -> Fusion117
FEATURE [Part::Box] Box030  label="Cube017"
  AttacherType = Attacher::AttachEngine3D
  Height = 28
  Length = 3
  Placement = pos=(110.7,19,22) rot=(0,0,1;0rad)
  Width = 15.7
FEATURE [Part::Cylinder] Cylinder048
  Angle = 360
  AttacherType = Attacher::AttachEngine3D
  Height = 10
  Placement = pos=(0,0,36.15) rot=(0,0,1;0rad)
  Radius = 4
FEATURE [Part::Cylinder] Cylinder049
  Angle = 360
  AttacherType = Attacher::AttachEngine3D
  Height = 20
  Placement = pos=(0,0,36.15) rot=(0,0,1;0rad)
  Radius = 10.3
FEATURE [Part::MultiFuse] Fusion118  label="removeToCreteHoleForPlugHousing042"
  Placement = pos=(70,19,36) rot=(0,1,0;1.5708rad)
  Shapes = -> [Cylinder049,Cylinder048]
FEATURE [Part::Cut] Cut050  label="plugHousingTab005"
  Base = -> Box030
  Placement = pos=(-107.4,-14,0) rot=(0,0,1;0rad)
  Tool = -> Fusion118
FEATURE [Part::MultiFuse] Fusion119
  Placement = pos=(9.6,23,0) rot=(0,0,1;3.14159rad)
  Shapes = -> [Cut049,Cut050]
FEATURE [Part::Box] Box031  label="Cube018"
  AttacherType = Attacher::AttachEngine3D
  Height = 10
  Length = 3
  Placement = pos=(3.3,4,12) rot=(0,0,1;0rad)
  Width = 10
FEATURE [Part::Fillet] Fillet044
  Base = -> Box031
  Edges = 1 edges r=2: [Edge11]
FEATURE [Part::Box] Box032  label="Cube019"
  AttacherType = Attacher::AttachEngine3D
  Height = 10
  Length = 3
  Placement = pos=(3.3,4,50) rot=(0,0,1;0rad)
  Width = 10
FEATURE [Part::Fillet] Fillet045
  Base = -> Box032
  Edges = 1 edges r=2: [Edge12]
FEATURE [Part::Box] Box033  label="Cube020"
  AttacherType = Attacher::AttachEngine3D
  Height = 28
  Length = 4
  Placement = pos=(5,0,22) rot=(0,0,1;0rad)
  Width = 10
FEATURE [Part::Fillet] Fillet046
  Base = -> Box033
  Edges = 1 edges r=1: [Edge7]
FEATURE [Part::Fillet] Fillet047
  Base = -> Fillet046
  Edges = 1 edges r=2: [Edge5]
FEATURE [Part::Fillet] Fillet048
  Base = -> Fillet047
  Edges = 1 edges r=2: [Edge2]
FEATURE [Part::Cylinder] Cylinder050
  Angle = 360
  AttacherType = Attacher::AttachEngine3D
  Height = 20
  Placement = pos=(0,0,36.15) rot=(0,0,1;0rad)
  Radius = 8.2
FEATURE [Part::Cylinder] Cylinder051
  Angle = 360
  AttacherType = Attacher::AttachEngine3D
  Height = 10
  Placement = pos=(0,0,36.15) rot=(0,0,1;0rad)
  Radius = 4
FEATURE [Part::MultiFuse] Fusion120  label="removeToCreteHoleForPlugHousing043"
  Placement = pos=(-42,19,36) rot=(0,1,0;1.5708rad)
  Shapes = -> [Cylinder050,Cylinder051]
FEATURE [Sketcher::SketchObject] Sketch067  label="topSketch018"
  FullyConstrained = true
  sketch-geometry (4):
    g0: LineSegment StartX=16.8446 StartY=31.512 StartZ=0 EndX=16.3251 EndY=34.4666 EndZ=0
    g1: ArcOfCircle CenterX=19 CenterY=19.2524 CenterZ=0 NormalX=0 NormalY=0 NormalZ=1 AngleXU=0 Radius=15.4476 StartAngle=1.74483 EndAngle=2.72717
    g2: ArcOfCircle CenterX=19 CenterY=19.2524 CenterZ=0 NormalX=0 NormalY=0 NormalZ=1 AngleXU=0 Radius=12.4476 StartAngle=1.74483 EndAngle=2.73189
    g3: LineSegment StartX=4.86004 StartY=25.4725 StartZ=0 EndX=7.58253 EndY=24.2107 EndZ=0
  constraints (7):
    c: Block(g0)
    c: Coincident(g1,g0)
    c: Coincident(g2,g0)
    c: Coincident(g3,g1)
    c: Coincident(g3,g2)
    c: Block(g1)
    c: Block(g2)
FEATURE [Part::Extrusion] Extrude058
  Base = -> Sketch067
  Dir = (0,0,1)
  DirMode = 2
  FaceMakerClass = Part::FaceMakerBullseye
  LengthFwd = 10
  LengthRev = 0
  Placement = pos=(0,0,31) rot=(0,0,1;0rad)
  Solid = true
  Symmetric = false
FEATURE [Part::Cut] Cut051
  Base = -> Extrude058
  Tool = -> Fusion120
FEATURE [Part::Fillet] Fillet049
  Base = -> Cut051
  Edges = 1 edges r=2: [Edge1]
FEATURE [Part::Fillet] Fillet050
  Base = -> Fillet049
  Edges = 1 edges r=2.5: [Edge1]
FEATURE [Part::Fillet] Fillet051
  Base = -> Fillet050
  Edges = 1 edges r=2.5: [Edge2]
FEATURE [Part::MultiFuse] Fusion121  label="wireHolder003"
  Shapes = -> [Fusion116,Fillet051]
FEATURE [Part::MultiFuse] Fusion122
  Shapes = -> [Fillet045,Fusion121]
FEATURE [Part::MultiFuse] Fusion123  label="wireHolder004"
  Shapes = -> [Fusion122,Fillet048]
FEATURE [Part::MultiFuse] Fusion124  label="wireHolder005"
  Shapes = -> [Fillet044,Fusion119,Fusion123]
FEATURE [Sketcher::SketchObject] Sketch068  label="topSketch019"
  FullyConstrained = true
  sketch-geometry (6):
    g0: LineSegment StartX=19 StartY=38 StartZ=0 EndX=117 EndY=38 EndZ=0
    g1: ArcOfCircle CenterX=19 CenterY=19 CenterZ=0 NormalX=0 NormalY=0 NormalZ=1 AngleXU=0 Radius=19 StartAngle=1.5708 EndAngle=3.14159
    g2: LineSegment StartX=117 StartY=38 StartZ=0 EndX=117 EndY=19 EndZ=0
    g3: LineSegment StartX=98 StartY=1.0161e-12 StartZ=0 EndX=5.22862e-06 EndY=1.0161e-12 EndZ=0
    g4: LineSegment StartX=5.22862e-06 StartY=19 StartZ=0 EndX=5.22862e-06 EndY=1.0161e-12 EndZ=0
    g5: ArcOfCircle CenterX=98 CenterY=19 CenterZ=0 NormalX=0 NormalY=0 NormalZ=1 AngleXU=0 Radius=19 StartAngle=4.71239 EndAngle=6.28319
  constraints (16):
    c: Horizontal(g0)
    c: Distance(g0) = 98
    c: Coincident(g1,g0)
    c: Block(g1)
    c: Coincident(g2,g0)
    c: Vertical(g2)
    c: Distance(g2) = 19
    c: Horizontal(g3)
    c: Coincident(g4,g1)
    c: Vertical(g4)
    c: Coincident(g3,g4)
    c: Block(g3)
    c: Coincident(g5,g2)
    c: Coincident(g5,g3)
    c: Block(g0)
    c: Block(g5)
FEATURE [Part::Extrusion] Extrude059  label="sideA002"
  Base = -> Sketch068
  Dir = (0,0,1)
  DirMode = 2
  FaceMakerClass = Part::FaceMakerBullseye
  LengthFwd = 3
  LengthRev = 0
  Placement = pos=(0,0,-2.7) rot=(0,0,1;0rad)
  Solid = true
  Symmetric = false
FEATURE [Sketcher::SketchObject] Sketch069  label="topSketch020"
  FullyConstrained = true
  sketch-geometry (6):
    g0: LineSegment StartX=19 StartY=38 StartZ=0 EndX=117 EndY=38 EndZ=0
    g1: ArcOfCircle CenterX=19 CenterY=19 CenterZ=0 NormalX=0 NormalY=0 NormalZ=1 AngleXU=0 Radius=19 StartAngle=1.5708 EndAngle=3.14159
    g2: LineSegment StartX=117 StartY=38 StartZ=0 EndX=117 EndY=19 EndZ=0
    g3: LineSegment StartX=98 StartY=1.0161e-12 StartZ=0 EndX=5.22862e-06 EndY=1.0161e-12 EndZ=0
    g4: LineSegment StartX=5.22862e-06 StartY=19 StartZ=0 EndX=5.22862e-06 EndY=1.0161e-12 EndZ=0
    g5: ArcOfCircle CenterX=98 CenterY=19 CenterZ=0 NormalX=0 NormalY=0 NormalZ=1 AngleXU=0 Radius=19 StartAngle=4.71239 EndAngle=6.28319
  constraints (16):
    c: Horizontal(g0)
    c: Distance(g0) = 98
    c: Coincident(g1,g0)
    c: Block(g1)
    c: Coincident(g2,g0)
    c: Vertical(g2)
    c: Distance(g2) = 19
    c: Horizontal(g3)
    c: Coincident(g4,g1)
    c: Vertical(g4)
    c: Coincident(g3,g4)
    c: Block(g3)
    c: Coincident(g5,g2)
    c: Coincident(g5,g3)
    c: Block(g0)
    c: Block(g5)
FEATURE [Part::Extrusion] Extrude060  label="sideB002"
  Base = -> Sketch069
  Dir = (0,0,1)
  DirMode = 2
  FaceMakerClass = Part::FaceMakerBullseye
  LengthFwd = 3
  LengthRev = 0
  Placement = pos=(0,0,71.7) rot=(0,0,1;0rad)
  Solid = true
  Symmetric = false
FEATURE [Part::MultiFuse] Fusion127  label="removeFromBottom001"
  Placement = pos=(2,0,0) rot=(0,0,1;0rad)
  Shapes = -> [Extrude059,Extrude060]
FEATURE [Part::Cylinder] Cylinder052
  Angle = 360
  AttacherType = Attacher::AttachEngine3D
  Height = 20
  Placement = pos=(0,0,36.15) rot=(0,0,1;0rad)
  Radius = 14
FEATURE [Part::Cylinder] Cylinder053
  Angle = 360
  AttacherType = Attacher::AttachEngine3D
  Height = 10
  Placement = pos=(0,0,36.15) rot=(0,0,1;0rad)
  Radius = 4
FEATURE [Part::MultiFuse] Fusion128  label="removeToCreteHoleForPlugHousing044"
  Placement = pos=(70,19,36) rot=(0,1,0;1.5708rad)
  Shapes = -> [Cylinder052,Cylinder053]
FEATURE [Part::Cut] Cut052  label="bottom011"
  Base = -> Extrude043
  Tool = -> Fusion128
FEATURE [Part::Cut] Cut054  label="bottom012"
  Base = -> Cut052
  Tool = -> Fusion115
FEATURE [Sketcher::SketchObject] Sketch070
  FullyConstrained = true
  Placement = pos=(117,19,0) rot=(0.57735,0.57735,0.57735;2.0944rad)
  sketch-geometry (48):
    g0: LineSegment StartX=-49.19 StartY=69.25 StartZ=0 EndX=-49.19 EndY=66.25 EndZ=0
    g1: LineSegment StartX=-49.19 StartY=63.5 StartZ=0 EndX=-49.19 EndY=60.5 EndZ=0
    g2: LineSegment StartX=-49.19 StartY=57.75 StartZ=0 EndX=-49.19 EndY=54.75 EndZ=0
    g3: LineSegment StartX=-49.19 StartY=52 StartZ=0 EndX=-49.19 EndY=49 EndZ=0
    g4: LineSegment StartX=-49.19 StartY=46.25 StartZ=0 EndX=-49.19 EndY=43.25 EndZ=0
    g5: LineSegment StartX=-49.19 StartY=40.5 StartZ=0 EndX=-49.19 EndY=37.5 EndZ=0
    g6: LineSegment StartX=-49.19 StartY=34.5 StartZ=0 EndX=-49.19 EndY=31.5 EndZ=0
    g7: LineSegment StartX=-49.19 StartY=28.75 StartZ=0 EndX=-49.19 EndY=25.75 EndZ=0
    g8: LineSegment StartX=-49.19 StartY=23 StartZ=0 EndX=-49.19 EndY=20 EndZ=0
    g9: LineSegment StartX=-49.19 StartY=17.25 StartZ=0 EndX=-49.19 EndY=14.25 EndZ=0
    g10: LineSegment StartX=-49.19 StartY=11.5 StartZ=0 EndX=-49.19 EndY=8.5 EndZ=0
    g11: LineSegment StartX=-49.19 StartY=5.75 StartZ=0 EndX=-49.19 EndY=2.75 EndZ=0
    g12: ArcOfCircle CenterX=-1.5 CenterY=67.75 CenterZ=0 NormalX=0 NormalY=0 NormalZ=1 AngleXU=0 Radius=1.5 StartAngle=4.71239 EndAngle=7.85398
    g13: ArcOfCircle CenterX=-1.5 CenterY=62 CenterZ=0 NormalX=0 NormalY=0 NormalZ=1 AngleXU=0 Radius=1.5 StartAngle=4.71239 EndAngle=7.85398
    g14: ArcOfCircle CenterX=-1.5 CenterY=56.25 CenterZ=0 NormalX=0 NormalY=0 NormalZ=1 AngleXU=0 Radius=1.5 StartAngle=4.71239 EndAngle=7.85398
    g15: ArcOfCircle CenterX=-11.49 CenterY=50.5 CenterZ=0 NormalX=0 NormalY=0 NormalZ=1 AngleXU=0 Radius=1.5 StartAngle=4.71239 EndAngle=7.85398
    g16: ArcOfCircle CenterX=-16.28 CenterY=44.75 CenterZ=0 NormalX=0 NormalY=0 NormalZ=1 AngleXU=0 Radius=1.5 StartAngle=4.71239 EndAngle=7.85398
    g17: ArcOfCircle CenterX=-18.2337 CenterY=39 CenterZ=0 NormalX=0 NormalY=0 NormalZ=1 AngleXU=0 Radius=1.5 StartAngle=4.71485 EndAngle=7.85398
    g18: ArcOfCircle CenterX=-16.2837 CenterY=27.25 CenterZ=0 NormalX=0 NormalY=0 NormalZ=1 AngleXU=0 Radius=1.5 StartAngle=4.71485 EndAngle=7.85398
    g19: ArcOfCircle CenterX=-18.2337 CenterY=33 CenterZ=0 NormalX=0 NormalY=0 NormalZ=1 AngleXU=0 Radius=1.5 StartAngle=4.71485 EndAngle=7.85398
    g20: ArcOfCircle CenterX=-11.49 CenterY=21.5 CenterZ=0 NormalX=0 NormalY=0 NormalZ=1 AngleXU=0 Radius=1.5 StartAngle=4.71239 EndAngle=7.85398
    g21: ArcOfCircle CenterX=-1.5 CenterY=4.25 CenterZ=0 NormalX=0 NormalY=0 NormalZ=1 AngleXU=0 Radius=1.5 StartAngle=4.71239 EndAngle=7.85398
    g22: ArcOfCircle CenterX=-1.5 CenterY=10 CenterZ=0 NormalX=0 NormalY=0 NormalZ=1 AngleXU=0 Radius=1.5 StartAngle=4.71239 EndAngle=7.85398
    g23: ArcOfCircle CenterX=-1.5 CenterY=15.75 CenterZ=0 NormalX=0 NormalY=0 NormalZ=1 AngleXU=0 Radius=1.5 StartAngle=4.71239 EndAngle=7.85398
    g24: LineSegment StartX=-49.19 StartY=69.25 StartZ=0 EndX=-1.5 EndY=69.25 EndZ=0
    g25: LineSegment StartX=-49.19 StartY=66.25 StartZ=0 EndX=-1.5 EndY=66.25 EndZ=0
    g26: LineSegment StartX=-49.19 StartY=63.5 StartZ=0 EndX=-1.5 EndY=63.5 EndZ=0
    g27: LineSegment StartX=-49.19 StartY=60.5 StartZ=0 EndX=-1.5 EndY=60.5 EndZ=0
    g28: LineSegment StartX=-49.19 StartY=57.75 StartZ=0 EndX=-1.5 EndY=57.75 EndZ=0
    g29: LineSegment StartX=-49.19 StartY=54.75 StartZ=0 EndX=-1.5 EndY=54.75 EndZ=0
    g30: LineSegment StartX=-49.19 StartY=52 StartZ=0 EndX=-11.49 EndY=52 EndZ=0
    g31: LineSegment StartX=-49.19 StartY=49 StartZ=0 EndX=-11.49 EndY=49 EndZ=0
    g32: LineSegment StartX=-49.19 StartY=46.25 StartZ=0 EndX=-16.28 EndY=46.25 EndZ=0
    g33: LineSegment StartX=-49.19 StartY=43.25 StartZ=0 EndX=-16.28 EndY=43.25 EndZ=0
    g34: LineSegment StartX=-49.19 StartY=40.5 StartZ=0 EndX=-18.2337 EndY=40.5 EndZ=0
    g35: LineSegment StartX=-49.19 StartY=37.5 StartZ=0 EndX=-18.23 EndY=37.5 EndZ=0
    g36: LineSegment StartX=-49.19 StartY=34.5 StartZ=0 EndX=-18.2337 EndY=34.5 EndZ=0
    g37: LineSegment StartX=-49.19 StartY=31.5 StartZ=0 EndX=-18.23 EndY=31.5 EndZ=0
    g38: LineSegment StartX=-49.19 StartY=28.75 StartZ=0 EndX=-16.2837 EndY=28.75 EndZ=0
    g39: LineSegment StartX=-49.19 StartY=25.75 StartZ=0 EndX=-16.28 EndY=25.75 EndZ=0
    g40: LineSegment StartX=-49.19 StartY=23 StartZ=0 EndX=-11.49 EndY=23 EndZ=0
    g41: LineSegment StartX=-49.19 StartY=20 StartZ=0 EndX=-11.49 EndY=20 EndZ=0
    g42: LineSegment StartX=-49.19 StartY=17.25 StartZ=0 EndX=-1.5 EndY=17.25 EndZ=0
    g43: LineSegment StartX=-49.19 StartY=14.25 StartZ=0 EndX=-1.5 EndY=14.25 EndZ=0
    g44: LineSegment StartX=-49.19 StartY=11.5 StartZ=0 EndX=-1.5 EndY=11.5 EndZ=0
    g45: LineSegment StartX=-49.19 StartY=8.5 StartZ=0 EndX=-1.5 EndY=8.5 EndZ=0
    g46: LineSegment StartX=-49.19 StartY=5.75 StartZ=0 EndX=-1.5 EndY=5.75 EndZ=0
    g47: LineSegment StartX=-49.19 StartY=2.75 StartZ=0 EndX=-1.5 EndY=2.75 EndZ=0
  constraints (120):
    c: Vertical(g0)
    c: Distance(g0) = 3
    c: Block(g0)
    c: Vertical(g1)
    c: Distance(g1) = 3
    c: Vertical(g2)
    c: Equal(g0,g2) = 3
    c: Block(g2)
    c: Vertical(g3)
    c: Equal(g1,g3) = 3
    c: Vertical(g4)
    c: Equal(g0,g4) = 3
    c: Block(g4)
    c: Vertical(g5)
    c: Equal(g1,g5) = 3
    c: Vertical(g6)
    c: Equal(g0,g6) = 3
    c: Block(g6)
    c: Vertical(g7)
    c: Equal(g1,g7) = 3
    c: Vertical(g8)
    c: Equal(g0,g8) = 3
    c: Block(g8)
    c: Vertical(g9)
    c: Equal(g1,g9) = 3
    c: Vertical(g10)
    c: Equal(g0,g10) = 3
    c: Block(g10)
    c: Vertical(g11)
    c: Equal(g1,g11) = 3
    c: Block(g12)
    c: Block(g13)
    c: Block(g14)
    c: Block(g15)
    c: Block(g16)
    c: Block(g17)
    c: Block(g18)
    c: Block(g19)
    c: Block(g20)
    c: Block(g21)
    c: Block(g22)
    c: Block(g23)
    c: Block(g11)
    c: Block(g9)
    c: Block(g7)
    c: Block(g5)
    c: Block(g3)
    c: Block(g1)
    c: Coincident(g24,g0)
    c: Coincident(g24,g12)
    c: Horizontal(g24)
    c: Coincident(g25,g0)
    c: Coincident(g25,g12)
    c: Horizontal(g25)
    c: Coincident(g26,g1)
    c: Coincident(g26,g13)
    c: Horizontal(g26)
    c: Coincident(g27,g1)
    c: Coincident(g27,g13)
    c: Horizontal(g27)
    c: Coincident(g28,g2)
    c: Coincident(g28,g14)
    c: Horizontal(g28)
    c: Coincident(g29,g2)
    c: Coincident(g29,g14)
    c: Horizontal(g29)
    c: Coincident(g30,g3)
    c: Coincident(g30,g15)
    c: Horizontal(g30)
    c: Coincident(g31,g3)
    c: Coincident(g31,g15)
    c: Horizontal(g31)
    c: Coincident(g32,g4)
    c: Coincident(g32,g16)
    c: Horizontal(g32)
    c: Coincident(g33,g4)
    c: Coincident(g33,g16)
    c: Horizontal(g33)
    c: Coincident(g34,g5)
    c: Coincident(g34,g17)
    c: Horizontal(g34)
    c: Coincident(g35,g5)
    c: Coincident(g35,g17)
    c: Horizontal(g35)
    c: Coincident(g36,g6)
    c: Coincident(g36,g19)
    c: Horizontal(g36)
    c: Coincident(g37,g6)
    c: Coincident(g37,g19)
    c: Horizontal(g37)
    c: Coincident(g38,g7)
    c: Coincident(g38,g18)
    c: Horizontal(g38)
    c: Coincident(g39,g7)
    c: Coincident(g39,g18)
    c: Horizontal(g39)
    c: Coincident(g40,g8)
    c: Coincident(g40,g20)
    c: Horizontal(g40)
    c: Coincident(g41,g8)
    c: Coincident(g41,g20)
    c: Horizontal(g41)
    c: Coincident(g42,g9)
    c: Coincident(g42,g23)
    c: Horizontal(g42)
    c: Coincident(g43,g9)
    c: Coincident(g43,g23)
    c: Horizontal(g43)
    c: Coincident(g44,g10)
    c: Coincident(g44,g22)
    c: Horizontal(g44)
    c: Coincident(g45,g10)
    c: Coincident(g45,g22)
    c: Horizontal(g45)
    c: Coincident(g46,g11)
    c: Coincident(g46,g21)
    c: Horizontal(g46)
    c: Coincident(g47,g11)
    c: Coincident(g47,g21)
    c: Horizontal(g47)
FEATURE [Part::Extrusion] Extrude061
  Base = -> Sketch070
  Dir = (1,0,0)
  DirMode = 2
  FaceMakerClass = Part::FaceMakerBullseye
  LengthFwd = 23
  LengthRev = 0
  Placement = pos=(-19,0,0) rot=(0,0,1;0rad)
  Solid = true
  Symmetric = false
FEATURE [Part::Fillet] Fillet052  label="removeToCreateVentalationHoles002"
  Base = -> Extrude061
  Edges = <same value as first occurrence — deduplicated (x6 in doc)>
  Placement = pos=(7,0.02,0) rot=(0,0,1;0rad)
FEATURE [Part::MultiFuse] Fusion130  label="bottom013"
  Shapes = -> [Cut054,Cut034]
FEATURE [Part::Cut] Cut055
  Base = -> Fusion130
  Tool = -> Fillet052
FEATURE [Part::Cylinder] Cylinder054
  Angle = 360
  AttacherType = Attacher::AttachEngine3D
  Height = 20
  Placement = pos=(0,0,36.15) rot=(0,0,1;0rad)
  Radius = 4
FEATURE [Sketcher::SketchObject] Sketch071  label="bottomSketch002"
  FullyConstrained = true
  sketch-geometry (32):
    g0: LineSegment StartX=3.3 StartY=-6.03275e-07 StartZ=0 EndX=98 EndY=-6.03275e-07 EndZ=0
    g1: ArcOfCircle CenterX=98 CenterY=19 CenterZ=0 NormalX=0 NormalY=0 NormalZ=1 AngleXU=0 Radius=19 StartAngle=4.71239 EndAngle=5.71103
    g2: LineSegment StartX=6.3 StartY=8 StartZ=0 EndX=3.3 EndY=8 EndZ=0
    g3: LineSegment StartX=3.3 StartY=8 StartZ=0 EndX=3.3 EndY=-6.03275e-07 EndZ=0
    g4: ArcOfCircle CenterX=8.3 CenterY=5 CenterZ=0 NormalX=0 NormalY=0 NormalZ=1 AngleXU=0 Radius=2 StartAngle=3.14159 EndAngle=4.71239
    g5: LineSegment StartX=6.3 StartY=8 StartZ=0 EndX=6.3 EndY=5 EndZ=0
    g6: ArcOfCircle CenterX=98 CenterY=19 CenterZ=0 NormalX=0 NormalY=0 NormalZ=1 AngleXU=0 Radius=12.7 StartAngle=4.71239 EndAngle=6.28319
    g7: LineSegment StartX=94.7 StartY=3 StartZ=0 EndX=8.3 EndY=3 EndZ=0
    g8-g12: Circle x5 (B-spline internal-alignment scaffolding for g13; pole/knot coordinates omitted)
    g13: BSplineCurve PolesCount=5 KnotsCount=3 Degree=3 IsPeriodic=0
    g14: GeomPoint X=98 Y=6.3 Z=0
    g15: GeomPoint X=96.3938 Y=4.71946 Z=0
    g16: GeomPoint X=94.7 Y=3 Z=0
    g17-g23: Circle x7 (B-spline internal-alignment scaffolding for g24; pole/knot coordinates omitted)
    g24: BSplineCurve PolesCount=7 KnotsCount=5 Degree=3 IsPeriodic=0
    g25-g29: GeomPoint x5 (B-spline internal-alignment scaffolding for g24; pole/knot coordinates omitted)
    g30: ArcOfCircle CenterX=98 CenterY=19 CenterZ=0 NormalX=0 NormalY=0 NormalZ=1 AngleXU=0 Radius=15.7 StartAngle=5.81226 EndAngle=6.28319
    g31: LineSegment StartX=110.7 StartY=19 StartZ=0 EndX=113.7 EndY=19 EndZ=0
  constraints (41):
    c: Horizontal(g0)
    c: Coincident(g1,g0)
    c: Block(g1)
    c: Horizontal(g2)
    c: Distance(g2) = 3
    c: Coincident(g3,g2)
    c: Vertical(g3)
    c: Coincident(g3,g0)
    c: Block(g4)
    c: Block(g2)
    c: Coincident(g5,g2)
    c: Coincident(g5,g4)
    c: Vertical(g5)
    c: Coincident(g6,g1)
    c: Block(g6)
    c: Coincident(g7,g4)
    c: Horizontal(g7)
    c: Block(g0)
    c: Block(g7)
    c: Block(g3)
    c: Coincident(g13,g6)
    c: Weight(g8) = 1
    c: Equal(g8, g9-g12) x4
    c: Coincident(g13,g7)
    c: InternalAlignment(g8-g12 -> g13) x5
    c: InternalAlignment(g14,g13)
    c: InternalAlignment(g15,g13)
    c: InternalAlignment(g16,g13)
    c: Block(g13)
    c: Weight(g17) = 1
    c: Equal(g17, g18-g23) x6
    c: Coincident(g24,g1)
    c: InternalAlignment(g17-g23 -> g24) x7
    c: InternalAlignment(g25-g29 -> g24) x5
    c: Block(g24)
    c: Coincident(g30,g24)
    c: Coincident(g31,g6)
    c: Coincident(g31,g30)
    c: Horizontal(g31)
    c: Block(g31)
    c: Block(g30)
FEATURE [Part::Extrusion] Extrude062  label="bottom014"
  Base = -> Sketch071
  Dir = (0,0,1)
  DirMode = 2
  FaceMakerClass = Part::FaceMakerBullseye
  LengthFwd = 71.4
  LengthRev = 0
  Placement = pos=(0,0,0.3) rot=(0,0,1;0rad)
  Solid = true
  Symmetric = false
FEATURE [Part::Fillet] Fillet054
  Base = -> Extrude062
  Edges = 1 edges r=2.4: [Edge17]
FEATURE [Part::Fillet] Fillet055  label="bottom015"
  Base = -> Fillet054
  Edges = 1 edges r=2.4: [Edge36]
FEATURE [Part::Cylinder] Cylinder055
  Angle = 360
  AttacherType = Attacher::AttachEngine3D
  Height = 10
  Placement = pos=(0,0,36.15) rot=(0,0,1;0rad)
  Radius = 4
FEATURE [Part::MultiFuse] Fusion131  label="removeToCreateHoleForPlugHousing002"
  Placement = pos=(70,19,36.15) rot=(0,1,0;1.5708rad)
  Shapes = -> [Cylinder054,Cylinder055]
FEATURE [Part::Cut] Cut056  label="Bottom001"
  Base = -> Fillet055
  Placement = pos=(9,0,0) rot=(0,0,1;0rad)
  Tool = -> Fusion131
FEATURE [Part::Cut] Cut057
  Base = -> Cut055
  Tool = -> Cut056
FEATURE [Sketcher::SketchObject] Sketch072  label="topSketch021"
  FullyConstrained = true
  sketch-geometry (4):
    g0: ArcOfCircle CenterX=105 CenterY=19 CenterZ=0 NormalX=0 NormalY=0 NormalZ=1 AngleXU=0 Radius=20.6155 StartAngle=5.54125 EndAngle=6.28319
    g1: ArcOfCircle CenterX=105 CenterY=19 CenterZ=0 NormalX=0 NormalY=0 NormalZ=1 AngleXU=0 Radius=13 StartAngle=5.54125 EndAngle=6.28319
    g2: LineSegment StartX=118 StartY=19 StartZ=0 EndX=125.616 EndY=19 EndZ=0
    g3: LineSegment StartX=114.583 StartY=10.2157 StartZ=0 EndX=120.197 EndY=5.06982 EndZ=0
  constraints (7):
    c: Block(g0)
    c: Block(g1)
    c: Coincident(g2,g1)
    c: Coincident(g2,g0)
    c: Horizontal(g2)
    c: Coincident(g3,g1)
    c: Coincident(g3,g0)
FEATURE [Part::Extrusion] Extrude063  label="bottomPlugHousingBit003"
  Base = -> Sketch072
  Dir = (0,0,1)
  DirMode = 2
  FaceMakerClass = Part::FaceMakerBullseye
  LengthFwd = 72
  LengthRev = 0
  Solid = true
  Symmetric = false
FEATURE [Part::Cylinder] Cylinder056
  Angle = 360
  AttacherType = Attacher::AttachEngine3D
  Height = 20
  Placement = pos=(0,0,36.15) rot=(0,0,1;0rad)
  Radius = 14.3
FEATURE [Part::Cylinder] Cylinder057
  Angle = 360
  AttacherType = Attacher::AttachEngine3D
  Height = 10
  Placement = pos=(0,0,36.15) rot=(0,0,1;0rad)
  Radius = 4
FEATURE [Part::Box] Box034  label="removeToCreteHoleForPlugHousing047"
  AttacherType = Attacher::AttachEngine3D
  Height = 28.6
  Length = 20
  Placement = pos=(106.15,0,21.7) rot=(0,0,1;0rad)
  Width = 19
FEATURE [Part::Cylinder] Cylinder058
  Angle = 360
  AttacherType = Attacher::AttachEngine3D
  Height = 20
  Placement = pos=(0,0,36.15) rot=(0,0,1;0rad)
  Radius = 14.3
FEATURE [Part::Cylinder] Cylinder059
  Angle = 360
  AttacherType = Attacher::AttachEngine3D
  Height = 10
  Placement = pos=(0,0,36.15) rot=(0,0,1;0rad)
  Radius = 4
FEATURE [Part::MultiFuse] Fusion134  label="removeToCreteHoleForPlugHousing046"
  Placement = pos=(70,19,36) rot=(0,1,0;1.5708rad)
  Shapes = -> [Cylinder058,Cylinder059]
FEATURE [Part::Cylinder] Cylinder060
  Angle = 360
  AttacherType = Attacher::AttachEngine3D
  Height = 20
  Placement = pos=(0,0,36.15) rot=(0,0,1;0rad)
  Radius = 14
FEATURE [Part::Cylinder] Cylinder061
  Angle = 360
  AttacherType = Attacher::AttachEngine3D
  Height = 10
  Placement = pos=(0,0,36.15) rot=(0,0,1;0rad)
  Radius = 4
FEATURE [Part::MultiFuse] Fusion135  label="removeToCreteHoleForPlugHousing048"
  Placement = pos=(70,19,36) rot=(0,1,0;1.5708rad)
  Shapes = -> [Cylinder060,Cylinder061]
FEATURE [Part::Box] Box035  label="removeToCreteHoleForPlugHousing049"
  AttacherType = Attacher::AttachEngine3D
  Height = 28.6
  Length = 20
  Placement = pos=(106.15,0,21.7) rot=(0,0,1;0rad)
  Width = 19
FEATURE [Part::MultiFuse] Fusion133  label="removeToCreteHoleForPlugHousing045"
  Placement = pos=(0,0,-28.3) rot=(0,0,1;0rad)
  Shapes = -> [Box035,Fusion134]
FEATURE [Part::MultiFuse] Fusion138  label="removeToCreteHoleForPlugHousing051"
  Placement = pos=(70,19,36) rot=(0,1,0;1.5708rad)
  Shapes = -> [Cylinder056,Cylinder057]
FEATURE [Part::MultiFuse] Fusion137  label="removeToCreteHoleForPlugHousing050"
  Placement = pos=(0,0,28.3) rot=(0,0,1;0rad)
  Shapes = -> [Box034,Fusion138]
FEATURE [Part::MultiFuse] Fusion132  label="removeToCreatePlugHousingBottomBit002"
  Shapes = -> [Fusion133,Fusion137]
FEATURE [Part::MultiFuse] Fusion136  label="removeToCreatePlugHousingBottomBit003"
  Shapes = -> [Fusion135,Fusion132]
FEATURE [Part::Cut] Cut058  label="bottomPlugHousingBit002"
  Base = -> Extrude063
  Placement = pos=(-0.09,0,0) rot=(0,0,1;0rad)
  Tool = -> Fusion136
FEATURE [Sketcher::SketchObject] Sketch073  label="bottomSketch003"
  FullyConstrained = true
  sketch-geometry (45):
    g0: LineSegment StartX=6.29999 StartY=8 StartZ=0 EndX=3.29999 EndY=8 EndZ=0
    g1: LineSegment StartX=3.29999 StartY=8 StartZ=0 EndX=3.29999 EndY=-6.03275e-07 EndZ=0
    g2: ArcOfCircle CenterX=8.29999 CenterY=5 CenterZ=0 NormalX=0 NormalY=0 NormalZ=1 AngleXU=0 Radius=2 StartAngle=3.14159 EndAngle=4.71239
    g3: LineSegment StartX=6.29999 StartY=8 StartZ=0 EndX=6.29999 EndY=5 EndZ=0
    g4: ArcOfCircle CenterX=105 CenterY=19 CenterZ=0 NormalX=0 NormalY=0 NormalZ=1 AngleXU=0 Radius=12.7 StartAngle=4.71239 EndAngle=5.94289
    g5-g11: Circle x7 (B-spline internal-alignment scaffolding for g12; pole/knot coordinates omitted)
    g12: BSplineCurve PolesCount=7 KnotsCount=5 Degree=3 IsPeriodic=0
    g13-g17: GeomPoint x5 (B-spline internal-alignment scaffolding for g12; pole/knot coordinates omitted)
    g18: ArcOfCircle CenterX=105 CenterY=19 CenterZ=0 NormalX=0 NormalY=0 NormalZ=1 AngleXU=0 Radius=15.7 StartAngle=5.81226 EndAngle=6.28319
    g19: BSplineCurve PolesCount=5 KnotsCount=3 Degree=3 IsPeriodic=0
    g20: LineSegment StartX=8.29999 StartY=3 StartZ=0 EndX=101.7 EndY=3 EndZ=0
    g21: LineSegment StartX=3.29999 StartY=-6.03275e-07 StartZ=0 EndX=105 EndY=-6.03275e-07 EndZ=0
    g22: LineSegment StartX=120.974 StartY=8.71251 StartZ=0 EndX=122.332 EndY=7.83778 EndZ=0
    g23: LineSegment StartX=105 StartY=-6.03274e-07 StartZ=0 EndX=113 EndY=-6.03274e-07 EndZ=0
    g24: ArcOfCircle CenterX=105 CenterY=19 CenterZ=0 NormalX=0 NormalY=0 NormalZ=1 AngleXU=0 Radius=20.6155 StartAngle=5.11091 EndAngle=5.71103
    g25: ArcOfCircle CenterX=117.7 CenterY=19 CenterZ=0 NormalX=0 NormalY=0 NormalZ=1 AngleXU=0 Radius=3 StartAngle=1.2e-15 EndAngle=2.10468
    g26: Circle CenterX=116.345 CenterY=16.3232 CenterZ=0 NormalX=0 NormalY=0 NormalZ=1 AngleXU=0 Radius=1
    g27: Circle CenterX=117.24 CenterY=15.7584 CenterZ=0 NormalX=0 NormalY=0 NormalZ=1 AngleXU=0 Radius=1
    g28: Circle CenterX=116.972 CenterY=14.7612 CenterZ=0 NormalX=0 NormalY=0 NormalZ=1 AngleXU=0 Radius=1
    g29: BSplineCurve PolesCount=3 KnotsCount=2 Degree=2 IsPeriodic=0
    g30: GeomPoint X=116.345 Y=16.3232 Z=0
    g31: GeomPoint X=116.972 Y=14.7612 Z=0
    g32: Circle CenterX=115.828 CenterY=17.157 CenterZ=0 NormalX=0 NormalY=0 NormalZ=1 AngleXU=0 Radius=1
    g33: Circle CenterX=115.841 CenterY=16.639 CenterZ=0 NormalX=0 NormalY=0 NormalZ=1 AngleXU=0 Radius=1
    g34: Circle CenterX=116.345 CenterY=16.3232 CenterZ=0 NormalX=0 NormalY=0 NormalZ=1 AngleXU=0 Radius=1
    g35: BSplineCurve PolesCount=3 KnotsCount=2 Degree=2 IsPeriodic=0
    g36: GeomPoint X=115.828 Y=17.157 Z=0
    g37: GeomPoint X=116.345 Y=16.3232 Z=0
    g38: LineSegment StartX=115.828 StartY=17.157 StartZ=0 EndX=115.828 EndY=20.8307 EndZ=0
    g39: Circle CenterX=115.828 CenterY=20.8307 CenterZ=0 NormalX=0 NormalY=0 NormalZ=1 AngleXU=0 Radius=1
    g40: Circle CenterX=115.831 CenterY=21.3396 CenterZ=0 NormalX=0 NormalY=0 NormalZ=1 AngleXU=0 Radius=1
    g41: Circle CenterX=116.173 CenterY=21.5825 CenterZ=0 NormalX=0 NormalY=0 NormalZ=1 AngleXU=0 Radius=1
    g42: BSplineCurve PolesCount=3 KnotsCount=2 Degree=2 IsPeriodic=0
    g43: GeomPoint X=115.828 Y=20.8307 Z=0
    g44: GeomPoint X=116.173 Y=21.5825 Z=0
  constraints (70):
    c: Horizontal(g0)
    c: Distance(g0) = 3
    c: Coincident(g1,g0)
    c: Vertical(g1)
    c: Block(g2)
    c: Block(g0)
    c: Coincident(g3,g0)
    c: Coincident(g3,g2)
    c: Vertical(g3)
    c: Block(g1)
    c: Block(g4)
    c: Coincident(g19,g4)
    c: Block(g19)
    c: Equal(g5, g6-g11) x6
    c: InternalAlignment(g5-g11 -> g12) x7
    c: InternalAlignment(g13-g17 -> g12) x5
    c: Block(g12)
    c: Coincident(g18,g12)
    c: Block(g18)
    c: Coincident(g20,g2)
    c: Coincident(g20,g19)
    c: Horizontal(g20)
    c: Distance(g20) = 93.4
    c: Coincident(g21,g1)
    c: Horizontal(g21)
    c: Distance(g21) = 101.7
    c: Horizontal(g23)
    c: Distance(g23) = 8
    c: Coincident(g24,g23)
    c: Block(g23)
    c: Coincident(g22,g24)
    c: Block(g24)
    c: Block(g22)
    c: Distance(g22) = 1.61553
    c: Coincident(g25,g18)
    c: Block(g25)
    c: Weight(g26) = 1
    c: Equal(g26,g27)
    c: Equal(g26,g28)
    c: Coincident(g29,g4)
    c: InternalAlignment(g26,g29)
    c: InternalAlignment(g27,g29)
    c: InternalAlignment(g28,g29)
    c: InternalAlignment(g30,g29)
    c: InternalAlignment(g31,g29)
    c: Block(g29)
    c: Weight(g32) = 1
    c: Equal(g32,g33)
    c: Equal(g32,g34)
    c: Coincident(g35,g29)
    c: InternalAlignment(g32,g35)
    c: InternalAlignment(g33,g35)
    c: InternalAlignment(g34,g35)
    c: InternalAlignment(g36,g35)
    c: InternalAlignment(g37,g35)
    c: Block(g35)
    c: Coincident(g38,g35)
    c: Vertical(g38)
    c: Block(g38)
    c: Coincident(g42,g38)
    c: Weight(g39) = 1
    c: Equal(g39,g40)
    c: Equal(g39,g41)
    c: Coincident(g42,g25)
    c: InternalAlignment(g39,g42)
    c: InternalAlignment(g40,g42)
    c: InternalAlignment(g41,g42)
    c: InternalAlignment(g43,g42)
    c: InternalAlignment(g44,g42)
    c: Block(g42)
FEATURE [Part::Extrusion] Extrude064  label="bottom016"
  Base = -> Sketch073
  Dir = (0,0,1)
  DirMode = 2
  FaceMakerClass = Part::FaceMakerBullseye
  LengthFwd = 71.4
  LengthRev = 0
  Placement = pos=(0,0,0.3) rot=(0,0,1;0rad)
  Solid = true
  Symmetric = false
FEATURE [Part::Revolution] Revolve157  label="removeToCreateScrewAndThreadedInsertHole063"
  Angle = 360
  Axis = (0,1,0)
  Base = (0,0,0)
  FaceMakerClass = Part::FaceMakerBullseye
  Placement = pos=(12.5,0,10) rot=(0,0,1;0rad)
  Solid = false
  Source = -> Face141
  Symmetric = false
FEATURE [Sketcher::SketchObject] Sketch074
  FullyConstrained = true
  Placement = pos=(117,19,0) rot=(0.57735,0.57735,0.57735;2.0944rad)
  sketch-geometry (48):
    g0: LineSegment StartX=-49.19 StartY=69.25 StartZ=0 EndX=-49.19 EndY=66.25 EndZ=0
    g1: LineSegment StartX=-49.19 StartY=63.5 StartZ=0 EndX=-49.19 EndY=60.5 EndZ=0
    g2: LineSegment StartX=-49.19 StartY=57.75 StartZ=0 EndX=-49.19 EndY=54.75 EndZ=0
    g3: LineSegment StartX=-49.19 StartY=52 StartZ=0 EndX=-49.19 EndY=49 EndZ=0
    g4: LineSegment StartX=-49.19 StartY=46.25 StartZ=0 EndX=-49.19 EndY=43.25 EndZ=0
    g5: LineSegment StartX=-49.19 StartY=40.5 StartZ=0 EndX=-49.19 EndY=37.5 EndZ=0
    g6: LineSegment StartX=-49.19 StartY=34.5 StartZ=0 EndX=-49.19 EndY=31.5 EndZ=0
    g7: LineSegment StartX=-49.19 StartY=28.75 StartZ=0 EndX=-49.19 EndY=25.75 EndZ=0
    g8: LineSegment StartX=-49.19 StartY=23 StartZ=0 EndX=-49.19 EndY=20 EndZ=0
    g9: LineSegment StartX=-49.19 StartY=17.25 StartZ=0 EndX=-49.19 EndY=14.25 EndZ=0
    g10: LineSegment StartX=-49.19 StartY=11.5 StartZ=0 EndX=-49.19 EndY=8.5 EndZ=0
    g11: LineSegment StartX=-49.19 StartY=5.75 StartZ=0 EndX=-49.19 EndY=2.75 EndZ=0
    g12: ArcOfCircle CenterX=-1.5 CenterY=67.75 CenterZ=0 NormalX=0 NormalY=0 NormalZ=1 AngleXU=0 Radius=1.5 StartAngle=4.71239 EndAngle=7.85398
    g13: ArcOfCircle CenterX=-1.5 CenterY=62 CenterZ=0 NormalX=0 NormalY=0 NormalZ=1 AngleXU=0 Radius=1.5 StartAngle=4.71239 EndAngle=7.85398
    g14: ArcOfCircle CenterX=-1.5 CenterY=56.25 CenterZ=0 NormalX=0 NormalY=0 NormalZ=1 AngleXU=0 Radius=1.5 StartAngle=4.71239 EndAngle=7.85398
    g15: ArcOfCircle CenterX=-11.49 CenterY=50.5 CenterZ=0 NormalX=0 NormalY=0 NormalZ=1 AngleXU=0 Radius=1.5 StartAngle=4.71239 EndAngle=7.85398
    g16: ArcOfCircle CenterX=-16.28 CenterY=44.75 CenterZ=0 NormalX=0 NormalY=0 NormalZ=1 AngleXU=0 Radius=1.5 StartAngle=4.71239 EndAngle=7.85398
    g17: ArcOfCircle CenterX=-18.2337 CenterY=39 CenterZ=0 NormalX=0 NormalY=0 NormalZ=1 AngleXU=0 Radius=1.5 StartAngle=4.71485 EndAngle=7.85398
    g18: ArcOfCircle CenterX=-16.2837 CenterY=27.25 CenterZ=0 NormalX=0 NormalY=0 NormalZ=1 AngleXU=0 Radius=1.5 StartAngle=4.71485 EndAngle=7.85398
    g19: ArcOfCircle CenterX=-18.2337 CenterY=33 CenterZ=0 NormalX=0 NormalY=0 NormalZ=1 AngleXU=0 Radius=1.5 StartAngle=4.71485 EndAngle=7.85398
    g20: ArcOfCircle CenterX=-11.49 CenterY=21.5 CenterZ=0 NormalX=0 NormalY=0 NormalZ=1 AngleXU=0 Radius=1.5 StartAngle=4.71239 EndAngle=7.85398
    g21: ArcOfCircle CenterX=-1.5 CenterY=4.25 CenterZ=0 NormalX=0 NormalY=0 NormalZ=1 AngleXU=0 Radius=1.5 StartAngle=4.71239 EndAngle=7.85398
    g22: ArcOfCircle CenterX=-1.5 CenterY=10 CenterZ=0 NormalX=0 NormalY=0 NormalZ=1 AngleXU=0 Radius=1.5 StartAngle=4.71239 EndAngle=7.85398
    g23: ArcOfCircle CenterX=-1.5 CenterY=15.75 CenterZ=0 NormalX=0 NormalY=0 NormalZ=1 AngleXU=0 Radius=1.5 StartAngle=4.71239 EndAngle=7.85398
    g24: LineSegment StartX=-49.19 StartY=69.25 StartZ=0 EndX=-1.5 EndY=69.25 EndZ=0
    g25: LineSegment StartX=-49.19 StartY=66.25 StartZ=0 EndX=-1.5 EndY=66.25 EndZ=0
    g26: LineSegment StartX=-49.19 StartY=63.5 StartZ=0 EndX=-1.5 EndY=63.5 EndZ=0
    g27: LineSegment StartX=-49.19 StartY=60.5 StartZ=0 EndX=-1.5 EndY=60.5 EndZ=0
    g28: LineSegment StartX=-49.19 StartY=57.75 StartZ=0 EndX=-1.5 EndY=57.75 EndZ=0
    g29: LineSegment StartX=-49.19 StartY=54.75 StartZ=0 EndX=-1.5 EndY=54.75 EndZ=0
    g30: LineSegment StartX=-49.19 StartY=52 StartZ=0 EndX=-11.49 EndY=52 EndZ=0
    g31: LineSegment StartX=-49.19 StartY=49 StartZ=0 EndX=-11.49 EndY=49 EndZ=0
    g32: LineSegment StartX=-49.19 StartY=46.25 StartZ=0 EndX=-16.28 EndY=46.25 EndZ=0
    g33: LineSegment StartX=-49.19 StartY=43.25 StartZ=0 EndX=-16.28 EndY=43.25 EndZ=0
    g34: LineSegment StartX=-49.19 StartY=40.5 StartZ=0 EndX=-18.2337 EndY=40.5 EndZ=0
    g35: LineSegment StartX=-49.19 StartY=37.5 StartZ=0 EndX=-18.23 EndY=37.5 EndZ=0
    g36: LineSegment StartX=-49.19 StartY=34.5 StartZ=0 EndX=-18.2337 EndY=34.5 EndZ=0
    g37: LineSegment StartX=-49.19 StartY=31.5 StartZ=0 EndX=-18.23 EndY=31.5 EndZ=0
    g38: LineSegment StartX=-49.19 StartY=28.75 StartZ=0 EndX=-16.2837 EndY=28.75 EndZ=0
    g39: LineSegment StartX=-49.19 StartY=25.75 StartZ=0 EndX=-16.28 EndY=25.75 EndZ=0
    g40: LineSegment StartX=-49.19 StartY=23 StartZ=0 EndX=-11.49 EndY=23 EndZ=0
    g41: LineSegment StartX=-49.19 StartY=20 StartZ=0 EndX=-11.49 EndY=20 EndZ=0
    g42: LineSegment StartX=-49.19 StartY=17.25 StartZ=0 EndX=-1.5 EndY=17.25 EndZ=0
    g43: LineSegment StartX=-49.19 StartY=14.25 StartZ=0 EndX=-1.5 EndY=14.25 EndZ=0
    g44: LineSegment StartX=-49.19 StartY=11.5 StartZ=0 EndX=-1.5 EndY=11.5 EndZ=0
    g45: LineSegment StartX=-49.19 StartY=8.5 StartZ=0 EndX=-1.5 EndY=8.5 EndZ=0
    g46: LineSegment StartX=-49.19 StartY=5.75 StartZ=0 EndX=-1.5 EndY=5.75 EndZ=0
    g47: LineSegment StartX=-49.19 StartY=2.75 StartZ=0 EndX=-1.5 EndY=2.75 EndZ=0
  constraints (120):
    c: Vertical(g0)
    c: Distance(g0) = 3
    c: Block(g0)
    c: Vertical(g1)
    c: Distance(g1) = 3
    c: Vertical(g2)
    c: Equal(g0,g2) = 3
    c: Block(g2)
    c: Vertical(g3)
    c: Equal(g1,g3) = 3
    c: Vertical(g4)
    c: Equal(g0,g4) = 3
    c: Block(g4)
    c: Vertical(g5)
    c: Equal(g1,g5) = 3
    c: Vertical(g6)
    c: Equal(g0,g6) = 3
    c: Block(g6)
    c: Vertical(g7)
    c: Equal(g1,g7) = 3
    c: Vertical(g8)
    c: Equal(g0,g8) = 3
    c: Block(g8)
    c: Vertical(g9)
    c: Equal(g1,g9) = 3
    c: Vertical(g10)
    c: Equal(g0,g10) = 3
    c: Block(g10)
    c: Vertical(g11)
    c: Equal(g1,g11) = 3
    c: Block(g12)
    c: Block(g13)
    c: Block(g14)
    c: Block(g15)
    c: Block(g16)
    c: Block(g17)
    c: Block(g18)
    c: Block(g19)
    c: Block(g20)
    c: Block(g21)
    c: Block(g22)
    c: Block(g23)
    c: Block(g11)
    c: Block(g9)
    c: Block(g7)
    c: Block(g5)
    c: Block(g3)
    c: Block(g1)
    c: Coincident(g24,g0)
    c: Coincident(g24,g12)
    c: Horizontal(g24)
    c: Coincident(g25,g0)
    c: Coincident(g25,g12)
    c: Horizontal(g25)
    c: Coincident(g26,g1)
    c: Coincident(g26,g13)
    c: Horizontal(g26)
    c: Coincident(g27,g1)
    c: Coincident(g27,g13)
    c: Horizontal(g27)
    c: Coincident(g28,g2)
    c: Coincident(g28,g14)
    c: Horizontal(g28)
    c: Coincident(g29,g2)
    c: Coincident(g29,g14)
    c: Horizontal(g29)
    c: Coincident(g30,g3)
    c: Coincident(g30,g15)
    c: Horizontal(g30)
    c: Coincident(g31,g3)
    c: Coincident(g31,g15)
    c: Horizontal(g31)
    c: Coincident(g32,g4)
    c: Coincident(g32,g16)
    c: Horizontal(g32)
    c: Coincident(g33,g4)
    c: Coincident(g33,g16)
    c: Horizontal(g33)
    c: Coincident(g34,g5)
    c: Coincident(g34,g17)
    c: Horizontal(g34)
    c: Coincident(g35,g5)
    c: Coincident(g35,g17)
    c: Horizontal(g35)
    c: Coincident(g36,g6)
    c: Coincident(g36,g19)
    c: Horizontal(g36)
    c: Coincident(g37,g6)
    c: Coincident(g37,g19)
    c: Horizontal(g37)
    c: Coincident(g38,g7)
    c: Coincident(g38,g18)
    c: Horizontal(g38)
    c: Coincident(g39,g7)
    c: Coincident(g39,g18)
    c: Horizontal(g39)
    c: Coincident(g40,g8)
    c: Coincident(g40,g20)
    c: Horizontal(g40)
    c: Coincident(g41,g8)
    c: Coincident(g41,g20)
    c: Horizontal(g41)
    c: Coincident(g42,g9)
    c: Coincident(g42,g23)
    c: Horizontal(g42)
    c: Coincident(g43,g9)
    c: Coincident(g43,g23)
    c: Horizontal(g43)
    c: Coincident(g44,g10)
    c: Coincident(g44,g22)
    c: Horizontal(g44)
    c: Coincident(g45,g10)
    c: Coincident(g45,g22)
    c: Horizontal(g45)
    c: Coincident(g46,g11)
    c: Coincident(g46,g21)
    c: Horizontal(g46)
    c: Coincident(g47,g11)
    c: Coincident(g47,g21)
    c: Horizontal(g47)
FEATURE [Part::Extrusion] Extrude065
  Base = -> Sketch074
  Dir = (1,0,0)
  DirMode = 2
  FaceMakerClass = Part::FaceMakerBullseye
  LengthFwd = 23
  LengthRev = 0
  Placement = pos=(-19,0,0) rot=(0,0,1;0rad)
  Solid = true
  Symmetric = false
FEATURE [Part::Fillet] Fillet056  label="removeToCreateVentalationHoles003"
  Base = -> Extrude065
  Edges = <same value as first occurrence — deduplicated (x6 in doc)>
  Placement = pos=(7,0.02,0) rot=(0,0,1;0rad)
FEATURE [Part::Revolution] Revolve158  label="removeToCreateScrewAndThreadedInsertHole065"
  Angle = 360
  Axis = (0,1,0)
  Base = (0,0,0)
  FaceMakerClass = Part::FaceMakerBullseye
  Placement = pos=(12.5,0,62) rot=(0,0,1;0rad)
  Solid = false
  Source = -> Face146
  Symmetric = false
FEATURE [Part::Revolution] Revolve159  label="removeToCreateScrewAndThreadedInsertHole066"
  Angle = 360
  Axis = (0,1,0)
  Base = (0,0,0)
  FaceMakerClass = Part::FaceMakerBullseye
  Placement = pos=(89.5,0,68.5) rot=(0,0,1;0rad)
  Solid = false
  Source = -> Face143
  Symmetric = false
FEATURE [Part::Revolution] Revolve160  label="removeToCreateScrewAndThreadedInsertHole067"
  Angle = 360
  Axis = (0,1,0)
  Base = (0,0,0)
  FaceMakerClass = Part::FaceMakerBullseye
  Placement = pos=(89.5,0,3.5) rot=(0,0,1;0rad)
  Solid = false
  Source = -> Face142
  Symmetric = false
FEATURE [Part::Revolution] Revolve161  label="removeToCreateScrewAndThreadedInsertHole068"
  Angle = 360
  Axis = (0,1,0)
  Base = (0,0,0)
  FaceMakerClass = Part::FaceMakerBullseye
  Placement = pos=(109.5,4.7,3.5) rot=(0,0,1;0rad)
  Solid = false
  Source = -> Face145
  Symmetric = false
FEATURE [Part::Revolution] Revolve162  label="removeToCreateScrewAndThreadedInsertHole069"
  Angle = 360
  Axis = (0,1,0)
  Base = (0,0,0)
  FaceMakerClass = Part::FaceMakerBullseye
  Placement = pos=(109.5,4.7,68.5) rot=(0,0,1;0rad)
  Solid = false
  Source = -> Face144
  Symmetric = false
FEATURE [Part::MultiFuse] Fusion141  label="removeToCreateScrewAndThreadedInsertHole064"
  Shapes = -> [Revolve162,Revolve161,Revolve160,Revolve159,Revolve158,Revolve157]
FEATURE [Part::Cylinder] Cylinder062
  Angle = 360
  AttacherType = Attacher::AttachEngine3D
  Height = 20
  Placement = pos=(0,0,36.15) rot=(0,0,1;0rad)
  Radius = 14
FEATURE [Part::Cylinder] Cylinder063
  Angle = 360
  AttacherType = Attacher::AttachEngine3D
  Height = 10
  Placement = pos=(0,0,36.15) rot=(0,0,1;0rad)
  Radius = 4
FEATURE [Part::MultiFuse] Fusion139  label="removeToCreteHoleForPlugHousing052"
  Placement = pos=(70,19,36) rot=(0,1,0;1.5708rad)
  Shapes = -> [Cylinder062,Cylinder063]
FEATURE [Part::Cut] Cut060  label="bottom017"
  Base = -> Extrude064
  Tool = -> Fusion139
FEATURE [Part::Cut] Cut061  label="bottom019"
  Base = -> Cut060
  Tool = -> Fusion141
FEATURE [Part::MultiFuse] Fusion140  label="bottom018"
  Shapes = -> [Cut061,Cut058]
FEATURE [Part::Cut] Cut059  label="bottom020"
  Base = -> Fusion140
  Tool = -> Fillet056
FEATURE [Part::Box] Box036  label="Cube021"
  AttacherType = Attacher::AttachEngine3D
  Height = 80
  Length = 26
  Placement = pos=(0,-1,-5) rot=(0,0,1;0rad)
  Width = 11
FEATURE [Part::Cut] Cut062  label="removeFromBottom002"
  Base = -> Cut057
  Tool = -> Box036
FEATURE [Part::Cut] Cut063
  Base = -> Cut059
  Tool = -> Cut062
FEATURE [Part::Cut] Cut064  label="pcbStands"
  Base = -> Fusion095
  Tool = -> Fusion127
FEATURE [Sketcher::SketchObject] Sketch075  label="topSketch022"
  FullyConstrained = true
  sketch-geometry (6):
    g0: LineSegment StartX=19 StartY=38 StartZ=0 EndX=117 EndY=38 EndZ=0
    g1: ArcOfCircle CenterX=19 CenterY=19 CenterZ=0 NormalX=0 NormalY=0 NormalZ=1 AngleXU=0 Radius=19 StartAngle=1.5708 EndAngle=3.14159
    g2: LineSegment StartX=117 StartY=38 StartZ=0 EndX=117 EndY=19 EndZ=0
    g3: LineSegment StartX=98 StartY=1.0161e-12 StartZ=0 EndX=5.22862e-06 EndY=1.0161e-12 EndZ=0
    g4: LineSegment StartX=5.22862e-06 StartY=19 StartZ=0 EndX=5.22862e-06 EndY=1.0161e-12 EndZ=0
    g5: ArcOfCircle CenterX=98 CenterY=19 CenterZ=0 NormalX=0 NormalY=0 NormalZ=1 AngleXU=0 Radius=19 StartAngle=4.71239 EndAngle=6.28319
  constraints (16):
    c: Horizontal(g0)
    c: Distance(g0) = 98
    c: Coincident(g1,g0)
    c: Block(g1)
    c: Coincident(g2,g0)
    c: Vertical(g2)
    c: Distance(g2) = 19
    c: Horizontal(g3)
    c: Coincident(g4,g1)
    c: Vertical(g4)
    c: Coincident(g3,g4)
    c: Block(g3)
    c: Coincident(g5,g2)
    c: Coincident(g5,g3)
    c: Block(g0)
    c: Block(g5)
FEATURE [Part::Extrusion] Extrude067  label="sideB003"
  Base = -> Sketch075
  Dir = (0,0,1)
  DirMode = 2
  FaceMakerClass = Part::FaceMakerBullseye
  LengthFwd = 3
  LengthRev = 0
  Placement = pos=(0,0,71.7) rot=(0,0,1;0rad)
  Solid = true
  Symmetric = false
FEATURE [Sketcher::SketchObject] Sketch076  label="topSketch023"
  FullyConstrained = true
  sketch-geometry (6):
    g0: LineSegment StartX=19 StartY=38 StartZ=0 EndX=117 EndY=38 EndZ=0
    g1: ArcOfCircle CenterX=19 CenterY=19 CenterZ=0 NormalX=0 NormalY=0 NormalZ=1 AngleXU=0 Radius=19 StartAngle=1.5708 EndAngle=3.14159
    g2: LineSegment StartX=117 StartY=38 StartZ=0 EndX=117 EndY=19 EndZ=0
    g3: LineSegment StartX=98 StartY=1.0161e-12 StartZ=0 EndX=5.22862e-06 EndY=1.0161e-12 EndZ=0
    g4: LineSegment StartX=5.22862e-06 StartY=19 StartZ=0 EndX=5.22862e-06 EndY=1.0161e-12 EndZ=0
    g5: ArcOfCircle CenterX=98 CenterY=19 CenterZ=0 NormalX=0 NormalY=0 NormalZ=1 AngleXU=0 Radius=19 StartAngle=4.71239 EndAngle=6.28319
  constraints (16):
    c: Horizontal(g0)
    c: Distance(g0) = 98
    c: Coincident(g1,g0)
    c: Block(g1)
    c: Coincident(g2,g0)
    c: Vertical(g2)
    c: Distance(g2) = 19
    c: Horizontal(g3)
    c: Coincident(g4,g1)
    c: Vertical(g4)
    c: Coincident(g3,g4)
    c: Block(g3)
    c: Coincident(g5,g2)
    c: Coincident(g5,g3)
    c: Block(g0)
    c: Block(g5)
FEATURE [Part::Extrusion] Extrude066  label="sideA003"
  Base = -> Sketch076
  Dir = (0,0,1)
  DirMode = 2
  FaceMakerClass = Part::FaceMakerBullseye
  LengthFwd = 3
  LengthRev = 0
  Placement = pos=(0,0,-2.7) rot=(0,0,1;0rad)
  Solid = true
  Symmetric = false
FEATURE [Part::MultiFuse] Fusion142  label="removeFromBottom003"
  Placement = pos=(2,0,0) rot=(0,0,1;0rad)
  Shapes = -> [Extrude066,Extrude067]
FEATURE [Part::Cut] Cut065  label="screwRetainers002"
  Base = -> Fusion096
  Tool = -> Fusion142
FEATURE [Sketcher::SketchObject] Sketch077
  FullyConstrained = true
  Placement = pos=(117,19,0) rot=(0.57735,0.57735,0.57735;2.0944rad)
  sketch-geometry (8):
    g0: LineSegment StartX=-49.19 StartY=63.5 StartZ=0 EndX=-49.19 EndY=60.5 EndZ=0
    g1: LineSegment StartX=-49.19 StartY=11.5 StartZ=0 EndX=-49.19 EndY=8.5 EndZ=0
    g2: ArcOfCircle CenterX=-1.5 CenterY=62 CenterZ=0 NormalX=0 NormalY=0 NormalZ=1 AngleXU=0 Radius=1.5 StartAngle=4.71239 EndAngle=7.85398
    g3: ArcOfCircle CenterX=-1.5 CenterY=10 CenterZ=0 NormalX=0 NormalY=0 NormalZ=1 AngleXU=0 Radius=1.5 StartAngle=4.71239 EndAngle=7.85398
    g4: LineSegment StartX=-49.19 StartY=63.5 StartZ=0 EndX=-1.5 EndY=63.5 EndZ=0
    g5: LineSegment StartX=-49.19 StartY=60.5 StartZ=0 EndX=-1.5 EndY=60.5 EndZ=0
    g6: LineSegment StartX=-49.19 StartY=11.5 StartZ=0 EndX=-1.5 EndY=11.5 EndZ=0
    g7: LineSegment StartX=-49.19 StartY=8.5 StartZ=0 EndX=-1.5 EndY=8.5 EndZ=0
  constraints (19):
    c: Vertical(g0)
    c: Distance(g0) = 3
    c: Vertical(g1)
    c: Block(g1)
    c: Block(g2)
    c: Block(g3)
    c: Block(g0)
    c: Coincident(g4,g0)
    c: Coincident(g4,g2)
    c: Horizontal(g4)
    c: Coincident(g5,g0)
    c: Coincident(g5,g2)
    c: Horizontal(g5)
    c: Coincident(g6,g1)
    c: Coincident(g6,g3)
    c: Horizontal(g6)
    c: Coincident(g7,g1)
    c: Coincident(g7,g3)
    c: Horizontal(g7)
FEATURE [Part::Extrusion] Extrude068
  Base = -> Sketch077
  Dir = (1,0,0)
  DirMode = 2
  FaceMakerClass = Part::FaceMakerBullseye
  LengthFwd = 10
  LengthRev = 0
  Solid = true
  Symmetric = false
FEATURE [Part::Fillet] Fillet057  label="removeFromtMoreFrontCaseScrewRetainers002"
  Base = -> Extrude068
  Edges = 4 edges r=1.49: [Edge6,Edge11,Edge18,Edge23]
  Placement = pos=(-12,0,0) rot=(0,0,1;0rad)
FEATURE [Sketcher::SketchObject] Sketch078
  FullyConstrained = true
  Placement = pos=(117,19,0) rot=(0.57735,0.57735,0.57735;2.0944rad)
  sketch-geometry (8):
    g0: LineSegment StartX=-49.19 StartY=69.25 StartZ=0 EndX=-49.19 EndY=66.25 EndZ=0
    g1: LineSegment StartX=-49.19 StartY=5.75 StartZ=0 EndX=-49.19 EndY=2.75 EndZ=0
    g2: ArcOfCircle CenterX=-1.5 CenterY=67.75 CenterZ=0 NormalX=0 NormalY=0 NormalZ=1 AngleXU=0 Radius=1.5 StartAngle=4.71239 EndAngle=7.85398
    g3: ArcOfCircle CenterX=-1.5 CenterY=4.25 CenterZ=0 NormalX=0 NormalY=0 NormalZ=1 AngleXU=0 Radius=1.5 StartAngle=4.71239 EndAngle=7.85398
    g4: LineSegment StartX=-49.19 StartY=69.25 StartZ=0 EndX=-1.5 EndY=69.25 EndZ=0
    g5: LineSegment StartX=-49.19 StartY=66.25 StartZ=0 EndX=-1.5 EndY=66.25 EndZ=0
    g6: LineSegment StartX=-49.19 StartY=5.75 StartZ=0 EndX=-1.5 EndY=5.75 EndZ=0
    g7: LineSegment StartX=-49.19 StartY=2.75 StartZ=0 EndX=-1.5 EndY=2.75 EndZ=0
  constraints (19):
    c: Vertical(g0)
    c: Distance(g0) = 3
    c: Block(g0)
    c: Vertical(g1)
    c: Block(g2)
    c: Block(g3)
    c: Block(g1)
    c: Coincident(g4,g0)
    c: Coincident(g4,g2)
    c: Horizontal(g4)
    c: Coincident(g5,g0)
    c: Coincident(g5,g2)
    c: Horizontal(g5)
    c: Coincident(g6,g1)
    c: Coincident(g6,g3)
    c: Horizontal(g6)
    c: Coincident(g7,g1)
    c: Coincident(g7,g3)
    c: Horizontal(g7)
FEATURE [Part::Extrusion] Extrude069
  Base = -> Sketch078
  Dir = (1,0,0)
  DirMode = 2
  FaceMakerClass = Part::FaceMakerBullseye
  LengthFwd = 10
  LengthRev = 0
  Solid = true
  Symmetric = false
FEATURE [Part::Fillet] Fillet058  label="removeFromtMoreFrontCaseScrewRetainers003"
  Base = -> Extrude069
  Edges = 4 edges r=1.49: [Edge6,Edge11,Edge18,Edge23]
  Placement = pos=(-4,0,0) rot=(0,0,1;0rad)
FEATURE [Part::Cut] Cut066
  Base = -> Cut065
  Tool = -> Fillet058
FEATURE [Part::Cut] Cut067  label="screwPillars"
  Base = -> Cut066
  Tool = -> Fillet057
FEATURE [Part::MultiFuse] Fusion143  label="bottom021"
  Shapes = -> [Cut031,Cut063]
FEATURE [Part::Cylinder] Cylinder
  Angle = 360
  AttacherType = Attacher::AttachEngine3D
  Height = 10
  Placement = pos=(20.65,12,4.68) rot=(1,0,0;1.5708rad)
  Radius = 2
FEATURE [Part::Cylinder] Cylinder064
  Angle = 360
  AttacherType = Attacher::AttachEngine3D
  Height = 10
  Placement = pos=(20.65,12,67.38) rot=(1,0,0;1.5708rad)
  Radius = 2
FEATURE [Part::Cylinder] Cylinder065
  Angle = 360
  AttacherType = Attacher::AttachEngine3D
  Height = 10
  Placement = pos=(77.15,12,67.38) rot=(1,0,0;1.5708rad)
  Radius = 2
FEATURE [Part::Cylinder] Cylinder066
  Angle = 360
  AttacherType = Attacher::AttachEngine3D
  Height = 10
  Placement = pos=(77.15,12,4.68) rot=(1,0,0;1.5708rad)
  Radius = 2
FEATURE [Part::MultiFuse] Fusion144  label="removeFromThreadedInsertHousing"
  Shapes = -> [Cylinder065,Cylinder064,Cylinder,Cylinder066]
FEATURE [Part::Cut] Cut068  label="pcbStands001"
  Base = -> Cut064
  Tool = -> Fusion144
FEATURE [Part::MultiFuse] Fusion145
  Shapes = -> [Cut068,Fusion143]
FEATURE [Part::MultiFuse] Fusion146
  Shapes = -> [Fusion145]
FEATURE [Part::MultiFuse] Fusion147  label="bottom022"
  Shapes = -> [Cut067,Fusion146]
FEATURE [Part::MultiFuse] Fusion148  label="casePillars005"
  Shapes = -> [Cut047,Fusion092]
FEATURE [Part::MultiFuse] Fusion149  label="bottom023"
  Shapes = -> [Fusion124,Fusion113,Fusion147]
FEATURE [Part::MultiFuse] Fusion150  label="topBits"
  Shapes = -> [Cut025,Fusion148,Cut030,Fillet034]
FEATURE [Part::Feature] Face149 .. Face152  x4 (patterned run collapsed; names and placements below)
  shape: bbox 3.2 x 1.5 x 2e-07 mm, 1 faces, 0 solids (baked)
FEATURE [Part::Feature] Face153
  shape: bbox 3.6 x 3.2 x 2e-07 mm, 1 faces, 0 solids (baked)
FEATURE [Part::Feature] Face154
  shape: bbox 3.6 x 3.2 x 2e-07 mm, 1 faces, 0 solids (baked)
FEATURE [Sketcher::SketchObject] Sketch079  label="topSketch024"
  FullyConstrained = true
  sketch-geometry (6):
    g0: LineSegment StartX=19 StartY=38 StartZ=0 EndX=117 EndY=38 EndZ=0
    g1: ArcOfCircle CenterX=19 CenterY=19 CenterZ=0 NormalX=0 NormalY=0 NormalZ=1 AngleXU=0 Radius=19 StartAngle=1.5708 EndAngle=3.14159
    g2: LineSegment StartX=117 StartY=38 StartZ=0 EndX=117 EndY=19 EndZ=0
    g3: LineSegment StartX=98 StartY=1.0161e-12 StartZ=0 EndX=5.22862e-06 EndY=1.0161e-12 EndZ=0
    g4: LineSegment StartX=5.22862e-06 StartY=19 StartZ=0 EndX=5.22862e-06 EndY=1.0161e-12 EndZ=0
    g5: ArcOfCircle CenterX=98 CenterY=19 CenterZ=0 NormalX=0 NormalY=0 NormalZ=1 AngleXU=0 Radius=19 StartAngle=4.71239 EndAngle=6.28319
  constraints (16):
    c: Horizontal(g0)
    c: Distance(g0) = 98
    c: Coincident(g1,g0)
    c: Block(g1)
    c: Coincident(g2,g0)
    c: Vertical(g2)
    c: Distance(g2) = 19
    c: Horizontal(g3)
    c: Coincident(g4,g1)
    c: Vertical(g4)
    c: Coincident(g3,g4)
    c: Block(g3)
    c: Coincident(g5,g2)
    c: Coincident(g5,g3)
    c: Block(g0)
    c: Block(g5)
FEATURE [Sketcher::SketchObject] Sketch080  label="topSketch025"
  FullyConstrained = true
  sketch-geometry (6):
    g0: LineSegment StartX=19 StartY=38 StartZ=0 EndX=117 EndY=38 EndZ=0
    g1: ArcOfCircle CenterX=19 CenterY=19 CenterZ=0 NormalX=0 NormalY=0 NormalZ=1 AngleXU=0 Radius=19 StartAngle=1.5708 EndAngle=3.14159
    g2: LineSegment StartX=117 StartY=38 StartZ=0 EndX=117 EndY=19 EndZ=0
    g3: LineSegment StartX=98 StartY=1.0161e-12 StartZ=0 EndX=5.22862e-06 EndY=1.0161e-12 EndZ=0
    g4: LineSegment StartX=5.22862e-06 StartY=19 StartZ=0 EndX=5.22862e-06 EndY=1.0161e-12 EndZ=0
    g5: ArcOfCircle CenterX=98 CenterY=19 CenterZ=0 NormalX=0 NormalY=0 NormalZ=1 AngleXU=0 Radius=19 StartAngle=4.71239 EndAngle=6.28319
  constraints (16):
    c: Horizontal(g0)
    c: Distance(g0) = 98
    c: Coincident(g1,g0)
    c: Block(g1)
    c: Coincident(g2,g0)
    c: Vertical(g2)
    c: Distance(g2) = 19
    c: Horizontal(g3)
    c: Coincident(g4,g1)
    c: Vertical(g4)
    c: Coincident(g3,g4)
    c: Block(g3)
    c: Coincident(g5,g2)
    c: Coincident(g5,g3)
    c: Block(g0)
    c: Block(g5)
FEATURE [Part::Extrusion] Extrude070  label="sideA004"
  Base = -> Sketch080
  Dir = (0,0,1)
  DirMode = 2
  FaceMakerClass = Part::FaceMakerBullseye
  LengthFwd = 3
  LengthRev = 0
  Placement = pos=(0,0,-2.7) rot=(0,0,1;0rad)
  Solid = true
  Symmetric = false
FEATURE [Sketcher::SketchObject] Sketch081
  FullyConstrained = true
  Placement = pos=(117,19,0) rot=(0.57735,0.57735,0.57735;2.0944rad)
  sketch-geometry (8):
    g0: LineSegment StartX=-49.19 StartY=63.5 StartZ=0 EndX=-49.19 EndY=60.5 EndZ=0
    g1: LineSegment StartX=-49.19 StartY=11.5 StartZ=0 EndX=-49.19 EndY=8.5 EndZ=0
    g2: ArcOfCircle CenterX=-1.5 CenterY=62 CenterZ=0 NormalX=0 NormalY=0 NormalZ=1 AngleXU=0 Radius=1.5 StartAngle=4.71239 EndAngle=7.85398
    g3: ArcOfCircle CenterX=-1.5 CenterY=10 CenterZ=0 NormalX=0 NormalY=0 NormalZ=1 AngleXU=0 Radius=1.5 StartAngle=4.71239 EndAngle=7.85398
    g4: LineSegment StartX=-49.19 StartY=63.5 StartZ=0 EndX=-1.5 EndY=63.5 EndZ=0
    g5: LineSegment StartX=-49.19 StartY=60.5 StartZ=0 EndX=-1.5 EndY=60.5 EndZ=0
    g6: LineSegment StartX=-49.19 StartY=11.5 StartZ=0 EndX=-1.5 EndY=11.5 EndZ=0
    g7: LineSegment StartX=-49.19 StartY=8.5 StartZ=0 EndX=-1.5 EndY=8.5 EndZ=0
  constraints (19):
    c: Vertical(g0)
    c: Distance(g0) = 3
    c: Vertical(g1)
    c: Block(g1)
    c: Block(g2)
    c: Block(g3)
    c: Block(g0)
    c: Coincident(g4,g0)
    c: Coincident(g4,g2)
    c: Horizontal(g4)
    c: Coincident(g5,g0)
    c: Coincident(g5,g2)
    c: Horizontal(g5)
    c: Coincident(g6,g1)
    c: Coincident(g6,g3)
    c: Horizontal(g6)
    c: Coincident(g7,g1)
    c: Coincident(g7,g3)
    c: Horizontal(g7)
FEATURE [Part::Extrusion] Extrude071  label="sideB004"
  Base = -> Sketch079
  Dir = (0,0,1)
  DirMode = 2
  FaceMakerClass = Part::FaceMakerBullseye
  LengthFwd = 3
  LengthRev = 0
  Placement = pos=(0,0,71.7) rot=(0,0,1;0rad)
  Solid = true
  Symmetric = false
FEATURE [Part::MultiFuse] Fusion152  label="removeFromBottom004"
  Placement = pos=(2,0,0) rot=(0,0,1;0rad)
  Shapes = -> [Extrude070,Extrude071]
FEATURE [Part::Extrusion] Extrude072
  Base = -> Sketch081
  Dir = (1,0,0)
  DirMode = 2
  FaceMakerClass = Part::FaceMakerBullseye
  LengthFwd = 10
  LengthRev = 0
  Solid = true
  Symmetric = false
FEATURE [Part::Fillet] Fillet059  label="removeFromtMoreFrontCaseScrewRetainers004"
  Base = -> Extrude072
  Edges = 4 edges r=1.49: [Edge6,Edge11,Edge18,Edge23]
  Placement = pos=(-12,0,0) rot=(0,0,1;0rad)
FEATURE [Sketcher::SketchObject] Sketch082
  FullyConstrained = true
  Placement = pos=(117,19,0) rot=(0.57735,0.57735,0.57735;2.0944rad)
  sketch-geometry (8):
    g0: LineSegment StartX=-49.19 StartY=69.25 StartZ=0 EndX=-49.19 EndY=66.25 EndZ=0
    g1: LineSegment StartX=-49.19 StartY=5.75 StartZ=0 EndX=-49.19 EndY=2.75 EndZ=0
    g2: ArcOfCircle CenterX=-1.5 CenterY=67.75 CenterZ=0 NormalX=0 NormalY=0 NormalZ=1 AngleXU=0 Radius=1.5 StartAngle=4.71239 EndAngle=7.85398
    g3: ArcOfCircle CenterX=-1.5 CenterY=4.25 CenterZ=0 NormalX=0 NormalY=0 NormalZ=1 AngleXU=0 Radius=1.5 StartAngle=4.71239 EndAngle=7.85398
    g4: LineSegment StartX=-49.19 StartY=69.25 StartZ=0 EndX=-1.5 EndY=69.25 EndZ=0
    g5: LineSegment StartX=-49.19 StartY=66.25 StartZ=0 EndX=-1.5 EndY=66.25 EndZ=0
    g6: LineSegment StartX=-49.19 StartY=5.75 StartZ=0 EndX=-1.5 EndY=5.75 EndZ=0
    g7: LineSegment StartX=-49.19 StartY=2.75 StartZ=0 EndX=-1.5 EndY=2.75 EndZ=0
  constraints (19):
    c: Vertical(g0)
    c: Distance(g0) = 3
    c: Block(g0)
    c: Vertical(g1)
    c: Block(g2)
    c: Block(g3)
    c: Block(g1)
    c: Coincident(g4,g0)
    c: Coincident(g4,g2)
    c: Horizontal(g4)
    c: Coincident(g5,g0)
    c: Coincident(g5,g2)
    c: Horizontal(g5)
    c: Coincident(g6,g1)
    c: Coincident(g6,g3)
    c: Horizontal(g6)
    c: Coincident(g7,g1)
    c: Coincident(g7,g3)
    c: Horizontal(g7)
FEATURE [Part::Extrusion] Extrude073
  Base = -> Sketch082
  Dir = (1,0,0)
  DirMode = 2
  FaceMakerClass = Part::FaceMakerBullseye
  LengthFwd = 10
  LengthRev = 0
  Solid = true
  Symmetric = false
FEATURE [Part::Fillet] Fillet060  label="removeFromtMoreFrontCaseScrewRetainers005"
  Base = -> Extrude073
  Edges = 4 edges r=1.49: [Edge6,Edge11,Edge18,Edge23]
  Placement = pos=(-4,0,0) rot=(0,0,1;0rad)
FEATURE [Part::Revolution] Revolve163  label="backCaseScrewRetainer004"
  Angle = 360
  Axis = (0,1,0)
  Base = (0,0,0)
  FaceMakerClass = Part::FaceMakerBullseye
  Placement = pos=(12.5,3,62) rot=(0,0,1;0rad)
  Solid = false
  Source = -> Face149
  Symmetric = false
FEATURE [Part::Revolution] Revolve164  label="frontCaseScrewRetainer006"
  Angle = 360
  Axis = (0,1,0)
  Base = (0,0,0)
  FaceMakerClass = Part::FaceMakerBullseye
  Placement = pos=(89.5,3,68.5) rot=(0,0,1;0rad)
  Solid = false
  Source = -> Face151
  Symmetric = false
FEATURE [Part::Revolution] Revolve165  label="frontCaseScrewRetainer007"
  Angle = 360
  Axis = (0,1,0)
  Base = (0,0,0)
  FaceMakerClass = Part::FaceMakerBullseye
  Placement = pos=(89.5,3,3.5) rot=(0,0,1;0rad)
  Solid = false
  Source = -> Face152
  Symmetric = false
FEATURE [Part::Revolution] Revolve166  label="backCaseScrewRetainer005"
  Angle = 360
  Axis = (0,1,0)
  Base = (0,0,0)
  FaceMakerClass = Part::FaceMakerBullseye
  Placement = pos=(12.5,3,10) rot=(0,0,1;0rad)
  Solid = false
  Source = -> Face150
  Symmetric = false
FEATURE [Part::Revolution] Revolve167  label="moreFrontCaseScrewRetainer006"
  Angle = 360
  Axis = (0,1,0)
  Base = (0,0,0)
  FaceMakerClass = Part::FaceMakerBullseye
  Placement = pos=(109.5,4.5,68.5) rot=(0,0,1;0rad)
  Solid = false
  Source = -> Face153
  Symmetric = false
FEATURE [Part::Revolution] Revolve168  label="moreFrontCaseScrewRetainer007"
  Angle = 360
  Axis = (0,1,0)
  Base = (0,0,0)
  FaceMakerClass = Part::FaceMakerBullseye
  Placement = pos=(109.5,4.5,3.5) rot=(0,0,1;0rad)
  Solid = false
  Source = -> Face154
  Symmetric = false
FEATURE [Part::MultiFuse] Fusion151  label="screwRetainers003"
  Shapes = -> [Revolve168,Revolve167,Revolve166,Revolve165,Revolve164,Revolve163]
FEATURE [Part::Cut] Cut069  label="screwRetainers004"
  Base = -> Fusion151
  Tool = -> Fusion152
FEATURE [Part::Cut] Cut070
  Base = -> Cut069
  Tool = -> Fillet060
FEATURE [Part::Cut] Cut071  label="screwPillars001"
  Base = -> Cut070
  Tool = -> Fillet059
FEATURE [Part::MultiFuse] Fusion153  label="bottom024"
  Shapes = -> [Fusion149,Cut071]
FEATURE [Part::Cylinder] Cylinder067
  Angle = 360
  AttacherType = Attacher::AttachEngine3D
  Height = 10
  Placement = pos=(20.65,12,4.68) rot=(1,0,0;1.5708rad)
  Radius = 2
FEATURE [Part::Cylinder] Cylinder068
  Angle = 360
  AttacherType = Attacher::AttachEngine3D
  Height = 10
  Placement = pos=(20.65,12,67.38) rot=(1,0,0;1.5708rad)
  Radius = 2
FEATURE [Part::Cylinder] Cylinder069
  Angle = 360
  AttacherType = Attacher::AttachEngine3D
  Height = 10
  Placement = pos=(77.15,12,67.38) rot=(1,0,0;1.5708rad)
  Radius = 2
FEATURE [Part::Cylinder] Cylinder070
  Angle = 360
  AttacherType = Attacher::AttachEngine3D
  Height = 10
  Placement = pos=(77.15,12,4.68) rot=(1,0,0;1.5708rad)
  Radius = 2
FEATURE [Part::MultiFuse] Fusion154  label="removeFromThreadedInsertHousing001"
  Shapes = -> [Cylinder069,Cylinder068,Cylinder067,Cylinder070]
FEATURE [Part::Cut] Cut072  label="bottom025"
  Base = -> Fusion153
  Tool = -> Fusion154
FEATURE [Image::ImagePlane] ImagePlane
  XSize = 339
  YSize = 72
FEATURE [Sketcher::SketchObject] Sketch083
  FullyConstrained = true
  MapMode = 5
  Support = -> [XY_Plane]
  sketch-geometry (338):
    g0: LineSegment StartX=-151.619 StartY=28.8932 StartZ=0 EndX=-140.819 EndY=28.8932 EndZ=0
    g1: LineSegment StartX=-151.619 StartY=24.0313 StartZ=0 EndX=-151.619 EndY=28.8932 EndZ=0
    g2: LineSegment StartX=-140.819 StartY=17.7713 StartZ=0 EndX=-151.619 EndY=17.7713 EndZ=0
    g3: LineSegment StartX=-151.619 StartY=17.7713 StartZ=0 EndX=-151.619 EndY=22.6313 EndZ=0
    g4: LineSegment StartX=-151.619 StartY=22.6313 StartZ=0 EndX=-145.128 EndY=22.6313 EndZ=0
    g5: LineSegment StartX=-145.128 StartY=24.0313 StartZ=0 EndX=-140.819 EndY=28.8932 EndZ=0
    g6: LineSegment StartX=-145.128 StartY=22.6313 StartZ=0 EndX=-140.819 EndY=17.7713 EndZ=0
    g7: ArcOfCircle CenterX=-155.157 CenterY=23.3323 CenterZ=0 NormalX=0 NormalY=0 NormalZ=1 AngleXU=0 Radius=6.92354 StartAngle=1.03434 EndAngle=5.24885
    g8: ArcOfCircle CenterX=-155.157 CenterY=23.3323 CenterZ=0 NormalX=0 NormalY=0 NormalZ=1 AngleXU=0 Radius=12.6269 StartAngle=1.28675 EndAngle=4.99643
    g9: LineSegment StartX=-151.619 StartY=35.4532 StartZ=0 EndX=-151.619 EndY=29.2832 EndZ=0
    g10: LineSegment StartX=-151.619 StartY=17.3813 StartZ=0 EndX=-151.619 EndY=11.2113 EndZ=0
    g11-g21: Circle x11 (B-spline internal-alignment scaffolding for g22; pole/knot coordinates omitted)
    g22: BSplineCurve PolesCount=11 KnotsCount=9 Degree=3 IsPeriodic=0
    g23-g31: GeomPoint x9 (B-spline internal-alignment scaffolding for g22; pole/knot coordinates omitted)
    g32-g49: Circle x18 (B-spline internal-alignment scaffolding for g50; pole/knot coordinates omitted)
    g50: BSplineCurve PolesCount=18 KnotsCount=16 Degree=3 IsPeriodic=0
    g51-g66: GeomPoint x16 (B-spline internal-alignment scaffolding for g50; pole/knot coordinates omitted)
    g67: LineSegment StartX=-117.124 StartY=30.093 StartZ=0 EndX=-117.603 EndY=26.5272 EndZ=0
    g68: LineSegment StartX=-117.603 StartY=17.8472 StartZ=0 EndX=-117.124 EndY=14.2659 EndZ=0
    g69: Ellipse CenterX=-109.671 CenterY=20.025 CenterZ=0 NormalX=0 NormalY=0 NormalZ=1 MajorRadius=3.34798 MinorRadius=2.71052 AngleXU=-1.56793
    g70: GeomPoint X=-109.666 Y=18.0598 Z=0
    g71: GeomPoint X=-109.677 Y=21.9902 Z=0
    g72: Ellipse CenterX=-109.671 CenterY=20.0123 CenterZ=0 NormalX=0 NormalY=0 NormalZ=1 MajorRadius=6.93002 MinorRadius=6.36273 AngleXU=-3.13976
    g73: GeomPoint X=-112.417 Y=20.0073 Z=0
    g74: GeomPoint X=-106.925 Y=20.0173 Z=0
    g75: Ellipse CenterX=-51.7682 CenterY=20.1463 CenterZ=0 NormalX=0 NormalY=0 NormalZ=1 MajorRadius=3.19279 MinorRadius=2.71052 AngleXU=-1.52774
    g76: GeomPoint X=-51.6955 Y=18.4606 Z=0
    g77: GeomPoint X=-51.8408 Y=21.832 Z=0
    g78: GeomPoint X=-54.5142 Y=20.1413 Z=0
    g79: GeomPoint X=-49.0221 Y=20.1513 Z=0
    g80: Ellipse CenterX=-51.7682 CenterY=20.1463 CenterZ=0 NormalX=0 NormalY=0 NormalZ=1 MajorRadius=6.93002 MinorRadius=6.36273 AngleXU=-3.13976
    g81: Ellipse CenterX=-22.8436 CenterY=20.1783 CenterZ=0 NormalX=0 NormalY=0 NormalZ=1 MajorRadius=3.31512 MinorRadius=2.71052 AngleXU=-1.60214
    g82: GeomPoint X=-22.9034 Y=18.2706 Z=0
    g83: GeomPoint X=-22.7838 Y=22.0861 Z=0
    g84: GeomPoint X=-25.5897 Y=20.1733 Z=0
    g85: GeomPoint X=-20.0976 Y=20.1833 Z=0
    g86: Ellipse CenterX=-22.8436 CenterY=20.1783 CenterZ=0 NormalX=0 NormalY=0 NormalZ=1 MajorRadius=6.93002 MinorRadius=6.36273 AngleXU=-3.13976
    g87: LineSegment StartX=-101.889 StartY=14.1107 StartZ=0 EndX=-97.7455 EndY=14.1107 EndZ=0
    g88: LineSegment StartX=-93.8155 StartY=14.1107 StartZ=0 EndX=-89.6755 EndY=14.1107 EndZ=0
    g89: LineSegment StartX=-85.7455 StartY=14.1107 StartZ=0 EndX=-81.6055 EndY=14.1107 EndZ=0
    g90: LineSegment StartX=-101.889 StartY=14.1107 StartZ=0 EndX=-101.889 EndY=25.9907 EndZ=0
    g91: LineSegment StartX=-101.889 StartY=25.9907 StartZ=0 EndX=-97.8594 EndY=25.9907 EndZ=0
    g92: LineSegment StartX=-97.8594 StartY=25.9907 StartZ=0 EndX=-97.8594 EndY=24.0907 EndZ=0
    g93: LineSegment StartX=-97.7455 StartY=14.1107 StartZ=0 EndX=-97.7455 EndY=19.9107 EndZ=0
    g94: LineSegment StartX=-89.6755 StartY=14.1107 StartZ=0 EndX=-89.6755 EndY=19.9107 EndZ=0
    g95: LineSegment StartX=-93.8155 StartY=14.1107 StartZ=0 EndX=-93.8155 EndY=21.0107 EndZ=0
    g96-g106: Circle x11 (B-spline internal-alignment scaffolding for g107; pole/knot coordinates omitted)
    g107: BSplineCurve PolesCount=11 KnotsCount=9 Degree=3 IsPeriodic=0
    g108-g116: GeomPoint x9 (B-spline internal-alignment scaffolding for g107; pole/knot coordinates omitted)
    g117: BSplineCurve PolesCount=11 KnotsCount=9 Degree=3 IsPeriodic=0
    g118-g125: Circle x8 (B-spline internal-alignment scaffolding for g126; pole/knot coordinates omitted)
    g126: BSplineCurve PolesCount=8 KnotsCount=6 Degree=3 IsPeriodic=0
    g127-g132: GeomPoint x6 (B-spline internal-alignment scaffolding for g126; pole/knot coordinates omitted)
    g133: BSplineCurve PolesCount=8 KnotsCount=6 Degree=3 IsPeriodic=0
    g134: LineSegment StartX=-85.7455 StartY=21.0107 StartZ=0 EndX=-85.7455 EndY=14.1107 EndZ=0
    g135: LineSegment StartX=-80.0879 StartY=14.1107 StartZ=0 EndX=-75.944 EndY=14.1107 EndZ=0
    g136: LineSegment StartX=-72.014 StartY=14.1107 StartZ=0 EndX=-67.874 EndY=14.1107 EndZ=0
    g137: LineSegment StartX=-63.944 StartY=14.1107 StartZ=0 EndX=-59.804 EndY=14.1107 EndZ=0
    g138: LineSegment StartX=-80.0879 StartY=14.1107 StartZ=0 EndX=-80.0879 EndY=25.9907 EndZ=0
    g139: LineSegment StartX=-80.0879 StartY=25.9907 StartZ=0 EndX=-76.0579 EndY=25.9907 EndZ=0
    g140: LineSegment StartX=-76.0579 StartY=25.9907 StartZ=0 EndX=-76.0579 EndY=24.0907 EndZ=0
    g141: LineSegment StartX=-75.944 StartY=14.1107 StartZ=0 EndX=-75.944 EndY=19.9107 EndZ=0
    g142: LineSegment StartX=-67.874 StartY=14.1107 StartZ=0 EndX=-67.874 EndY=19.9107 EndZ=0
    g143: LineSegment StartX=-72.014 StartY=14.1107 StartZ=0 EndX=-72.014 EndY=21.0107 EndZ=0
    g144-g148: Circle x5 (B-spline internal-alignment scaffolding for g149; pole/knot coordinates omitted)
    g149: BSplineCurve PolesCount=11 KnotsCount=9 Degree=3 IsPeriodic=0
    g150-g158: GeomPoint x9 (B-spline internal-alignment scaffolding for g149; pole/knot coordinates omitted)
    g159: BSplineCurve PolesCount=11 KnotsCount=9 Degree=3 IsPeriodic=0
    g160-g167: Circle x8 (B-spline internal-alignment scaffolding for g168; pole/knot coordinates omitted)
    g168: BSplineCurve PolesCount=8 KnotsCount=6 Degree=3 IsPeriodic=0
    g169-g174: GeomPoint x6 (B-spline internal-alignment scaffolding for g168; pole/knot coordinates omitted)
    g175: BSplineCurve PolesCount=8 KnotsCount=6 Degree=3 IsPeriodic=0
    g176: LineSegment StartX=-63.944 StartY=21.0107 StartZ=0 EndX=-63.944 EndY=14.1107 EndZ=0
    g177: LineSegment StartX=-59.804 StartY=14.1107 StartZ=0 EndX=-59.804 EndY=21.5868 EndZ=0
    g178: BSplineCurve PolesCount=4 KnotsCount=2 Degree=3 IsPeriodic=0
    g179: GeomPoint X=-59.804 Y=21.5868 Z=0
    g180: GeomPoint X=-60.2379 Y=24.0907 Z=0
    g181: LineSegment StartX=-81.6055 StartY=14.1107 StartZ=0 EndX=-81.6055 EndY=21.5868 EndZ=0
    g182: LineSegment StartX=-151.619 StartY=24.0313 StartZ=0 EndX=-145.128 EndY=24.0313 EndZ=0
    g183: Circle CenterX=-82.0394 CenterY=24.0907 CenterZ=0 NormalX=0 NormalY=0 NormalZ=1 AngleXU=0 Radius=1
    g184: Circle CenterX=-81.7131 CenterY=23.2736 CenterZ=0 NormalX=0 NormalY=0 NormalZ=1 AngleXU=0 Radius=1
    g185: Circle CenterX=-81.6055 CenterY=21.5868 CenterZ=0 NormalX=0 NormalY=0 NormalZ=1 AngleXU=0 Radius=1
    g186: BSplineCurve PolesCount=3 KnotsCount=2 Degree=2 IsPeriodic=0
    g187: GeomPoint X=-82.0394 Y=24.0907 Z=0
    g188: GeomPoint X=-81.6055 Y=21.5868 Z=0
    g189: Ellipse CenterX=-37.3522 CenterY=19.9515 CenterZ=0 NormalX=0 NormalY=0 NormalZ=1 MajorRadius=2.99755 MinorRadius=2.49 AngleXU=1.5708
    g190: GeomPoint X=-37.3522 Y=21.6203 Z=0
    g191: GeomPoint X=-37.3522 Y=18.2826 Z=0
    g192: ArcOfEllipse CenterX=-38.7647 CenterY=20.06 CenterZ=0 NormalX=0 NormalY=0 NormalZ=1 MajorRadius=6.30025 MinorRadius=5.3849 AngleXU=1.57276 StartAngle=5.50632 EndAngle=10.3035
    g193: GeomPoint X=-38.7711 Y=23.3304 Z=0
    g194: GeomPoint X=-38.7583 Y=16.7895 Z=0
    g195: LineSegment StartX=-34.6109 StartY=14.1107 StartZ=0 EndX=-30.8984 EndY=14.1107 EndZ=0
    g196: LineSegment StartX=-30.8984 StartY=14.1107 StartZ=0 EndX=-30.8984 EndY=31.1784 EndZ=0
    g197: LineSegment StartX=-30.8984 StartY=31.1784 StartZ=0 EndX=-34.9984 EndY=31.1784 EndZ=0
    g198: LineSegment StartX=-34.9984 StartY=24.5602 StartZ=0 EndX=-34.9984 EndY=31.1784 EndZ=0
    g199: LineSegment StartX=-34.6109 StartY=16.0476 StartZ=0 EndX=-34.6109 EndY=14.1107 EndZ=0
    g200: LineSegment StartX=-14.8781 StartY=14.1107 StartZ=0 EndX=-10.5106 EndY=14.1107 EndZ=0
    g201: LineSegment StartX=-14.8781 StartY=14.1107 StartZ=0 EndX=-14.8781 EndY=25.8504 EndZ=0
    g202: LineSegment StartX=-14.8781 StartY=25.8504 StartZ=0 EndX=-10.8534 EndY=25.8504 EndZ=0
    g203: LineSegment StartX=-10.8534 StartY=25.8504 StartZ=0 EndX=-10.8534 EndY=24.0923 EndZ=0
    g204: LineSegment StartX=-10.5106 StartY=14.1107 StartZ=0 EndX=-10.5106 EndY=19.7752 EndZ=0
    g205: LineSegment StartX=-5.96397 StartY=25.9304 StartZ=0 EndX=-5.96397 EndY=22.574 EndZ=0
    g206-g214: Circle x9 (B-spline internal-alignment scaffolding for g215; pole/knot coordinates omitted)
    g215: BSplineCurve PolesCount=9 KnotsCount=7 Degree=3 IsPeriodic=0
    g216-g222: GeomPoint x7 (B-spline internal-alignment scaffolding for g215; pole/knot coordinates omitted)
    g223-g232: Circle x10 (B-spline internal-alignment scaffolding for g233; pole/knot coordinates omitted)
    g233: BSplineCurve PolesCount=10 KnotsCount=8 Degree=3 IsPeriodic=0
    g234-g241: GeomPoint x8 (B-spline internal-alignment scaffolding for g233; pole/knot coordinates omitted)
    g242: LineSegment StartX=-1.58923 StartY=21.0696 StartZ=0 EndX=2.62034 EndY=21.0696 EndZ=0
    g243: LineSegment StartX=-1.55856 StartY=18.7342 StartZ=0 EndX=6.45946 EndY=18.7342 EndZ=0
    g244: LineSegment StartX=5.29231 StartY=17.386 StartZ=0 EndX=5.29231 EndY=14.3674 EndZ=0
    g245-g269: Circle x25 (B-spline internal-alignment scaffolding for g270; pole/knot coordinates omitted)
    g270: BSplineCurve PolesCount=25 KnotsCount=23 Degree=3 IsPeriodic=0
    g271-g293: GeomPoint x23 (B-spline internal-alignment scaffolding for g270; pole/knot coordinates omitted)
    g294-g304: Circle x11 (B-spline internal-alignment scaffolding for g305; pole/knot coordinates omitted)
    g305: BSplineCurve PolesCount=11 KnotsCount=9 Degree=3 IsPeriodic=0
    g306-g314: GeomPoint x9 (B-spline internal-alignment scaffolding for g305; pole/knot coordinates omitted)
    g315-g326: Circle x12 (B-spline internal-alignment scaffolding for g327; pole/knot coordinates omitted)
    g327: BSplineCurve PolesCount=12 KnotsCount=10 Degree=3 IsPeriodic=0
    g328-g337: GeomPoint x10 (B-spline internal-alignment scaffolding for g327; pole/knot coordinates omitted)
  constraints (252):
    c: Coincident(g1,g0)
    c: Horizontal(g0)
    c: Vertical(g1)
    c: Coincident(g2,g3)
    c: Coincident(g3,g4)
    c: Horizontal(g4)
    c: Horizontal(g2)
    c: Vertical(g3)
    c: Block(g1)
    c: Distance(g3) = 4.86
    c: Block(g4)
    c: Distance(g0) = 10.8
    c: Distance(g2) = 10.8
    c: Coincident(g5,g0)
    c: Coincident(g6,g4)
    c: Coincident(g6,g2)
    c: Block(g8)
    c: Block(g7)
    c: Coincident(g9,g8)
    c: Coincident(g9,g7)
    c: Vertical(g9)
    c: Coincident(g10,g7)
    c: Coincident(g10,g8)
    c: Vertical(g10)
    c: Weight(g11) = 1
    c: Equal(g11, g12-g21) x10
    c: InternalAlignment(g11-g21 -> g22) x11
    c: InternalAlignment(g23-g31 -> g22) x9
    c: Block(g22)
    c: Weight(g32) = 1
    c: Equal(g32, g33-g49) x17
    c: InternalAlignment(g32-g49 -> g50) x18
    c: InternalAlignment(g51-g66 -> g50) x16
    c: Block(g50)
    c: Coincident(g67,g50)
    c: Coincident(g67,g22)
    c: Coincident(g68,g22)
    c: Coincident(g68,g50)
    c: InternalAlignment(g70,g69)
    c: InternalAlignment(g71,g69)
    c: Block(g69)
    c: InternalAlignment(g73,g72)
    c: InternalAlignment(g74,g72)
    c: Block(g72)
    c: InternalAlignment(g76,g75)
    c: InternalAlignment(g77,g75)
    c: InternalAlignment(g78,g80)
    c: InternalAlignment(g79,g80)
    c: Block(g80)
    c: Coincident(g75,g80)
    c: Block(g75)
    c: InternalAlignment(g82,g81)
    c: InternalAlignment(g83,g81)
    c: InternalAlignment(g84,g86)
    c: InternalAlignment(g85,g86)
    c: Block(g86)
    c: Coincident(g81,g86)
    c: Block(g81)
    c: Horizontal(g87)
    c: Block(g87)
    c: Horizontal(g88)
    c: Distance(g88) = 4.14
    c: Horizontal(g89)
    c: Equal(g88,g89) = 4.14
    c: Block(g89)
    c: Block(g88)
    c: Coincident(g90,g87)
    c: Vertical(g90)
    c: Distance(g90) = 11.88
    c: Coincident(g91,g90)
    c: Horizontal(g91)
    c: Coincident(g92,g91)
    c: Vertical(g92)
    c: Distance(g91) = 4.03
    c: Distance(g92) = 1.9
    c: Coincident(g93,g87)
    c: Vertical(g93)
    c: Vertical(g94)
    c: Coincident(g94,g88)
    c: Distance(g93) = 5.8
    c: Distance(g94) = 5.8
    c: Vertical(g95)
    c: Coincident(g95,g88)
    c: Distance(g95) = 6.9
    c: Coincident(g107,g92)
    c: Weight(g96) = 1
    c: Equal(g96, g97-g106) x10
    c: InternalAlignment(g96-g106 -> g107) x11
    c: InternalAlignment(g108-g116 -> g107) x9
    c: Block(g107)
    c: Block(g117)
    c: Coincident(g126,g93)
    c: Weight(g118) = 1
    c: Equal(g118, g119-g125) x7
    c: Coincident(g126,g95)
    c: InternalAlignment(g118-g125 -> g126) x8
    c: InternalAlignment(g127-g132 -> g126) x6
    c: Coincident(g133,g94)
    c: Block(g126)
    c: Block(g133)
    c: Coincident(g134,g133)
    c: Coincident(g134,g89)
    c: Vertical(g134)
    c: Horizontal(g135)
    c: Block(g135)
    c: Horizontal(g136)
    c: Equal(g88,g136) = 4.14
    c: Horizontal(g137)
    c: Equal(g136,g137) = 4.14
    c: Block(g137)
    c: Block(g136)
    c: Coincident(g138,g135)
    c: Vertical(g138)
    c: Equal(g90,g138) = 11.88
    c: Coincident(g139,g138)
    c: Horizontal(g139)
    c: Coincident(g140,g139)
    c: Vertical(g140)
    c: Equal(g91,g139) = 4.03
    c: Equal(g92,g140) = 1.9
    c: Coincident(g141,g135)
    c: Vertical(g141)
    c: Vertical(g142)
    c: Coincident(g142,g136)
    c: Equal(g93,g141) = 5.8
    c: Equal(g94,g142) = 5.8
    c: Vertical(g143)
    c: Coincident(g143,g136)
    c: Equal(g95,g143) = 6.9
    c: Coincident(g149,g140)
    c: Equal(g96,g144) = 1
    c: Equal(g144, g145-g148) x4
    c: InternalAlignment(g144-g148 -> g149) x5
    c: InternalAlignment(g150-g158 -> g149) x9
    c: Block(g149)
    c: Block(g159)
    c: Coincident(g168,g141)
    c: Equal(g118,g160) = 1
    c: Equal(g160, g161-g167) x7
    c: Coincident(g168,g143)
    c: InternalAlignment(g160-g167 -> g168) x8
    c: InternalAlignment(g169-g174 -> g168) x6
    c: Coincident(g175,g142)
    c: Block(g168)
    c: Block(g175)
    c: Coincident(g176,g175)
    c: Coincident(g176,g137)
    c: Vertical(g176)
    c: Coincident(g177,g137)
    c: Vertical(g177)
    c: Coincident(g178,g177)
    c: Coincident(g178,g159)
    c: InternalAlignment(g179,g178)
    c: InternalAlignment(g180,g178)
    c: Block(g178)
    c: Vertical(g181)
    c: Coincident(g181,g89)
    c: Block(g5)
    c: Coincident(g182,g1)
    c: Coincident(g182,g5)
    c: Horizontal(g182)
    c: Coincident(g186,g117)
    c: Weight(g183) = 1
    c: Equal(g183,g184)
    c: Equal(g183,g185)
    c: Coincident(g186,g181)
    c: InternalAlignment(g183,g186)
    c: InternalAlignment(g184,g186)
    c: InternalAlignment(g185,g186)
    c: InternalAlignment(g187,g186)
    c: InternalAlignment(g188,g186)
    c: Block(g186)
    c: InternalAlignment(g190,g189)
    c: InternalAlignment(g191,g189)
    c: Block(g189)
    c: InternalAlignment(g193,g192)
    c: InternalAlignment(g194,g192)
    c: Block(g192)
    c: Horizontal(g195)
    c: Block(g195)
    c: Coincident(g196,g195)
    c: Vertical(g196)
    c: Block(g196)
    c: Distance(g195) = 3.71244
    c: Coincident(g197,g196)
    c: Horizontal(g197)
    c: Distance(g197) = 4.1
    c: Coincident(g198,g192)
    c: Coincident(g198,g197)
    c: Vertical(g198)
    c: Block(g198)
    c: Coincident(g199,g192)
    c: Coincident(g199,g195)
    c: Vertical(g199)
    c: Block(g199)
    c: Horizontal(g200)
    c: Block(g200)
    c: Coincident(g201,g200)
    c: Vertical(g201)
    c: Block(g201)
    c: Coincident(g202,g201)
    c: Horizontal(g202)
    c: Block(g202)
    c: Coincident(g203,g202)
    c: Vertical(g203)
    c: Block(g203)
    c: Coincident(g204,g200)
    c: Vertical(g204)
    c: Block(g204)
    c: Coincident(g215,g203)
    c: Weight(g206) = 1
    c: Equal(g206, g207-g214) x8
    c: Coincident(g215,g205)
    c: InternalAlignment(g206-g214 -> g215) x9
    c: InternalAlignment(g216-g222 -> g215) x7
    c: Coincident(g233,g204)
    c: Weight(g223) = 1
    c: Equal(g223, g224-g232) x9
    c: Coincident(g233,g205)
    c: InternalAlignment(g223-g232 -> g233) x10
    c: InternalAlignment(g234-g241 -> g233) x8
    c: Vertical(g205)
    c: Block(g205)
    c: Block(g215)
    c: Block(g233)
    c: Horizontal(g242)
    c: Horizontal(g243)
    c: Block(g242)
    c: Block(g243)
    c: Vertical(g244)
    c: Block(g244)
    c: Coincident(g270,g243)
    c: Weight(g245) = 1
    c: Equal(g245, g246-g269) x24
    c: Coincident(g270,g244)
    c: InternalAlignment(g245-g269 -> g270) x25
    c: InternalAlignment(g271-g293 -> g270) x23
    c: Coincident(g305,g242)
    c: Weight(g294) = 1
    c: Equal(g294, g295-g304) x10
    c: Coincident(g305,g242)
    c: InternalAlignment(g294-g304 -> g305) x11
    c: InternalAlignment(g306-g314 -> g305) x9
    c: Block(g305)
    c: Coincident(g327,g243)
    c: Weight(g315) = 1
    c: Equal(g315, g316-g326) x11
    c: Coincident(g327,g244)
    c: InternalAlignment(g315-g326 -> g327) x12
    c: InternalAlignment(g328-g337 -> g327) x10
    c: Block(g327)
    c: Block(g270)
FEATURE [PartDesign::Body] Body  label="CommodoreLogoAndText"
  Group = -> [Sketch083]
  Origin = -> Origin
FEATURE [Part::Extrusion] Extrude074  label="CommodoreLogoAndText001"
  Base = -> Sketch083
  Dir = (0,0,1)
  DirMode = 2
  FaceMakerClass = Part::FaceMakerBullseye
  LengthFwd = 10
  LengthRev = 0
  Solid = true
  Symmetric = false
FEATURE [Part::FeaturePython] Clone  label="CommodoreLogoAndTextScale"  # Draft clone (typed FeaturePython)
  AttacherType = Attacher::AttachEngine3D
  Fuse = false
  Objects = -> [Extrude074]
  Placement = pos=(111,5.37,-11.6) rot=(0,0,1;0rad)
  Scale = (0.62,0.62,1)
FEATURE [Part::Mirroring] Part__Mirroring  label="CommodoreLogoAndTextScale (Mirror #1)"
  Base = (0,0,0)
  Normal = (1,0,0)
  Placement = pos=(123.576,0,0) rot=(0,0,1;0rad)
  Source = -> Clone
FEATURE [Sketcher::SketchObject] Sketch084
  FullyConstrained = true
  MapMode = 5
  Support = -> [XY_Plane001]
  sketch-geometry (338):
    g0: LineSegment StartX=-151.619 StartY=28.8932 StartZ=0 EndX=-140.819 EndY=28.8932 EndZ=0
    g1: LineSegment StartX=-151.619 StartY=24.0313 StartZ=0 EndX=-151.619 EndY=28.8932 EndZ=0
    g2: LineSegment StartX=-140.819 StartY=17.7713 StartZ=0 EndX=-151.619 EndY=17.7713 EndZ=0
    g3: LineSegment StartX=-151.619 StartY=17.7713 StartZ=0 EndX=-151.619 EndY=22.6313 EndZ=0
    g4: LineSegment StartX=-151.619 StartY=22.6313 StartZ=0 EndX=-145.128 EndY=22.6313 EndZ=0
    g5: LineSegment StartX=-145.128 StartY=24.0313 StartZ=0 EndX=-140.819 EndY=28.8932 EndZ=0
    g6: LineSegment StartX=-145.128 StartY=22.6313 StartZ=0 EndX=-140.819 EndY=17.7713 EndZ=0
    g7: ArcOfCircle CenterX=-155.157 CenterY=23.3323 CenterZ=0 NormalX=0 NormalY=0 NormalZ=1 AngleXU=0 Radius=6.92354 StartAngle=1.03434 EndAngle=5.24885
    g8: ArcOfCircle CenterX=-155.157 CenterY=23.3323 CenterZ=0 NormalX=0 NormalY=0 NormalZ=1 AngleXU=0 Radius=12.6269 StartAngle=1.28675 EndAngle=4.99643
    g9: LineSegment StartX=-151.619 StartY=35.4532 StartZ=0 EndX=-151.619 EndY=29.2832 EndZ=0
    g10: LineSegment StartX=-151.619 StartY=17.3813 StartZ=0 EndX=-151.619 EndY=11.2113 EndZ=0
    g11-g21: Circle x11 (B-spline internal-alignment scaffolding for g22; pole/knot coordinates omitted)
    g22: BSplineCurve PolesCount=11 KnotsCount=9 Degree=3 IsPeriodic=0
    g23-g31: GeomPoint x9 (B-spline internal-alignment scaffolding for g22; pole/knot coordinates omitted)
    g32-g49: Circle x18 (B-spline internal-alignment scaffolding for g50; pole/knot coordinates omitted)
    g50: BSplineCurve PolesCount=18 KnotsCount=16 Degree=3 IsPeriodic=0
    g51-g66: GeomPoint x16 (B-spline internal-alignment scaffolding for g50; pole/knot coordinates omitted)
    g67: LineSegment StartX=-117.124 StartY=30.093 StartZ=0 EndX=-117.603 EndY=26.5272 EndZ=0
    g68: LineSegment StartX=-117.603 StartY=17.8472 StartZ=0 EndX=-117.124 EndY=14.2659 EndZ=0
    g69: Ellipse CenterX=-109.671 CenterY=20.025 CenterZ=0 NormalX=0 NormalY=0 NormalZ=1 MajorRadius=3.34798 MinorRadius=2.71052 AngleXU=-1.56793
    g70: GeomPoint X=-109.666 Y=18.0598 Z=0
    g71: GeomPoint X=-109.677 Y=21.9902 Z=0
    g72: Ellipse CenterX=-109.671 CenterY=20.0123 CenterZ=0 NormalX=0 NormalY=0 NormalZ=1 MajorRadius=6.93002 MinorRadius=6.36273 AngleXU=-3.13976
    g73: GeomPoint X=-112.417 Y=20.0073 Z=0
    g74: GeomPoint X=-106.925 Y=20.0173 Z=0
    g75: Ellipse CenterX=-51.7682 CenterY=20.1463 CenterZ=0 NormalX=0 NormalY=0 NormalZ=1 MajorRadius=3.19279 MinorRadius=2.71052 AngleXU=-1.52774
    g76: GeomPoint X=-51.6955 Y=18.4606 Z=0
    g77: GeomPoint X=-51.8408 Y=21.832 Z=0
    g78: GeomPoint X=-54.5142 Y=20.1413 Z=0
    g79: GeomPoint X=-49.0221 Y=20.1513 Z=0
    g80: Ellipse CenterX=-51.7682 CenterY=20.1463 CenterZ=0 NormalX=0 NormalY=0 NormalZ=1 MajorRadius=6.93002 MinorRadius=6.36273 AngleXU=-3.13976
    g81: Ellipse CenterX=-22.8436 CenterY=20.1783 CenterZ=0 NormalX=0 NormalY=0 NormalZ=1 MajorRadius=3.31512 MinorRadius=2.71052 AngleXU=-1.60214
    g82: GeomPoint X=-22.9034 Y=18.2706 Z=0
    g83: GeomPoint X=-22.7838 Y=22.0861 Z=0
    g84: GeomPoint X=-25.5897 Y=20.1733 Z=0
    g85: GeomPoint X=-20.0976 Y=20.1833 Z=0
    g86: Ellipse CenterX=-22.8436 CenterY=20.1783 CenterZ=0 NormalX=0 NormalY=0 NormalZ=1 MajorRadius=6.93002 MinorRadius=6.36273 AngleXU=-3.13976
    g87: LineSegment StartX=-101.889 StartY=14.1107 StartZ=0 EndX=-97.7455 EndY=14.1107 EndZ=0
    g88: LineSegment StartX=-93.8155 StartY=14.1107 StartZ=0 EndX=-89.6755 EndY=14.1107 EndZ=0
    g89: LineSegment StartX=-85.7455 StartY=14.1107 StartZ=0 EndX=-81.6055 EndY=14.1107 EndZ=0
    g90: LineSegment StartX=-101.889 StartY=14.1107 StartZ=0 EndX=-101.889 EndY=25.9907 EndZ=0
    g91: LineSegment StartX=-101.889 StartY=25.9907 StartZ=0 EndX=-97.8594 EndY=25.9907 EndZ=0
    g92: LineSegment StartX=-97.8594 StartY=25.9907 StartZ=0 EndX=-97.8594 EndY=24.0907 EndZ=0
    g93: LineSegment StartX=-97.7455 StartY=14.1107 StartZ=0 EndX=-97.7455 EndY=19.9107 EndZ=0
    g94: LineSegment StartX=-89.6755 StartY=14.1107 StartZ=0 EndX=-89.6755 EndY=19.9107 EndZ=0
    g95: LineSegment StartX=-93.8155 StartY=14.1107 StartZ=0 EndX=-93.8155 EndY=21.0107 EndZ=0
    g96-g106: Circle x11 (B-spline internal-alignment scaffolding for g107; pole/knot coordinates omitted)
    g107: BSplineCurve PolesCount=11 KnotsCount=9 Degree=3 IsPeriodic=0
    g108-g116: GeomPoint x9 (B-spline internal-alignment scaffolding for g107; pole/knot coordinates omitted)
    g117: BSplineCurve PolesCount=11 KnotsCount=9 Degree=3 IsPeriodic=0
    g118-g125: Circle x8 (B-spline internal-alignment scaffolding for g126; pole/knot coordinates omitted)
    g126: BSplineCurve PolesCount=8 KnotsCount=6 Degree=3 IsPeriodic=0
    g127-g132: GeomPoint x6 (B-spline internal-alignment scaffolding for g126; pole/knot coordinates omitted)
    g133: BSplineCurve PolesCount=8 KnotsCount=6 Degree=3 IsPeriodic=0
    g134: LineSegment StartX=-85.7455 StartY=21.0107 StartZ=0 EndX=-85.7455 EndY=14.1107 EndZ=0
    g135: LineSegment StartX=-80.0879 StartY=14.1107 StartZ=0 EndX=-75.944 EndY=14.1107 EndZ=0
    g136: LineSegment StartX=-72.014 StartY=14.1107 StartZ=0 EndX=-67.874 EndY=14.1107 EndZ=0
    g137: LineSegment StartX=-63.944 StartY=14.1107 StartZ=0 EndX=-59.804 EndY=14.1107 EndZ=0
    g138: LineSegment StartX=-80.0879 StartY=14.1107 StartZ=0 EndX=-80.0879 EndY=25.9907 EndZ=0
    g139: LineSegment StartX=-80.0879 StartY=25.9907 StartZ=0 EndX=-76.0579 EndY=25.9907 EndZ=0
    g140: LineSegment StartX=-76.0579 StartY=25.9907 StartZ=0 EndX=-76.0579 EndY=24.0907 EndZ=0
    g141: LineSegment StartX=-75.944 StartY=14.1107 StartZ=0 EndX=-75.944 EndY=19.9107 EndZ=0
    g142: LineSegment StartX=-67.874 StartY=14.1107 StartZ=0 EndX=-67.874 EndY=19.9107 EndZ=0
    g143: LineSegment StartX=-72.014 StartY=14.1107 StartZ=0 EndX=-72.014 EndY=21.0107 EndZ=0
    g144-g148: Circle x5 (B-spline internal-alignment scaffolding for g149; pole/knot coordinates omitted)
    g149: BSplineCurve PolesCount=11 KnotsCount=9 Degree=3 IsPeriodic=0
    g150-g158: GeomPoint x9 (B-spline internal-alignment scaffolding for g149; pole/knot coordinates omitted)
    g159: BSplineCurve PolesCount=11 KnotsCount=9 Degree=3 IsPeriodic=0
    g160-g167: Circle x8 (B-spline internal-alignment scaffolding for g168; pole/knot coordinates omitted)
    g168: BSplineCurve PolesCount=8 KnotsCount=6 Degree=3 IsPeriodic=0
    g169-g174: GeomPoint x6 (B-spline internal-alignment scaffolding for g168; pole/knot coordinates omitted)
    g175: BSplineCurve PolesCount=8 KnotsCount=6 Degree=3 IsPeriodic=0
    g176: LineSegment StartX=-63.944 StartY=21.0107 StartZ=0 EndX=-63.944 EndY=14.1107 EndZ=0
    g177: LineSegment StartX=-59.804 StartY=14.1107 StartZ=0 EndX=-59.804 EndY=21.5868 EndZ=0
    g178: BSplineCurve PolesCount=4 KnotsCount=2 Degree=3 IsPeriodic=0
    g179: GeomPoint X=-59.804 Y=21.5868 Z=0
    g180: GeomPoint X=-60.2379 Y=24.0907 Z=0
    g181: LineSegment StartX=-81.6055 StartY=14.1107 StartZ=0 EndX=-81.6055 EndY=21.5868 EndZ=0
    g182: LineSegment StartX=-151.619 StartY=24.0313 StartZ=0 EndX=-145.128 EndY=24.0313 EndZ=0
    g183: Circle CenterX=-82.0394 CenterY=24.0907 CenterZ=0 NormalX=0 NormalY=0 NormalZ=1 AngleXU=0 Radius=1
    g184: Circle CenterX=-81.7131 CenterY=23.2736 CenterZ=0 NormalX=0 NormalY=0 NormalZ=1 AngleXU=0 Radius=1
    g185: Circle CenterX=-81.6055 CenterY=21.5868 CenterZ=0 NormalX=0 NormalY=0 NormalZ=1 AngleXU=0 Radius=1
    g186: BSplineCurve PolesCount=3 KnotsCount=2 Degree=2 IsPeriodic=0
    g187: GeomPoint X=-82.0394 Y=24.0907 Z=0
    g188: GeomPoint X=-81.6055 Y=21.5868 Z=0
    g189: Ellipse CenterX=-37.3522 CenterY=19.9515 CenterZ=0 NormalX=0 NormalY=0 NormalZ=1 MajorRadius=2.99755 MinorRadius=2.49 AngleXU=1.5708
    g190: GeomPoint X=-37.3522 Y=21.6203 Z=0
    g191: GeomPoint X=-37.3522 Y=18.2826 Z=0
    g192: ArcOfEllipse CenterX=-38.7647 CenterY=20.06 CenterZ=0 NormalX=0 NormalY=0 NormalZ=1 MajorRadius=6.30025 MinorRadius=5.3849 AngleXU=1.57276 StartAngle=5.50632 EndAngle=10.3035
    g193: GeomPoint X=-38.7711 Y=23.3304 Z=0
    g194: GeomPoint X=-38.7583 Y=16.7895 Z=0
    g195: LineSegment StartX=-34.6109 StartY=14.1107 StartZ=0 EndX=-30.8984 EndY=14.1107 EndZ=0
    g196: LineSegment StartX=-30.8984 StartY=14.1107 StartZ=0 EndX=-30.8984 EndY=31.1784 EndZ=0
    g197: LineSegment StartX=-30.8984 StartY=31.1784 StartZ=0 EndX=-34.9984 EndY=31.1784 EndZ=0
    g198: LineSegment StartX=-34.9984 StartY=24.5602 StartZ=0 EndX=-34.9984 EndY=31.1784 EndZ=0
    g199: LineSegment StartX=-34.6109 StartY=16.0476 StartZ=0 EndX=-34.6109 EndY=14.1107 EndZ=0
    g200: LineSegment StartX=-14.8781 StartY=14.1107 StartZ=0 EndX=-10.5106 EndY=14.1107 EndZ=0
    g201: LineSegment StartX=-14.8781 StartY=14.1107 StartZ=0 EndX=-14.8781 EndY=25.8504 EndZ=0
    g202: LineSegment StartX=-14.8781 StartY=25.8504 StartZ=0 EndX=-10.8534 EndY=25.8504 EndZ=0
    g203: LineSegment StartX=-10.8534 StartY=25.8504 StartZ=0 EndX=-10.8534 EndY=24.0923 EndZ=0
    g204: LineSegment StartX=-10.5106 StartY=14.1107 StartZ=0 EndX=-10.5106 EndY=19.7752 EndZ=0
    g205: LineSegment StartX=-5.96397 StartY=25.9304 StartZ=0 EndX=-5.96397 EndY=22.574 EndZ=0
    g206-g214: Circle x9 (B-spline internal-alignment scaffolding for g215; pole/knot coordinates omitted)
    g215: BSplineCurve PolesCount=9 KnotsCount=7 Degree=3 IsPeriodic=0
    g216-g222: GeomPoint x7 (B-spline internal-alignment scaffolding for g215; pole/knot coordinates omitted)
    g223-g232: Circle x10 (B-spline internal-alignment scaffolding for g233; pole/knot coordinates omitted)
    g233: BSplineCurve PolesCount=10 KnotsCount=8 Degree=3 IsPeriodic=0
    g234-g241: GeomPoint x8 (B-spline internal-alignment scaffolding for g233; pole/knot coordinates omitted)
    g242: LineSegment StartX=-1.58923 StartY=21.0696 StartZ=0 EndX=2.62034 EndY=21.0696 EndZ=0
    g243: LineSegment StartX=-1.55856 StartY=18.7342 StartZ=0 EndX=6.45946 EndY=18.7342 EndZ=0
    g244: LineSegment StartX=5.29231 StartY=17.386 StartZ=0 EndX=5.29231 EndY=14.3674 EndZ=0
    g245-g269: Circle x25 (B-spline internal-alignment scaffolding for g270; pole/knot coordinates omitted)
    g270: BSplineCurve PolesCount=25 KnotsCount=23 Degree=3 IsPeriodic=0
    g271-g293: GeomPoint x23 (B-spline internal-alignment scaffolding for g270; pole/knot coordinates omitted)
    g294-g304: Circle x11 (B-spline internal-alignment scaffolding for g305; pole/knot coordinates omitted)
    g305: BSplineCurve PolesCount=11 KnotsCount=9 Degree=3 IsPeriodic=0
    g306-g314: GeomPoint x9 (B-spline internal-alignment scaffolding for g305; pole/knot coordinates omitted)
    g315-g326: Circle x12 (B-spline internal-alignment scaffolding for g327; pole/knot coordinates omitted)
    g327: BSplineCurve PolesCount=12 KnotsCount=10 Degree=3 IsPeriodic=0
    g328-g337: GeomPoint x10 (B-spline internal-alignment scaffolding for g327; pole/knot coordinates omitted)
  constraints (252):
    c: Coincident(g1,g0)
    c: Horizontal(g0)
    c: Vertical(g1)
    c: Coincident(g2,g3)
    c: Coincident(g3,g4)
    c: Horizontal(g4)
    c: Horizontal(g2)
    c: Vertical(g3)
    c: Block(g1)
    c: Distance(g3) = 4.86
    c: Block(g4)
    c: Distance(g0) = 10.8
    c: Distance(g2) = 10.8
    c: Coincident(g5,g0)
    c: Coincident(g6,g4)
    c: Coincident(g6,g2)
    c: Block(g8)
    c: Block(g7)
    c: Coincident(g9,g8)
    c: Coincident(g9,g7)
    c: Vertical(g9)
    c: Coincident(g10,g7)
    c: Coincident(g10,g8)
    c: Vertical(g10)
    c: Weight(g11) = 1
    c: Equal(g11, g12-g21) x10
    c: InternalAlignment(g11-g21 -> g22) x11
    c: InternalAlignment(g23-g31 -> g22) x9
    c: Block(g22)
    c: Weight(g32) = 1
    c: Equal(g32, g33-g49) x17
    c: InternalAlignment(g32-g49 -> g50) x18
    c: InternalAlignment(g51-g66 -> g50) x16
    c: Block(g50)
    c: Coincident(g67,g50)
    c: Coincident(g67,g22)
    c: Coincident(g68,g22)
    c: Coincident(g68,g50)
    c: InternalAlignment(g70,g69)
    c: InternalAlignment(g71,g69)
    c: Block(g69)
    c: InternalAlignment(g73,g72)
    c: InternalAlignment(g74,g72)
    c: Block(g72)
    c: InternalAlignment(g76,g75)
    c: InternalAlignment(g77,g75)
    c: InternalAlignment(g78,g80)
    c: InternalAlignment(g79,g80)
    c: Block(g80)
    c: Coincident(g75,g80)
    c: Block(g75)
    c: InternalAlignment(g82,g81)
    c: InternalAlignment(g83,g81)
    c: InternalAlignment(g84,g86)
    c: InternalAlignment(g85,g86)
    c: Block(g86)
    c: Coincident(g81,g86)
    c: Block(g81)
    c: Horizontal(g87)
    c: Block(g87)
    c: Horizontal(g88)
    c: Distance(g88) = 4.14
    c: Horizontal(g89)
    c: Equal(g88,g89) = 4.14
    c: Block(g89)
    c: Block(g88)
    c: Coincident(g90,g87)
    c: Vertical(g90)
    c: Distance(g90) = 11.88
    c: Coincident(g91,g90)
    c: Horizontal(g91)
    c: Coincident(g92,g91)
    c: Vertical(g92)
    c: Distance(g91) = 4.03
    c: Distance(g92) = 1.9
    c: Coincident(g93,g87)
    c: Vertical(g93)
    c: Vertical(g94)
    c: Coincident(g94,g88)
    c: Distance(g93) = 5.8
    c: Distance(g94) = 5.8
    c: Vertical(g95)
    c: Coincident(g95,g88)
    c: Distance(g95) = 6.9
    c: Coincident(g107,g92)
    c: Weight(g96) = 1
    c: Equal(g96, g97-g106) x10
    c: InternalAlignment(g96-g106 -> g107) x11
    c: InternalAlignment(g108-g116 -> g107) x9
    c: Block(g107)
    c: Block(g117)
    c: Coincident(g126,g93)
    c: Weight(g118) = 1
    c: Equal(g118, g119-g125) x7
    c: Coincident(g126,g95)
    c: InternalAlignment(g118-g125 -> g126) x8
    c: InternalAlignment(g127-g132 -> g126) x6
    c: Coincident(g133,g94)
    c: Block(g126)
    c: Block(g133)
    c: Coincident(g134,g133)
    c: Coincident(g134,g89)
    c: Vertical(g134)
    c: Horizontal(g135)
    c: Block(g135)
    c: Horizontal(g136)
    c: Equal(g88,g136) = 4.14
    c: Horizontal(g137)
    c: Equal(g136,g137) = 4.14
    c: Block(g137)
    c: Block(g136)
    c: Coincident(g138,g135)
    c: Vertical(g138)
    c: Equal(g90,g138) = 11.88
    c: Coincident(g139,g138)
    c: Horizontal(g139)
    c: Coincident(g140,g139)
    c: Vertical(g140)
    c: Equal(g91,g139) = 4.03
    c: Equal(g92,g140) = 1.9
    c: Coincident(g141,g135)
    c: Vertical(g141)
    c: Vertical(g142)
    c: Coincident(g142,g136)
    c: Equal(g93,g141) = 5.8
    c: Equal(g94,g142) = 5.8
    c: Vertical(g143)
    c: Coincident(g143,g136)
    c: Equal(g95,g143) = 6.9
    c: Coincident(g149,g140)
    c: Equal(g96,g144) = 1
    c: Equal(g144, g145-g148) x4
    c: InternalAlignment(g144-g148 -> g149) x5
    c: InternalAlignment(g150-g158 -> g149) x9
    c: Block(g149)
    c: Block(g159)
    c: Coincident(g168,g141)
    c: Equal(g118,g160) = 1
    c: Equal(g160, g161-g167) x7
    c: Coincident(g168,g143)
    c: InternalAlignment(g160-g167 -> g168) x8
    c: InternalAlignment(g169-g174 -> g168) x6
    c: Coincident(g175,g142)
    c: Block(g168)
    c: Block(g175)
    c: Coincident(g176,g175)
    c: Coincident(g176,g137)
    c: Vertical(g176)
    c: Coincident(g177,g137)
    c: Vertical(g177)
    c: Coincident(g178,g177)
    c: Coincident(g178,g159)
    c: InternalAlignment(g179,g178)
    c: InternalAlignment(g180,g178)
    c: Block(g178)
    c: Vertical(g181)
    c: Coincident(g181,g89)
    c: Block(g5)
    c: Coincident(g182,g1)
    c: Coincident(g182,g5)
    c: Horizontal(g182)
    c: Coincident(g186,g117)
    c: Weight(g183) = 1
    c: Equal(g183,g184)
    c: Equal(g183,g185)
    c: Coincident(g186,g181)
    c: InternalAlignment(g183,g186)
    c: InternalAlignment(g184,g186)
    c: InternalAlignment(g185,g186)
    c: InternalAlignment(g187,g186)
    c: InternalAlignment(g188,g186)
    c: Block(g186)
    c: InternalAlignment(g190,g189)
    c: InternalAlignment(g191,g189)
    c: Block(g189)
    c: InternalAlignment(g193,g192)
    c: InternalAlignment(g194,g192)
    c: Block(g192)
    c: Horizontal(g195)
    c: Block(g195)
    c: Coincident(g196,g195)
    c: Vertical(g196)
    c: Block(g196)
    c: Distance(g195) = 3.71244
    c: Coincident(g197,g196)
    c: Horizontal(g197)
    c: Distance(g197) = 4.1
    c: Coincident(g198,g192)
    c: Coincident(g198,g197)
    c: Vertical(g198)
    c: Block(g198)
    c: Coincident(g199,g192)
    c: Coincident(g199,g195)
    c: Vertical(g199)
    c: Block(g199)
    c: Horizontal(g200)
    c: Block(g200)
    c: Coincident(g201,g200)
    c: Vertical(g201)
    c: Block(g201)
    c: Coincident(g202,g201)
    c: Horizontal(g202)
    c: Block(g202)
    c: Coincident(g203,g202)
    c: Vertical(g203)
    c: Block(g203)
    c: Coincident(g204,g200)
    c: Vertical(g204)
    c: Block(g204)
    c: Coincident(g215,g203)
    c: Weight(g206) = 1
    c: Equal(g206, g207-g214) x8
    c: Coincident(g215,g205)
    c: InternalAlignment(g206-g214 -> g215) x9
    c: InternalAlignment(g216-g222 -> g215) x7
    c: Coincident(g233,g204)
    c: Weight(g223) = 1
    c: Equal(g223, g224-g232) x9
    c: Coincident(g233,g205)
    c: InternalAlignment(g223-g232 -> g233) x10
    c: InternalAlignment(g234-g241 -> g233) x8
    c: Vertical(g205)
    c: Block(g205)
    c: Block(g215)
    c: Block(g233)
    c: Horizontal(g242)
    c: Horizontal(g243)
    c: Block(g242)
    c: Block(g243)
    c: Vertical(g244)
    c: Block(g244)
    c: Coincident(g270,g243)
    c: Weight(g245) = 1
    c: Equal(g245, g246-g269) x24
    c: Coincident(g270,g244)
    c: InternalAlignment(g245-g269 -> g270) x25
    c: InternalAlignment(g271-g293 -> g270) x23
    c: Coincident(g305,g242)
    c: Weight(g294) = 1
    c: Equal(g294, g295-g304) x10
    c: Coincident(g305,g242)
    c: InternalAlignment(g294-g304 -> g305) x11
    c: InternalAlignment(g306-g314 -> g305) x9
    c: Block(g305)
    c: Coincident(g327,g243)
    c: Weight(g315) = 1
    c: Equal(g315, g316-g326) x11
    c: Coincident(g327,g244)
    c: InternalAlignment(g315-g326 -> g327) x12
    c: InternalAlignment(g328-g337 -> g327) x10
    c: Block(g327)
    c: Block(g270)
FEATURE [Part::Extrusion] Extrude075  label="CommodoreLogoAndText002"
  Base = -> Sketch084
  Dir = (0,0,1)
  DirMode = 2
  FaceMakerClass = Part::FaceMakerBullseye
  LengthFwd = 10
  LengthRev = 0
  Solid = true
  Symmetric = false
FEATURE [Part::FeaturePython] Clone001  label="CommodoreLogoAndTextScale001"  # Draft clone (typed FeaturePython)
  AttacherType = Attacher::AttachEngine3D
  Fuse = false
  Objects = -> [Extrude075]
  Placement = pos=(112.566,5.37,73.6) rot=(0,0,1;0rad)
  Scale = (0.62,0.62,1)
FEATURE [Part::Cut] Cut073  label="sideA005"
  Base = -> Extrude002
  Tool = -> Part__Mirroring
FEATURE [Part::Cut] Cut074  label="sideB005"
  Base = -> Extrude028
  Tool = -> Clone001
FEATURE [Sketcher::SketchObject] Sketch085
  FullyConstrained = true
  Placement = pos=(0,0,0) rot=(-1,0,0;4.71239rad)
  sketch-geometry (10):
    g0: LineSegment StartX=0 StartY=0 StartZ=0 EndX=-7 EndY=0 EndZ=0
    g1: LineSegment StartX=-7 StartY=10 StartZ=0 EndX=-6.5 EndY=10 EndZ=0
    g2: LineSegment StartX=0 StartY=10 StartZ=0 EndX=-0.5 EndY=10 EndZ=0
    g3: ArcOfCircle CenterX=-3.5 CenterY=10 CenterZ=0 NormalX=0 NormalY=0 NormalZ=1 AngleXU=0 Radius=3 StartAngle=3.14159 EndAngle=6.28319
    g4: LineSegment StartX=-7 StartY=0 StartZ=0 EndX=-10.5 EndY=0 EndZ=0
    g5: LineSegment StartX=0 StartY=0 StartZ=0 EndX=3.5 EndY=0 EndZ=0
    g6: ArcOfCircle CenterX=-10.5 CenterY=3.5 CenterZ=0 NormalX=0 NormalY=0 NormalZ=1 AngleXU=0 Radius=3.5 StartAngle=4.71239 EndAngle=6.28319
    g7: ArcOfCircle CenterX=3.5 CenterY=3.5 CenterZ=0 NormalX=0 NormalY=0 NormalZ=1 AngleXU=0 Radius=3.5 StartAngle=3.14159 EndAngle=4.71239
    g8: LineSegment StartX=-7 StartY=3.5 StartZ=0 EndX=-7 EndY=10 EndZ=0
    g9: LineSegment StartX=0 StartY=10 StartZ=0 EndX=0 EndY=3.5 EndZ=0
  constraints (26):
    c: Coincident(g0,g-1)
    c: Horizontal(g0)
    c: Distance(g0) = 7
    c: Horizontal(g1)
    c: Distance(g1) = 0.5
    c: Horizontal(g2)
    c: Distance(g2) = 0.5
    c: Coincident(g3,g1)
    c: Coincident(g3,g2)
    c: Block(g3)
    c: Coincident(g4,g0)
    c: Horizontal(g4)
    c: Distance(g4) = 3.5
    c: Coincident(g5,g0)
    c: Distance(g5) = 3.5
    c: Horizontal(g5)
    c: Coincident(g6,g4)
    c: Block(g6)
    c: Coincident(g7,g5)
    c: Block(g7)
    c: Coincident(g8,g6)
    c: Coincident(g8,g1)
    c: Vertical(g8)
    c: Coincident(g9,g2)
    c: Coincident(g9,g7)
    c: Vertical(g9)
FEATURE [Part::Extrusion] Extrude076  label="backRightCasePillarSideBracket"
  Base = -> Sketch085
  Dir = (0,-1,3e-16)
  DirMode = 2
  FaceMakerClass = Part::FaceMakerBullseye
  LengthFwd = 6.7
  LengthRev = 0
  Placement = pos=(16,11.5,0) rot=(0,0,1;0rad)
  Solid = true
  Symmetric = false
FEATURE [Sketcher::SketchObject] Sketch086
  FullyConstrained = true
  Placement = pos=(0,0,0) rot=(1,0,0;1.5708rad)
  sketch-geometry (10):
    g0: LineSegment StartX=0 StartY=0 StartZ=0 EndX=-7 EndY=0 EndZ=0
    g1: LineSegment StartX=-7 StartY=10 StartZ=0 EndX=-6.5 EndY=10 EndZ=0
    g2: LineSegment StartX=0 StartY=10 StartZ=0 EndX=-0.5 EndY=10 EndZ=0
    g3: ArcOfCircle CenterX=-3.5 CenterY=10 CenterZ=0 NormalX=0 NormalY=0 NormalZ=1 AngleXU=0 Radius=3 StartAngle=3.14159 EndAngle=6.28319
    g4: LineSegment StartX=-7 StartY=0 StartZ=0 EndX=-10.5 EndY=0 EndZ=0
    g5: LineSegment StartX=0 StartY=0 StartZ=0 EndX=3.5 EndY=0 EndZ=0
    g6: ArcOfCircle CenterX=-10.5 CenterY=3.5 CenterZ=0 NormalX=0 NormalY=0 NormalZ=1 AngleXU=0 Radius=3.5 StartAngle=4.71239 EndAngle=6.28319
    g7: ArcOfCircle CenterX=3.5 CenterY=3.5 CenterZ=0 NormalX=0 NormalY=0 NormalZ=1 AngleXU=0 Radius=3.5 StartAngle=3.14159 EndAngle=4.71239
    g8: LineSegment StartX=-7 StartY=3.5 StartZ=0 EndX=-7 EndY=10 EndZ=0
    g9: LineSegment StartX=0 StartY=10 StartZ=0 EndX=0 EndY=3.5 EndZ=0
  constraints (26):
    c: Coincident(g0,g-1)
    c: Horizontal(g0)
    c: Distance(g0) = 7
    c: Horizontal(g1)
    c: Distance(g1) = 0.5
    c: Horizontal(g2)
    c: Distance(g2) = 0.5
    c: Coincident(g3,g1)
    c: Coincident(g3,g2)
    c: Block(g3)
    c: Coincident(g4,g0)
    c: Horizontal(g4)
    c: Distance(g4) = 3.5
    c: Coincident(g5,g0)
    c: Distance(g5) = 3.5
    c: Horizontal(g5)
    c: Coincident(g6,g4)
    c: Block(g6)
    c: Coincident(g7,g5)
    c: Block(g7)
    c: Coincident(g8,g6)
    c: Coincident(g8,g1)
    c: Vertical(g8)
    c: Coincident(g9,g2)
    c: Coincident(g9,g7)
    c: Vertical(g9)
FEATURE [Part::Extrusion] Extrude077  label="backLeftCasePillarSideBracket001"
  Base = -> Sketch086
  Dir = (0,-1,3e-16)
  DirMode = 2
  FaceMakerClass = Part::FaceMakerBullseye
  LengthFwd = 6.7
  LengthRev = 0
  Placement = pos=(9,11.5,72) rot=(0,1,0;3.14159rad)
  Solid = true
  Symmetric = false
FEATURE [Sketcher::SketchObject] Sketch087
  FullyConstrained = true
  Placement = pos=(0,0,0) rot=(1,0,0;1.5708rad)
  sketch-geometry (8):
    g0: LineSegment StartX=0 StartY=4e-16 StartZ=0 EndX=-7 EndY=4e-16 EndZ=0
    g1: LineSegment StartX=-7 StartY=4e-16 StartZ=0 EndX=-10.5 EndY=4e-16 EndZ=0
    g2: LineSegment StartX=0 StartY=4e-16 StartZ=0 EndX=3.5 EndY=4e-16 EndZ=0
    g3: ArcOfCircle CenterX=-10.5 CenterY=3.5 CenterZ=0 NormalX=0 NormalY=0 NormalZ=1 AngleXU=0 Radius=3.5 StartAngle=4.71239 EndAngle=6.28319
    g4: ArcOfCircle CenterX=3.5 CenterY=3.5 CenterZ=0 NormalX=0 NormalY=0 NormalZ=1 AngleXU=0 Radius=3.5 StartAngle=3.14159 EndAngle=4.71239
    g5: ArcOfCircle CenterX=-3.5 CenterY=3.5 CenterZ=0 NormalX=0 NormalY=0 NormalZ=1 AngleXU=0 Radius=3 StartAngle=3.14159 EndAngle=6.28319
    g6: LineSegment StartX=-7 StartY=3.5 StartZ=0 EndX=-6.5 EndY=3.5 EndZ=0
    g7: LineSegment StartX=-0.5 StartY=3.5 StartZ=0 EndX=0 EndY=3.5 EndZ=0
  constraints (20):
    c: Coincident(g0,g-1)
    c: Horizontal(g0)
    c: Distance(g0) = 7
    c: Coincident(g1,g0)
    c: Horizontal(g1)
    c: Distance(g1) = 3.5
    c: Coincident(g2,g0)
    c: Distance(g2) = 3.5
    c: Horizontal(g2)
    c: Coincident(g3,g1)
    c: Block(g3)
    c: Coincident(g4,g2)
    c: Block(g4)
    c: Horizontal(g6)
    c: Coincident(g5,g6)
    c: Block(g5)
    c: Coincident(g6,g3)
    c: Coincident(g7,g5)
    c: Coincident(g7,g4)
    c: Horizontal(g7)
FEATURE [Part::Extrusion] Extrude078  label="frontBackLeftCasePillarSideBracket001"
  Base = -> Sketch087
  Dir = (0,-1,2e-16)
  DirMode = 2
  FaceMakerClass = Part::FaceMakerBullseye
  LengthFwd = 6.7
  LengthRev = 0
  Placement = pos=(93,11.5,0) rot=(0,0,1;0rad)
  Solid = true
  Symmetric = false
FEATURE [Sketcher::SketchObject] Sketch088
  FullyConstrained = true
  Placement = pos=(0,0,0) rot=(1,0,0;1.5708rad)
  sketch-geometry (8):
    g0: LineSegment StartX=0 StartY=4e-16 StartZ=0 EndX=-7 EndY=4e-16 EndZ=0
    g1: LineSegment StartX=-7 StartY=4e-16 StartZ=0 EndX=-10.5 EndY=4e-16 EndZ=0
    g2: LineSegment StartX=0 StartY=4e-16 StartZ=0 EndX=3.5 EndY=4e-16 EndZ=0
    g3: ArcOfCircle CenterX=-10.5 CenterY=3.5 CenterZ=0 NormalX=0 NormalY=0 NormalZ=1 AngleXU=0 Radius=3.5 StartAngle=4.71239 EndAngle=6.28319
    g4: ArcOfCircle CenterX=3.5 CenterY=3.5 CenterZ=0 NormalX=0 NormalY=0 NormalZ=1 AngleXU=0 Radius=3.5 StartAngle=3.14159 EndAngle=4.71239
    g5: ArcOfCircle CenterX=-3.5 CenterY=3.5 CenterZ=0 NormalX=0 NormalY=0 NormalZ=1 AngleXU=0 Radius=3 StartAngle=3.14159 EndAngle=6.28319
    g6: LineSegment StartX=-7 StartY=3.5 StartZ=0 EndX=-6.5 EndY=3.5 EndZ=0
    g7: LineSegment StartX=-0.5 StartY=3.5 StartZ=0 EndX=0 EndY=3.5 EndZ=0
  constraints (20):
    c: Coincident(g0,g-1)
    c: Horizontal(g0)
    c: Distance(g0) = 7
    c: Coincident(g1,g0)
    c: Horizontal(g1)
    c: Distance(g1) = 3.5
    c: Coincident(g2,g0)
    c: Distance(g2) = 3.5
    c: Horizontal(g2)
    c: Coincident(g3,g1)
    c: Block(g3)
    c: Coincident(g4,g2)
    c: Block(g4)
    c: Horizontal(g6)
    c: Coincident(g5,g6)
    c: Block(g5)
    c: Coincident(g6,g3)
    c: Coincident(g7,g5)
    c: Coincident(g7,g4)
    c: Horizontal(g7)
FEATURE [Part::Extrusion] Extrude079  label="frontFrontLeftCasePillarSideBracket002"
  Base = -> Sketch088
  Dir = (0,-1,2e-16)
  DirMode = 2
  FaceMakerClass = Part::FaceMakerBullseye
  LengthFwd = 2
  LengthRev = 0
  Placement = pos=(113,11.5,0) rot=(0,0,1;0rad)
  Solid = true
  Symmetric = false
FEATURE [Part::Chamfer] Chamfer
  Base = -> Extrude076
  Edges = 1 edges r=3: [Edge19]
FEATURE [Part::Chamfer] Chamfer001  label="backRightCasePillarSideBracket001"
  Base = -> Chamfer
  Edges = 1 edges r=3: [Edge23]
FEATURE [Part::Chamfer] Chamfer002
  Base = -> Extrude077
  Edges = 1 edges r=3: [Edge7]
FEATURE [Part::Chamfer] Chamfer003  label="backLeftCasePillarSideBracket002"
  Base = -> Chamfer002
  Edges = 1 edges r=3: [Edge28]
